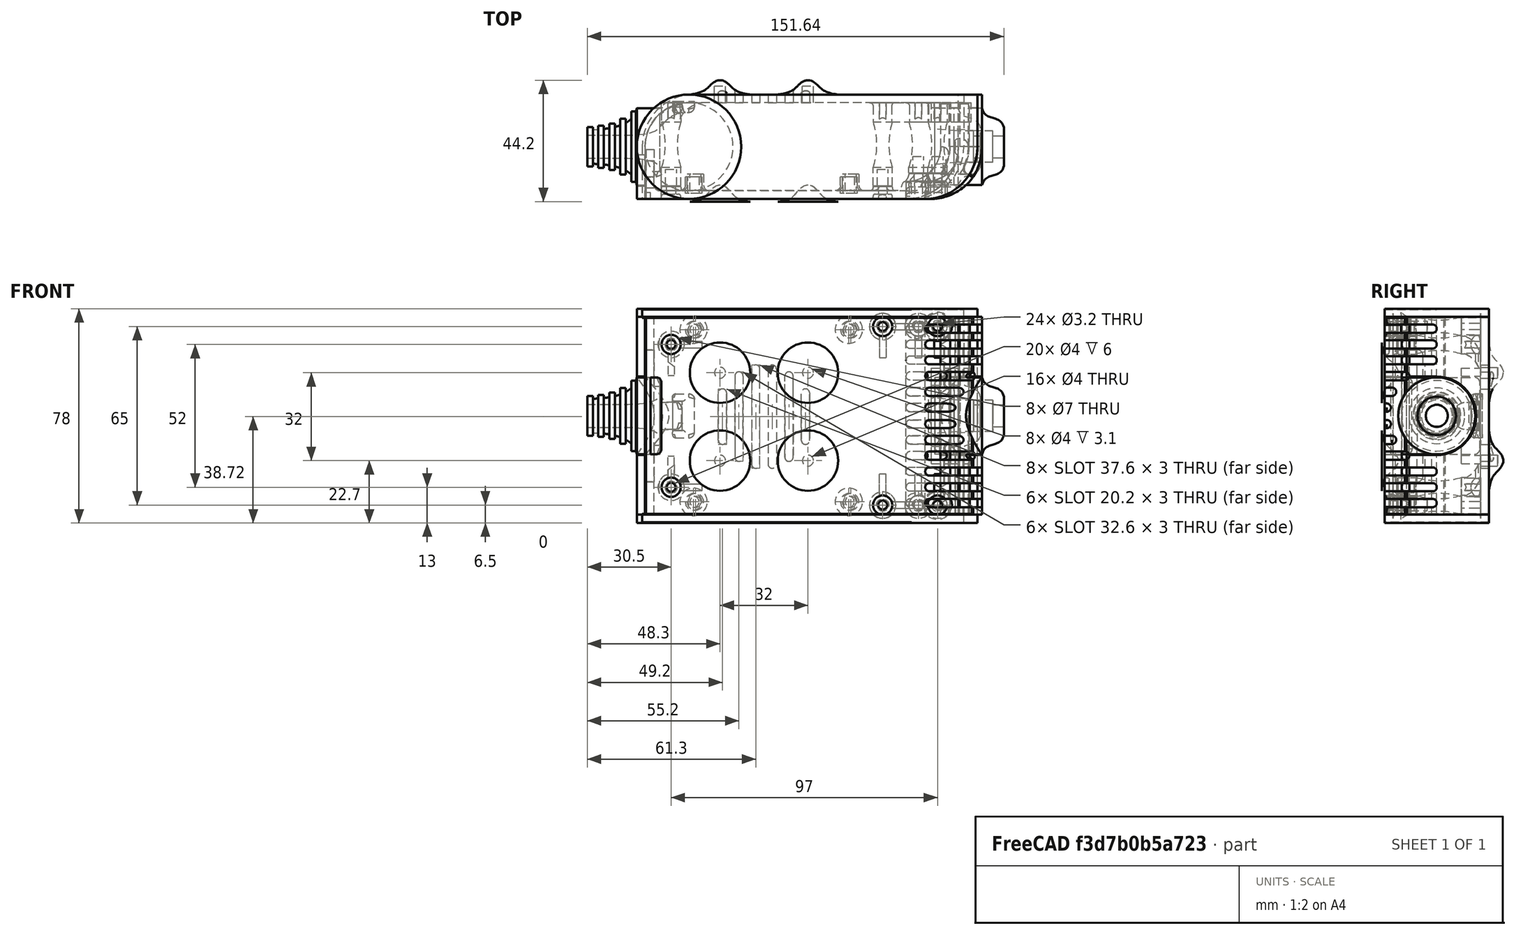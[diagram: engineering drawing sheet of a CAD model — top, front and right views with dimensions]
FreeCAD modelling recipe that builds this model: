
FCSTD DOCUMENT  (FreeCAD 0.19R0.19.2)
Label: enclosure_169FCStd
License: All rights reserved
LicenseURL: http://en.wikipedia.org/wiki/All_rights_reserved
objects: Part::Revolution×146, Part::Feature×140, Part::MultiFuse×134, Sketcher::SketchObject×74, Part::Cylinder×62, Part::Cut×61, Part::Extrusion×59, Part::Fillet×54, Part::Box×36, App::MeasureDistance×4
note: 766 computed .brp shape members not serialized (recipe doc carries the construction recipe); baked Part::Feature solids carry a one-line shape summary decoded from their .brp

FEATURE [Sketcher::SketchObject] Sketch  label="topSketch"
  FullyConstrained = true
  sketch-geometry (20):
    g0: LineSegment StartX=5.21097e-06 StartY=3 StartZ=0 EndX=5.21097e-06 EndY=19 EndZ=0
    g1: ArcOfCircle CenterX=19 CenterY=19 CenterZ=0 NormalX=0 NormalY=0 NormalZ=1 AngleXU=0 Radius=19 StartAngle=1.5708 EndAngle=3.14159
    g2: ArcOfCircle CenterX=19 CenterY=19 CenterZ=0 NormalX=0 NormalY=0 NormalZ=1 AngleXU=0 Radius=16 StartAngle=1.5708 EndAngle=3.14159
    g3: LineSegment StartX=114 StartY=35 StartZ=0 EndX=19 EndY=35 EndZ=0
    g4: LineSegment StartX=5.21097e-06 StartY=3 StartZ=0 EndX=5.21097e-06 EndY=0 EndZ=0
    g5: LineSegment StartX=3 StartY=0 StartZ=0 EndX=5.21097e-06 EndY=0 EndZ=0
    g6: LineSegment StartX=3 StartY=19 StartZ=0 EndX=3 EndY=0 EndZ=0
    g7: LineSegment StartX=19 StartY=38 StartZ=0 EndX=124 EndY=38 EndZ=0
    g8: Circle CenterX=119 CenterY=35 CenterZ=0 NormalX=0 NormalY=0 NormalZ=1 AngleXU=0 Radius=1
    g9: Circle CenterX=121 CenterY=35 CenterZ=0 NormalX=0 NormalY=0 NormalZ=1 AngleXU=0 Radius=1
    g10: Circle CenterX=121 CenterY=33 CenterZ=0 NormalX=0 NormalY=0 NormalZ=1 AngleXU=0 Radius=1
    g11: BSplineCurve PolesCount=3 KnotsCount=2 Degree=2 IsPeriodic=0
    g12: GeomPoint X=119 Y=35 Z=0
    g13: GeomPoint X=121 Y=33 Z=0
    g14: LineSegment StartX=119 StartY=35 StartZ=0 EndX=114 EndY=35 EndZ=0
    g15: ArcOfCircle CenterX=105 CenterY=19 CenterZ=0 NormalX=0 NormalY=0 NormalZ=1 AngleXU=0 Radius=19 StartAngle=5.7297 EndAngle=6.28319
    g16: ArcOfCircle CenterX=105 CenterY=19 CenterZ=0 NormalX=0 NormalY=0 NormalZ=1 AngleXU=0 Radius=16 StartAngle=5.60905 EndAngle=6.28319
    g17: LineSegment StartX=121 StartY=33 StartZ=0 EndX=121 EndY=19 EndZ=0
    g18: LineSegment StartX=124 StartY=38 StartZ=0 EndX=124 EndY=19 EndZ=0
    g19: LineSegment StartX=117.5 StartY=9.01251 StartZ=0 EndX=121.163 EndY=9.0125 EndZ=0
  constraints (46):
    c: Vertical(g0)
    c: Block(g0)
    c: Coincident(g1,g0)
    c: Block(g1)
    c: Coincident(g2,g1)
    c: Block(g2)
    c: Coincident(g3,g2)
    c: Horizontal(g3)
    c: Tangent(g3,g2)
    c: Coincident(g4,g0)
    c: Distance(g4) = 3
    c: Vertical(g4)
    c: Coincident(g5,g4)
    c: Horizontal(g5)
    c: Coincident(g6,g2)
    c: Coincident(g6,g5)
    c: Vertical(g6)
    c: Horizontal(g7)
    c: Distance(g7) = 105
    c: Coincident(g7,g1)
    c: Block(g3)
    c: Weight(g8) = 1
    c: Equal(g8,g9)
    c: Equal(g8,g10)
    c: InternalAlignment(g8,g11)
    c: InternalAlignment(g9,g11)
    c: InternalAlignment(g10,g11)
    c: InternalAlignment(g12,g11)
    c: InternalAlignment(g13,g11)
    c: Block(g11)
    c: Coincident(g14,g11)
    c: Coincident(g14,g3)
    c: Horizontal(g14)
    c: Block(g15)
    c: Coincident(g16,g15)
    c: Block(g16)
    c: Coincident(g17,g11)
    c: Coincident(g17,g16)
    c: Vertical(g17)
    c: Distance(g17) = 14
    c: Coincident(g18,g7)
    c: Coincident(g18,g15)
    c: Vertical(g18)
    c: Distance(g18) = 19
    c: Coincident(g19,g16)
    c: Coincident(g19,g15)
FEATURE [Sketcher::SketchObject] Sketch001  label="bottomSketch"
  FullyConstrained = true
  sketch-geometry (32):
    g0: LineSegment StartX=3.3 StartY=-6.03275e-07 StartZ=0 EndX=98 EndY=-6.03275e-07 EndZ=0
    g1: ArcOfCircle CenterX=98 CenterY=19 CenterZ=0 NormalX=0 NormalY=0 NormalZ=1 AngleXU=0 Radius=19 StartAngle=4.71239 EndAngle=5.71103
    g2: LineSegment StartX=6.3 StartY=8 StartZ=0 EndX=3.3 EndY=8 EndZ=0
    g3: LineSegment StartX=3.3 StartY=8 StartZ=0 EndX=3.3 EndY=-6.03275e-07 EndZ=0
    g4: ArcOfCircle CenterX=8.3 CenterY=5 CenterZ=0 NormalX=0 NormalY=0 NormalZ=1 AngleXU=0 Radius=2 StartAngle=3.14159 EndAngle=4.71239
    g5: LineSegment StartX=6.3 StartY=8 StartZ=0 EndX=6.3 EndY=5 EndZ=0
    g6: ArcOfCircle CenterX=98 CenterY=19 CenterZ=0 NormalX=0 NormalY=0 NormalZ=1 AngleXU=0 Radius=12.7 StartAngle=4.71239 EndAngle=6.28319
    g7: LineSegment StartX=94.7 StartY=3 StartZ=0 EndX=8.3 EndY=3 EndZ=0
    g8-g12: Circle x5 (B-spline internal-alignment scaffolding for g13; pole/knot coordinates omitted)
    g13: BSplineCurve PolesCount=5 KnotsCount=3 Degree=3 IsPeriodic=0
    g14: GeomPoint X=98 Y=6.3 Z=0
    g15: GeomPoint X=96.3938 Y=4.71946 Z=0
    g16: GeomPoint X=94.7 Y=3 Z=0
    g17-g23: Circle x7 (B-spline internal-alignment scaffolding for g24; pole/knot coordinates omitted)
    g24: BSplineCurve PolesCount=7 KnotsCount=5 Degree=3 IsPeriodic=0
    g25-g29: GeomPoint x5 (B-spline internal-alignment scaffolding for g24; pole/knot coordinates omitted)
    g30: ArcOfCircle CenterX=98 CenterY=19 CenterZ=0 NormalX=0 NormalY=0 NormalZ=1 AngleXU=0 Radius=15.7 StartAngle=5.81226 EndAngle=6.28319
    g31: LineSegment StartX=110.7 StartY=19 StartZ=0 EndX=113.7 EndY=19 EndZ=0
  constraints (41):
    c: Horizontal(g0)
    c: Coincident(g1,g0)
    c: Block(g1)
    c: Horizontal(g2)
    c: Distance(g2) = 3
    c: Coincident(g3,g2)
    c: Vertical(g3)
    c: Coincident(g3,g0)
    c: Block(g4)
    c: Block(g2)
    c: Coincident(g5,g2)
    c: Coincident(g5,g4)
    c: Vertical(g5)
    c: Coincident(g6,g1)
    c: Block(g6)
    c: Coincident(g7,g4)
    c: Horizontal(g7)
    c: Block(g0)
    c: Block(g7)
    c: Block(g3)
    c: Coincident(g13,g6)
    c: Weight(g8) = 1
    c: Equal(g8, g9-g12) x4
    c: Coincident(g13,g7)
    c: InternalAlignment(g8-g12 -> g13) x5
    c: InternalAlignment(g14,g13)
    c: InternalAlignment(g15,g13)
    c: InternalAlignment(g16,g13)
    c: Block(g13)
    c: Weight(g17) = 1
    c: Equal(g17, g18-g23) x6
    c: Coincident(g24,g1)
    c: InternalAlignment(g17-g23 -> g24) x7
    c: InternalAlignment(g25-g29 -> g24) x5
    c: Block(g24)
    c: Coincident(g30,g24)
    c: Coincident(g31,g6)
    c: Coincident(g31,g30)
    c: Horizontal(g31)
    c: Block(g31)
    c: Block(g30)
FEATURE [Part::Extrusion] Extrude  label="top"
  Base = -> Sketch
  Dir = (0,0,1)
  DirMode = 2
  FaceMakerClass = Part::FaceMakerBullseye
  LengthFwd = 72
  LengthRev = 0
  Solid = true
  Symmetric = false
FEATURE [Part::Extrusion] Extrude001  label="bottom"
  Base = -> Sketch001
  Dir = (0,0,1)
  DirMode = 2
  FaceMakerClass = Part::FaceMakerBullseye
  LengthFwd = 71.4
  LengthRev = 0
  Placement = pos=(0,0,0.3) rot=(0,0,1;0rad)
  Solid = true
  Symmetric = false
FEATURE [Sketcher::SketchObject] Sketch002  label="topSketch001"
  FullyConstrained = true
  sketch-geometry (6):
    g0: ArcOfCircle CenterX=19 CenterY=19 CenterZ=0 NormalX=0 NormalY=0 NormalZ=1 AngleXU=0 Radius=19 StartAngle=1.5708 EndAngle=3.14159
    g1: LineSegment StartX=5.22862e-06 StartY=19 StartZ=0 EndX=5.22862e-06 EndY=1.19904e-11 EndZ=0
    g2: LineSegment StartX=19 StartY=38 StartZ=0 EndX=124 EndY=38 EndZ=0
    g3: LineSegment StartX=5.22862e-06 StartY=1.19904e-11 StartZ=0 EndX=105 EndY=1.19904e-11 EndZ=0
    g4: ArcOfCircle CenterX=105 CenterY=19 CenterZ=0 NormalX=0 NormalY=0 NormalZ=1 AngleXU=0 Radius=19 StartAngle=4.71239 EndAngle=6.28319
    g5: LineSegment StartX=124 StartY=38 StartZ=0 EndX=124 EndY=19 EndZ=0
  constraints (16):
    c: Block(g0)
    c: Coincident(g1,g0)
    c: Vertical(g1)
    c: Horizontal(g2)
    c: Distance(g2) = 105
    c: Coincident(g2,g0)
    c: Distance(g1) = 19
    c: Coincident(g3,g1)
    c: Horizontal(g3)
    c: Distance(g3) = 105
    c: Block(g4)
    c: Coincident(g4,g3)
    c: Coincident(g5,g2)
    c: Coincident(g5,g4)
    c: Vertical(g5)
    c: Distance(g5) = 19
FEATURE [Part::Extrusion] Extrude002  label="sideA"
  Base = -> Sketch002
  Dir = (0,0,1)
  DirMode = 2
  FaceMakerClass = Part::FaceMakerBullseye
  LengthFwd = 3
  LengthRev = 0
  Placement = pos=(0,0,-3) rot=(0,0,1;0rad)
  Solid = true
  Symmetric = false
FEATURE [Sketcher::SketchObject] Sketch003  label="topSketch002"
  FullyConstrained = true
  sketch-geometry (6):
    g0: LineSegment StartX=19 StartY=38 StartZ=0 EndX=117 EndY=38 EndZ=0
    g1: ArcOfCircle CenterX=19 CenterY=19 CenterZ=0 NormalX=0 NormalY=0 NormalZ=1 AngleXU=0 Radius=19 StartAngle=1.5708 EndAngle=3.14159
    g2: LineSegment StartX=117 StartY=38 StartZ=0 EndX=117 EndY=19 EndZ=0
    g3: LineSegment StartX=98 StartY=1.0161e-12 StartZ=0 EndX=5.22862e-06 EndY=1.0161e-12 EndZ=0
    g4: LineSegment StartX=5.22862e-06 StartY=19 StartZ=0 EndX=5.22862e-06 EndY=1.0161e-12 EndZ=0
    g5: ArcOfCircle CenterX=98 CenterY=19 CenterZ=0 NormalX=0 NormalY=0 NormalZ=1 AngleXU=0 Radius=19 StartAngle=4.71239 EndAngle=6.28319
  constraints (16):
    c: Horizontal(g0)
    c: Distance(g0) = 98
    c: Coincident(g1,g0)
    c: Block(g1)
    c: Coincident(g2,g0)
    c: Vertical(g2)
    c: Distance(g2) = 19
    c: Horizontal(g3)
    c: Coincident(g4,g1)
    c: Vertical(g4)
    c: Coincident(g3,g4)
    c: Block(g3)
    c: Coincident(g5,g2)
    c: Coincident(g5,g3)
    c: Block(g0)
    c: Block(g5)
FEATURE [Sketcher::SketchObject] Sketch004
  FullyConstrained = true
  MapMode = 3
  Placement = pos=(0,0,0) rot=(1,0,0;1.5708rad)
  Support = -> [Extrude]
  sketch-geometry (8):
    g0: Circle CenterX=80.351 CenterY=-67.6202 CenterZ=0 NormalX=0 NormalY=0 NormalZ=1 AngleXU=0 Radius=2
    g1: Circle CenterX=80.351 CenterY=-67.6202 CenterZ=0 NormalX=0 NormalY=0 NormalZ=1 AngleXU=0 Radius=3
    g2: Circle CenterX=80.351 CenterY=-4.92017 CenterZ=0 NormalX=0 NormalY=0 NormalZ=1 AngleXU=0 Radius=2
    g3: Circle CenterX=80.351 CenterY=-4.92017 CenterZ=0 NormalX=0 NormalY=0 NormalZ=1 AngleXU=0 Radius=3
    g4: Circle CenterX=23.851 CenterY=-4.92017 CenterZ=0 NormalX=0 NormalY=0 NormalZ=1 AngleXU=0 Radius=2
    g5: Circle CenterX=23.851 CenterY=-4.92017 CenterZ=0 NormalX=0 NormalY=0 NormalZ=1 AngleXU=0 Radius=3
    g6: Circle CenterX=23.851 CenterY=-67.6202 CenterZ=0 NormalX=0 NormalY=0 NormalZ=1 AngleXU=0 Radius=2
    g7: Circle CenterX=23.851 CenterY=-67.6202 CenterZ=0 NormalX=0 NormalY=0 NormalZ=1 AngleXU=0 Radius=3
  constraints (8):
    c: Block(g3)
    c: Block(g2)
    c: Block(g1)
    c: Block(g0)
    c: Block(g6)
    c: Block(g7)
    c: Block(g4)
    c: Block(g5)
FEATURE [Part::Extrusion] Extrude004
  Base = -> Sketch004
  Dir = (0,-1,2e-16)
  DirMode = 2
  FaceMakerClass = Part::FaceMakerBullseye
  LengthFwd = 6
  LengthRev = 0
  Placement = pos=(0,9,0) rot=(0,0,1;0rad)
  Solid = true
  Symmetric = false
FEATURE [Sketcher::SketchObject] Sketch005
  FullyConstrained = true
  MapMode = 3
  Placement = pos=(0,0,0) rot=(1,0,0;1.5708rad)
  Support = -> [Extrude]
  sketch-geometry (8):
    g0: Circle CenterX=80.351 CenterY=-67.6202 CenterZ=0 NormalX=0 NormalY=0 NormalZ=1 AngleXU=0 Radius=3
    g1: Circle CenterX=80.351 CenterY=-4.92017 CenterZ=0 NormalX=0 NormalY=0 NormalZ=1 AngleXU=0 Radius=3
    g2: Circle CenterX=23.851 CenterY=-4.92017 CenterZ=0 NormalX=0 NormalY=0 NormalZ=1 AngleXU=0 Radius=3
    g3: Circle CenterX=23.851 CenterY=-67.6202 CenterZ=0 NormalX=0 NormalY=0 NormalZ=1 AngleXU=0 Radius=3
    g4: Circle CenterX=23.851 CenterY=-67.6202 CenterZ=0 NormalX=0 NormalY=0 NormalZ=1 AngleXU=0 Radius=5
    g5: Circle CenterX=80.351 CenterY=-67.6202 CenterZ=0 NormalX=0 NormalY=0 NormalZ=1 AngleXU=0 Radius=5
    g6: Circle CenterX=23.851 CenterY=-4.92017 CenterZ=0 NormalX=0 NormalY=0 NormalZ=1 AngleXU=0 Radius=5
    g7: Circle CenterX=80.351 CenterY=-4.92017 CenterZ=0 NormalX=0 NormalY=0 NormalZ=1 AngleXU=0 Radius=5
  constraints (8):
    c: Block(g1)
    c: Block(g0)
    c: Block(g3)
    c: Block(g2)
    c: Block(g5)
    c: Block(g4)
    c: Block(g6)
    c: Block(g7)
FEATURE [Part::Extrusion] Extrude005
  Base = -> Sketch005
  Dir = (0,-1,2e-16)
  DirMode = 2
  FaceMakerClass = Part::FaceMakerBullseye
  LengthFwd = 2
  LengthRev = 0
  Solid = true
  Symmetric = false
FEATURE [Sketcher::SketchObject] Sketch006
  FullyConstrained = true
  MapMode = 3
  Placement = pos=(0,0,0) rot=(1,0,0;1.5708rad)
  sketch-geometry (8):
    g0: Circle CenterX=80.351 CenterY=-67.6202 CenterZ=0 NormalX=0 NormalY=0 NormalZ=1 AngleXU=0 Radius=3
    g1: Circle CenterX=80.351 CenterY=-4.92017 CenterZ=0 NormalX=0 NormalY=0 NormalZ=1 AngleXU=0 Radius=3
    g2: Circle CenterX=23.851 CenterY=-4.92017 CenterZ=0 NormalX=0 NormalY=0 NormalZ=1 AngleXU=0 Radius=3
    g3: Circle CenterX=23.851 CenterY=-67.6202 CenterZ=0 NormalX=0 NormalY=0 NormalZ=1 AngleXU=0 Radius=3
    g4: Circle CenterX=23.851 CenterY=-67.6202 CenterZ=0 NormalX=0 NormalY=0 NormalZ=1 AngleXU=0 Radius=5
    g5: Circle CenterX=80.351 CenterY=-67.6202 CenterZ=0 NormalX=0 NormalY=0 NormalZ=1 AngleXU=0 Radius=5
    g6: Circle CenterX=23.851 CenterY=-4.92017 CenterZ=0 NormalX=0 NormalY=0 NormalZ=1 AngleXU=0 Radius=5
    g7: Circle CenterX=80.351 CenterY=-4.92017 CenterZ=0 NormalX=0 NormalY=0 NormalZ=1 AngleXU=0 Radius=5
  constraints (8):
    c: Block(g1)
    c: Block(g0)
    c: Block(g3)
    c: Block(g2)
    c: Block(g5)
    c: Block(g4)
    c: Block(g6)
    c: Block(g7)
FEATURE [Part::Extrusion] Extrude007
  Base = -> Sketch006
  Dir = (0,-1,2e-16)
  DirMode = 2
  FaceMakerClass = Part::FaceMakerBullseye
  LengthFwd = 2
  LengthRev = 0
  Solid = true
  Symmetric = false
FEATURE [Part::Fillet] Fillet
  Base = -> Extrude007
  Edges = 4 edges r=1.99: [Edge6,Edge12,Edge18,Edge24]
FEATURE [Part::Cut] Cut
  Base = -> Extrude005
  Placement = pos=(0,5,0) rot=(0,0,1;0rad)
  Tool = -> Fillet
FEATURE [Part::MultiFuse] Fusion  label="pCBScrews"
  Placement = pos=(-2.5,0,72.3) rot=(0,0,1;0rad)
  Shapes = -> [Extrude004,Cut]
FEATURE [App::MeasureDistance] Distance  label="Distance: 0.69 mm"
  Distance = 0.685967
  P1 = (24.0138,2.9647,0.3)
  P2 = (23.8901,3,-0.373787)
FEATURE [App::MeasureDistance] Distance001  label="Distance: 0.53 mm"
  Distance = 0.533607
  P1 = (80.2939,3,72.2334)
  P2 = (80.281,2.99661,71.7)
FEATURE [Part::Fillet] Fillet001
  Base = -> Extrude001
  Edges = 1 edges r=2.4: [Edge17]
FEATURE [Part::Fillet] Fillet002  label="bottom001"
  Base = -> Fillet001
  Edges = 1 edges r=2.4: [Edge36]
FEATURE [Part::Fillet] Fillet003  label="top001"
  Base = -> Extrude
  Edges = 1 edges r=2: [Edge1]
FEATURE [Sketcher::SketchObject] Sketch007
  FullyConstrained = true
  sketch-geometry (16):
    g0: LineSegment StartX=4 StartY=0 StartZ=0 EndX=4 EndY=2.4 EndZ=0
    g1: LineSegment StartX=4 StartY=2.4 StartZ=0 EndX=7 EndY=2.4 EndZ=0
    g2: LineSegment StartX=4 StartY=0 StartZ=0 EndX=5.7 EndY=0 EndZ=0
    g3: LineSegment StartX=5.7 StartY=0 StartZ=0 EndX=5.7 EndY=-5.6 EndZ=0
    g4-g8: Circle x5 (B-spline internal-alignment scaffolding for g9; pole/knot coordinates omitted)
    g9: BSplineCurve PolesCount=5 KnotsCount=3 Degree=3 IsPeriodic=0
    g10: GeomPoint X=7 Y=2.4 Z=0
    g11: GeomPoint X=10.4582 Y=-1.55472 Z=0
    g12: GeomPoint X=14 Y=-5.6 Z=0
    g13: LineSegment StartX=14 StartY=-5.6 StartZ=0 EndX=14 EndY=-14.1 EndZ=0
    g14: LineSegment StartX=14 StartY=-14.1 StartZ=0 EndX=6.5 EndY=-14.1 EndZ=0
    g15: LineSegment StartX=5.7 StartY=-5.6 StartZ=0 EndX=6.5 EndY=-14.1 EndZ=0
  constraints (28):
    c: Distance(g0) = 2.4
    c: Vertical(g0)
    c: Block(g0)
    c: Coincident(g1,g0)
    c: Horizontal(g1)
    c: Distance(g1) = 3
    c: Coincident(g2,g0)
    c: Horizontal(g2)
    c: Distance(g2) = 1.7
    c: Coincident(g3,g2)
    c: Vertical(g3)
    c: Distance(g3) = 5.6
    c: Coincident(g9,g1)
    c: Weight(g4) = 1
    c: Equal(g4, g5-g8) x4
    c: InternalAlignment(g4-g8 -> g9) x5
    c: InternalAlignment(g10,g9)
    c: InternalAlignment(g11,g9)
    c: InternalAlignment(g12,g9)
    c: Block(g9)
    c: Coincident(g13,g9)
    c: Vertical(g13)
    c: Distance(g13) = 8.5
    c: Coincident(g14,g13)
    c: Horizontal(g14)
    c: Distance(g14) = 7.5
    c: Coincident(g15,g3)
    c: Coincident(g15,g14)
FEATURE [Part::Feature] Face
  shape: bbox 10 x 16.5 x 2e-07 mm, 1 faces, 0 solids (baked)
FEATURE [Part::Revolution] Revolve  label="plugHousing"
  Angle = 360
  Axis = (0,1,0)
  Base = (0,0,0)
  FaceMakerClass = Part::FaceMakerBullseye
  Placement = pos=(0,0,36.15) rot=(0,0,1;0rad)
  Solid = false
  Source = -> Face
  Symmetric = false
FEATURE [Part::Feature] Face001
  shape: bbox 10 x 16.5 x 2e-07 mm, 1 faces, 0 solids (baked)
FEATURE [Part::Revolution] Revolve001  label="plugHousing001"
  Angle = 360
  Axis = (0,1,0)
  Base = (0,0,0)
  FaceMakerClass = Part::FaceMakerBullseye
  Placement = pos=(0,0,36.15) rot=(0,0,1;0rad)
  Solid = false
  Source = -> Face001
  Symmetric = false
FEATURE [Part::MultiFuse] Fusion001  label="plugHousing002"
  Placement = pos=(0,0,0) rot=(0,0,1;1.5708rad)
  Shapes = -> [Revolve001,Revolve]
FEATURE [Part::Feature] Face002
  shape: bbox 10 x 16.5 x 2e-07 mm, 1 faces, 0 solids (baked)
FEATURE [Part::Revolution] Revolve003  label="plugHousing005"
  Angle = 360
  Axis = (0,1,0)
  Base = (0,0,0)
  FaceMakerClass = Part::FaceMakerBullseye
  Placement = pos=(0,0,36.15) rot=(0,0,1;0rad)
  Solid = false
  Source = -> Face002
  Symmetric = false
FEATURE [Part::Feature] Face003
  shape: bbox 10 x 16.5 x 2e-07 mm, 1 faces, 0 solids (baked)
FEATURE [Part::Revolution] Revolve002  label="plugHousing003"
  Angle = 360
  Axis = (0,1,0)
  Base = (0,0,0)
  FaceMakerClass = Part::FaceMakerBullseye
  Placement = pos=(0,0,36.15) rot=(0,0,1;0rad)
  Solid = false
  Source = -> Face003
  Symmetric = false
FEATURE [Part::MultiFuse] Fusion002  label="plugHousing004"
  Placement = pos=(0,0,0) rot=(0,0,1;1.5708rad)
  Shapes = -> [Revolve002,Revolve003]
FEATURE [Part::MultiFuse] Fusion003  label="plugHousing006"
  Placement = pos=(0,19,0) rot=(0,0,1;3.14159rad)
  Shapes = -> [Fusion002,Fusion001]
FEATURE [Part::Feature] Face004
  shape: bbox 10 x 16.5 x 2e-07 mm, 1 faces, 0 solids (baked)
FEATURE [Part::Revolution] Revolve006  label="plugHousing010"
  Angle = 360
  Axis = (0,1,0)
  Base = (0,0,0)
  FaceMakerClass = Part::FaceMakerBullseye
  Placement = pos=(0,0,36.15) rot=(0,0,1;0rad)
  Solid = false
  Source = -> Face004
  Symmetric = false
FEATURE [Part::Feature] Face005
  shape: bbox 10 x 16.5 x 2e-07 mm, 1 faces, 0 solids (baked)
FEATURE [Part::Revolution] Revolve007  label="plugHousing011"
  Angle = 360
  Axis = (0,1,0)
  Base = (0,0,0)
  FaceMakerClass = Part::FaceMakerBullseye
  Placement = pos=(0,0,36.15) rot=(0,0,1;0rad)
  Solid = false
  Source = -> Face005
  Symmetric = false
FEATURE [Part::Feature] Face006
  shape: bbox 10 x 16.5 x 2e-07 mm, 1 faces, 0 solids (baked)
FEATURE [Part::Revolution] Revolve004  label="plugHousing007"
  Angle = 360
  Axis = (0,1,0)
  Base = (0,0,0)
  FaceMakerClass = Part::FaceMakerBullseye
  Placement = pos=(0,0,36.15) rot=(0,0,1;0rad)
  Solid = false
  Source = -> Face006
  Symmetric = false
FEATURE [Part::MultiFuse] Fusion004  label="plugHousing009"
  Placement = pos=(0,0,0) rot=(0,0,1;1.5708rad)
  Shapes = -> [Revolve004,Revolve007]
FEATURE [Part::Feature] Face007
  shape: bbox 10 x 16.5 x 2e-07 mm, 1 faces, 0 solids (baked)
FEATURE [Part::Revolution] Revolve005  label="plugHousing008"
  Angle = 360
  Axis = (0,1,0)
  Base = (0,0,0)
  FaceMakerClass = Part::FaceMakerBullseye
  Placement = pos=(0,0,36.15) rot=(0,0,1;0rad)
  Solid = false
  Source = -> Face007
  Symmetric = false
FEATURE [Part::MultiFuse] Fusion005  label="plugHousing012"
  Placement = pos=(0,0,0) rot=(0,0,1;1.5708rad)
  Shapes = -> [Revolve006,Revolve005]
FEATURE [Part::MultiFuse] Fusion006  label="plugHousing013"
  Placement = pos=(0,19,0) rot=(0,0,1;3.14159rad)
  Shapes = -> [Fusion005,Fusion004]
FEATURE [Part::MultiFuse] Fusion007  label="plugHousing014"
  Placement = pos=(122.621,0,-0.15) rot=(0,0,1;0rad)
  Shapes = -> [Fusion003,Fusion006]
FEATURE [Part::Cylinder] Cylinder002
  Angle = 360
  AttacherType = Attacher::AttachEngine3D
  Height = 20
  Placement = pos=(0,0,36.15) rot=(0,0,1;0rad)
  Radius = 4
FEATURE [Part::Cylinder] Cylinder003
  Angle = 360
  AttacherType = Attacher::AttachEngine3D
  Height = 10
  Placement = pos=(0,0,36.15) rot=(0,0,1;0rad)
  Radius = 4
FEATURE [Part::MultiFuse] Fusion009  label="removeToCreateHoleForPlugHousing"
  Placement = pos=(70,19,36.15) rot=(0,1,0;1.5708rad)
  Shapes = -> [Cylinder002,Cylinder003]
FEATURE [Part::Cylinder] Cylinder004
  Angle = 360
  AttacherType = Attacher::AttachEngine3D
  Height = 20
  Placement = pos=(0,0,36.15) rot=(0,0,1;0rad)
  Radius = 4
FEATURE [Part::Cylinder] Cylinder005
  Angle = 360
  AttacherType = Attacher::AttachEngine3D
  Height = 10
  Placement = pos=(0,0,36.15) rot=(0,0,1;0rad)
  Radius = 4
FEATURE [Part::MultiFuse] Fusion010  label="removeToCreateHoleForPlugHousing001"
  Placement = pos=(70,19,36.15) rot=(0,1,0;1.5708rad)
  Shapes = -> [Cylinder004,Cylinder005]
FEATURE [Part::Cut] Cut001
  Base = -> Fillet003
  Tool = -> Fusion010
FEATURE [Part::Cut] Cut002  label="Bottom"
  Base = -> Fillet002
  Tool = -> Fusion009
FEATURE [Part::Feature] Face008
  shape: bbox 10 x 16.5 x 2e-07 mm, 1 faces, 0 solids (baked)
FEATURE [Part::Revolution] Revolve011  label="plugHousing021"
  Angle = 360
  Axis = (0,1,0)
  Base = (0,0,0)
  FaceMakerClass = Part::FaceMakerBullseye
  Placement = pos=(0,0,36.15) rot=(0,0,1;0rad)
  Solid = false
  Source = -> Face008
  Symmetric = false
FEATURE [Part::Feature] Face009
  shape: bbox 10 x 16.5 x 2e-07 mm, 1 faces, 0 solids (baked)
FEATURE [Part::Revolution] Revolve012  label="plugHousing022"
  Angle = 360
  Axis = (0,1,0)
  Base = (0,0,0)
  FaceMakerClass = Part::FaceMakerBullseye
  Placement = pos=(0,0,36.15) rot=(0,0,1;0rad)
  Solid = false
  Source = -> Face009
  Symmetric = false
FEATURE [Part::Feature] Face010 .. Face013  x4 (patterned run collapsed; names and placements below)
  shape: bbox 10 x 16.5 x 2e-07 mm, 1 faces, 0 solids (baked)
FEATURE [Part::Revolution] Revolve015  label="plugHousing027"
  Angle = 360
  Axis = (0,1,0)
  Base = (0,0,0)
  FaceMakerClass = Part::FaceMakerBullseye
  Placement = pos=(0,0,36.15) rot=(0,0,1;0rad)
  Solid = false
  Source = -> Face013
  Symmetric = false
FEATURE [Part::Feature] Face014
  shape: bbox 10 x 16.5 x 2e-07 mm, 1 faces, 0 solids (baked)
FEATURE [Part::Feature] Face015
  shape: bbox 10 x 16.5 x 2e-07 mm, 1 faces, 0 solids (baked)
FEATURE [Part::Feature] Face016
  shape: bbox 10 x 16.5 x 2e-07 mm, 1 faces, 0 solids (baked)
FEATURE [Part::Revolution] Revolve019  label="plugHousing033"
  Angle = 360
  Axis = (0,1,0)
  Base = (0,0,0)
  FaceMakerClass = Part::FaceMakerBullseye
  Placement = pos=(0,0,36.15) rot=(0,0,1;0rad)
  Solid = false
  Source = -> Face016
  Symmetric = false
FEATURE [Part::Feature] Face017
  shape: bbox 10 x 16.5 x 2e-07 mm, 1 faces, 0 solids (baked)
FEATURE [Part::Revolution] Revolve020  label="plugHousing034"
  Angle = 360
  Axis = (0,1,0)
  Base = (0,0,0)
  FaceMakerClass = Part::FaceMakerBullseye
  Placement = pos=(0,0,36.15) rot=(0,0,1;0rad)
  Solid = false
  Source = -> Face017
  Symmetric = false
FEATURE [Part::Feature] Face018
  shape: bbox 10 x 16.5 x 2e-07 mm, 1 faces, 0 solids (baked)
FEATURE [Part::Revolution] Revolve016  label="plugHousing030"
  Angle = 360
  Axis = (0,1,0)
  Base = (0,0,0)
  FaceMakerClass = Part::FaceMakerBullseye
  Placement = pos=(0,0,36.15) rot=(0,0,1;0rad)
  Solid = false
  Source = -> Face018
  Symmetric = false
FEATURE [Part::MultiFuse] Fusion020  label="plugHousing038"
  Placement = pos=(0,0,0) rot=(0,0,1;1.5708rad)
  Shapes = -> [Revolve016,Revolve020]
FEATURE [Part::Feature] Face019
  shape: bbox 10 x 16.5 x 2e-07 mm, 1 faces, 0 solids (baked)
FEATURE [Part::Feature] Face020
  shape: bbox 10 x 16.5 x 2e-07 mm, 1 faces, 0 solids (baked)
FEATURE [Part::Revolution] Revolve017  label="plugHousing031"
  Angle = 360
  Axis = (0,1,0)
  Base = (0,0,0)
  FaceMakerClass = Part::FaceMakerBullseye
  Placement = pos=(0,0,36.15) rot=(0,0,1;0rad)
  Solid = false
  Source = -> Face020
  Symmetric = false
FEATURE [Part::MultiFuse] Fusion021  label="plugHousing039"
  Placement = pos=(0,0,0) rot=(0,0,1;1.5708rad)
  Shapes = -> [Revolve019,Revolve017]
FEATURE [Part::MultiFuse] Fusion023  label="plugHousing041"
  Placement = pos=(0,19,0) rot=(0,0,1;3.14159rad)
  Shapes = -> [Fusion021,Fusion020]
FEATURE [Part::Revolution] Revolve022  label="plugHousing043"
  Angle = 360
  Axis = (0,1,0)
  Base = (0,0,0)
  FaceMakerClass = Part::FaceMakerBullseye
  Placement = pos=(0,0,36.15) rot=(0,0,1;0rad)
  Solid = false
  Source = -> Face019
  Symmetric = false
FEATURE [Part::Feature] Face021
  shape: bbox 10 x 16.5 x 2e-07 mm, 1 faces, 0 solids (baked)
FEATURE [Part::Revolution] Revolve023  label="plugHousing044"
  Angle = 360
  Axis = (0,1,0)
  Base = (0,0,0)
  FaceMakerClass = Part::FaceMakerBullseye
  Placement = pos=(0,0,36.15) rot=(0,0,1;0rad)
  Solid = false
  Source = -> Face021
  Symmetric = false
FEATURE [Part::Feature] Face022
  shape: bbox 10 x 16.5 x 2e-07 mm, 1 faces, 0 solids (baked)
FEATURE [Part::Revolution] Revolve018  label="plugHousing032"
  Angle = 360
  Axis = (0,1,0)
  Base = (0,0,0)
  FaceMakerClass = Part::FaceMakerBullseye
  Placement = pos=(0,0,36.15) rot=(0,0,1;0rad)
  Solid = false
  Source = -> Face022
  Symmetric = false
FEATURE [Part::MultiFuse] Fusion022  label="plugHousing040"
  Placement = pos=(0,0,0) rot=(0,0,1;1.5708rad)
  Shapes = -> [Revolve018,Revolve023]
FEATURE [Part::Feature] Face023
  shape: bbox 10 x 16.5 x 2e-07 mm, 1 faces, 0 solids (baked)
FEATURE [Part::Revolution] Revolve021  label="plugHousing035"
  Angle = 360
  Axis = (0,1,0)
  Base = (0,0,0)
  FaceMakerClass = Part::FaceMakerBullseye
  Placement = pos=(0,0,36.15) rot=(0,0,1;0rad)
  Solid = false
  Source = -> Face023
  Symmetric = false
FEATURE [Part::MultiFuse] Fusion018  label="plugHousing036"
  Placement = pos=(0,0,0) rot=(0,0,1;1.5708rad)
  Shapes = -> [Revolve022,Revolve021]
FEATURE [Part::MultiFuse] Fusion019  label="plugHousing037"
  Placement = pos=(0,19,0) rot=(0,0,1;3.14159rad)
  Shapes = -> [Fusion018,Fusion022]
FEATURE [Part::MultiFuse] Fusion024  label="plugHousing042"
  Placement = pos=(122.621,0,-0.15) rot=(0,0,1;0rad)
  Shapes = -> [Fusion023,Fusion019]
FEATURE [Part::Cylinder] Cylinder006
  Angle = 360
  AttacherType = Attacher::AttachEngine3D
  Height = 20
  Placement = pos=(0,0,36.15) rot=(0,0,1;0rad)
  Radius = 14.3
FEATURE [Part::Cylinder] Cylinder007
  Angle = 360
  AttacherType = Attacher::AttachEngine3D
  Height = 10
  Placement = pos=(0,0,36.15) rot=(0,0,1;0rad)
  Radius = 4
FEATURE [Part::MultiFuse] Fusion026  label="removeToCreteHoleForPlugHousing"
  Placement = pos=(70,19,36) rot=(0,1,0;1.5708rad)
  Shapes = -> [Cylinder006,Cylinder007]
FEATURE [Part::Box] Box001  label="Cube001"
  AttacherType = Attacher::AttachEngine3D
  Height = 28
  Length = 3
  Placement = pos=(110.7,19,22) rot=(0,0,1;0rad)
  Width = 15.7
FEATURE [Part::Cut] Cut003  label="top002"
  Base = -> Cut001
  Tool = -> Fusion007
FEATURE [Part::Revolution] Revolve008  label="plugHousing015"
  Angle = 360
  Axis = (0,1,0)
  Base = (0,0,0)
  FaceMakerClass = Part::FaceMakerBullseye
  Placement = pos=(0,0,36.15) rot=(0,0,1;0rad)
  Solid = false
  Source = -> Face010
  Symmetric = false
FEATURE [Part::MultiFuse] Fusion013  label="plugHousing020"
  Placement = pos=(0,0,0) rot=(0,0,1;1.5708rad)
  Shapes = -> [Revolve008,Revolve012]
FEATURE [Part::Cut] Cut004  label="top003"
  Base = -> Cut003
  Placement = pos=(1,0,0) rot=(0,0,1;0rad)
  Tool = -> Fusion026
FEATURE [Part::Cylinder] Cylinder008
  Angle = 360
  AttacherType = Attacher::AttachEngine3D
  Height = 20
  Placement = pos=(0,0,36.15) rot=(0,0,1;0rad)
  Radius = 10.3
FEATURE [Part::Cylinder] Cylinder009
  Angle = 360
  AttacherType = Attacher::AttachEngine3D
  Height = 10
  Placement = pos=(0,0,36.15) rot=(0,0,1;0rad)
  Radius = 4
FEATURE [Part::MultiFuse] Fusion027  label="removeToCreteHoleForPlugHousing001"
  Placement = pos=(70,19,36) rot=(0,1,0;1.5708rad)
  Shapes = -> [Cylinder008,Cylinder009]
FEATURE [Part::Cut] Cut005  label="plugHousingTab"
  Base = -> Box001
  Tool = -> Fusion027
FEATURE [Part::MultiFuse] Fusion028  label="plugHousing045"
  Shapes = -> [Fusion024,Cut005]
FEATURE [Part::Box] Box002  label="Cube002"
  AttacherType = Attacher::AttachEngine3D
  Height = 28.8
  Length = 3
  Placement = pos=(107.3,28,21.6) rot=(0,0,1;0rad)
  Width = 7
FEATURE [Part::Box] Box003  label="Cube003"
  AttacherType = Attacher::AttachEngine3D
  Height = 3
  Length = 6.4
  Placement = pos=(107.3,28,18.6) rot=(0,0,1;0rad)
  Width = 7
FEATURE [Part::Box] Box004  label="Cube004"
  AttacherType = Attacher::AttachEngine3D
  Height = 3
  Length = 6.4
  Placement = pos=(107.3,28,50.4) rot=(0,0,1;0rad)
  Width = 7
FEATURE [Part::MultiFuse] Fusion029  label="plugHousingBracketHolder"
  Shapes = -> [Box004,Box002,Box003]
FEATURE [Part::Cylinder] Cylinder010
  Angle = 360
  AttacherType = Attacher::AttachEngine3D
  Height = 20
  Placement = pos=(0,0,36.15) rot=(0,0,1;0rad)
  Radius = 14.3
FEATURE [Part::Cylinder] Cylinder011
  Angle = 360
  AttacherType = Attacher::AttachEngine3D
  Height = 10
  Placement = pos=(0,0,36.15) rot=(0,0,1;0rad)
  Radius = 4
FEATURE [Part::MultiFuse] Fusion030  label="removeToCreteHoleForPlugHousing002"
  Placement = pos=(70,19,36) rot=(0,1,0;1.5708rad)
  Shapes = -> [Cylinder010,Cylinder011]
FEATURE [Part::Cut] Cut006  label="plugHousingBracketHolder001"
  Base = -> Fusion029
  Tool = -> Fusion030
FEATURE [Part::Cylinder] Cylinder012
  Angle = 360
  AttacherType = Attacher::AttachEngine3D
  Height = 20
  Placement = pos=(0,0,36.15) rot=(0,0,1;0rad)
  Radius = 7
FEATURE [Part::Cylinder] Cylinder013
  Angle = 360
  AttacherType = Attacher::AttachEngine3D
  Height = 10
  Placement = pos=(0,0,36.15) rot=(0,0,1;0rad)
  Radius = 4
FEATURE [Part::MultiFuse] Fusion032  label="removeToCreteHoleForPlugHousing003"
  Placement = pos=(70,19,36) rot=(0,1,0;1.5708rad)
  Shapes = -> [Cylinder012,Cylinder013]
FEATURE [Part::Cut] Cut007  label="bottom002"
  Base = -> Cut002
  Tool = -> Fusion032
FEATURE [Sketcher::SketchObject] Sketch008
  FullyConstrained = true
  sketch-geometry (54):
    g0: LineSegment StartX=-4.2 StartY=0 StartZ=0 EndX=-6.2 EndY=0 EndZ=0
    g1: LineSegment StartX=-14 StartY=-18 StartZ=0 EndX=-14 EndY=-26.5 EndZ=0
    g2: LineSegment StartX=-4.2 StartY=0 StartZ=0 EndX=-4.2 EndY=-13.4877 EndZ=0
    g3: Circle CenterX=-4.2 CenterY=-13.4877 CenterZ=0 NormalX=0 NormalY=0 NormalZ=1 AngleXU=0 Radius=1
    g4: Circle CenterX=-4.2 CenterY=-26.5 CenterZ=0 NormalX=0 NormalY=0 NormalZ=1 AngleXU=0 Radius=1
    g5: Circle CenterX=-8.2 CenterY=-26.5 CenterZ=0 NormalX=0 NormalY=0 NormalZ=1 AngleXU=0 Radius=1
    g6: BSplineCurve PolesCount=3 KnotsCount=2 Degree=2 IsPeriodic=0
    g7: GeomPoint X=-4.2 Y=-13.4877 Z=0
    g8: GeomPoint X=-8.2 Y=-26.5 Z=0
    g9: LineSegment StartX=-14 StartY=-26.5 StartZ=0 EndX=-8.2 EndY=-26.5 EndZ=0
    g10: LineSegment StartX=-10.15 StartY=-12 StartZ=0 EndX=-10.15 EndY=-14 EndZ=0
    g11: LineSegment StartX=-12.8401 StartY=-16 StartZ=0 EndX=-10.1571 EndY=-16 EndZ=0
    g12: LineSegment StartX=-10.15 StartY=-14 StartZ=0 EndX=-8.70761 EndY=-14 EndZ=0
    g13: LineSegment StartX=-12.8401 StartY=-16 StartZ=0 EndX=-12.8401 EndY=-17.6958 EndZ=0
    g14: LineSegment StartX=-10.15 StartY=-12 StartZ=0 EndX=-7.79258 EndY=-12 EndZ=0
    g15: Circle CenterX=-6.2215 CenterY=-2 CenterZ=0 NormalX=0 NormalY=0 NormalZ=1 AngleXU=0 Radius=1
    g16: Circle CenterX=-6.22762 CenterY=-2.58724 CenterZ=0 NormalX=0 NormalY=0 NormalZ=1 AngleXU=0 Radius=1
    g17: Circle CenterX=-6.32538 CenterY=-4 CenterZ=0 NormalX=0 NormalY=0 NormalZ=1 AngleXU=0 Radius=1
    g18: BSplineCurve PolesCount=3 KnotsCount=2 Degree=2 IsPeriodic=0
    g19: GeomPoint X=-6.2215 Y=-2 Z=0
    g20: GeomPoint X=-6.32538 Y=-4 Z=0
    g21: Circle CenterX=-6.48644 CenterY=-5.99526 CenterZ=0 NormalX=0 NormalY=0 NormalZ=1 AngleXU=0 Radius=1
    g22: Circle CenterX=-6.58486 CenterY=-6.99526 CenterZ=0 NormalX=0 NormalY=0 NormalZ=1 AngleXU=0 Radius=1
    g23: Circle CenterX=-6.77343 CenterY=-8 CenterZ=0 NormalX=0 NormalY=0 NormalZ=1 AngleXU=0 Radius=1
    g24: BSplineCurve PolesCount=3 KnotsCount=2 Degree=2 IsPeriodic=0
    g25: GeomPoint X=-6.48644 Y=-5.99526 Z=0
    g26: GeomPoint X=-6.77343 Y=-8 Z=0
    g27: Circle CenterX=-7.19003 CenterY=-10 CenterZ=0 NormalX=0 NormalY=0 NormalZ=1 AngleXU=0 Radius=1
    g28: Circle CenterX=-7.44407 CenterY=-11.0915 CenterZ=0 NormalX=0 NormalY=0 NormalZ=1 AngleXU=0 Radius=1
    g29: Circle CenterX=-7.79258 CenterY=-12 CenterZ=0 NormalX=0 NormalY=0 NormalZ=1 AngleXU=0 Radius=1
    g30: BSplineCurve PolesCount=3 KnotsCount=2 Degree=2 IsPeriodic=0
    g31: GeomPoint X=-7.19003 Y=-10 Z=0
    g32: GeomPoint X=-7.79258 Y=-12 Z=0
    g33: Circle CenterX=-8.70761 CenterY=-14 CenterZ=0 NormalX=0 NormalY=0 NormalZ=1 AngleXU=0 Radius=1
    g34: Circle CenterX=-9.33087 CenterY=-15.1837 CenterZ=0 NormalX=0 NormalY=0 NormalZ=1 AngleXU=0 Radius=1
    g35: Circle CenterX=-10.1571 CenterY=-16 CenterZ=0 NormalX=0 NormalY=0 NormalZ=1 AngleXU=0 Radius=1
    g36: BSplineCurve PolesCount=3 KnotsCount=2 Degree=2 IsPeriodic=0
    g37: GeomPoint X=-8.70761 Y=-14 Z=0
    g38: GeomPoint X=-10.1571 Y=-16 Z=0
    g39: Circle CenterX=-12.8401 CenterY=-17.6958 CenterZ=0 NormalX=0 NormalY=0 NormalZ=1 AngleXU=0 Radius=1
    g40: Circle CenterX=-13.3521 CenterY=-17.9027 CenterZ=0 NormalX=0 NormalY=0 NormalZ=1 AngleXU=0 Radius=1
    g41: Circle CenterX=-14 CenterY=-18 CenterZ=0 NormalX=0 NormalY=0 NormalZ=1 AngleXU=0 Radius=1
    g42: BSplineCurve PolesCount=3 KnotsCount=2 Degree=2 IsPeriodic=0
    g43: GeomPoint X=-12.8401 Y=-17.6958 Z=0
    g44: GeomPoint X=-14 Y=-18 Z=0
    g45: LineSegment StartX=-6.2 StartY=0 StartZ=0 EndX=-7.2 EndY=0 EndZ=0
    g46: LineSegment StartX=-7.2 StartY=0 StartZ=0 EndX=-7.2 EndY=-2 EndZ=0
    g47: LineSegment StartX=-7.2 StartY=-2 StartZ=0 EndX=-6.2215 EndY=-2 EndZ=0
    g48: LineSegment StartX=-6.32538 StartY=-4 StartZ=0 EndX=-7.65538 EndY=-4 EndZ=0
    g49: LineSegment StartX=-7.65538 StartY=-4 StartZ=0 EndX=-7.65538 EndY=-5.99526 EndZ=0
    g50: LineSegment StartX=-7.65538 StartY=-5.99526 StartZ=0 EndX=-6.48644 EndY=-5.99526 EndZ=0
    g51: LineSegment StartX=-6.77343 StartY=-8 StartZ=0 EndX=-8.43343 EndY=-8 EndZ=0
    g52: LineSegment StartX=-8.43343 StartY=-8 StartZ=0 EndX=-8.43343 EndY=-10 EndZ=0
    g53: LineSegment StartX=-8.43343 StartY=-10 StartZ=0 EndX=-7.19003 EndY=-10 EndZ=0
  constraints (112):
    c: Horizontal(g0)
    c: Distance(g0) = 2
    c: Block(g0)
    c: Vertical(g1)
    c: Coincident(g2,g0)
    c: Vertical(g2)
    c: Block(g2)
    c: Coincident(g6,g2)
    c: Weight(g3) = 1
    c: Equal(g3,g4)
    c: Equal(g3,g5)
    c: InternalAlignment(g3,g6)
    c: InternalAlignment(g4,g6)
    c: InternalAlignment(g5,g6)
    c: InternalAlignment(g7,g6)
    c: InternalAlignment(g8,g6)
    c: Block(g6)
    c: Coincident(g9,g1)
    c: Coincident(g9,g6)
    c: Horizontal(g9)
    c: Vertical(g10)
    c: Block(g10)
    c: Horizontal(g11)
    c: Block(g11)
    c: Coincident(g12,g10)
    c: Horizontal(g12)
    c: Block(g12)
    c: Coincident(g13,g11)
    c: Vertical(g13)
    c: Block(g13)
    c: Coincident(g14,g10)
    c: Horizontal(g14)
    c: Block(g14)
    c: Block(g9)
    c: Block(g1)
    c: Weight(g15) = 1
    c: Equal(g15,g16)
    c: Equal(g15,g17)
    c: InternalAlignment(g15,g18)
    c: InternalAlignment(g16,g18)
    c: InternalAlignment(g17,g18)
    c: InternalAlignment(g19,g18)
    c: InternalAlignment(g20,g18)
    c: Weight(g21) = 1
    c: Equal(g21,g22)
    c: Equal(g21,g23)
    c: InternalAlignment(g21,g24)
    c: InternalAlignment(g22,g24)
    c: InternalAlignment(g23,g24)
    c: InternalAlignment(g25,g24)
    c: InternalAlignment(g26,g24)
    c: Weight(g27) = 1
    c: Equal(g27,g28)
    c: Equal(g27,g29)
    c: Coincident(g30,g14)
    c: InternalAlignment(g27,g30)
    c: InternalAlignment(g28,g30)
    c: InternalAlignment(g29,g30)
    c: InternalAlignment(g31,g30)
    c: InternalAlignment(g32,g30)
    c: Coincident(g36,g12)
    c: Weight(g33) = 1
    c: Equal(g33,g34)
    c: Equal(g33,g35)
    c: Coincident(g36,g11)
    c: InternalAlignment(g33,g36)
    c: InternalAlignment(g34,g36)
    c: InternalAlignment(g35,g36)
    c: InternalAlignment(g37,g36)
    c: InternalAlignment(g38,g36)
    c: Coincident(g42,g13)
    c: Weight(g39) = 1
    c: Equal(g39,g40)
    c: Equal(g39,g41)
    c: Coincident(g42,g1)
    c: InternalAlignment(g39,g42)
    c: InternalAlignment(g40,g42)
    c: InternalAlignment(g41,g42)
    c: InternalAlignment(g43,g42)
    c: InternalAlignment(g44,g42)
    c: Block(g18)
    c: Block(g24)
    c: Block(g30)
    c: Block(g36)
    c: Block(g42)
    c: Horizontal(g45)
    c: Coincident(g45,g0)
    c: Vertical(g46)
    c: Coincident(g46,g45)
    c: Coincident(g47,g46)
    c: Coincident(g47,g18)
    c: Horizontal(g47)
    c: Block(g46)
    c: Coincident(g48,g18)
    c: Horizontal(g48)
    c: Distance(g48) = 1.33
    c: Vertical(g49)
    c: Coincident(g49,g48)
    c: Coincident(g50,g49)
    c: Coincident(g50,g24)
    c: Horizontal(g50)
    c: Tangent(g50,g22)
    c: Horizontal(g51)
    c: Coincident(g51,g24)
    c: Block(g51)
    c: Vertical(g52)
    c: Block(g52)
    c: Coincident(g52,g51)
    c: Coincident(g53,g52)
    c: Coincident(g53,g30)
    c: Horizontal(g53)
    c: Distance(g1) = 8.5
FEATURE [Part::Feature] Face024
  shape: bbox 9.8 x 26.5 x 2e-07 mm, 1 faces, 0 solids (baked)
FEATURE [Part::Revolution] Revolve024
  Angle = 360
  Axis = (0,1,0)
  Base = (0,0,0)
  FaceMakerClass = Part::FaceMakerBullseye
  Placement = pos=(0,0,0) rot=(0,0,1;1.5708rad)
  Solid = false
  Source = -> Face024
  Symmetric = false
FEATURE [Part::Feature] Face025
  shape: bbox 9.8 x 26.5 x 2e-07 mm, 1 faces, 0 solids (baked)
FEATURE [Part::Revolution] Revolve025
  Angle = 360
  Axis = (0,1,0)
  Base = (0,0,0)
  FaceMakerClass = Part::FaceMakerBullseye
  Placement = pos=(0,0,0) rot=(0,0,1;1.5708rad)
  Solid = false
  Source = -> Face025
  Symmetric = false
FEATURE [Part::MultiFuse] Fusion033
  Placement = pos=(-18,19,36) rot=(0,0,1;0rad)
  Shapes = -> [Revolve025,Revolve024]
FEATURE [Part::Cylinder] Cylinder014
  Angle = 360
  AttacherType = Attacher::AttachEngine3D
  Height = 20
  Placement = pos=(0,0,36.15) rot=(0,0,1;0rad)
  Radius = 14.3
FEATURE [Part::Cylinder] Cylinder015
  Angle = 360
  AttacherType = Attacher::AttachEngine3D
  Height = 10
  Placement = pos=(0,0,36.15) rot=(0,0,1;0rad)
  Radius = 4
FEATURE [Part::MultiFuse] Fusion034  label="removeToCreteHoleForPlugHousing004"
  Placement = pos=(-42,19,36) rot=(0,1,0;1.5708rad)
  Shapes = -> [Cylinder014,Cylinder015]
FEATURE [Part::Cut] Cut008  label="top004"
  Base = -> Cut004
  Placement = pos=(-1,0,0) rot=(0,0,1;0rad)
  Tool = -> Fusion034
FEATURE [Part::Box] Box005  label="Cube005"
  AttacherType = Attacher::AttachEngine3D
  Height = 28
  Length = 3
  Placement = pos=(110.7,19,22) rot=(0,0,1;0rad)
  Width = 15.7
FEATURE [Part::Cylinder] Cylinder016
  Angle = 360
  AttacherType = Attacher::AttachEngine3D
  Height = 10
  Placement = pos=(0,0,36.15) rot=(0,0,1;0rad)
  Radius = 4
FEATURE [Part::Cylinder] Cylinder017
  Angle = 360
  AttacherType = Attacher::AttachEngine3D
  Height = 20
  Placement = pos=(0,0,36.15) rot=(0,0,1;0rad)
  Radius = 10.3
FEATURE [Part::MultiFuse] Fusion035  label="removeToCreteHoleForPlugHousing005"
  Placement = pos=(70,19,36) rot=(0,1,0;1.5708rad)
  Shapes = -> [Cylinder017,Cylinder016]
FEATURE [Part::Cut] Cut009  label="plugHousingTab001"
  Base = -> Box005
  Placement = pos=(-107.4,-14,0) rot=(0,0,1;0rad)
  Tool = -> Fusion035
FEATURE [Part::Box] Box006  label="Cube006"
  AttacherType = Attacher::AttachEngine3D
  Height = 28
  Length = 3
  Placement = pos=(110.7,19,22) rot=(0,0,1;0rad)
  Width = 15.7
FEATURE [Part::Cylinder] Cylinder018
  Angle = 360
  AttacherType = Attacher::AttachEngine3D
  Height = 10
  Placement = pos=(0,0,36.15) rot=(0,0,1;0rad)
  Radius = 4
FEATURE [Part::Cylinder] Cylinder019
  Angle = 360
  AttacherType = Attacher::AttachEngine3D
  Height = 20
  Placement = pos=(0,0,36.15) rot=(0,0,1;0rad)
  Radius = 10.3
FEATURE [Part::MultiFuse] Fusion036  label="removeToCreteHoleForPlugHousing006"
  Placement = pos=(70,19,36) rot=(0,1,0;1.5708rad)
  Shapes = -> [Cylinder019,Cylinder018]
FEATURE [Part::Cut] Cut010  label="plugHousingTab002"
  Base = -> Box006
  Placement = pos=(-107.4,-14,0) rot=(0,0,1;0rad)
  Tool = -> Fusion036
FEATURE [Part::MultiFuse] Fusion037
  Placement = pos=(9.6,23,0) rot=(0,0,1;3.14159rad)
  Shapes = -> [Cut009,Cut010]
FEATURE [Part::Box] Box  label="Cube"
  AttacherType = Attacher::AttachEngine3D
  Height = 10
  Length = 3
  Placement = pos=(3.3,4,12) rot=(0,0,1;0rad)
  Width = 10
FEATURE [Part::Fillet] Fillet004
  Base = -> Fusion028
  Edges = 1 edges r=2: [Edge25]
FEATURE [Part::Fillet] Fillet005  label="plugHousing046"
  Base = -> Fillet004
  Edges = 1 edges r=2: [Edge8]
FEATURE [Part::Fillet] Fillet006
  Base = -> Box
  Edges = 1 edges r=2: [Edge11]
FEATURE [Part::Box] Box007  label="Cube007"
  AttacherType = Attacher::AttachEngine3D
  Height = 10
  Length = 3
  Placement = pos=(3.3,4,50) rot=(0,0,1;0rad)
  Width = 10
FEATURE [Part::Fillet] Fillet007
  Base = -> Box007
  Edges = 1 edges r=2: [Edge12]
FEATURE [Part::Box] Box008  label="Cube008"
  AttacherType = Attacher::AttachEngine3D
  Height = 28
  Length = 4
  Placement = pos=(5,0,22) rot=(0,0,1;0rad)
  Width = 10
FEATURE [Part::Fillet] Fillet008
  Base = -> Box008
  Edges = 1 edges r=1: [Edge7]
FEATURE [Part::Fillet] Fillet009
  Base = -> Fillet008
  Edges = 1 edges r=2: [Edge5]
FEATURE [Part::Fillet] Fillet010
  Base = -> Fillet009
  Edges = 1 edges r=2: [Edge2]
FEATURE [Sketcher::SketchObject] Sketch009  label="topSketch003"
  FullyConstrained = true
  sketch-geometry (4):
    g0: LineSegment StartX=16.8446 StartY=31.512 StartZ=0 EndX=16.3251 EndY=34.4666 EndZ=0
    g1: ArcOfCircle CenterX=19 CenterY=19.2524 CenterZ=0 NormalX=0 NormalY=0 NormalZ=1 AngleXU=0 Radius=15.4476 StartAngle=1.74483 EndAngle=2.72717
    g2: ArcOfCircle CenterX=19 CenterY=19.2524 CenterZ=0 NormalX=0 NormalY=0 NormalZ=1 AngleXU=0 Radius=12.4476 StartAngle=1.74483 EndAngle=2.73189
    g3: LineSegment StartX=4.86004 StartY=25.4725 StartZ=0 EndX=7.58253 EndY=24.2107 EndZ=0
  constraints (7):
    c: Block(g0)
    c: Coincident(g1,g0)
    c: Coincident(g2,g0)
    c: Coincident(g3,g1)
    c: Coincident(g3,g2)
    c: Block(g1)
    c: Block(g2)
FEATURE [Part::Extrusion] Extrude008
  Base = -> Sketch009
  Dir = (0,0,1)
  DirMode = 2
  FaceMakerClass = Part::FaceMakerBullseye
  LengthFwd = 10
  LengthRev = 0
  Placement = pos=(0,0,31) rot=(0,0,1;0rad)
  Solid = true
  Symmetric = false
FEATURE [Part::Cylinder] Cylinder020
  Angle = 360
  AttacherType = Attacher::AttachEngine3D
  Height = 20
  Placement = pos=(0,0,36.15) rot=(0,0,1;0rad)
  Radius = 8.2
FEATURE [Part::Cylinder] Cylinder021
  Angle = 360
  AttacherType = Attacher::AttachEngine3D
  Height = 10
  Placement = pos=(0,0,36.15) rot=(0,0,1;0rad)
  Radius = 4
FEATURE [Part::MultiFuse] Fusion038  label="removeToCreteHoleForPlugHousing007"
  Placement = pos=(-42,19,36) rot=(0,1,0;1.5708rad)
  Shapes = -> [Cylinder020,Cylinder021]
FEATURE [Part::Cut] Cut011
  Base = -> Extrude008
  Tool = -> Fusion038
FEATURE [Part::Fillet] Fillet011
  Base = -> Cut011
  Edges = 1 edges r=2: [Edge1]
FEATURE [Part::Fillet] Fillet012
  Base = -> Fillet011
  Edges = 1 edges r=2.5: [Edge1]
FEATURE [Part::Fillet] Fillet013
  Base = -> Fillet012
  Edges = 1 edges r=2.5: [Edge2]
FEATURE [Part::Box] Box010  label="Cube010"
  AttacherType = Attacher::AttachEngine3D
  Height = 16
  Length = 8
  Placement = pos=(12.7,31.52,28) rot=(0,0,1;0rad)
  Width = 4
FEATURE [Sketcher::SketchObject] Sketch010  label="topSketch004"
  FullyConstrained = true
  sketch-geometry (4):
    g0: LineSegment StartX=16.8446 StartY=31.512 StartZ=0 EndX=16.3251 EndY=34.4666 EndZ=0
    g1: ArcOfCircle CenterX=19 CenterY=19.2524 CenterZ=0 NormalX=0 NormalY=0 NormalZ=1 AngleXU=0 Radius=15.4476 StartAngle=1.74483 EndAngle=2.72717
    g2: ArcOfCircle CenterX=19 CenterY=19.2524 CenterZ=0 NormalX=0 NormalY=0 NormalZ=1 AngleXU=0 Radius=12.4476 StartAngle=1.74483 EndAngle=2.73189
    g3: LineSegment StartX=4.86004 StartY=25.4725 StartZ=0 EndX=7.58253 EndY=24.2107 EndZ=0
  constraints (7):
    c: Block(g0)
    c: Coincident(g1,g0)
    c: Coincident(g2,g0)
    c: Coincident(g3,g1)
    c: Coincident(g3,g2)
    c: Block(g1)
    c: Block(g2)
FEATURE [Part::Cylinder] Cylinder022
  Angle = 360
  AttacherType = Attacher::AttachEngine3D
  Height = 10
  Placement = pos=(0,0,36.15) rot=(0,0,1;0rad)
  Radius = 4
FEATURE [Sketcher::SketchObject] Sketch011  label="topSketch005"
  FullyConstrained = true
  sketch-geometry (4):
    g0: LineSegment StartX=16.8446 StartY=31.512 StartZ=0 EndX=16.3251 EndY=34.4666 EndZ=0
    g1: ArcOfCircle CenterX=19 CenterY=19.2524 CenterZ=0 NormalX=0 NormalY=0 NormalZ=1 AngleXU=0 Radius=15.4476 StartAngle=1.74483 EndAngle=2.72717
    g2: ArcOfCircle CenterX=19 CenterY=19.2524 CenterZ=0 NormalX=0 NormalY=0 NormalZ=1 AngleXU=0 Radius=12.4476 StartAngle=1.74483 EndAngle=2.73189
    g3: LineSegment StartX=4.86004 StartY=25.4725 StartZ=0 EndX=7.58253 EndY=24.2107 EndZ=0
  constraints (7):
    c: Block(g0)
    c: Coincident(g1,g0)
    c: Coincident(g2,g0)
    c: Coincident(g3,g1)
    c: Coincident(g3,g2)
    c: Block(g1)
    c: Block(g2)
FEATURE [Part::Extrusion] Extrude010
  Base = -> Sketch011
  Dir = (0,0,1)
  DirMode = 2
  FaceMakerClass = Part::FaceMakerBullseye
  LengthFwd = 10.6
  LengthRev = 0
  Placement = pos=(0,0,31) rot=(0,0,1;0rad)
  Solid = true
  Symmetric = false
FEATURE [Part::Cylinder] Cylinder023
  Angle = 360
  AttacherType = Attacher::AttachEngine3D
  Height = 20
  Placement = pos=(0,0,36.15) rot=(0,0,1;0rad)
  Radius = 8.2
FEATURE [Part::MultiFuse] Fusion039  label="removeToCreteHoleForPlugHousing008"
  Placement = pos=(-42,19,36) rot=(0,1,0;1.5708rad)
  Shapes = -> [Cylinder023,Cylinder022]
FEATURE [Part::Cut] Cut012
  Base = -> Extrude010
  Placement = pos=(0,0,-0.3) rot=(0,0,1;0rad)
  Tool = -> Fusion039
FEATURE [Part::Cut] Cut013
  Base = -> Box010
  Tool = -> Cut012
FEATURE [Part::Fillet] Fillet014
  Base = -> Cut013
  Edges = 1 edges r=0.7: [Edge13]
FEATURE [Part::Fillet] Fillet015
  Base = -> Fillet014
  Edges = 1 edges r=0.7: [Edge13]
FEATURE [Part::Fillet] Fillet016
  Base = -> Fillet015
  Edges = 1 edges r=0.7: [Edge16]
FEATURE [Part::Fillet] Fillet017
  Base = -> Fillet016
  Edges = 1 edges r=0.7: [Edge11]
FEATURE [Part::Fillet] Fillet018
  Base = -> Fillet017
  Edges = 1 edges r=0.7: [Edge10]
FEATURE [Part::Fillet] Fillet019
  Base = -> Fillet018
  Edges = 1 edges r=1.2: [Edge5]
FEATURE [Part::Fillet] Fillet020
  Base = -> Fillet019
  Edges = 1 edges r=1.2: [Edge12]
FEATURE [Part::Fillet] Fillet021
  Base = -> Fillet020
  Edges = 1 edges r=2: [Edge1]
  Placement = pos=(0.3,0,0) rot=(0,0,1;0rad)
FEATURE [Part::MultiFuse] Fusion040  label="top005"
  Shapes = -> [Cut008,Fillet021]
FEATURE [Part::MultiFuse] Fusion041  label="wireHolder"
  Shapes = -> [Fusion033,Fillet013]
FEATURE [Part::MultiFuse] Fusion042
  Shapes = -> [Fillet007,Fusion041]
FEATURE [Part::MultiFuse] Fusion043  label="wireHolder001"
  Shapes = -> [Fusion042,Fillet010]
FEATURE [Part::MultiFuse] Fusion044  label="wireHolder002"
  Shapes = -> [Fillet006,Fusion037,Fusion043]
FEATURE [Part::Feature] Face026
  shape: bbox 11 x 6 x 2e-07 mm, 1 faces, 0 solids (baked)
FEATURE [Part::Revolution] Revolve026
  Angle = 360
  Axis = (0,1,0)
  Base = (0,0,0)
  FaceMakerClass = Part::FaceMakerBullseye
  Placement = pos=(30.3,-1,19.7) rot=(0,0,1;0rad)
  Solid = false
  Source = -> Face026
  Symmetric = false
FEATURE [Sketcher::SketchObject] Sketch013  label="topSketch006"
  FullyConstrained = true
  sketch-geometry (13):
    g0: LineSegment StartX=117 StartY=19 StartZ=0 EndX=117 EndY=38 EndZ=0
    g1: ArcOfCircle CenterX=98 CenterY=19 CenterZ=0 NormalX=0 NormalY=0 NormalZ=1 AngleXU=0 Radius=19 StartAngle=5.7297 EndAngle=6.28319
    g2: LineSegment StartX=0 StartY=3 StartZ=0 EndX=0 EndY=19 EndZ=0
    g3: LineSegment StartX=19 StartY=38 StartZ=0 EndX=117 EndY=38 EndZ=0
    g4: ArcOfCircle CenterX=19 CenterY=19 CenterZ=0 NormalX=0 NormalY=0 NormalZ=1 AngleXU=0 Radius=19 StartAngle=1.5708 EndAngle=3.14159
    g5: ArcOfCircle CenterX=19 CenterY=19 CenterZ=0 NormalX=0 NormalY=0 NormalZ=1 AngleXU=0 Radius=16 StartAngle=1.5708 EndAngle=3.14159
    g6: ArcOfCircle CenterX=98 CenterY=19 CenterZ=0 NormalX=0 NormalY=0 NormalZ=1 AngleXU=0 Radius=16 StartAngle=5.60905 EndAngle=6.28319
    g7: LineSegment StartX=114 StartY=19 StartZ=0 EndX=114 EndY=35 EndZ=0
    g8: LineSegment StartX=110.5 StartY=9.01251 StartZ=0 EndX=114.163 EndY=9.01251 EndZ=0
    g9: LineSegment StartX=114 StartY=35 StartZ=0 EndX=19 EndY=35 EndZ=0
    g10: LineSegment StartX=0 StartY=3 StartZ=0 EndX=0 EndY=0 EndZ=0
    g11: LineSegment StartX=3 StartY=0 StartZ=0 EndX=0 EndY=0 EndZ=0
    g12: LineSegment StartX=3 StartY=19 StartZ=0 EndX=3 EndY=0 EndZ=0
  constraints (33):
    c: Vertical(g0)
    c: Distance(g0) = 19
    c: Block(g0)
    c: Coincident(g1,g0)
    c: Block(g1)
    c: Vertical(g2)
    c: Block(g2)
    c: Coincident(g3,g0)
    c: Horizontal(g3)
    c: Distance(g3) = 98
    c: Coincident(g4,g3)
    c: Coincident(g4,g2)
    c: Block(g4)
    c: Coincident(g5,g4)
    c: Coincident(g6,g1)
    c: Block(g6)
    c: Block(g5)
    c: Coincident(g7,g6)
    c: Vertical(g7)
    c: Coincident(g8,g6)
    c: Coincident(g8,g1)
    c: Coincident(g9,g7)
    c: Coincident(g9,g5)
    c: Horizontal(g9)
    c: Tangent(g9,g5)
    c: Coincident(g10,g2)
    c: Distance(g10) = 3
    c: Vertical(g10)
    c: Coincident(g11,g10)
    c: Horizontal(g11)
    c: Coincident(g12,g5)
    c: Coincident(g12,g11)
    c: Vertical(g12)
FEATURE [Part::Extrusion] Extrude011  label="top006"
  Base = -> Sketch013
  Dir = (0,0,1)
  DirMode = 2
  FaceMakerClass = Part::FaceMakerBullseye
  LengthFwd = 72
  LengthRev = 0
  Solid = true
  Symmetric = false
FEATURE [Sketcher::SketchObject] Sketch014
  FullyConstrained = true
  MapMode = 3
  Placement = pos=(0,0,0) rot=(1,0,0;1.5708rad)
  Support = -> [Extrude011]
  sketch-geometry (8):
    g0: Circle CenterX=80.351 CenterY=-67.6202 CenterZ=0 NormalX=0 NormalY=0 NormalZ=1 AngleXU=0 Radius=2
    g1: Circle CenterX=80.351 CenterY=-67.6202 CenterZ=0 NormalX=0 NormalY=0 NormalZ=1 AngleXU=0 Radius=3
    g2: Circle CenterX=80.351 CenterY=-4.92017 CenterZ=0 NormalX=0 NormalY=0 NormalZ=1 AngleXU=0 Radius=2
    g3: Circle CenterX=80.351 CenterY=-4.92017 CenterZ=0 NormalX=0 NormalY=0 NormalZ=1 AngleXU=0 Radius=3
    g4: Circle CenterX=23.851 CenterY=-4.92017 CenterZ=0 NormalX=0 NormalY=0 NormalZ=1 AngleXU=0 Radius=2
    g5: Circle CenterX=23.851 CenterY=-4.92017 CenterZ=0 NormalX=0 NormalY=0 NormalZ=1 AngleXU=0 Radius=3
    g6: Circle CenterX=23.851 CenterY=-67.6202 CenterZ=0 NormalX=0 NormalY=0 NormalZ=1 AngleXU=0 Radius=2
    g7: Circle CenterX=23.851 CenterY=-67.6202 CenterZ=0 NormalX=0 NormalY=0 NormalZ=1 AngleXU=0 Radius=3
  constraints (8):
    c: Block(g3)
    c: Block(g2)
    c: Block(g1)
    c: Block(g0)
    c: Block(g6)
    c: Block(g7)
    c: Block(g4)
    c: Block(g5)
FEATURE [Part::Feature] Face027
  shape: bbox 11 x 6 x 2e-07 mm, 1 faces, 0 solids (baked)
FEATURE [Part::Revolution] Revolve027
  Angle = 360
  Axis = (0,1,0)
  Base = (0,0,0)
  FaceMakerClass = Part::FaceMakerBullseye
  Placement = pos=(30.3,-1,51.7) rot=(0,0,1;0rad)
  Solid = false
  Source = -> Face027
  Symmetric = false
FEATURE [Part::Feature] Face028
  shape: bbox 11 x 6 x 2e-07 mm, 1 faces, 0 solids (baked)
FEATURE [Part::Revolution] Revolve028
  Angle = 360
  Axis = (0,1,0)
  Base = (0,0,0)
  FaceMakerClass = Part::FaceMakerBullseye
  Placement = pos=(62.3,-1,19.7) rot=(0,0,1;0rad)
  Solid = false
  Source = -> Face028
  Symmetric = false
FEATURE [Part::Feature] Face029
  shape: bbox 11 x 6 x 2e-07 mm, 1 faces, 0 solids (baked)
FEATURE [Part::Revolution] Revolve029
  Angle = 360
  Axis = (0,1,0)
  Base = (0,0,0)
  FaceMakerClass = Part::FaceMakerBullseye
  Placement = pos=(62.3,-1,51.7) rot=(0,0,1;0rad)
  Solid = false
  Source = -> Face029
  Symmetric = false
FEATURE [Part::Feature] Wire
  shape: bbox 11 x 5.2 x 2e-07 mm, 0 faces, 0 solids (baked)
FEATURE [Part::Revolution] Revolve030
  Angle = 360
  Axis = (0,1,0)
  Base = (0,0,0)
  FaceMakerClass = Part::FaceMakerBullseye
  Placement = pos=(30.3,38,19.7) rot=(0,0,1;0rad)
  Solid = true
  Source = -> Wire
  Symmetric = false
FEATURE [Part::Feature] Wire001
  shape: bbox 11 x 5.2 x 2e-07 mm, 0 faces, 0 solids (baked)
FEATURE [Part::Revolution] Revolve031
  Angle = 360
  Axis = (0,1,0)
  Base = (0,0,0)
  FaceMakerClass = Part::FaceMakerBullseye
  Placement = pos=(30.3,38,51.7) rot=(0,0,1;0rad)
  Solid = true
  Source = -> Wire001
  Symmetric = false
FEATURE [Part::Feature] Wire002
  shape: bbox 11 x 5.2 x 2e-07 mm, 0 faces, 0 solids (baked)
FEATURE [Part::Revolution] Revolve032
  Angle = 360
  Axis = (0,1,0)
  Base = (0,0,0)
  FaceMakerClass = Part::FaceMakerBullseye
  Placement = pos=(62.3,38,51.7) rot=(0,0,1;0rad)
  Solid = true
  Source = -> Wire002
  Symmetric = false
FEATURE [Part::Feature] Wire003
  shape: bbox 11 x 5.2 x 2e-07 mm, 0 faces, 0 solids (baked)
FEATURE [Part::Revolution] Revolve033
  Angle = 360
  Axis = (0,1,0)
  Base = (0,0,0)
  FaceMakerClass = Part::FaceMakerBullseye
  Placement = pos=(62.3,38,19.7) rot=(0,0,1;0rad)
  Solid = true
  Source = -> Wire003
  Symmetric = false
FEATURE [Part::MultiFuse] Fusion045  label="altRandScrewHousing"
  Shapes = -> [Revolve029,Revolve027,Revolve028,Revolve026]
FEATURE [Part::MultiFuse] Fusion046  label="fanScrewHousing"
  Shapes = -> [Revolve033,Revolve032,Revolve031,Revolve030]
FEATURE [Sketcher::SketchObject] Sketch015
  FullyConstrained = true
  sketch-geometry (17):
    g0: Circle CenterX=-3.5 CenterY=23.5 CenterZ=0 NormalX=0 NormalY=0 NormalZ=1 AngleXU=0 Radius=1
    g1: Circle CenterX=-1 CenterY=15.25 CenterZ=0 NormalX=0 NormalY=0 NormalZ=1 AngleXU=0 Radius=1
    g2: Circle CenterX=-3.5 CenterY=7 CenterZ=0 NormalX=0 NormalY=0 NormalZ=1 AngleXU=0 Radius=1
    g3: BSplineCurve PolesCount=3 KnotsCount=2 Degree=2 IsPeriodic=0
    g4: GeomPoint X=-3.5 Y=23.5 Z=0
    g5: GeomPoint X=-3.5 Y=7 Z=0
    g6: Circle CenterX=-4.8 CenterY=30.5 CenterZ=0 NormalX=0 NormalY=0 NormalZ=1 AngleXU=0 Radius=1
    g7: Circle CenterX=-3.5 CenterY=30.5 CenterZ=0 NormalX=0 NormalY=0 NormalZ=1 AngleXU=0 Radius=1
    g8: Circle CenterX=-3.5 CenterY=29.2 CenterZ=0 NormalX=0 NormalY=0 NormalZ=1 AngleXU=0 Radius=1
    g9: BSplineCurve PolesCount=3 KnotsCount=2 Degree=2 IsPeriodic=0
    g10: GeomPoint X=-4.8 Y=30.5 Z=0
    g11: GeomPoint X=-3.5 Y=29.2 Z=0
    g12: LineSegment StartX=-3.5 StartY=29.2 StartZ=0 EndX=-3.5 EndY=23.5 EndZ=0
    g13: LineSegment StartX=-4.8 StartY=30.5 StartZ=0 EndX=0 EndY=30.5 EndZ=0
    g14: LineSegment StartX=-3.5 StartY=0.3 StartZ=0 EndX=0 EndY=0.3 EndZ=0
    g15: LineSegment StartX=-3.5 StartY=0.3 StartZ=0 EndX=-3.5 EndY=7 EndZ=0
    g16: LineSegment StartX=0 StartY=0.3 StartZ=0 EndX=0 EndY=30.5 EndZ=0
  constraints (33):
    c: Weight(g0) = 1
    c: Equal(g0,g1)
    c: Equal(g0,g2)
    c: InternalAlignment(g0,g3)
    c: InternalAlignment(g1,g3)
    c: InternalAlignment(g2,g3)
    c: InternalAlignment(g4,g3)
    c: InternalAlignment(g5,g3)
    c: Block(g3)
    c: Weight(g6) = 1
    c: Equal(g6,g7)
    c: Equal(g6,g8)
    c: InternalAlignment(g6,g9)
    c: InternalAlignment(g7,g9)
    c: InternalAlignment(g8,g9)
    c: InternalAlignment(g10,g9)
    c: InternalAlignment(g11,g9)
    c: Block(g9)
    c: Coincident(g12,g9)
    c: Coincident(g12,g3)
    c: Vertical(g12)
    c: Coincident(g13,g9)
    c: Horizontal(g13)
    c: Distance(g13) = 4.8
    c: Horizontal(g14)
    c: Block(g14)
    c: Coincident(g15,g14)
    c: Coincident(g15,g3)
    c: Vertical(g15)
    c: Coincident(g16,g14)
    c: Coincident(g16,g13)
    c: Vertical(g16)
    c: Tangent(g16,g1)
FEATURE [Sketcher::SketchObject] Sketch016
  FullyConstrained = true
  sketch-geometry (16):
    g0: Circle CenterX=-3.5 CenterY=23.5 CenterZ=0 NormalX=0 NormalY=0 NormalZ=1 AngleXU=0 Radius=1
    g1: Circle CenterX=-1 CenterY=15.25 CenterZ=0 NormalX=0 NormalY=0 NormalZ=1 AngleXU=0 Radius=1
    g2: Circle CenterX=-3.5 CenterY=7 CenterZ=0 NormalX=0 NormalY=0 NormalZ=1 AngleXU=0 Radius=1
    g3: BSplineCurve PolesCount=3 KnotsCount=2 Degree=2 IsPeriodic=0
    g4: GeomPoint X=-3.5 Y=23.5 Z=0
    g5: GeomPoint X=-3.5 Y=7 Z=0
    g6: LineSegment StartX=-3.5 StartY=28.2 StartZ=0 EndX=-3.5 EndY=23.5 EndZ=0
    g7: LineSegment StartX=0 StartY=29.5 StartZ=0 EndX=0 EndY=30 EndZ=0
    g8: LineSegment StartX=-3.5 StartY=28.2 StartZ=0 EndX=-3.5 EndY=30 EndZ=0
    g9: LineSegment StartX=0 StartY=30 StartZ=0 EndX=0 EndY=30.5 EndZ=0
    g10: LineSegment StartX=0 StartY=30.5 StartZ=0 EndX=-3.5 EndY=30.5 EndZ=0
    g11: LineSegment StartX=-3.5 StartY=30.5 StartZ=0 EndX=-3.5 EndY=30 EndZ=0
    g12: LineSegment StartX=0 StartY=29.5 StartZ=0 EndX=0 EndY=5 EndZ=0
    g13: LineSegment StartX=-3.5 StartY=0.3 StartZ=0 EndX=-3.5 EndY=7 EndZ=0
    g14: LineSegment StartX=-3.5 StartY=0.3 StartZ=0 EndX=0 EndY=0.3 EndZ=0
    g15: LineSegment StartX=0 StartY=5 StartZ=0 EndX=0 EndY=0.3 EndZ=0
  constraints (39):
    c: Weight(g0) = 1
    c: Equal(g0,g1)
    c: Equal(g0,g2)
    c: InternalAlignment(g0,g3)
    c: InternalAlignment(g1,g3)
    c: InternalAlignment(g2,g3)
    c: InternalAlignment(g4,g3)
    c: InternalAlignment(g5,g3)
    c: Block(g3)
    c: Coincident(g6,g3)
    c: Vertical(g6)
    c: Vertical(g7)
    c: Distance(g7) = 0.5
    c: Coincident(g8,g6)
    c: Vertical(g8)
    c: Block(g6)
    c: Block(g7)
    c: Vertical(g9)
    c: Equal(g7,g9) = 0.5
    c: Block(g9)
    c: Coincident(g9,g7)
    c: Horizontal(g10)
    c: Coincident(g10,g9)
    c: Coincident(g11,g10)
    c: Coincident(g11,g8)
    c: Vertical(g11)
    c: Block(g11)
    c: Coincident(g12,g7)
    c: Vertical(g12)
    c: Coincident(g13,g3)
    c: Vertical(g13)
    c: Distance(g13) = 6.7
    c: Coincident(g14,g13)
    c: Horizontal(g14)
    c: Block(g14)
    c: Coincident(g15,g12)
    c: Coincident(g15,g14)
    c: Vertical(g15)
    c: Block(g15)
FEATURE [Sketcher::SketchObject] Sketch017
  FullyConstrained = true
  sketch-geometry (11):
    g0: LineSegment StartX=-3.5 StartY=1e-16 StartZ=0 EndX=-1.6 EndY=1e-16 EndZ=0
    g1: LineSegment StartX=-1.6 StartY=1e-16 StartZ=0 EndX=-1.6 EndY=1.5 EndZ=0
    g2: LineSegment StartX=-3.5 StartY=1.5 StartZ=0 EndX=-1.6 EndY=1.5 EndZ=0
    g3: LineSegment StartX=-3.5 StartY=1e-16 StartZ=0 EndX=-4.8 EndY=1e-16 EndZ=0
    g4: Circle CenterX=-3.5 CenterY=1.3 CenterZ=0 NormalX=0 NormalY=0 NormalZ=1 AngleXU=0 Radius=1
    g5: Circle CenterX=-3.5 CenterY=1e-16 CenterZ=0 NormalX=0 NormalY=0 NormalZ=1 AngleXU=0 Radius=1
    g6: Circle CenterX=-4.8 CenterY=1e-16 CenterZ=0 NormalX=0 NormalY=0 NormalZ=1 AngleXU=0 Radius=1
    g7: BSplineCurve PolesCount=3 KnotsCount=2 Degree=2 IsPeriodic=0
    g8: GeomPoint X=-3.5 Y=1.3 Z=0
    g9: GeomPoint X=-4.8 Y=1e-16 Z=0
    g10: LineSegment StartX=-3.5 StartY=1.3 StartZ=0 EndX=-3.5 EndY=1.5 EndZ=0
  constraints (24):
    c: Horizontal(g0)
    c: Distance(g0) = 1.9
    c: Block(g0)
    c: Coincident(g1,g0)
    c: Vertical(g1)
    c: Coincident(g2,g1)
    c: Horizontal(g2)
    c: Coincident(g3,g0)
    c: Horizontal(g3)
    c: Distance(g3) = 1.3
    c: Weight(g4) = 1
    c: Equal(g4,g5)
    c: Coincident(g5,g0)
    c: Equal(g4,g6)
    c: Coincident(g7,g3)
    c: InternalAlignment(g4,g7)
    c: InternalAlignment(g5,g7)
    c: InternalAlignment(g6,g7)
    c: InternalAlignment(g8,g7)
    c: InternalAlignment(g9,g7)
    c: Coincident(g10,g7)
    c: Coincident(g10,g2)
    c: Vertical(g10)
    c: Block(g10)
FEATURE [Part::Feature] Face035
  shape: bbox 3.2 x 1.5 x 2e-07 mm, 1 faces, 0 solids (baked)
FEATURE [Part::Revolution] Revolve039  label="backCaseScrewRetainer"
  Angle = 360
  Axis = (0,1,0)
  Base = (0,0,0)
  FaceMakerClass = Part::FaceMakerBullseye
  Placement = pos=(12.5,3,62) rot=(0,0,1;0rad)
  Solid = false
  Source = -> Face035
  Symmetric = false
FEATURE [Part::Feature] Face036
  shape: bbox 3.2 x 1.5 x 2e-07 mm, 1 faces, 0 solids (baked)
FEATURE [Part::Feature] Face039
  shape: bbox 4.8 x 30.2 x 2e-07 mm, 1 faces, 0 solids (baked)
FEATURE [Part::Revolution] Revolve043  label="frontCaseScrewPost002"
  Angle = 360
  Axis = (0,1,0)
  Base = (0,0,0)
  FaceMakerClass = Part::FaceMakerBullseye
  Placement = pos=(89.5,4.5,3.5) rot=(0,0,1;0rad)
  Solid = false
  Source = -> Face039
  Symmetric = false
FEATURE [Part::Feature] Face042
  shape: bbox 4.8 x 30.2 x 2e-07 mm, 1 faces, 0 solids (baked)
FEATURE [Part::Revolution] Revolve046  label="frontCaseScrewPost003"
  Angle = 360
  Axis = (0,1,0)
  Base = (0,0,0)
  FaceMakerClass = Part::FaceMakerBullseye
  Placement = pos=(89.5,4.5,68.5) rot=(0,0,1;0rad)
  Solid = false
  Source = -> Face042
  Symmetric = false
FEATURE [Part::Feature] Face043
  shape: bbox 3.2 x 1.5 x 2e-07 mm, 1 faces, 0 solids (baked)
FEATURE [Part::Revolution] Revolve047  label="frontCaseScrewRetainer002"
  Angle = 360
  Axis = (0,1,0)
  Base = (0,0,0)
  FaceMakerClass = Part::FaceMakerBullseye
  Placement = pos=(89.5,3,68.5) rot=(0,0,1;0rad)
  Solid = false
  Source = -> Face043
  Symmetric = false
FEATURE [Part::Feature] Face044
  shape: bbox 3.2 x 1.5 x 2e-07 mm, 1 faces, 0 solids (baked)
FEATURE [Part::Revolution] Revolve048  label="frontCaseScrewRetainer003"
  Angle = 360
  Axis = (0,1,0)
  Base = (0,0,0)
  FaceMakerClass = Part::FaceMakerBullseye
  Placement = pos=(89.5,3,3.5) rot=(0,0,1;0rad)
  Solid = false
  Source = -> Face044
  Symmetric = false
FEATURE [App::MeasureDistance] Distance002  label="Distance: 1.67 mm"
  Distance = 1.66921
  P1 = (99.2361,4.7524,71.7)
  P2 = (99.2347,6.42161,71.7)
FEATURE [Sketcher::SketchObject] Sketch018
  FullyConstrained = true
  sketch-geometry (7):
    g0: LineSegment StartX=0 StartY=0 StartZ=0 EndX=0 EndY=6 EndZ=0
    g1: Circle CenterX=0 CenterY=0 CenterZ=0 NormalX=0 NormalY=0 NormalZ=1 AngleXU=0 Radius=1
    g2: Circle CenterX=8 CenterY=6 CenterZ=0 NormalX=0 NormalY=0 NormalZ=1 AngleXU=0 Radius=1
    g3: BSplineCurve PolesCount=3 KnotsCount=2 Degree=2 IsPeriodic=0
    g4: GeomPoint X=0 Y=0 Z=0
    g5: GeomPoint X=8 Y=6 Z=0
    g6: LineSegment StartX=0 StartY=6 StartZ=0 EndX=8 EndY=6 EndZ=0
  constraints (14):
    c: Coincident(g0,g-1)
    c: Distance(g0) = 6
    c: Vertical(g0)
    c: Coincident(g3,g0)
    c: Weight(g1) = 1
    c: Equal(g1,g2)
    c: InternalAlignment(g1,g3)
    c: InternalAlignment(g2,g3)
    c: InternalAlignment(g4,g3)
    c: InternalAlignment(g5,g3)
    c: Block(g3)
    c: Coincident(g6,g0)
    c: Coincident(g6,g3)
    c: Horizontal(g6)
FEATURE [Part::Extrusion] Extrude012  label="caseScrewPillarBracket"
  Base = -> Sketch018
  Dir = (0,0,1)
  DirMode = 2
  FaceMakerClass = Part::FaceMakerBullseye
  LengthFwd = 2.4
  LengthRev = 0
  Placement = pos=(15.76,29,8.8) rot=(0,1,0;0rad)
  Solid = true
  Symmetric = false
FEATURE [Sketcher::SketchObject] Sketch019
  FullyConstrained = true
  sketch-geometry (7):
    g0: LineSegment StartX=0 StartY=0 StartZ=0 EndX=0 EndY=6 EndZ=0
    g1: Circle CenterX=0 CenterY=0 CenterZ=0 NormalX=0 NormalY=0 NormalZ=1 AngleXU=0 Radius=1
    g2: Circle CenterX=8 CenterY=6 CenterZ=0 NormalX=0 NormalY=0 NormalZ=1 AngleXU=0 Radius=1
    g3: BSplineCurve PolesCount=3 KnotsCount=2 Degree=2 IsPeriodic=0
    g4: GeomPoint X=0 Y=0 Z=0
    g5: GeomPoint X=8 Y=6 Z=0
    g6: LineSegment StartX=0 StartY=6 StartZ=0 EndX=8 EndY=6 EndZ=0
  constraints (14):
    c: Coincident(g0,g-1)
    c: Distance(g0) = 6
    c: Vertical(g0)
    c: Coincident(g3,g0)
    c: Weight(g1) = 1
    c: Equal(g1,g2)
    c: InternalAlignment(g1,g3)
    c: InternalAlignment(g2,g3)
    c: InternalAlignment(g4,g3)
    c: InternalAlignment(g5,g3)
    c: Block(g3)
    c: Coincident(g6,g0)
    c: Coincident(g6,g3)
    c: Horizontal(g6)
FEATURE [Part::Extrusion] Extrude013  label="caseScrewPillarBracket001"
  Base = -> Sketch019
  Dir = (0,0,1)
  DirMode = 2
  FaceMakerClass = Part::FaceMakerBullseye
  LengthFwd = 2.4
  LengthRev = 0
  Placement = pos=(15.76,29,60.8) rot=(0,0,1;0rad)
  Solid = true
  Symmetric = false
FEATURE [Sketcher::SketchObject] Sketch020
  FullyConstrained = true
  sketch-geometry (7):
    g0: LineSegment StartX=0 StartY=0 StartZ=0 EndX=0 EndY=6 EndZ=0
    g1: Circle CenterX=0 CenterY=0 CenterZ=0 NormalX=0 NormalY=0 NormalZ=1 AngleXU=0 Radius=1
    g2: Circle CenterX=8 CenterY=6 CenterZ=0 NormalX=0 NormalY=0 NormalZ=1 AngleXU=0 Radius=1
    g3: BSplineCurve PolesCount=3 KnotsCount=2 Degree=2 IsPeriodic=0
    g4: GeomPoint X=0 Y=0 Z=0
    g5: GeomPoint X=8 Y=6 Z=0
    g6: LineSegment StartX=0 StartY=6 StartZ=0 EndX=8 EndY=6 EndZ=0
  constraints (14):
    c: Coincident(g0,g-1)
    c: Distance(g0) = 6
    c: Vertical(g0)
    c: Coincident(g3,g0)
    c: Weight(g1) = 1
    c: Equal(g1,g2)
    c: InternalAlignment(g1,g3)
    c: InternalAlignment(g2,g3)
    c: InternalAlignment(g4,g3)
    c: InternalAlignment(g5,g3)
    c: Block(g3)
    c: Coincident(g6,g0)
    c: Coincident(g6,g3)
    c: Horizontal(g6)
FEATURE [Part::Extrusion] Extrude014  label="caseScrewPillarBracket002"
  Base = -> Sketch020
  Dir = (0,0,1)
  DirMode = 2
  FaceMakerClass = Part::FaceMakerBullseye
  LengthFwd = 2.4
  LengthRev = 0
  Placement = pos=(13.7,29,13.26) rot=(0,-1,0;1.5708rad)
  Solid = true
  Symmetric = false
FEATURE [Sketcher::SketchObject] Sketch021
  FullyConstrained = true
  sketch-geometry (7):
    g0: LineSegment StartX=0 StartY=0 StartZ=0 EndX=0 EndY=6 EndZ=0
    g1: Circle CenterX=0 CenterY=0 CenterZ=0 NormalX=0 NormalY=0 NormalZ=1 AngleXU=0 Radius=1
    g2: Circle CenterX=8 CenterY=6 CenterZ=0 NormalX=0 NormalY=0 NormalZ=1 AngleXU=0 Radius=1
    g3: BSplineCurve PolesCount=3 KnotsCount=2 Degree=2 IsPeriodic=0
    g4: GeomPoint X=0 Y=0 Z=0
    g5: GeomPoint X=8 Y=6 Z=0
    g6: LineSegment StartX=0 StartY=6 StartZ=0 EndX=8 EndY=6 EndZ=0
  constraints (14):
    c: Coincident(g0,g-1)
    c: Distance(g0) = 6
    c: Vertical(g0)
    c: Coincident(g3,g0)
    c: Weight(g1) = 1
    c: Equal(g1,g2)
    c: InternalAlignment(g1,g3)
    c: InternalAlignment(g2,g3)
    c: InternalAlignment(g4,g3)
    c: InternalAlignment(g5,g3)
    c: Block(g3)
    c: Coincident(g6,g0)
    c: Coincident(g6,g3)
    c: Horizontal(g6)
FEATURE [Part::Extrusion] Extrude015  label="caseScrewPillarBracket003"
  Base = -> Sketch021
  Dir = (0,0,1)
  DirMode = 2
  FaceMakerClass = Part::FaceMakerBullseye
  LengthFwd = 2.4
  LengthRev = 0
  Placement = pos=(11.3,29,58.74) rot=(0,1,0;1.5708rad)
  Solid = true
  Symmetric = false
FEATURE [Sketcher::SketchObject] Sketch022
  FullyConstrained = true
  sketch-geometry (7):
    g0: LineSegment StartX=0 StartY=0 StartZ=0 EndX=0 EndY=6 EndZ=0
    g1: Circle CenterX=0 CenterY=0 CenterZ=0 NormalX=0 NormalY=0 NormalZ=1 AngleXU=0 Radius=1
    g2: Circle CenterX=8 CenterY=6 CenterZ=0 NormalX=0 NormalY=0 NormalZ=1 AngleXU=0 Radius=1
    g3: BSplineCurve PolesCount=3 KnotsCount=2 Degree=2 IsPeriodic=0
    g4: GeomPoint X=0 Y=0 Z=0
    g5: GeomPoint X=8 Y=6 Z=0
    g6: LineSegment StartX=0 StartY=6 StartZ=0 EndX=8 EndY=6 EndZ=0
  constraints (14):
    c: Coincident(g0,g-1)
    c: Distance(g0) = 6
    c: Vertical(g0)
    c: Coincident(g3,g0)
    c: Weight(g1) = 1
    c: Equal(g1,g2)
    c: InternalAlignment(g1,g3)
    c: InternalAlignment(g2,g3)
    c: InternalAlignment(g4,g3)
    c: InternalAlignment(g5,g3)
    c: Block(g3)
    c: Coincident(g6,g0)
    c: Coincident(g6,g3)
    c: Horizontal(g6)
FEATURE [Part::Extrusion] Extrude016  label="caseScrewPillarBracket004"
  Base = -> Sketch022
  Dir = (0,0,1)
  DirMode = 2
  FaceMakerClass = Part::FaceMakerBullseye
  LengthFwd = 2.4
  LengthRev = 0
  Placement = pos=(88.3,29,65.23) rot=(0,1,0;1.5708rad)
  Solid = true
  Symmetric = false
FEATURE [Sketcher::SketchObject] Sketch023
  FullyConstrained = true
  sketch-geometry (7):
    g0: LineSegment StartX=0 StartY=0 StartZ=0 EndX=0 EndY=6 EndZ=0
    g1: Circle CenterX=0 CenterY=0 CenterZ=0 NormalX=0 NormalY=0 NormalZ=1 AngleXU=0 Radius=1
    g2: Circle CenterX=8 CenterY=6 CenterZ=0 NormalX=0 NormalY=0 NormalZ=1 AngleXU=0 Radius=1
    g3: BSplineCurve PolesCount=3 KnotsCount=2 Degree=2 IsPeriodic=0
    g4: GeomPoint X=0 Y=0 Z=0
    g5: GeomPoint X=8 Y=6 Z=0
    g6: LineSegment StartX=0 StartY=6 StartZ=0 EndX=8 EndY=6 EndZ=0
  constraints (14):
    c: Coincident(g0,g-1)
    c: Distance(g0) = 6
    c: Vertical(g0)
    c: Coincident(g3,g0)
    c: Weight(g1) = 1
    c: Equal(g1,g2)
    c: InternalAlignment(g1,g3)
    c: InternalAlignment(g2,g3)
    c: InternalAlignment(g4,g3)
    c: InternalAlignment(g5,g3)
    c: Block(g3)
    c: Coincident(g6,g0)
    c: Coincident(g6,g3)
    c: Horizontal(g6)
FEATURE [Part::Extrusion] Extrude017  label="caseScrewPillarBracket005"
  Base = -> Sketch023
  Dir = (0,0,1)
  DirMode = 2
  FaceMakerClass = Part::FaceMakerBullseye
  LengthFwd = 2.4
  LengthRev = 0
  Placement = pos=(90.7,29,6.77) rot=(0,-1,0;1.5708rad)
  Solid = true
  Symmetric = false
FEATURE [Sketcher::SketchObject] Sketch024
  FullyConstrained = true
  sketch-geometry (7):
    g0: LineSegment StartX=0 StartY=0 StartZ=0 EndX=0 EndY=6 EndZ=0
    g1: Circle CenterX=0 CenterY=0 CenterZ=0 NormalX=0 NormalY=0 NormalZ=1 AngleXU=0 Radius=1
    g2: Circle CenterX=8 CenterY=6 CenterZ=0 NormalX=0 NormalY=0 NormalZ=1 AngleXU=0 Radius=1
    g3: BSplineCurve PolesCount=3 KnotsCount=2 Degree=2 IsPeriodic=0
    g4: GeomPoint X=0 Y=0 Z=0
    g5: GeomPoint X=8 Y=6 Z=0
    g6: LineSegment StartX=0 StartY=6 StartZ=0 EndX=8 EndY=6 EndZ=0
  constraints (14):
    c: Coincident(g0,g-1)
    c: Distance(g0) = 6
    c: Vertical(g0)
    c: Coincident(g3,g0)
    c: Weight(g1) = 1
    c: Equal(g1,g2)
    c: InternalAlignment(g1,g3)
    c: InternalAlignment(g2,g3)
    c: InternalAlignment(g4,g3)
    c: InternalAlignment(g5,g3)
    c: Block(g3)
    c: Coincident(g6,g0)
    c: Coincident(g6,g3)
    c: Horizontal(g6)
FEATURE [Part::Extrusion] Extrude018  label="caseScrewPillarBracket006"
  Base = -> Sketch024
  Dir = (0,0,1)
  DirMode = 2
  FaceMakerClass = Part::FaceMakerBullseye
  LengthFwd = 2.4
  LengthRev = 0
  Placement = pos=(103.7,29,6.77) rot=(0,-1,0;1.5708rad)
  Solid = true
  Symmetric = false
FEATURE [Sketcher::SketchObject] Sketch025
  FullyConstrained = true
  sketch-geometry (7):
    g0: LineSegment StartX=0 StartY=0 StartZ=0 EndX=0 EndY=6 EndZ=0
    g1: Circle CenterX=0 CenterY=0 CenterZ=0 NormalX=0 NormalY=0 NormalZ=1 AngleXU=0 Radius=1
    g2: Circle CenterX=8 CenterY=6 CenterZ=0 NormalX=0 NormalY=0 NormalZ=1 AngleXU=0 Radius=1
    g3: BSplineCurve PolesCount=3 KnotsCount=2 Degree=2 IsPeriodic=0
    g4: GeomPoint X=0 Y=0 Z=0
    g5: GeomPoint X=8 Y=6 Z=0
    g6: LineSegment StartX=0 StartY=6 StartZ=0 EndX=8 EndY=6 EndZ=0
  constraints (14):
    c: Coincident(g0,g-1)
    c: Distance(g0) = 6
    c: Vertical(g0)
    c: Coincident(g3,g0)
    c: Weight(g1) = 1
    c: Equal(g1,g2)
    c: InternalAlignment(g1,g3)
    c: InternalAlignment(g2,g3)
    c: InternalAlignment(g4,g3)
    c: InternalAlignment(g5,g3)
    c: Block(g3)
    c: Coincident(g6,g0)
    c: Coincident(g6,g3)
    c: Horizontal(g6)
FEATURE [Part::Extrusion] Extrude019  label="caseScrewPillarBracket007"
  Base = -> Sketch025
  Dir = (0,0,1)
  DirMode = 2
  FaceMakerClass = Part::FaceMakerBullseye
  LengthFwd = 2.4
  LengthRev = 0
  Placement = pos=(101.3,29,65.23) rot=(0,1,0;1.5708rad)
  Solid = true
  Symmetric = false
FEATURE [Part::Box] Box011  label="frontCaseScrewPillarBracket"
  AttacherType = Attacher::AttachEngine3D
  Height = 2.4
  Length = 16
  Placement = pos=(87,28,2.3) rot=(0,0,1;0rad)
  Width = 7
FEATURE [Part::Box] Box012  label="frontCaseScrewPillarBracket001"
  AttacherType = Attacher::AttachEngine3D
  Height = 2.4
  Length = 16
  Placement = pos=(87,28,67.3) rot=(0,0,1;0rad)
  Width = 7
FEATURE [Sketcher::SketchObject] Sketch026
  FullyConstrained = true
  sketch-geometry (17):
    g0: Circle CenterX=-3.5 CenterY=23.5 CenterZ=0 NormalX=0 NormalY=0 NormalZ=1 AngleXU=0 Radius=1
    g1: Circle CenterX=-1 CenterY=15.25 CenterZ=0 NormalX=0 NormalY=0 NormalZ=1 AngleXU=0 Radius=1
    g2: Circle CenterX=-3.5 CenterY=7 CenterZ=0 NormalX=0 NormalY=0 NormalZ=1 AngleXU=0 Radius=1
    g3: BSplineCurve PolesCount=3 KnotsCount=2 Degree=2 IsPeriodic=0
    g4: GeomPoint X=-3.5 Y=23.5 Z=0
    g5: GeomPoint X=-3.5 Y=7 Z=0
    g6: Circle CenterX=-4.8 CenterY=30.5 CenterZ=0 NormalX=0 NormalY=0 NormalZ=1 AngleXU=0 Radius=1
    g7: Circle CenterX=-3.5 CenterY=30.5 CenterZ=0 NormalX=0 NormalY=0 NormalZ=1 AngleXU=0 Radius=1
    g8: Circle CenterX=-3.5 CenterY=29.2 CenterZ=0 NormalX=0 NormalY=0 NormalZ=1 AngleXU=0 Radius=1
    g9: BSplineCurve PolesCount=3 KnotsCount=2 Degree=2 IsPeriodic=0
    g10: GeomPoint X=-4.8 Y=30.5 Z=0
    g11: GeomPoint X=-3.5 Y=29.2 Z=0
    g12: LineSegment StartX=-3.5 StartY=29.2 StartZ=0 EndX=-3.5 EndY=23.5 EndZ=0
    g13: LineSegment StartX=-4.8 StartY=30.5 StartZ=0 EndX=0 EndY=30.5 EndZ=0
    g14: LineSegment StartX=-3.5 StartY=5 StartZ=0 EndX=-3.5 EndY=7 EndZ=0
    g15: LineSegment StartX=0 StartY=5 StartZ=0 EndX=0 EndY=30.5 EndZ=0
    g16: LineSegment StartX=-3.5 StartY=5 StartZ=0 EndX=0 EndY=5 EndZ=0
  constraints (33):
    c: Weight(g0) = 1
    c: Equal(g0,g1)
    c: Equal(g0,g2)
    c: InternalAlignment(g0,g3)
    c: InternalAlignment(g1,g3)
    c: InternalAlignment(g2,g3)
    c: InternalAlignment(g4,g3)
    c: InternalAlignment(g5,g3)
    c: Block(g3)
    c: Weight(g6) = 1
    c: Equal(g6,g7)
    c: Equal(g6,g8)
    c: InternalAlignment(g6,g9)
    c: InternalAlignment(g7,g9)
    c: InternalAlignment(g8,g9)
    c: InternalAlignment(g10,g9)
    c: InternalAlignment(g11,g9)
    c: Block(g9)
    c: Coincident(g12,g9)
    c: Coincident(g12,g3)
    c: Vertical(g12)
    c: Coincident(g13,g9)
    c: Horizontal(g13)
    c: Distance(g13) = 4.8
    c: Coincident(g14,g3)
    c: Vertical(g14)
    c: Coincident(g15,g13)
    c: Vertical(g15)
    c: Tangent(g15,g1)
    c: Distance(g14) = 2
    c: Coincident(g16,g14)
    c: Horizontal(g16)
    c: Coincident(g15,g16)
FEATURE [Part::Feature] Face050
  shape: bbox 4.8 x 25.5 x 2e-07 mm, 1 faces, 0 solids (baked)
FEATURE [Part::Revolution] Revolve054  label="moreFrontCaseScrewPost001"
  Angle = 360
  Axis = (0,1,0)
  Base = (0,0,0)
  FaceMakerClass = Part::FaceMakerBullseye
  Placement = pos=(102.5,4.5,3.5) rot=(0,0,1;0rad)
  Solid = false
  Source = -> Face050
  Symmetric = false
FEATURE [Part::Feature] Face051
  shape: bbox 4.8 x 25.5 x 2e-07 mm, 1 faces, 0 solids (baked)
FEATURE [Part::Revolution] Revolve055  label="moreFrontCaseScrewPost002"
  Angle = 360
  Axis = (0,1,0)
  Base = (0,0,0)
  FaceMakerClass = Part::FaceMakerBullseye
  Placement = pos=(102.5,4.5,68.5) rot=(0,0,1;0rad)
  Solid = false
  Source = -> Face051
  Symmetric = false
FEATURE [Sketcher::SketchObject] Sketch027
  FullyConstrained = true
  sketch-geometry (10):
    g0: LineSegment StartX=-1.6 StartY=4.7 StartZ=0 EndX=-1.6 EndY=1.7 EndZ=0
    g1: LineSegment StartX=-3.5 StartY=4.7 StartZ=0 EndX=-1.6 EndY=4.7 EndZ=0
    g2: LineSegment StartX=-1.6 StartY=1.7 StartZ=0 EndX=-1.6 EndY=1.5 EndZ=0
    g3: LineSegment StartX=-1.6 StartY=1.5 StartZ=0 EndX=-5.2 EndY=1.5 EndZ=0
    g4: Circle CenterX=-3.5 CenterY=4.7 CenterZ=0 NormalX=0 NormalY=0 NormalZ=1 AngleXU=0 Radius=1
    g5: Circle CenterX=-3.59627 CenterY=2.99743 CenterZ=0 NormalX=0 NormalY=0 NormalZ=1 AngleXU=0 Radius=1
    g6: Circle CenterX=-5.2 CenterY=1.5 CenterZ=0 NormalX=0 NormalY=0 NormalZ=1 AngleXU=0 Radius=1
    g7: BSplineCurve PolesCount=3 KnotsCount=2 Degree=2 IsPeriodic=0
    g8: GeomPoint X=-3.5 Y=4.7 Z=0
    g9: GeomPoint X=-5.2 Y=1.5 Z=0
  constraints (23):
    c: Vertical(g0)
    c: Distance(g0) = 3
    c: Coincident(g1,g0)
    c: Horizontal(g1)
    c: Block(g0)
    c: Block(g1)
    c: Coincident(g2,g0)
    c: Vertical(g2)
    c: Distance(g2) = 0.2
    c: Coincident(g3,g2)
    c: Horizontal(g3)
    c: Block(g3)
    c: Coincident(g7,g1)
    c: Weight(g4) = 1
    c: Equal(g4,g5)
    c: Equal(g4,g6)
    c: Coincident(g7,g3)
    c: InternalAlignment(g4,g7)
    c: InternalAlignment(g5,g7)
    c: InternalAlignment(g6,g7)
    c: InternalAlignment(g8,g7)
    c: InternalAlignment(g9,g7)
    c: Block(g7)
FEATURE [Sketcher::SketchObject] Sketch028
  FullyConstrained = true
  sketch-geometry (18):
    g0: LineSegment StartX=0 StartY=3e-16 StartZ=0 EndX=0 EndY=1.7 EndZ=0
    g1: LineSegment StartX=-3.5 StartY=0 StartZ=0 EndX=-3.5 EndY=0.9 EndZ=0
    g2: Circle CenterX=-2.7 CenterY=1.7 CenterZ=0 NormalX=0 NormalY=0 NormalZ=1 AngleXU=0 Radius=1
    g3: Circle CenterX=-3.5 CenterY=1.7 CenterZ=0 NormalX=0 NormalY=0 NormalZ=1 AngleXU=0 Radius=1
    g4: Circle CenterX=-3.5 CenterY=0.9 CenterZ=0 NormalX=0 NormalY=0 NormalZ=1 AngleXU=0 Radius=1
    g5: BSplineCurve PolesCount=3 KnotsCount=2 Degree=2 IsPeriodic=0
    g6: GeomPoint X=-2.7 Y=1.7 Z=0
    g7: GeomPoint X=-3.5 Y=0.9 Z=0
    g8: LineSegment StartX=-3.5 StartY=0 StartZ=0 EndX=-3.5 EndY=-7 EndZ=0
    g9: LineSegment StartX=0 StartY=3e-16 StartZ=0 EndX=0 EndY=-7 EndZ=0
    g10: LineSegment StartX=-3.5 StartY=-7 StartZ=0 EndX=0 EndY=-7 EndZ=0
    g11: LineSegment StartX=-2.7 StartY=1.7 StartZ=0 EndX=-1.6 EndY=1.7 EndZ=0
    g12: LineSegment StartX=0 StartY=1.7 StartZ=0 EndX=0 EndY=4.5 EndZ=0
    g13: LineSegment StartX=0 StartY=4.5 StartZ=0 EndX=0 EndY=10.8 EndZ=0
    g14: LineSegment StartX=0 StartY=10.8 StartZ=0 EndX=-2 EndY=10.8 EndZ=0
    g15: LineSegment StartX=-1.6 StartY=4.7 StartZ=0 EndX=-1.6 EndY=1.7 EndZ=0
    g16: LineSegment StartX=-1.6 StartY=4.7 StartZ=0 EndX=-2 EndY=4.7 EndZ=0
    g17: LineSegment StartX=-2 StartY=4.7 StartZ=0 EndX=-2 EndY=10.8 EndZ=0
  constraints (44):
    c: Vertical(g0)
    c: Vertical(g1)
    c: Distance(g1) = 0.9
    c: Block(g0)
    c: Distance(g0) = 1.7
    c: Weight(g2) = 1
    c: Equal(g2,g3)
    c: Equal(g2,g4)
    c: Coincident(g5,g1)
    c: InternalAlignment(g2,g5)
    c: InternalAlignment(g3,g5)
    c: InternalAlignment(g4,g5)
    c: InternalAlignment(g6,g5)
    c: InternalAlignment(g7,g5)
    c: Block(g5)
    c: Coincident(g8,g1)
    c: Vertical(g8)
    c: Distance(g8) = 7
    c: Vertical(g9)
    c: Equal(g8,g9) = 7
    c: Coincident(g9,g0)
    c: Coincident(g10,g8)
    c: Coincident(g10,g9)
    c: Horizontal(g10)
    c: Coincident(g11,g5)
    c: Horizontal(g11)
    c: Coincident(g12,g0)
    c: Vertical(g12)
    c: Distance(g12) = 2.8
    c: Coincident(g13,g12)
    c: Vertical(g13)
    c: Distance(g13) = 6.3
    c: Coincident(g14,g13)
    c: Horizontal(g14)
    c: Distance(g14) = 2
    c: Vertical(g15)
    c: Distance(g15) = 3
    c: Block(g11)
    c: Coincident(g15,g11)
    c: Coincident(g16,g15)
    c: Horizontal(g16)
    c: Coincident(g17,g16)
    c: Coincident(g17,g14)
    c: Vertical(g17)
FEATURE [Part::Revolution] Revolve040  label="backCaseScrewRetainer001"
  Angle = 360
  Axis = (0,1,0)
  Base = (0,0,0)
  FaceMakerClass = Part::FaceMakerBullseye
  Placement = pos=(12.5,3,10) rot=(0,0,1;0rad)
  Solid = false
  Source = -> Face036
  Symmetric = false
FEATURE [Part::Feature] Face055
  shape: bbox 3.5 x 30.2 x 2e-07 mm, 1 faces, 0 solids (baked)
FEATURE [Part::Revolution] Revolve059  label="backCaseScrewPost"
  Angle = 360
  Axis = (0,1,0)
  Base = (0,0,0)
  FaceMakerClass = Part::FaceMakerBullseye
  Placement = pos=(12.5,4.5,10) rot=(0,0,1;0rad)
  Solid = false
  Source = -> Face055
  Symmetric = false
FEATURE [Part::Feature] Face056
  shape: bbox 3.5 x 30.2 x 2e-07 mm, 1 faces, 0 solids (baked)
FEATURE [Part::Revolution] Revolve060  label="backCaseScrewPost001"
  Angle = 360
  Axis = (0,1,0)
  Base = (0,0,0)
  FaceMakerClass = Part::FaceMakerBullseye
  Placement = pos=(12.5,4.5,62) rot=(0,0,1;0rad)
  Solid = false
  Source = -> Face056
  Symmetric = false
FEATURE [Part::Feature] Face057
  shape: bbox 3.5 x 17.8 x 2e-07 mm, 1 faces, 0 solids (baked)
FEATURE [Part::Revolution] Revolve061  label="removeToCreateScrewAndThreadedInsertHole"
  Angle = 360
  Axis = (0,1,0)
  Base = (0,0,0)
  FaceMakerClass = Part::FaceMakerBullseye
  Placement = pos=(12.5,0,10) rot=(0,0,1;0rad)
  Solid = false
  Source = -> Face057
  Symmetric = false
FEATURE [Part::Feature] Face058
  shape: bbox 3.5 x 17.8 x 2e-07 mm, 1 faces, 0 solids (baked)
FEATURE [Part::Revolution] Revolve062  label="removeToCreateScrewAndThreadedInsertHole001"
  Angle = 360
  Axis = (0,1,0)
  Base = (0,0,0)
  FaceMakerClass = Part::FaceMakerBullseye
  Placement = pos=(12.5,0,62) rot=(0,0,1;0rad)
  Solid = false
  Source = -> Face058
  Symmetric = false
FEATURE [Part::Feature] Face059
  shape: bbox 3.5 x 17.8 x 2e-07 mm, 1 faces, 0 solids (baked)
FEATURE [Part::Revolution] Revolve063  label="removeToCreateScrewAndThreadedInsertHole002"
  Angle = 360
  Axis = (0,1,0)
  Base = (0,0,0)
  FaceMakerClass = Part::FaceMakerBullseye
  Placement = pos=(89.5,0,68.5) rot=(0,0,1;0rad)
  Solid = false
  Source = -> Face059
  Symmetric = false
FEATURE [Part::Feature] Face060
  shape: bbox 3.5 x 17.8 x 2e-07 mm, 1 faces, 0 solids (baked)
FEATURE [Part::Revolution] Revolve064  label="removeToCreateScrewAndThreadedInsertHole003"
  Angle = 360
  Axis = (0,1,0)
  Base = (0,0,0)
  FaceMakerClass = Part::FaceMakerBullseye
  Placement = pos=(89.5,0,3.5) rot=(0,0,1;0rad)
  Solid = false
  Source = -> Face060
  Symmetric = false
FEATURE [Part::Feature] Face061
  shape: bbox 3.5 x 17.8 x 2e-07 mm, 1 faces, 0 solids (baked)
FEATURE [Part::Revolution] Revolve065  label="removeToCreateScrewAndThreadedInsertHole004"
  Angle = 360
  Axis = (0,1,0)
  Base = (0,0,0)
  FaceMakerClass = Part::FaceMakerBullseye
  Placement = pos=(102.5,4.7,3.5) rot=(0,0,1;0rad)
  Solid = false
  Source = -> Face061
  Symmetric = false
FEATURE [Part::Feature] Face062
  shape: bbox 3.5 x 17.8 x 2e-07 mm, 1 faces, 0 solids (baked)
FEATURE [Part::Revolution] Revolve066  label="removeToCreateScrewAndThreadedInsertHole005"
  Angle = 360
  Axis = (0,1,0)
  Base = (0,0,0)
  FaceMakerClass = Part::FaceMakerBullseye
  Placement = pos=(102.5,4.7,68.5) rot=(0,0,1;0rad)
  Solid = false
  Source = -> Face062
  Symmetric = false
FEATURE [Part::MultiFuse] Fusion047  label="makeHoles"
  Shapes = -> [Revolve066,Revolve065,Revolve064,Revolve063,Revolve062,Revolve061]
FEATURE [Part::Feature] Face063
  shape: bbox 3.6 x 3.2 x 2e-07 mm, 1 faces, 0 solids (baked)
FEATURE [Part::Revolution] Revolve067  label="moreFrontCaseScrewRetainer002"
  Angle = 360
  Axis = (0,1,0)
  Base = (0,0,0)
  FaceMakerClass = Part::FaceMakerBullseye
  Placement = pos=(102.5,4.5,68.5) rot=(0,0,1;0rad)
  Solid = false
  Source = -> Face063
  Symmetric = false
FEATURE [Part::Feature] Face064
  shape: bbox 3.6 x 3.2 x 2e-07 mm, 1 faces, 0 solids (baked)
FEATURE [Part::Revolution] Revolve068  label="moreFrontCaseScrewRetainer003"
  Angle = 360
  Axis = (0,1,0)
  Base = (0,0,0)
  FaceMakerClass = Part::FaceMakerBullseye
  Placement = pos=(102.5,4.5,3.5) rot=(0,0,1;0rad)
  Solid = false
  Source = -> Face064
  Symmetric = false
FEATURE [Part::Feature] Face065
  shape: bbox 3.5 x 17.8 x 2e-07 mm, 1 faces, 0 solids (baked)
FEATURE [Part::Revolution] Revolve069  label="removeToCreateScrewAndThreadedInsertHole006"
  Angle = 360
  Axis = (0,1,0)
  Base = (0,0,0)
  FaceMakerClass = Part::FaceMakerBullseye
  Placement = pos=(12.5,0,10) rot=(0,0,1;0rad)
  Solid = false
  Source = -> Face065
  Symmetric = false
FEATURE [Part::Feature] Face066
  shape: bbox 3.5 x 17.8 x 2e-07 mm, 1 faces, 0 solids (baked)
FEATURE [Part::Revolution] Revolve070  label="removeToCreateScrewAndThreadedInsertHole007"
  Angle = 360
  Axis = (0,1,0)
  Base = (0,0,0)
  FaceMakerClass = Part::FaceMakerBullseye
  Placement = pos=(12.5,0,62) rot=(0,0,1;0rad)
  Solid = false
  Source = -> Face066
  Symmetric = false
FEATURE [Part::Feature] Face067
  shape: bbox 3.5 x 17.8 x 2e-07 mm, 1 faces, 0 solids (baked)
FEATURE [Part::Revolution] Revolve071  label="removeToCreateScrewAndThreadedInsertHole008"
  Angle = 360
  Axis = (0,1,0)
  Base = (0,0,0)
  FaceMakerClass = Part::FaceMakerBullseye
  Placement = pos=(89.5,0,68.5) rot=(0,0,1;0rad)
  Solid = false
  Source = -> Face067
  Symmetric = false
FEATURE [Part::Feature] Face068
  shape: bbox 3.5 x 17.8 x 2e-07 mm, 1 faces, 0 solids (baked)
FEATURE [Part::Revolution] Revolve072  label="removeToCreateScrewAndThreadedInsertHole009"
  Angle = 360
  Axis = (0,1,0)
  Base = (0,0,0)
  FaceMakerClass = Part::FaceMakerBullseye
  Placement = pos=(89.5,0,3.5) rot=(0,0,1;0rad)
  Solid = false
  Source = -> Face068
  Symmetric = false
FEATURE [Part::Feature] Face069
  shape: bbox 3.5 x 17.8 x 2e-07 mm, 1 faces, 0 solids (baked)
FEATURE [Part::Feature] Face070
  shape: bbox 3.5 x 17.8 x 2e-07 mm, 1 faces, 0 solids (baked)
FEATURE [Part::Revolution] Revolve073  label="removeToCreateScrewAndThreadedInsertHole010"
  Angle = 360
  Axis = (0,1,0)
  Base = (0,0,0)
  FaceMakerClass = Part::FaceMakerBullseye
  Placement = pos=(102.5,4.7,3.5) rot=(0,0,1;0rad)
  Solid = false
  Source = -> Face069
  Symmetric = false
FEATURE [Part::Revolution] Revolve074  label="removeToCreateScrewAndThreadedInsertHole011"
  Angle = 360
  Axis = (0,1,0)
  Base = (0,0,0)
  FaceMakerClass = Part::FaceMakerBullseye
  Placement = pos=(102.5,4.7,68.5) rot=(0,0,1;0rad)
  Solid = false
  Source = -> Face070
  Symmetric = false
FEATURE [Part::MultiFuse] Fusion048  label="makeHoles001"
  Shapes = -> [Revolve074,Revolve073,Revolve072,Revolve071,Revolve070,Revolve069]
FEATURE [Part::MultiFuse] Fusion049  label="caseScrewRetainers"
  Shapes = -> [Revolve067,Revolve068,Revolve048,Revolve047,Revolve039,Revolve040]
FEATURE [Part::Cut] Cut015  label="caseScrewRetainers001"
  Base = -> Fusion049
  Tool = -> Fusion048
FEATURE [Part::MultiFuse] Fusion050  label="casePillars"
  Shapes = -> [Revolve055,Revolve054,Revolve043,Revolve046,Revolve059,Revolve060]
FEATURE [Part::Feature] Face071 .. Face076  x6 (patterned run collapsed; names and placements below)
  shape: bbox 3.5 x 17.8 x 2e-07 mm, 1 faces, 0 solids (baked)
FEATURE [Part::Revolution] Revolve075  label="removeToCreateScrewAndThreadedInsertHole012"
  Angle = 360
  Axis = (0,1,0)
  Base = (0,0,0)
  FaceMakerClass = Part::FaceMakerBullseye
  Placement = pos=(12.5,0,10) rot=(0,0,1;0rad)
  Solid = false
  Source = -> Face071
  Symmetric = false
FEATURE [Part::Revolution] Revolve076  label="removeToCreateScrewAndThreadedInsertHole013"
  Angle = 360
  Axis = (0,1,0)
  Base = (0,0,0)
  FaceMakerClass = Part::FaceMakerBullseye
  Placement = pos=(12.5,0,62) rot=(0,0,1;0rad)
  Solid = false
  Source = -> Face072
  Symmetric = false
FEATURE [Part::Revolution] Revolve077  label="removeToCreateScrewAndThreadedInsertHole014"
  Angle = 360
  Axis = (0,1,0)
  Base = (0,0,0)
  FaceMakerClass = Part::FaceMakerBullseye
  Placement = pos=(89.5,0,68.5) rot=(0,0,1;0rad)
  Solid = false
  Source = -> Face073
  Symmetric = false
FEATURE [Part::Revolution] Revolve078  label="removeToCreateScrewAndThreadedInsertHole015"
  Angle = 360
  Axis = (0,1,0)
  Base = (0,0,0)
  FaceMakerClass = Part::FaceMakerBullseye
  Placement = pos=(89.5,0,3.5) rot=(0,0,1;0rad)
  Solid = false
  Source = -> Face074
  Symmetric = false
FEATURE [Part::Revolution] Revolve079  label="removeToCreateScrewAndThreadedInsertHole016"
  Angle = 360
  Axis = (0,1,0)
  Base = (0,0,0)
  FaceMakerClass = Part::FaceMakerBullseye
  Placement = pos=(102.5,4.7,3.5) rot=(0,0,1;0rad)
  Solid = false
  Source = -> Face075
  Symmetric = false
FEATURE [Part::Revolution] Revolve080  label="removeToCreateScrewAndThreadedInsertHole017"
  Angle = 360
  Axis = (0,1,0)
  Base = (0,0,0)
  FaceMakerClass = Part::FaceMakerBullseye
  Placement = pos=(102.5,4.7,68.5) rot=(0,0,1;0rad)
  Solid = false
  Source = -> Face076
  Symmetric = false
FEATURE [Part::MultiFuse] Fusion051  label="makeHoles002"
  Shapes = -> [Revolve080,Revolve079,Revolve078,Revolve077,Revolve076,Revolve075]
FEATURE [Part::Cut] Cut016  label="caesPillars"
  Base = -> Fusion050
  Tool = -> Fusion051
FEATURE [Part::Revolution] Revolve009  label="plugHousing016"
  Angle = 360
  Axis = (0,1,0)
  Base = (0,0,0)
  FaceMakerClass = Part::FaceMakerBullseye
  Placement = pos=(0,0,36.15) rot=(0,0,1;0rad)
  Solid = false
  Source = -> Face012
  Symmetric = false
FEATURE [Part::MultiFuse] Fusion014  label="plugHousing023"
  Placement = pos=(0,0,0) rot=(0,0,1;1.5708rad)
  Shapes = -> [Revolve011,Revolve009]
FEATURE [Part::Revolution] Revolve010  label="plugHousing017"
  Angle = 360
  Axis = (0,1,0)
  Base = (0,0,0)
  FaceMakerClass = Part::FaceMakerBullseye
  Placement = pos=(0,0,36.15) rot=(0,0,1;0rad)
  Solid = false
  Source = -> Face014
  Symmetric = false
FEATURE [Part::MultiFuse] Fusion015  label="plugHousing024"
  Placement = pos=(0,0,0) rot=(0,0,1;1.5708rad)
  Shapes = -> [Revolve010,Revolve015]
FEATURE [Part::Revolution] Revolve014  label="plugHousing026"
  Angle = 360
  Axis = (0,1,0)
  Base = (0,0,0)
  FaceMakerClass = Part::FaceMakerBullseye
  Placement = pos=(0,0,36.15) rot=(0,0,1;0rad)
  Solid = false
  Source = -> Face011
  Symmetric = false
FEATURE [Part::Revolution] Revolve013  label="plugHousing025"
  Angle = 360
  Axis = (0,1,0)
  Base = (0,0,0)
  FaceMakerClass = Part::FaceMakerBullseye
  Placement = pos=(0,0,36.15) rot=(0,0,1;0rad)
  Solid = false
  Source = -> Face015
  Symmetric = false
FEATURE [Part::MultiFuse] Fusion016  label="plugHousing028"
  Placement = pos=(0,19,0) rot=(0,0,1;3.14159rad)
  Shapes = -> [Fusion014,Fusion013]
FEATURE [Part::MultiFuse] Fusion011  label="plugHousing018"
  Placement = pos=(0,0,0) rot=(0,0,1;1.5708rad)
  Shapes = -> [Revolve014,Revolve013]
FEATURE [Part::MultiFuse] Fusion012  label="plugHousing019"
  Placement = pos=(0,19,0) rot=(0,0,1;3.14159rad)
  Shapes = -> [Fusion011,Fusion015]
FEATURE [Part::MultiFuse] Fusion017  label="plugHousing029"
  Placement = pos=(122.621,0,-0.15) rot=(0,0,1;0rad)
  Shapes = -> [Fusion016,Fusion012]
FEATURE [Part::MultiFuse] Fusion052  label="casePillarRetainers"
  Shapes = -> [Extrude012,Extrude013,Extrude014,Extrude015,Extrude016,Extrude017,Extrude018,Extrude019,Box011,Box012]
FEATURE [Part::Feature] Face077
  shape: bbox 3.5 x 17.8 x 2e-07 mm, 1 faces, 0 solids (baked)
FEATURE [Part::Revolution] Revolve081  label="removeToCreateScrewAndThreadedInsertHole018"
  Angle = 360
  Axis = (0,1,0)
  Base = (0,0,0)
  FaceMakerClass = Part::FaceMakerBullseye
  Placement = pos=(62.3,30.3,19.7) rot=(0,0,1;0rad)
  Solid = false
  Source = -> Face077
  Symmetric = false
FEATURE [Part::Feature] Face078
  shape: bbox 3.5 x 17.8 x 2e-07 mm, 1 faces, 0 solids (baked)
FEATURE [Part::Revolution] Revolve082  label="removeToCreateScrewAndThreadedInsertHole019"
  Angle = 360
  Axis = (0,1,0)
  Base = (0,0,0)
  FaceMakerClass = Part::FaceMakerBullseye
  Placement = pos=(62.3,30.3,51.7) rot=(0,0,1;0rad)
  Solid = false
  Source = -> Face078
  Symmetric = false
FEATURE [Part::Feature] Face079
  shape: bbox 3.5 x 17.8 x 2e-07 mm, 1 faces, 0 solids (baked)
FEATURE [Part::Revolution] Revolve083  label="removeToCreateScrewAndThreadedInsertHole020"
  Angle = 360
  Axis = (0,1,0)
  Base = (0,0,0)
  FaceMakerClass = Part::FaceMakerBullseye
  Placement = pos=(30.3,30.3,19.7) rot=(0,0,1;0rad)
  Solid = false
  Source = -> Face079
  Symmetric = false
FEATURE [Part::Feature] Face080
  shape: bbox 3.5 x 17.8 x 2e-07 mm, 1 faces, 0 solids (baked)
FEATURE [Part::Revolution] Revolve084  label="removeToCreateScrewAndThreadedInsertHole021"
  Angle = 360
  Axis = (0,1,0)
  Base = (0,0,0)
  FaceMakerClass = Part::FaceMakerBullseye
  Placement = pos=(30.3,30.3,51.7) rot=(0,0,1;0rad)
  Solid = false
  Source = -> Face080
  Symmetric = false
FEATURE [Part::MultiFuse] Fusion053  label="createThreadedInsertHolesForFan"
  Shapes = -> [Revolve081,Revolve082,Revolve083,Revolve084]
FEATURE [Part::Cut] Cut017  label="fanScrewHousing001"
  Base = -> Fusion046
  Tool = -> Fusion053
FEATURE [Part::Feature] Face081
  shape: bbox 3.5 x 17.8 x 2e-07 mm, 1 faces, 0 solids (baked)
FEATURE [Part::Revolution] Revolve085  label="removeToCreateScrewAndThreadedInsertHole022"
  Angle = 360
  Axis = (0,1,0)
  Base = (0,0,0)
  FaceMakerClass = Part::FaceMakerBullseye
  Placement = pos=(62.3,30.3,19.7) rot=(0,0,1;0rad)
  Solid = false
  Source = -> Face081
  Symmetric = false
FEATURE [Part::Feature] Face082
  shape: bbox 3.5 x 17.8 x 2e-07 mm, 1 faces, 0 solids (baked)
FEATURE [Part::Revolution] Revolve086  label="removeToCreateScrewAndThreadedInsertHole023"
  Angle = 360
  Axis = (0,1,0)
  Base = (0,0,0)
  FaceMakerClass = Part::FaceMakerBullseye
  Placement = pos=(62.3,30.3,51.7) rot=(0,0,1;0rad)
  Solid = false
  Source = -> Face082
  Symmetric = false
FEATURE [Part::Feature] Face083
  shape: bbox 3.5 x 17.8 x 2e-07 mm, 1 faces, 0 solids (baked)
FEATURE [Part::Revolution] Revolve087  label="removeToCreateScrewAndThreadedInsertHole024"
  Angle = 360
  Axis = (0,1,0)
  Base = (0,0,0)
  FaceMakerClass = Part::FaceMakerBullseye
  Placement = pos=(30.3,30.3,19.7) rot=(0,0,1;0rad)
  Solid = false
  Source = -> Face083
  Symmetric = false
FEATURE [Part::Feature] Face084
  shape: bbox 3.5 x 17.8 x 2e-07 mm, 1 faces, 0 solids (baked)
FEATURE [Part::Revolution] Revolve088  label="removeToCreateScrewAndThreadedInsertHole025"
  Angle = 360
  Axis = (0,1,0)
  Base = (0,0,0)
  FaceMakerClass = Part::FaceMakerBullseye
  Placement = pos=(30.3,30.3,51.7) rot=(0,0,1;0rad)
  Solid = false
  Source = -> Face084
  Symmetric = false
FEATURE [Part::MultiFuse] Fusion054  label="createThreadedInsertHolesForFan001"
  Shapes = -> [Revolve085,Revolve086,Revolve087,Revolve088]
FEATURE [Part::Cut] Cut018  label="top007"
  Base = -> Fusion040
  Tool = -> Fusion054
FEATURE [Sketcher::SketchObject] Sketch029
  FullyConstrained = false
  Placement = pos=(0,0,0) rot=(1,0,0;1.5708rad)
  sketch-geometry (24):
    g0: ArcOfCircle CenterX=-4 CenterY=-10.5 CenterZ=0 NormalX=0 NormalY=0 NormalZ=1 AngleXU=0 Radius=1.5 StartAngle=6e-16 EndAngle=3.14159
    g1: ArcOfCircle CenterX=-34.2 CenterY=-10.5 CenterZ=0 NormalX=0 NormalY=0 NormalZ=1 AngleXU=0 Radius=1.5 StartAngle=0 EndAngle=3.14159
    g2: ArcOfCircle CenterX=-34.2 CenterY=-27.7 CenterZ=0 NormalX=0 NormalY=0 NormalZ=1 AngleXU=0 Radius=1.5 StartAngle=3.14159 EndAngle=6.28319
    g3: ArcOfCircle CenterX=-4 CenterY=-27.7 CenterZ=0 NormalX=0 NormalY=0 NormalZ=1 AngleXU=0 Radius=1.5 StartAngle=3.1416 EndAngle=6.28319
    g4: ArcOfCircle CenterX=-10 CenterY=-4.3 CenterZ=0 NormalX=0 NormalY=0 NormalZ=1 AngleXU=0 Radius=1.5 StartAngle=2e-16 EndAngle=3.14159
    g5: ArcOfCircle CenterX=-16.1 CenterY=-1.8 CenterZ=0 NormalX=0 NormalY=0 NormalZ=1 AngleXU=0 Radius=1.5 StartAngle=5e-16 EndAngle=3.14159
    g6: ArcOfCircle CenterX=-22.1 CenterY=-1.8 CenterZ=0 NormalX=0 NormalY=0 NormalZ=1 AngleXU=0 Radius=1.5 StartAngle=5e-16 EndAngle=3.14159
    g7: ArcOfCircle CenterX=-28.2 CenterY=-4.3 CenterZ=0 NormalX=0 NormalY=0 NormalZ=1 AngleXU=0 Radius=1.5 StartAngle=2e-16 EndAngle=3.14159
    g8: ArcOfCircle CenterX=-10 CenterY=-33.9 CenterZ=0 NormalX=0 NormalY=0 NormalZ=1 AngleXU=0 Radius=1.5 StartAngle=3.14159 EndAngle=6.28319
    g9: ArcOfCircle CenterX=-16.1 CenterY=-36.4 CenterZ=0 NormalX=0 NormalY=0 NormalZ=1 AngleXU=0 Radius=1.5 StartAngle=3.14159 EndAngle=6.28319
    g10: ArcOfCircle CenterX=-22.1 CenterY=-36.4 CenterZ=0 NormalX=0 NormalY=0 NormalZ=1 AngleXU=0 Radius=1.5 StartAngle=3.14159 EndAngle=6.28319
    g11: ArcOfCircle CenterX=-28.2 CenterY=-33.9 CenterZ=0 NormalX=0 NormalY=0 NormalZ=1 AngleXU=0 Radius=1.5 StartAngle=3.14159 EndAngle=6.28319
    g12: LineSegment StartX=-35.7 StartY=-10.5 StartZ=0 EndX=-35.7 EndY=-27.7 EndZ=0
    g13: LineSegment StartX=-32.7 StartY=-10.5 StartZ=0 EndX=-32.7 EndY=-27.7 EndZ=0
    g14: LineSegment StartX=-29.7 StartY=-33.9 StartZ=0 EndX=-29.7 EndY=-4.3 EndZ=0
    g15: LineSegment StartX=-26.7 StartY=-33.9 StartZ=0 EndX=-26.7 EndY=-4.3 EndZ=0
    g16: LineSegment StartX=-2.5 StartY=-10.5 StartZ=0 EndX=-2.5 EndY=-27.7 EndZ=0
    g17: LineSegment StartX=-8.5 StartY=-4.3 StartZ=0 EndX=-8.5 EndY=-33.9 EndZ=0
    g18: LineSegment StartX=-5.5 StartY=-10.5 StartZ=0 EndX=-5.5 EndY=-27.7 EndZ=0
    g19: LineSegment StartX=-11.5 StartY=-4.3 StartZ=0 EndX=-11.5 EndY=-33.9 EndZ=0
    g20: LineSegment StartX=-14.6 StartY=-1.8 StartZ=0 EndX=-14.6 EndY=-36.4 EndZ=0
    g21: LineSegment StartX=-17.6 StartY=-1.8 StartZ=0 EndX=-17.6 EndY=-36.4 EndZ=0
    g22: LineSegment StartX=-20.6 StartY=-36.4 StartZ=0 EndX=-20.6 EndY=-1.8 EndZ=0
    g23: LineSegment StartX=-23.6 StartY=-1.8 StartZ=0 EndX=-23.6 EndY=-36.4 EndZ=0
  constraints (48):
    c: Block(g0)
    c: Block(g1)
    c: Block(g2)
    c: Block(g3)
    c: Block(g4)
    c: Block(g5)
    c: Block(g6)
    c: Block(g7)
    c: Block(g8)
    c: Block(g9)
    c: Block(g10)
    c: Block(g11)
    c: Coincident(g12,g1)
    c: Coincident(g12,g2)
    c: Vertical(g12)
    c: Coincident(g13,g1)
    c: Coincident(g13,g2)
    c: Vertical(g13)
    c: Coincident(g14,g11)
    c: Coincident(g14,g7)
    c: Vertical(g14)
    c: Coincident(g15,g11)
    c: Coincident(g15,g7)
    c: Vertical(g15)
    c: Coincident(g16,g0)
    c: Coincident(g16,g3)
    c: Vertical(g16)
    c: Coincident(g17,g4)
    c: Coincident(g17,g8)
    c: Vertical(g17)
    c: Coincident(g18,g0)
    c: Coincident(g18,g3)
    c: Vertical(g18)
    c: Coincident(g19,g4)
    c: Coincident(g19,g8)
    c: Vertical(g19)
    c: Coincident(g20,g5)
    c: Coincident(g20,g9)
    c: Vertical(g20)
    c: Coincident(g21,g5)
    c: Coincident(g21,g9)
    c: Vertical(g21)
    c: Coincident(g22,g10)
    c: Coincident(g22,g6)
    c: Vertical(g22)
    c: Coincident(g23,g6)
    c: Coincident(g23,g10)
    c: Vertical(g23)
FEATURE [Part::Extrusion] Extrude020  label="removeToCreateFanGrillHoles"
  Base = -> Sketch029
  Dir = (0,-1,6e-16)
  DirMode = 2
  FaceMakerClass = Part::FaceMakerBullseye
  LengthFwd = 10
  LengthRev = 0
  Placement = pos=(65.4,44,54.82) rot=(0,0,1;0rad)
  Solid = true
  Symmetric = false
FEATURE [Part::MultiFuse] Fusion055  label="top008"
  Shapes = -> [Cut017,Cut018]
FEATURE [Part::Cut] Cut019  label="top009"
  Base = -> Fusion055
  Tool = -> Extrude020
FEATURE [App::MeasureDistance] Distance003  label="Distance: 71.95 mm"
  Distance = 71.9513
  P1 = (117,38,72)
  P2 = (117,38,0.0487319)
FEATURE [Sketcher::SketchObject] Sketch030
  FullyConstrained = true
  Placement = pos=(117,19,0) rot=(0.57735,0.57735,0.57735;2.0944rad)
  sketch-geometry (48):
    g0: LineSegment StartX=-49.19 StartY=69.25 StartZ=0 EndX=-49.19 EndY=66.25 EndZ=0
    g1: LineSegment StartX=-49.19 StartY=63.5 StartZ=0 EndX=-49.19 EndY=60.5 EndZ=0
    g2: LineSegment StartX=-49.19 StartY=57.75 StartZ=0 EndX=-49.19 EndY=54.75 EndZ=0
    g3: LineSegment StartX=-49.19 StartY=52 StartZ=0 EndX=-49.19 EndY=49 EndZ=0
    g4: LineSegment StartX=-49.19 StartY=46.25 StartZ=0 EndX=-49.19 EndY=43.25 EndZ=0
    g5: LineSegment StartX=-49.19 StartY=40.5 StartZ=0 EndX=-49.19 EndY=37.5 EndZ=0
    g6: LineSegment StartX=-49.19 StartY=34.5 StartZ=0 EndX=-49.19 EndY=31.5 EndZ=0
    g7: LineSegment StartX=-49.19 StartY=28.75 StartZ=0 EndX=-49.19 EndY=25.75 EndZ=0
    g8: LineSegment StartX=-49.19 StartY=23 StartZ=0 EndX=-49.19 EndY=20 EndZ=0
    g9: LineSegment StartX=-49.19 StartY=17.25 StartZ=0 EndX=-49.19 EndY=14.25 EndZ=0
    g10: LineSegment StartX=-49.19 StartY=11.5 StartZ=0 EndX=-49.19 EndY=8.5 EndZ=0
    g11: LineSegment StartX=-49.19 StartY=5.75 StartZ=0 EndX=-49.19 EndY=2.75 EndZ=0
    g12: ArcOfCircle CenterX=-1.5 CenterY=67.75 CenterZ=0 NormalX=0 NormalY=0 NormalZ=1 AngleXU=0 Radius=1.5 StartAngle=4.71239 EndAngle=7.85398
    g13: ArcOfCircle CenterX=-1.5 CenterY=62 CenterZ=0 NormalX=0 NormalY=0 NormalZ=1 AngleXU=0 Radius=1.5 StartAngle=4.71239 EndAngle=7.85398
    g14: ArcOfCircle CenterX=-1.5 CenterY=56.25 CenterZ=0 NormalX=0 NormalY=0 NormalZ=1 AngleXU=0 Radius=1.5 StartAngle=4.71239 EndAngle=7.85398
    g15: ArcOfCircle CenterX=-11.49 CenterY=50.5 CenterZ=0 NormalX=0 NormalY=0 NormalZ=1 AngleXU=0 Radius=1.5 StartAngle=4.71239 EndAngle=7.85398
    g16: ArcOfCircle CenterX=-16.28 CenterY=44.75 CenterZ=0 NormalX=0 NormalY=0 NormalZ=1 AngleXU=0 Radius=1.5 StartAngle=4.71239 EndAngle=7.85398
    g17: ArcOfCircle CenterX=-18.2337 CenterY=39 CenterZ=0 NormalX=0 NormalY=0 NormalZ=1 AngleXU=0 Radius=1.5 StartAngle=4.71485 EndAngle=7.85398
    g18: ArcOfCircle CenterX=-16.2837 CenterY=27.25 CenterZ=0 NormalX=0 NormalY=0 NormalZ=1 AngleXU=0 Radius=1.5 StartAngle=4.71485 EndAngle=7.85398
    g19: ArcOfCircle CenterX=-18.2337 CenterY=33 CenterZ=0 NormalX=0 NormalY=0 NormalZ=1 AngleXU=0 Radius=1.5 StartAngle=4.71485 EndAngle=7.85398
    g20: ArcOfCircle CenterX=-11.49 CenterY=21.5 CenterZ=0 NormalX=0 NormalY=0 NormalZ=1 AngleXU=0 Radius=1.5 StartAngle=4.71239 EndAngle=7.85398
    g21: ArcOfCircle CenterX=-1.5 CenterY=4.25 CenterZ=0 NormalX=0 NormalY=0 NormalZ=1 AngleXU=0 Radius=1.5 StartAngle=4.71239 EndAngle=7.85398
    g22: ArcOfCircle CenterX=-1.5 CenterY=10 CenterZ=0 NormalX=0 NormalY=0 NormalZ=1 AngleXU=0 Radius=1.5 StartAngle=4.71239 EndAngle=7.85398
    g23: ArcOfCircle CenterX=-1.5 CenterY=15.75 CenterZ=0 NormalX=0 NormalY=0 NormalZ=1 AngleXU=0 Radius=1.5 StartAngle=4.71239 EndAngle=7.85398
    g24: LineSegment StartX=-49.19 StartY=69.25 StartZ=0 EndX=-1.5 EndY=69.25 EndZ=0
    g25: LineSegment StartX=-49.19 StartY=66.25 StartZ=0 EndX=-1.5 EndY=66.25 EndZ=0
    g26: LineSegment StartX=-49.19 StartY=63.5 StartZ=0 EndX=-1.5 EndY=63.5 EndZ=0
    g27: LineSegment StartX=-49.19 StartY=60.5 StartZ=0 EndX=-1.5 EndY=60.5 EndZ=0
    g28: LineSegment StartX=-49.19 StartY=57.75 StartZ=0 EndX=-1.5 EndY=57.75 EndZ=0
    g29: LineSegment StartX=-49.19 StartY=54.75 StartZ=0 EndX=-1.5 EndY=54.75 EndZ=0
    g30: LineSegment StartX=-49.19 StartY=52 StartZ=0 EndX=-11.49 EndY=52 EndZ=0
    g31: LineSegment StartX=-49.19 StartY=49 StartZ=0 EndX=-11.49 EndY=49 EndZ=0
    g32: LineSegment StartX=-49.19 StartY=46.25 StartZ=0 EndX=-16.28 EndY=46.25 EndZ=0
    g33: LineSegment StartX=-49.19 StartY=43.25 StartZ=0 EndX=-16.28 EndY=43.25 EndZ=0
    g34: LineSegment StartX=-49.19 StartY=40.5 StartZ=0 EndX=-18.2337 EndY=40.5 EndZ=0
    g35: LineSegment StartX=-49.19 StartY=37.5 StartZ=0 EndX=-18.23 EndY=37.5 EndZ=0
    g36: LineSegment StartX=-49.19 StartY=34.5 StartZ=0 EndX=-18.2337 EndY=34.5 EndZ=0
    g37: LineSegment StartX=-49.19 StartY=31.5 StartZ=0 EndX=-18.23 EndY=31.5 EndZ=0
    g38: LineSegment StartX=-49.19 StartY=28.75 StartZ=0 EndX=-16.2837 EndY=28.75 EndZ=0
    g39: LineSegment StartX=-49.19 StartY=25.75 StartZ=0 EndX=-16.28 EndY=25.75 EndZ=0
    g40: LineSegment StartX=-49.19 StartY=23 StartZ=0 EndX=-11.49 EndY=23 EndZ=0
    g41: LineSegment StartX=-49.19 StartY=20 StartZ=0 EndX=-11.49 EndY=20 EndZ=0
    g42: LineSegment StartX=-49.19 StartY=17.25 StartZ=0 EndX=-1.5 EndY=17.25 EndZ=0
    g43: LineSegment StartX=-49.19 StartY=14.25 StartZ=0 EndX=-1.5 EndY=14.25 EndZ=0
    g44: LineSegment StartX=-49.19 StartY=11.5 StartZ=0 EndX=-1.5 EndY=11.5 EndZ=0
    g45: LineSegment StartX=-49.19 StartY=8.5 StartZ=0 EndX=-1.5 EndY=8.5 EndZ=0
    g46: LineSegment StartX=-49.19 StartY=5.75 StartZ=0 EndX=-1.5 EndY=5.75 EndZ=0
    g47: LineSegment StartX=-49.19 StartY=2.75 StartZ=0 EndX=-1.5 EndY=2.75 EndZ=0
  constraints (120):
    c: Vertical(g0)
    c: Distance(g0) = 3
    c: Block(g0)
    c: Vertical(g1)
    c: Distance(g1) = 3
    c: Vertical(g2)
    c: Equal(g0,g2) = 3
    c: Block(g2)
    c: Vertical(g3)
    c: Equal(g1,g3) = 3
    c: Vertical(g4)
    c: Equal(g0,g4) = 3
    c: Block(g4)
    c: Vertical(g5)
    c: Equal(g1,g5) = 3
    c: Vertical(g6)
    c: Equal(g0,g6) = 3
    c: Block(g6)
    c: Vertical(g7)
    c: Equal(g1,g7) = 3
    c: Vertical(g8)
    c: Equal(g0,g8) = 3
    c: Block(g8)
    c: Vertical(g9)
    c: Equal(g1,g9) = 3
    c: Vertical(g10)
    c: Equal(g0,g10) = 3
    c: Block(g10)
    c: Vertical(g11)
    c: Equal(g1,g11) = 3
    c: Block(g12)
    c: Block(g13)
    c: Block(g14)
    c: Block(g15)
    c: Block(g16)
    c: Block(g17)
    c: Block(g18)
    c: Block(g19)
    c: Block(g20)
    c: Block(g21)
    c: Block(g22)
    c: Block(g23)
    c: Block(g11)
    c: Block(g9)
    c: Block(g7)
    c: Block(g5)
    c: Block(g3)
    c: Block(g1)
    c: Coincident(g24,g0)
    c: Coincident(g24,g12)
    c: Horizontal(g24)
    c: Coincident(g25,g0)
    c: Coincident(g25,g12)
    c: Horizontal(g25)
    c: Coincident(g26,g1)
    c: Coincident(g26,g13)
    c: Horizontal(g26)
    c: Coincident(g27,g1)
    c: Coincident(g27,g13)
    c: Horizontal(g27)
    c: Coincident(g28,g2)
    c: Coincident(g28,g14)
    c: Horizontal(g28)
    c: Coincident(g29,g2)
    c: Coincident(g29,g14)
    c: Horizontal(g29)
    c: Coincident(g30,g3)
    c: Coincident(g30,g15)
    c: Horizontal(g30)
    c: Coincident(g31,g3)
    c: Coincident(g31,g15)
    c: Horizontal(g31)
    c: Coincident(g32,g4)
    c: Coincident(g32,g16)
    c: Horizontal(g32)
    c: Coincident(g33,g4)
    c: Coincident(g33,g16)
    c: Horizontal(g33)
    c: Coincident(g34,g5)
    c: Coincident(g34,g17)
    c: Horizontal(g34)
    c: Coincident(g35,g5)
    c: Coincident(g35,g17)
    c: Horizontal(g35)
    c: Coincident(g36,g6)
    c: Coincident(g36,g19)
    c: Horizontal(g36)
    c: Coincident(g37,g6)
    c: Coincident(g37,g19)
    c: Horizontal(g37)
    c: Coincident(g38,g7)
    c: Coincident(g38,g18)
    c: Horizontal(g38)
    c: Coincident(g39,g7)
    c: Coincident(g39,g18)
    c: Horizontal(g39)
    c: Coincident(g40,g8)
    c: Coincident(g40,g20)
    c: Horizontal(g40)
    c: Coincident(g41,g8)
    c: Coincident(g41,g20)
    c: Horizontal(g41)
    c: Coincident(g42,g9)
    c: Coincident(g42,g23)
    c: Horizontal(g42)
    c: Coincident(g43,g9)
    c: Coincident(g43,g23)
    c: Horizontal(g43)
    c: Coincident(g44,g10)
    c: Coincident(g44,g22)
    c: Horizontal(g44)
    c: Coincident(g45,g10)
    c: Coincident(g45,g22)
    c: Horizontal(g45)
    c: Coincident(g46,g11)
    c: Coincident(g46,g21)
    c: Horizontal(g46)
    c: Coincident(g47,g11)
    c: Coincident(g47,g21)
    c: Horizontal(g47)
FEATURE [Sketcher::SketchObject] Sketch031
  FullyConstrained = true
  Placement = pos=(117,19,0) rot=(0.57735,0.57735,0.57735;2.0944rad)
  sketch-geometry (24):
    g0: ArcOfCircle CenterX=-49.19 CenterY=67.75 CenterZ=0 NormalX=0 NormalY=0 NormalZ=1 AngleXU=0 Radius=1.5 StartAngle=1.5708 EndAngle=4.71239
    g1: ArcOfCircle CenterX=-49.19 CenterY=62 CenterZ=0 NormalX=0 NormalY=0 NormalZ=1 AngleXU=0 Radius=1.5 StartAngle=1.5708 EndAngle=4.71239
    g2: ArcOfCircle CenterX=-49.19 CenterY=56.25 CenterZ=0 NormalX=0 NormalY=0 NormalZ=1 AngleXU=0 Radius=1.5 StartAngle=1.5708 EndAngle=4.71239
    g3: ArcOfCircle CenterX=-49.19 CenterY=50.5 CenterZ=0 NormalX=0 NormalY=0 NormalZ=1 AngleXU=0 Radius=1.5 StartAngle=1.5708 EndAngle=4.71239
    g4: ArcOfCircle CenterX=-49.19 CenterY=44.75 CenterZ=0 NormalX=0 NormalY=0 NormalZ=1 AngleXU=0 Radius=1.5 StartAngle=1.5708 EndAngle=4.71239
    g5: ArcOfCircle CenterX=-49.19 CenterY=39 CenterZ=0 NormalX=0 NormalY=0 NormalZ=1 AngleXU=0 Radius=1.5 StartAngle=1.5708 EndAngle=4.71239
    g6: ArcOfCircle CenterX=-49.19 CenterY=33 CenterZ=0 NormalX=0 NormalY=0 NormalZ=1 AngleXU=0 Radius=1.5 StartAngle=1.5708 EndAngle=4.71239
    g7: ArcOfCircle CenterX=-49.19 CenterY=27.25 CenterZ=0 NormalX=0 NormalY=0 NormalZ=1 AngleXU=0 Radius=1.5 StartAngle=1.5708 EndAngle=4.71239
    g8: ArcOfCircle CenterX=-49.19 CenterY=21.5 CenterZ=0 NormalX=0 NormalY=0 NormalZ=1 AngleXU=0 Radius=1.5 StartAngle=1.5708 EndAngle=4.71239
    g9: ArcOfCircle CenterX=-49.19 CenterY=15.75 CenterZ=0 NormalX=0 NormalY=0 NormalZ=1 AngleXU=0 Radius=1.5 StartAngle=1.5708 EndAngle=4.71239
    g10: ArcOfCircle CenterX=-49.19 CenterY=10 CenterZ=0 NormalX=0 NormalY=0 NormalZ=1 AngleXU=0 Radius=1.5 StartAngle=1.5708 EndAngle=4.71239
    g11: ArcOfCircle CenterX=-49.19 CenterY=4.25 CenterZ=0 NormalX=0 NormalY=0 NormalZ=1 AngleXU=0 Radius=1.5 StartAngle=1.5708 EndAngle=4.71239
    g12: LineSegment StartX=-49.19 StartY=69.25 StartZ=0 EndX=-49.19 EndY=66.25 EndZ=0
    g13: LineSegment StartX=-49.19 StartY=63.5 StartZ=0 EndX=-49.19 EndY=60.5 EndZ=0
    g14: LineSegment StartX=-49.19 StartY=57.75 StartZ=0 EndX=-49.19 EndY=54.75 EndZ=0
    g15: LineSegment StartX=-49.19 StartY=52 StartZ=0 EndX=-49.19 EndY=49 EndZ=0
    g16: LineSegment StartX=-49.19 StartY=46.25 StartZ=0 EndX=-49.19 EndY=43.25 EndZ=0
    g17: LineSegment StartX=-49.19 StartY=40.5 StartZ=0 EndX=-49.19 EndY=37.5 EndZ=0
    g18: LineSegment StartX=-49.19 StartY=34.5 StartZ=0 EndX=-49.19 EndY=31.5 EndZ=0
    g19: LineSegment StartX=-49.19 StartY=28.75 StartZ=0 EndX=-49.19 EndY=25.75 EndZ=0
    g20: LineSegment StartX=-49.19 StartY=23 StartZ=0 EndX=-49.19 EndY=20 EndZ=0
    g21: LineSegment StartX=-49.19 StartY=17.25 StartZ=0 EndX=-49.19 EndY=14.25 EndZ=0
    g22: LineSegment StartX=-49.19 StartY=11.5 StartZ=0 EndX=-49.19 EndY=8.5 EndZ=0
    g23: LineSegment StartX=-49.19 StartY=5.75 StartZ=0 EndX=-49.19 EndY=2.75 EndZ=0
  constraints (48):
    c: Block(g0)
    c: Block(g1)
    c: Block(g2)
    c: Block(g3)
    c: Block(g4)
    c: Block(g5)
    c: Block(g6)
    c: Block(g7)
    c: Block(g8)
    c: Block(g9)
    c: Block(g10)
    c: Block(g11)
    c: Coincident(g12,g0)
    c: Coincident(g12,g0)
    c: Vertical(g12)
    c: Vertical(g13)
    c: Coincident(g13,g1)
    c: Vertical(g14)
    c: Coincident(g14,g2)
    c: Vertical(g15)
    c: Coincident(g15,g3)
    c: Vertical(g16)
    c: Coincident(g16,g4)
    c: Vertical(g17)
    c: Coincident(g17,g5)
    c: Vertical(g18)
    c: Coincident(g18,g6)
    c: Vertical(g19)
    c: Coincident(g19,g7)
    c: Vertical(g20)
    c: Coincident(g20,g8)
    c: Vertical(g21)
    c: Coincident(g21,g9)
    c: Vertical(g22)
    c: Coincident(g22,g10)
    c: Vertical(g23)
    c: Coincident(g23,g11)
    c: Block(g23)
    c: Block(g22)
    c: Block(g21)
    c: Block(g20)
    c: Block(g13)
    c: Block(g14)
    c: Block(g15)
    c: Block(g16)
    c: Block(g17)
    c: Block(g18)
    c: Block(g19)
FEATURE [Part::Extrusion] Extrude022
  Base = -> Sketch030
  Dir = (1,-2e-16,2e-16)
  DirMode = 2
  FaceMakerClass = Part::FaceMakerBullseye
  LengthFwd = 19
  LengthRev = 0
  Placement = pos=(-19,0,0) rot=(0,0,1;0rad)
  Solid = true
  Symmetric = false
FEATURE [Part::Fillet] Fillet022
  Base = -> Extrude022
  Edges = 24 edges r=1.49: [Edge6,Edge11,Edge18,Edge23,Edge30,Edge35,Edge42,Edge47,Edge54,Edge59,Edge66,Edge71,Edge78,Edge83,Edge90,Edge95,Edge102,Edge107,Edge114,Edge119,Edge126,Edge131,Edge138,Edge143]
FEATURE [Part::Cut] Cut020  label="top010"
  Base = -> Cut019
  Tool = -> Fillet022
FEATURE [Sketcher::SketchObject] Sketch032
  FullyConstrained = true
  Placement = pos=(117,19,0) rot=(0.57735,0.57735,0.57735;2.0944rad)
  sketch-geometry (48):
    g0: LineSegment StartX=-49.19 StartY=69.25 StartZ=0 EndX=-49.19 EndY=66.25 EndZ=0
    g1: LineSegment StartX=-49.19 StartY=63.5 StartZ=0 EndX=-49.19 EndY=60.5 EndZ=0
    g2: LineSegment StartX=-49.19 StartY=57.75 StartZ=0 EndX=-49.19 EndY=54.75 EndZ=0
    g3: LineSegment StartX=-49.19 StartY=52 StartZ=0 EndX=-49.19 EndY=49 EndZ=0
    g4: LineSegment StartX=-49.19 StartY=46.25 StartZ=0 EndX=-49.19 EndY=43.25 EndZ=0
    g5: LineSegment StartX=-49.19 StartY=40.5 StartZ=0 EndX=-49.19 EndY=37.5 EndZ=0
    g6: LineSegment StartX=-49.19 StartY=34.5 StartZ=0 EndX=-49.19 EndY=31.5 EndZ=0
    g7: LineSegment StartX=-49.19 StartY=28.75 StartZ=0 EndX=-49.19 EndY=25.75 EndZ=0
    g8: LineSegment StartX=-49.19 StartY=23 StartZ=0 EndX=-49.19 EndY=20 EndZ=0
    g9: LineSegment StartX=-49.19 StartY=17.25 StartZ=0 EndX=-49.19 EndY=14.25 EndZ=0
    g10: LineSegment StartX=-49.19 StartY=11.5 StartZ=0 EndX=-49.19 EndY=8.5 EndZ=0
    g11: LineSegment StartX=-49.19 StartY=5.75 StartZ=0 EndX=-49.19 EndY=2.75 EndZ=0
    g12: ArcOfCircle CenterX=-1.5 CenterY=67.75 CenterZ=0 NormalX=0 NormalY=0 NormalZ=1 AngleXU=0 Radius=1.5 StartAngle=4.71239 EndAngle=7.85398
    g13: ArcOfCircle CenterX=-1.5 CenterY=62 CenterZ=0 NormalX=0 NormalY=0 NormalZ=1 AngleXU=0 Radius=1.5 StartAngle=4.71239 EndAngle=7.85398
    g14: ArcOfCircle CenterX=-1.5 CenterY=56.25 CenterZ=0 NormalX=0 NormalY=0 NormalZ=1 AngleXU=0 Radius=1.5 StartAngle=4.71239 EndAngle=7.85398
    g15: ArcOfCircle CenterX=-11.49 CenterY=50.5 CenterZ=0 NormalX=0 NormalY=0 NormalZ=1 AngleXU=0 Radius=1.5 StartAngle=4.71239 EndAngle=7.85398
    g16: ArcOfCircle CenterX=-16.28 CenterY=44.75 CenterZ=0 NormalX=0 NormalY=0 NormalZ=1 AngleXU=0 Radius=1.5 StartAngle=4.71239 EndAngle=7.85398
    g17: ArcOfCircle CenterX=-18.2337 CenterY=39 CenterZ=0 NormalX=0 NormalY=0 NormalZ=1 AngleXU=0 Radius=1.5 StartAngle=4.71485 EndAngle=7.85398
    g18: ArcOfCircle CenterX=-16.2837 CenterY=27.25 CenterZ=0 NormalX=0 NormalY=0 NormalZ=1 AngleXU=0 Radius=1.5 StartAngle=4.71485 EndAngle=7.85398
    g19: ArcOfCircle CenterX=-18.2337 CenterY=33 CenterZ=0 NormalX=0 NormalY=0 NormalZ=1 AngleXU=0 Radius=1.5 StartAngle=4.71485 EndAngle=7.85398
    g20: ArcOfCircle CenterX=-11.49 CenterY=21.5 CenterZ=0 NormalX=0 NormalY=0 NormalZ=1 AngleXU=0 Radius=1.5 StartAngle=4.71239 EndAngle=7.85398
    g21: ArcOfCircle CenterX=-1.5 CenterY=4.25 CenterZ=0 NormalX=0 NormalY=0 NormalZ=1 AngleXU=0 Radius=1.5 StartAngle=4.71239 EndAngle=7.85398
    g22: ArcOfCircle CenterX=-1.5 CenterY=10 CenterZ=0 NormalX=0 NormalY=0 NormalZ=1 AngleXU=0 Radius=1.5 StartAngle=4.71239 EndAngle=7.85398
    g23: ArcOfCircle CenterX=-1.5 CenterY=15.75 CenterZ=0 NormalX=0 NormalY=0 NormalZ=1 AngleXU=0 Radius=1.5 StartAngle=4.71239 EndAngle=7.85398
    g24: LineSegment StartX=-49.19 StartY=69.25 StartZ=0 EndX=-1.5 EndY=69.25 EndZ=0
    g25: LineSegment StartX=-49.19 StartY=66.25 StartZ=0 EndX=-1.5 EndY=66.25 EndZ=0
    g26: LineSegment StartX=-49.19 StartY=63.5 StartZ=0 EndX=-1.5 EndY=63.5 EndZ=0
    g27: LineSegment StartX=-49.19 StartY=60.5 StartZ=0 EndX=-1.5 EndY=60.5 EndZ=0
    g28: LineSegment StartX=-49.19 StartY=57.75 StartZ=0 EndX=-1.5 EndY=57.75 EndZ=0
    g29: LineSegment StartX=-49.19 StartY=54.75 StartZ=0 EndX=-1.5 EndY=54.75 EndZ=0
    g30: LineSegment StartX=-49.19 StartY=52 StartZ=0 EndX=-11.49 EndY=52 EndZ=0
    g31: LineSegment StartX=-49.19 StartY=49 StartZ=0 EndX=-11.49 EndY=49 EndZ=0
    g32: LineSegment StartX=-49.19 StartY=46.25 StartZ=0 EndX=-16.28 EndY=46.25 EndZ=0
    g33: LineSegment StartX=-49.19 StartY=43.25 StartZ=0 EndX=-16.28 EndY=43.25 EndZ=0
    g34: LineSegment StartX=-49.19 StartY=40.5 StartZ=0 EndX=-18.2337 EndY=40.5 EndZ=0
    g35: LineSegment StartX=-49.19 StartY=37.5 StartZ=0 EndX=-18.23 EndY=37.5 EndZ=0
    g36: LineSegment StartX=-49.19 StartY=34.5 StartZ=0 EndX=-18.2337 EndY=34.5 EndZ=0
    g37: LineSegment StartX=-49.19 StartY=31.5 StartZ=0 EndX=-18.23 EndY=31.5 EndZ=0
    g38: LineSegment StartX=-49.19 StartY=28.75 StartZ=0 EndX=-16.2837 EndY=28.75 EndZ=0
    g39: LineSegment StartX=-49.19 StartY=25.75 StartZ=0 EndX=-16.28 EndY=25.75 EndZ=0
    g40: LineSegment StartX=-49.19 StartY=23 StartZ=0 EndX=-11.49 EndY=23 EndZ=0
    g41: LineSegment StartX=-49.19 StartY=20 StartZ=0 EndX=-11.49 EndY=20 EndZ=0
    g42: LineSegment StartX=-49.19 StartY=17.25 StartZ=0 EndX=-1.5 EndY=17.25 EndZ=0
    g43: LineSegment StartX=-49.19 StartY=14.25 StartZ=0 EndX=-1.5 EndY=14.25 EndZ=0
    g44: LineSegment StartX=-49.19 StartY=11.5 StartZ=0 EndX=-1.5 EndY=11.5 EndZ=0
    g45: LineSegment StartX=-49.19 StartY=8.5 StartZ=0 EndX=-1.5 EndY=8.5 EndZ=0
    g46: LineSegment StartX=-49.19 StartY=5.75 StartZ=0 EndX=-1.5 EndY=5.75 EndZ=0
    g47: LineSegment StartX=-49.19 StartY=2.75 StartZ=0 EndX=-1.5 EndY=2.75 EndZ=0
  constraints (120):
    c: Vertical(g0)
    c: Distance(g0) = 3
    c: Block(g0)
    c: Vertical(g1)
    c: Distance(g1) = 3
    c: Vertical(g2)
    c: Equal(g0,g2) = 3
    c: Block(g2)
    c: Vertical(g3)
    c: Equal(g1,g3) = 3
    c: Vertical(g4)
    c: Equal(g0,g4) = 3
    c: Block(g4)
    c: Vertical(g5)
    c: Equal(g1,g5) = 3
    c: Vertical(g6)
    c: Equal(g0,g6) = 3
    c: Block(g6)
    c: Vertical(g7)
    c: Equal(g1,g7) = 3
    c: Vertical(g8)
    c: Equal(g0,g8) = 3
    c: Block(g8)
    c: Vertical(g9)
    c: Equal(g1,g9) = 3
    c: Vertical(g10)
    c: Equal(g0,g10) = 3
    c: Block(g10)
    c: Vertical(g11)
    c: Equal(g1,g11) = 3
    c: Block(g12)
    c: Block(g13)
    c: Block(g14)
    c: Block(g15)
    c: Block(g16)
    c: Block(g17)
    c: Block(g18)
    c: Block(g19)
    c: Block(g20)
    c: Block(g21)
    c: Block(g22)
    c: Block(g23)
    c: Block(g11)
    c: Block(g9)
    c: Block(g7)
    c: Block(g5)
    c: Block(g3)
    c: Block(g1)
    c: Coincident(g24,g0)
    c: Coincident(g24,g12)
    c: Horizontal(g24)
    c: Coincident(g25,g0)
    c: Coincident(g25,g12)
    c: Horizontal(g25)
    c: Coincident(g26,g1)
    c: Coincident(g26,g13)
    c: Horizontal(g26)
    c: Coincident(g27,g1)
    c: Coincident(g27,g13)
    c: Horizontal(g27)
    c: Coincident(g28,g2)
    c: Coincident(g28,g14)
    c: Horizontal(g28)
    c: Coincident(g29,g2)
    c: Coincident(g29,g14)
    c: Horizontal(g29)
    c: Coincident(g30,g3)
    c: Coincident(g30,g15)
    c: Horizontal(g30)
    c: Coincident(g31,g3)
    c: Coincident(g31,g15)
    c: Horizontal(g31)
    c: Coincident(g32,g4)
    c: Coincident(g32,g16)
    c: Horizontal(g32)
    c: Coincident(g33,g4)
    c: Coincident(g33,g16)
    c: Horizontal(g33)
    c: Coincident(g34,g5)
    c: Coincident(g34,g17)
    c: Horizontal(g34)
    c: Coincident(g35,g5)
    c: Coincident(g35,g17)
    c: Horizontal(g35)
    c: Coincident(g36,g6)
    c: Coincident(g36,g19)
    c: Horizontal(g36)
    c: Coincident(g37,g6)
    c: Coincident(g37,g19)
    c: Horizontal(g37)
    c: Coincident(g38,g7)
    c: Coincident(g38,g18)
    c: Horizontal(g38)
    c: Coincident(g39,g7)
    c: Coincident(g39,g18)
    c: Horizontal(g39)
    c: Coincident(g40,g8)
    c: Coincident(g40,g20)
    c: Horizontal(g40)
    c: Coincident(g41,g8)
    c: Coincident(g41,g20)
    c: Horizontal(g41)
    c: Coincident(g42,g9)
    c: Coincident(g42,g23)
    c: Horizontal(g42)
    c: Coincident(g43,g9)
    c: Coincident(g43,g23)
    c: Horizontal(g43)
    c: Coincident(g44,g10)
    c: Coincident(g44,g22)
    c: Horizontal(g44)
    c: Coincident(g45,g10)
    c: Coincident(g45,g22)
    c: Horizontal(g45)
    c: Coincident(g46,g11)
    c: Coincident(g46,g21)
    c: Horizontal(g46)
    c: Coincident(g47,g11)
    c: Coincident(g47,g21)
    c: Horizontal(g47)
FEATURE [Part::Extrusion] Extrude023
  Base = -> Sketch032
  Dir = (1,-2e-16,2e-16)
  DirMode = 2
  FaceMakerClass = Part::FaceMakerBullseye
  LengthFwd = 19
  LengthRev = 0
  Placement = pos=(-19,0,0) rot=(0,0,1;0rad)
  Solid = true
  Symmetric = false
FEATURE [Part::Fillet] Fillet023
  Base = -> Extrude023
  Edges = <same value as first occurrence — deduplicated (x6 in doc)>
  Placement = pos=(0,0.05,0) rot=(0,0,1;0rad)
FEATURE [Part::Cut] Cut014  label="bottom003"
  Base = -> Cut007
  Tool = -> Fusion047
FEATURE [Part::Cut] Cut021  label="bottom004"
  Base = -> Cut014
  Tool = -> Fillet023
FEATURE [Sketcher::SketchObject] Sketch033
  FullyConstrained = true
  Placement = pos=(117,19,0) rot=(0.57735,0.57735,0.57735;2.0944rad)
  sketch-geometry (8):
    g0: LineSegment StartX=-49.19 StartY=69.25 StartZ=0 EndX=-49.19 EndY=66.25 EndZ=0
    g1: LineSegment StartX=-49.19 StartY=5.75 StartZ=0 EndX=-49.19 EndY=2.75 EndZ=0
    g2: ArcOfCircle CenterX=-1.5 CenterY=67.75 CenterZ=0 NormalX=0 NormalY=0 NormalZ=1 AngleXU=0 Radius=1.5 StartAngle=4.71239 EndAngle=7.85398
    g3: ArcOfCircle CenterX=-1.5 CenterY=4.25 CenterZ=0 NormalX=0 NormalY=0 NormalZ=1 AngleXU=0 Radius=1.5 StartAngle=4.71239 EndAngle=7.85398
    g4: LineSegment StartX=-49.19 StartY=69.25 StartZ=0 EndX=-1.5 EndY=69.25 EndZ=0
    g5: LineSegment StartX=-49.19 StartY=66.25 StartZ=0 EndX=-1.5 EndY=66.25 EndZ=0
    g6: LineSegment StartX=-49.19 StartY=5.75 StartZ=0 EndX=-1.5 EndY=5.75 EndZ=0
    g7: LineSegment StartX=-49.19 StartY=2.75 StartZ=0 EndX=-1.5 EndY=2.75 EndZ=0
  constraints (19):
    c: Vertical(g0)
    c: Distance(g0) = 3
    c: Block(g0)
    c: Vertical(g1)
    c: Block(g2)
    c: Block(g3)
    c: Block(g1)
    c: Coincident(g4,g0)
    c: Coincident(g4,g2)
    c: Horizontal(g4)
    c: Coincident(g5,g0)
    c: Coincident(g5,g2)
    c: Horizontal(g5)
    c: Coincident(g6,g1)
    c: Coincident(g6,g3)
    c: Horizontal(g6)
    c: Coincident(g7,g1)
    c: Coincident(g7,g3)
    c: Horizontal(g7)
FEATURE [Sketcher::SketchObject] Sketch034
  FullyConstrained = true
  Placement = pos=(117,19,0) rot=(0.57735,0.57735,0.57735;2.0944rad)
  sketch-geometry (8):
    g0: LineSegment StartX=-49.19 StartY=63.5 StartZ=0 EndX=-49.19 EndY=60.5 EndZ=0
    g1: LineSegment StartX=-49.19 StartY=11.5 StartZ=0 EndX=-49.19 EndY=8.5 EndZ=0
    g2: ArcOfCircle CenterX=-1.5 CenterY=62 CenterZ=0 NormalX=0 NormalY=0 NormalZ=1 AngleXU=0 Radius=1.5 StartAngle=4.71239 EndAngle=7.85398
    g3: ArcOfCircle CenterX=-1.5 CenterY=10 CenterZ=0 NormalX=0 NormalY=0 NormalZ=1 AngleXU=0 Radius=1.5 StartAngle=4.71239 EndAngle=7.85398
    g4: LineSegment StartX=-49.19 StartY=63.5 StartZ=0 EndX=-1.5 EndY=63.5 EndZ=0
    g5: LineSegment StartX=-49.19 StartY=60.5 StartZ=0 EndX=-1.5 EndY=60.5 EndZ=0
    g6: LineSegment StartX=-49.19 StartY=11.5 StartZ=0 EndX=-1.5 EndY=11.5 EndZ=0
    g7: LineSegment StartX=-49.19 StartY=8.5 StartZ=0 EndX=-1.5 EndY=8.5 EndZ=0
  constraints (19):
    c: Vertical(g0)
    c: Distance(g0) = 3
    c: Vertical(g1)
    c: Block(g1)
    c: Block(g2)
    c: Block(g3)
    c: Block(g0)
    c: Coincident(g4,g0)
    c: Coincident(g4,g2)
    c: Horizontal(g4)
    c: Coincident(g5,g0)
    c: Coincident(g5,g2)
    c: Horizontal(g5)
    c: Coincident(g6,g1)
    c: Coincident(g6,g3)
    c: Horizontal(g6)
    c: Coincident(g7,g1)
    c: Coincident(g7,g3)
    c: Horizontal(g7)
FEATURE [Part::Extrusion] Extrude024
  Base = -> Sketch033
  Dir = (1,0,0)
  DirMode = 2
  FaceMakerClass = Part::FaceMakerBullseye
  LengthFwd = 10
  LengthRev = 0
  Solid = true
  Symmetric = false
FEATURE [Part::Extrusion] Extrude025
  Base = -> Sketch034
  Dir = (1,0,0)
  DirMode = 2
  FaceMakerClass = Part::FaceMakerBullseye
  LengthFwd = 10
  LengthRev = 0
  Solid = true
  Symmetric = false
FEATURE [Part::Fillet] Fillet024  label="removeFromtMoreFrontCaseScrewRetainers"
  Base = -> Extrude024
  Edges = 4 edges r=1.49: [Edge6,Edge11,Edge18,Edge23]
  Placement = pos=(-11,0,0) rot=(0,0,1;0rad)
FEATURE [Part::Fillet] Fillet025  label="removeFromtMoreFrontCaseScrewRetainers001"
  Base = -> Extrude025
  Edges = 4 edges r=1.49: [Edge6,Edge11,Edge18,Edge23]
  Placement = pos=(-19,0,0) rot=(0,0,1;0rad)
FEATURE [Part::Cut] Cut022
  Base = -> Cut015
  Tool = -> Fillet025
FEATURE [Part::Cut] Cut023  label="screwRetainers"
  Base = -> Cut022
  Tool = -> Fillet024
FEATURE [Part::MultiFuse] Fusion056  label="bottom005"
  Shapes = -> [Fusion044,Cut021]
FEATURE [Part::MultiFuse] Fusion057  label="casePillars001"
  Shapes = -> [Cut016,Fusion052]
FEATURE [Part::MultiFuse] Fusion058  label="bottom006"
  Shapes = -> [Fusion056,Cut023]
FEATURE [Part::MultiFuse] Fusion059  label="bottom007"
  Shapes = -> [Fusion058,Fillet005]
FEATURE [Part::MultiFuse] Fusion060  label="bottom008"
  Shapes = -> [Fusion059,Fusion]
FEATURE [Part::MultiFuse] Fusion061  label="top011"
  Shapes = -> [Cut006,Cut020]
FEATURE [Part::MultiFuse] Fusion062  label="top012"
  Shapes = -> [Fusion057,Fusion061]
FEATURE [Sketcher::SketchObject] Sketch035  label="topSketch007"
  FullyConstrained = true
  sketch-geometry (6):
    g0: LineSegment StartX=19 StartY=38 StartZ=0 EndX=117 EndY=38 EndZ=0
    g1: ArcOfCircle CenterX=19 CenterY=19 CenterZ=0 NormalX=0 NormalY=0 NormalZ=1 AngleXU=0 Radius=19 StartAngle=1.5708 EndAngle=3.14159
    g2: LineSegment StartX=117 StartY=38 StartZ=0 EndX=117 EndY=19 EndZ=0
    g3: LineSegment StartX=98 StartY=1.0161e-12 StartZ=0 EndX=5.22862e-06 EndY=1.0161e-12 EndZ=0
    g4: LineSegment StartX=5.22862e-06 StartY=19 StartZ=0 EndX=5.22862e-06 EndY=1.0161e-12 EndZ=0
    g5: ArcOfCircle CenterX=98 CenterY=19 CenterZ=0 NormalX=0 NormalY=0 NormalZ=1 AngleXU=0 Radius=19 StartAngle=4.71239 EndAngle=6.28319
  constraints (16):
    c: Horizontal(g0)
    c: Distance(g0) = 98
    c: Coincident(g1,g0)
    c: Block(g1)
    c: Coincident(g2,g0)
    c: Vertical(g2)
    c: Distance(g2) = 19
    c: Horizontal(g3)
    c: Coincident(g4,g1)
    c: Vertical(g4)
    c: Coincident(g3,g4)
    c: Block(g3)
    c: Coincident(g5,g2)
    c: Coincident(g5,g3)
    c: Block(g0)
    c: Block(g5)
FEATURE [Part::Extrusion] Extrude026  label="sideA001"
  Base = -> Sketch035
  Dir = (0,0,1)
  DirMode = 2
  FaceMakerClass = Part::FaceMakerBullseye
  LengthFwd = 3
  LengthRev = 0
  Placement = pos=(0,0,-2.7) rot=(0,0,1;0rad)
  Solid = true
  Symmetric = false
FEATURE [Sketcher::SketchObject] Sketch036  label="topSketch008"
  FullyConstrained = true
  sketch-geometry (6):
    g0: LineSegment StartX=19 StartY=38 StartZ=0 EndX=117 EndY=38 EndZ=0
    g1: ArcOfCircle CenterX=19 CenterY=19 CenterZ=0 NormalX=0 NormalY=0 NormalZ=1 AngleXU=0 Radius=19 StartAngle=1.5708 EndAngle=3.14159
    g2: LineSegment StartX=117 StartY=38 StartZ=0 EndX=117 EndY=19 EndZ=0
    g3: LineSegment StartX=98 StartY=1.0161e-12 StartZ=0 EndX=5.22862e-06 EndY=1.0161e-12 EndZ=0
    g4: LineSegment StartX=5.22862e-06 StartY=19 StartZ=0 EndX=5.22862e-06 EndY=1.0161e-12 EndZ=0
    g5: ArcOfCircle CenterX=98 CenterY=19 CenterZ=0 NormalX=0 NormalY=0 NormalZ=1 AngleXU=0 Radius=19 StartAngle=4.71239 EndAngle=6.28319
  constraints (16):
    c: Horizontal(g0)
    c: Distance(g0) = 98
    c: Coincident(g1,g0)
    c: Block(g1)
    c: Coincident(g2,g0)
    c: Vertical(g2)
    c: Distance(g2) = 19
    c: Horizontal(g3)
    c: Coincident(g4,g1)
    c: Vertical(g4)
    c: Coincident(g3,g4)
    c: Block(g3)
    c: Coincident(g5,g2)
    c: Coincident(g5,g3)
    c: Block(g0)
    c: Block(g5)
FEATURE [Part::Extrusion] Extrude027  label="sideB001"
  Base = -> Sketch036
  Dir = (0,0,1)
  DirMode = 2
  FaceMakerClass = Part::FaceMakerBullseye
  LengthFwd = 3
  LengthRev = 0
  Placement = pos=(0,0,71.7) rot=(0,0,1;0rad)
  Solid = true
  Symmetric = false
FEATURE [Part::MultiFuse] Fusion064  label="removeFromBottom"
  Shapes = -> [Extrude026,Extrude027]
FEATURE [Part::Cut] Cut024  label="bottom009"
  Base = -> Fusion060
  Tool = -> Fusion064
FEATURE [Sketcher::SketchObject] Sketch037  label="topSketch009"
  FullyConstrained = true
  sketch-geometry (6):
    g0: ArcOfCircle CenterX=19 CenterY=19 CenterZ=0 NormalX=0 NormalY=0 NormalZ=1 AngleXU=0 Radius=19 StartAngle=1.5708 EndAngle=3.14159
    g1: LineSegment StartX=5.22862e-06 StartY=19 StartZ=0 EndX=5.22862e-06 EndY=1.19904e-11 EndZ=0
    g2: LineSegment StartX=19 StartY=38 StartZ=0 EndX=124 EndY=38 EndZ=0
    g3: LineSegment StartX=5.22862e-06 StartY=1.19904e-11 StartZ=0 EndX=105 EndY=1.19904e-11 EndZ=0
    g4: ArcOfCircle CenterX=105 CenterY=19 CenterZ=0 NormalX=0 NormalY=0 NormalZ=1 AngleXU=0 Radius=19 StartAngle=4.71239 EndAngle=6.28319
    g5: LineSegment StartX=124 StartY=38 StartZ=0 EndX=124 EndY=19 EndZ=0
  constraints (16):
    c: Block(g0)
    c: Coincident(g1,g0)
    c: Vertical(g1)
    c: Horizontal(g2)
    c: Distance(g2) = 105
    c: Coincident(g2,g0)
    c: Distance(g1) = 19
    c: Coincident(g3,g1)
    c: Horizontal(g3)
    c: Distance(g3) = 105
    c: Block(g4)
    c: Coincident(g4,g3)
    c: Coincident(g5,g2)
    c: Coincident(g5,g4)
    c: Vertical(g5)
    c: Distance(g5) = 19
FEATURE [Part::Extrusion] Extrude028  label="sideB"
  Base = -> Sketch037
  Dir = (0,0,1)
  DirMode = 2
  FaceMakerClass = Part::FaceMakerBullseye
  LengthFwd = 3
  LengthRev = 0
  Placement = pos=(0,0,72) rot=(0,0,1;0rad)
  Solid = true
  Symmetric = false
FEATURE [Sketcher::SketchObject] Sketch038  label="topSketch010"
  FullyConstrained = true
  sketch-geometry (22):
    g0: LineSegment StartX=5.21097e-06 StartY=3 StartZ=0 EndX=5.21097e-06 EndY=19 EndZ=0
    g1: ArcOfCircle CenterX=19 CenterY=19 CenterZ=0 NormalX=0 NormalY=0 NormalZ=1 AngleXU=0 Radius=19 StartAngle=1.5708 EndAngle=3.14159
    g2: ArcOfCircle CenterX=19 CenterY=19 CenterZ=0 NormalX=0 NormalY=0 NormalZ=1 AngleXU=0 Radius=16 StartAngle=1.5708 EndAngle=3.14159
    g3: LineSegment StartX=114 StartY=35 StartZ=0 EndX=19 EndY=35 EndZ=0
    g4: LineSegment StartX=5.21097e-06 StartY=3 StartZ=0 EndX=5.21097e-06 EndY=0 EndZ=0
    g5: LineSegment StartX=3 StartY=0 StartZ=0 EndX=5.21097e-06 EndY=0 EndZ=0
    g6: LineSegment StartX=3 StartY=19 StartZ=0 EndX=3 EndY=0 EndZ=0
    g7: LineSegment StartX=19 StartY=38 StartZ=0 EndX=124 EndY=38 EndZ=0
    g8: Circle CenterX=119 CenterY=35 CenterZ=0 NormalX=0 NormalY=0 NormalZ=1 AngleXU=0 Radius=1
    g9: Circle CenterX=121 CenterY=35 CenterZ=0 NormalX=0 NormalY=0 NormalZ=1 AngleXU=0 Radius=1
    g10: Circle CenterX=121 CenterY=33 CenterZ=0 NormalX=0 NormalY=0 NormalZ=1 AngleXU=0 Radius=1
    g11: BSplineCurve PolesCount=3 KnotsCount=2 Degree=2 IsPeriodic=0
    g12: GeomPoint X=119 Y=35 Z=0
    g13: GeomPoint X=121 Y=33 Z=0
    g14: LineSegment StartX=119 StartY=35 StartZ=0 EndX=114 EndY=35 EndZ=0
    g15: ArcOfCircle CenterX=105 CenterY=19 CenterZ=0 NormalX=0 NormalY=0 NormalZ=1 AngleXU=0 Radius=16 StartAngle=5.60905 EndAngle=6.28319
    g16: LineSegment StartX=121 StartY=33 StartZ=0 EndX=121 EndY=19 EndZ=0
    g17: LineSegment StartX=117.5 StartY=9.01251 StartZ=0 EndX=121.163 EndY=9.0125 EndZ=0
    g18: ArcOfCircle CenterX=105 CenterY=19 CenterZ=0 NormalX=0 NormalY=0 NormalZ=1 AngleXU=0 Radius=20.6155 StartAngle=5.7297 EndAngle=6.28319
    g19: LineSegment StartX=121.163 StartY=9.0125 StartZ=0 EndX=122.538 EndY=8.16329 EndZ=0
    g20: LineSegment StartX=124 StartY=38 StartZ=0 EndX=125.616 EndY=38 EndZ=0
    g21: LineSegment StartX=125.616 StartY=19 StartZ=0 EndX=125.616 EndY=38 EndZ=0
  constraints (49):
    c: Vertical(g0)
    c: Block(g0)
    c: Coincident(g1,g0)
    c: Block(g1)
    c: Coincident(g2,g1)
    c: Block(g2)
    c: Coincident(g3,g2)
    c: Horizontal(g3)
    c: Tangent(g3,g2)
    c: Coincident(g4,g0)
    c: Distance(g4) = 3
    c: Vertical(g4)
    c: Coincident(g5,g4)
    c: Horizontal(g5)
    c: Coincident(g6,g2)
    c: Coincident(g6,g5)
    c: Vertical(g6)
    c: Horizontal(g7)
    c: Distance(g7) = 105
    c: Coincident(g7,g1)
    c: Block(g3)
    c: Weight(g8) = 1
    c: Equal(g8,g9)
    c: Equal(g8,g10)
    c: InternalAlignment(g8,g11)
    c: InternalAlignment(g9,g11)
    c: InternalAlignment(g10,g11)
    c: InternalAlignment(g12,g11)
    c: InternalAlignment(g13,g11)
    c: Block(g11)
    c: Coincident(g14,g11)
    c: Coincident(g14,g3)
    c: Horizontal(g14)
    c: Block(g15)
    c: Coincident(g16,g11)
    c: Coincident(g16,g15)
    c: Vertical(g16)
    c: Distance(g16) = 14
    c: Coincident(g17,g15)
    c: Block(g18)
    c: Coincident(g19,g18)
    c: Coincident(g20,g7)
    c: Horizontal(g20)
    c: Vertical(g21)
    c: Coincident(g20,g21)
    c: Block(g20)
    c: Block(g21)
    c: Block(g19)
    c: Block(g17)
FEATURE [Part::Extrusion] Extrude029
  Base = -> Sketch038
  Dir = (0,0,1)
  DirMode = 2
  FaceMakerClass = Part::FaceMakerBullseye
  LengthFwd = 72
  LengthRev = 0
  Solid = true
  Symmetric = false
FEATURE [Part::Feature] Face085
  shape: bbox 4.8 x 25.5 x 2e-07 mm, 1 faces, 0 solids (baked)
FEATURE [Part::Revolution] Revolve089  label="moreFrontCaseScrewPost003"
  Angle = 360
  Axis = (0,1,0)
  Base = (0,0,0)
  FaceMakerClass = Part::FaceMakerBullseye
  Placement = pos=(109.5,4.5,3.5) rot=(0,0,1;0rad)
  Solid = false
  Source = -> Face085
  Symmetric = false
FEATURE [Part::Feature] Face086
  shape: bbox 4.8 x 25.5 x 2e-07 mm, 1 faces, 0 solids (baked)
FEATURE [Part::Revolution] Revolve090  label="moreFrontCaseScrewPost004"
  Angle = 360
  Axis = (0,1,0)
  Base = (0,0,0)
  FaceMakerClass = Part::FaceMakerBullseye
  Placement = pos=(109.5,4.5,68.5) rot=(0,0,1;0rad)
  Solid = false
  Source = -> Face086
  Symmetric = false
FEATURE [Part::Fillet] Fillet026  label="top013"
  Base = -> Extrude029
  Edges = 1 edges r=2: [Edge35]
FEATURE [Sketcher::SketchObject] Sketch039
  FullyConstrained = true
  sketch-geometry (7):
    g0: LineSegment StartX=0 StartY=0 StartZ=0 EndX=0 EndY=6 EndZ=0
    g1: Circle CenterX=0 CenterY=0 CenterZ=0 NormalX=0 NormalY=0 NormalZ=1 AngleXU=0 Radius=1
    g2: Circle CenterX=8 CenterY=6 CenterZ=0 NormalX=0 NormalY=0 NormalZ=1 AngleXU=0 Radius=1
    g3: BSplineCurve PolesCount=3 KnotsCount=2 Degree=2 IsPeriodic=0
    g4: GeomPoint X=0 Y=0 Z=0
    g5: GeomPoint X=8 Y=6 Z=0
    g6: LineSegment StartX=0 StartY=6 StartZ=0 EndX=8 EndY=6 EndZ=0
  constraints (14):
    c: Coincident(g0,g-1)
    c: Distance(g0) = 6
    c: Vertical(g0)
    c: Coincident(g3,g0)
    c: Weight(g1) = 1
    c: Equal(g1,g2)
    c: InternalAlignment(g1,g3)
    c: InternalAlignment(g2,g3)
    c: InternalAlignment(g4,g3)
    c: InternalAlignment(g5,g3)
    c: Block(g3)
    c: Coincident(g6,g0)
    c: Coincident(g6,g3)
    c: Horizontal(g6)
FEATURE [Sketcher::SketchObject] Sketch040
  FullyConstrained = true
  sketch-geometry (7):
    g0: LineSegment StartX=0 StartY=0 StartZ=0 EndX=0 EndY=6 EndZ=0
    g1: Circle CenterX=0 CenterY=0 CenterZ=0 NormalX=0 NormalY=0 NormalZ=1 AngleXU=0 Radius=1
    g2: Circle CenterX=8 CenterY=6 CenterZ=0 NormalX=0 NormalY=0 NormalZ=1 AngleXU=0 Radius=1
    g3: BSplineCurve PolesCount=3 KnotsCount=2 Degree=2 IsPeriodic=0
    g4: GeomPoint X=0 Y=0 Z=0
    g5: GeomPoint X=8 Y=6 Z=0
    g6: LineSegment StartX=0 StartY=6 StartZ=0 EndX=8 EndY=6 EndZ=0
  constraints (14):
    c: Coincident(g0,g-1)
    c: Distance(g0) = 6
    c: Vertical(g0)
    c: Coincident(g3,g0)
    c: Weight(g1) = 1
    c: Equal(g1,g2)
    c: InternalAlignment(g1,g3)
    c: InternalAlignment(g2,g3)
    c: InternalAlignment(g4,g3)
    c: InternalAlignment(g5,g3)
    c: Block(g3)
    c: Coincident(g6,g0)
    c: Coincident(g6,g3)
    c: Horizontal(g6)
FEATURE [Sketcher::SketchObject] Sketch041
  FullyConstrained = true
  sketch-geometry (7):
    g0: LineSegment StartX=0 StartY=0 StartZ=0 EndX=0 EndY=6 EndZ=0
    g1: Circle CenterX=0 CenterY=0 CenterZ=0 NormalX=0 NormalY=0 NormalZ=1 AngleXU=0 Radius=1
    g2: Circle CenterX=8 CenterY=6 CenterZ=0 NormalX=0 NormalY=0 NormalZ=1 AngleXU=0 Radius=1
    g3: BSplineCurve PolesCount=3 KnotsCount=2 Degree=2 IsPeriodic=0
    g4: GeomPoint X=0 Y=0 Z=0
    g5: GeomPoint X=8 Y=6 Z=0
    g6: LineSegment StartX=0 StartY=6 StartZ=0 EndX=8 EndY=6 EndZ=0
  constraints (14):
    c: Coincident(g0,g-1)
    c: Distance(g0) = 6
    c: Vertical(g0)
    c: Coincident(g3,g0)
    c: Weight(g1) = 1
    c: Equal(g1,g2)
    c: InternalAlignment(g1,g3)
    c: InternalAlignment(g2,g3)
    c: InternalAlignment(g4,g3)
    c: InternalAlignment(g5,g3)
    c: Block(g3)
    c: Coincident(g6,g0)
    c: Coincident(g6,g3)
    c: Horizontal(g6)
FEATURE [Sketcher::SketchObject] Sketch042
  FullyConstrained = true
  sketch-geometry (7):
    g0: LineSegment StartX=0 StartY=0 StartZ=0 EndX=0 EndY=6 EndZ=0
    g1: Circle CenterX=0 CenterY=0 CenterZ=0 NormalX=0 NormalY=0 NormalZ=1 AngleXU=0 Radius=1
    g2: Circle CenterX=8 CenterY=6 CenterZ=0 NormalX=0 NormalY=0 NormalZ=1 AngleXU=0 Radius=1
    g3: BSplineCurve PolesCount=3 KnotsCount=2 Degree=2 IsPeriodic=0
    g4: GeomPoint X=0 Y=0 Z=0
    g5: GeomPoint X=8 Y=6 Z=0
    g6: LineSegment StartX=0 StartY=6 StartZ=0 EndX=8 EndY=6 EndZ=0
  constraints (14):
    c: Coincident(g0,g-1)
    c: Distance(g0) = 6
    c: Vertical(g0)
    c: Coincident(g3,g0)
    c: Weight(g1) = 1
    c: Equal(g1,g2)
    c: InternalAlignment(g1,g3)
    c: InternalAlignment(g2,g3)
    c: InternalAlignment(g4,g3)
    c: InternalAlignment(g5,g3)
    c: Block(g3)
    c: Coincident(g6,g0)
    c: Coincident(g6,g3)
    c: Horizontal(g6)
FEATURE [Part::Extrusion] Extrude030  label="caseScrewPillarBracket008"
  Base = -> Sketch039
  Dir = (0,0,1)
  DirMode = 2
  FaceMakerClass = Part::FaceMakerBullseye
  LengthFwd = 2.4
  LengthRev = 0
  Placement = pos=(15.76,29,8.8) rot=(0,1,0;0rad)
  Solid = true
  Symmetric = false
FEATURE [Part::Extrusion] Extrude031  label="caseScrewPillarBracket009"
  Base = -> Sketch040
  Dir = (0,0,1)
  DirMode = 2
  FaceMakerClass = Part::FaceMakerBullseye
  LengthFwd = 2.4
  LengthRev = 0
  Placement = pos=(15.76,29,60.8) rot=(0,0,1;0rad)
  Solid = true
  Symmetric = false
FEATURE [Part::Extrusion] Extrude032  label="caseScrewPillarBracket010"
  Base = -> Sketch041
  Dir = (0,0,1)
  DirMode = 2
  FaceMakerClass = Part::FaceMakerBullseye
  LengthFwd = 2.4
  LengthRev = 0
  Placement = pos=(13.7,29,13.26) rot=(0,-1,0;1.5708rad)
  Solid = true
  Symmetric = false
FEATURE [Part::Extrusion] Extrude033  label="caseScrewPillarBracket011"
  Base = -> Sketch042
  Dir = (0,0,1)
  DirMode = 2
  FaceMakerClass = Part::FaceMakerBullseye
  LengthFwd = 2.4
  LengthRev = 0
  Placement = pos=(11.3,29,58.74) rot=(0,1,0;1.5708rad)
  Solid = true
  Symmetric = false
FEATURE [Sketcher::SketchObject] Sketch043
  FullyConstrained = true
  sketch-geometry (7):
    g0: LineSegment StartX=0 StartY=0 StartZ=0 EndX=0 EndY=6 EndZ=0
    g1: Circle CenterX=0 CenterY=0 CenterZ=0 NormalX=0 NormalY=0 NormalZ=1 AngleXU=0 Radius=1
    g2: Circle CenterX=8 CenterY=6 CenterZ=0 NormalX=0 NormalY=0 NormalZ=1 AngleXU=0 Radius=1
    g3: BSplineCurve PolesCount=3 KnotsCount=2 Degree=2 IsPeriodic=0
    g4: GeomPoint X=0 Y=0 Z=0
    g5: GeomPoint X=8 Y=6 Z=0
    g6: LineSegment StartX=0 StartY=6 StartZ=0 EndX=8 EndY=6 EndZ=0
  constraints (14):
    c: Coincident(g0,g-1)
    c: Distance(g0) = 6
    c: Vertical(g0)
    c: Coincident(g3,g0)
    c: Weight(g1) = 1
    c: Equal(g1,g2)
    c: InternalAlignment(g1,g3)
    c: InternalAlignment(g2,g3)
    c: InternalAlignment(g4,g3)
    c: InternalAlignment(g5,g3)
    c: Block(g3)
    c: Coincident(g6,g0)
    c: Coincident(g6,g3)
    c: Horizontal(g6)
FEATURE [Part::Extrusion] Extrude034  label="caseScrewPillarBracket012"
  Base = -> Sketch043
  Dir = (0,0,1)
  DirMode = 2
  FaceMakerClass = Part::FaceMakerBullseye
  LengthFwd = 2.4
  LengthRev = 0
  Placement = pos=(88.3,29,65.23) rot=(0,1,0;1.5708rad)
  Solid = true
  Symmetric = false
FEATURE [Sketcher::SketchObject] Sketch044
  FullyConstrained = true
  sketch-geometry (7):
    g0: LineSegment StartX=0 StartY=0 StartZ=0 EndX=0 EndY=6 EndZ=0
    g1: Circle CenterX=0 CenterY=0 CenterZ=0 NormalX=0 NormalY=0 NormalZ=1 AngleXU=0 Radius=1
    g2: Circle CenterX=8 CenterY=6 CenterZ=0 NormalX=0 NormalY=0 NormalZ=1 AngleXU=0 Radius=1
    g3: BSplineCurve PolesCount=3 KnotsCount=2 Degree=2 IsPeriodic=0
    g4: GeomPoint X=0 Y=0 Z=0
    g5: GeomPoint X=8 Y=6 Z=0
    g6: LineSegment StartX=0 StartY=6 StartZ=0 EndX=8 EndY=6 EndZ=0
  constraints (14):
    c: Coincident(g0,g-1)
    c: Distance(g0) = 6
    c: Vertical(g0)
    c: Coincident(g3,g0)
    c: Weight(g1) = 1
    c: Equal(g1,g2)
    c: InternalAlignment(g1,g3)
    c: InternalAlignment(g2,g3)
    c: InternalAlignment(g4,g3)
    c: InternalAlignment(g5,g3)
    c: Block(g3)
    c: Coincident(g6,g0)
    c: Coincident(g6,g3)
    c: Horizontal(g6)
FEATURE [Part::Extrusion] Extrude035  label="caseScrewPillarBracket013"
  Base = -> Sketch044
  Dir = (0,0,1)
  DirMode = 2
  FaceMakerClass = Part::FaceMakerBullseye
  LengthFwd = 2.4
  LengthRev = 0
  Placement = pos=(90.7,29,6.77) rot=(0,-1,0;1.5708rad)
  Solid = true
  Symmetric = false
FEATURE [Sketcher::SketchObject] Sketch045
  FullyConstrained = true
  sketch-geometry (7):
    g0: LineSegment StartX=0 StartY=0 StartZ=0 EndX=0 EndY=6 EndZ=0
    g1: Circle CenterX=0 CenterY=0 CenterZ=0 NormalX=0 NormalY=0 NormalZ=1 AngleXU=0 Radius=1
    g2: Circle CenterX=8 CenterY=6 CenterZ=0 NormalX=0 NormalY=0 NormalZ=1 AngleXU=0 Radius=1
    g3: BSplineCurve PolesCount=3 KnotsCount=2 Degree=2 IsPeriodic=0
    g4: GeomPoint X=0 Y=0 Z=0
    g5: GeomPoint X=8 Y=6 Z=0
    g6: LineSegment StartX=0 StartY=6 StartZ=0 EndX=8 EndY=6 EndZ=0
  constraints (14):
    c: Coincident(g0,g-1)
    c: Distance(g0) = 6
    c: Vertical(g0)
    c: Coincident(g3,g0)
    c: Weight(g1) = 1
    c: Equal(g1,g2)
    c: InternalAlignment(g1,g3)
    c: InternalAlignment(g2,g3)
    c: InternalAlignment(g4,g3)
    c: InternalAlignment(g5,g3)
    c: Block(g3)
    c: Coincident(g6,g0)
    c: Coincident(g6,g3)
    c: Horizontal(g6)
FEATURE [Sketcher::SketchObject] Sketch046
  FullyConstrained = true
  sketch-geometry (7):
    g0: LineSegment StartX=0 StartY=0 StartZ=0 EndX=0 EndY=6 EndZ=0
    g1: Circle CenterX=0 CenterY=0 CenterZ=0 NormalX=0 NormalY=0 NormalZ=1 AngleXU=0 Radius=1
    g2: Circle CenterX=8 CenterY=6 CenterZ=0 NormalX=0 NormalY=0 NormalZ=1 AngleXU=0 Radius=1
    g3: BSplineCurve PolesCount=3 KnotsCount=2 Degree=2 IsPeriodic=0
    g4: GeomPoint X=0 Y=0 Z=0
    g5: GeomPoint X=8 Y=6 Z=0
    g6: LineSegment StartX=0 StartY=6 StartZ=0 EndX=8 EndY=6 EndZ=0
  constraints (14):
    c: Coincident(g0,g-1)
    c: Distance(g0) = 6
    c: Vertical(g0)
    c: Coincident(g3,g0)
    c: Weight(g1) = 1
    c: Equal(g1,g2)
    c: InternalAlignment(g1,g3)
    c: InternalAlignment(g2,g3)
    c: InternalAlignment(g4,g3)
    c: InternalAlignment(g5,g3)
    c: Block(g3)
    c: Coincident(g6,g0)
    c: Coincident(g6,g3)
    c: Horizontal(g6)
FEATURE [Part::Extrusion] Extrude036  label="caseScrewPillarBracket014"
  Base = -> Sketch045
  Dir = (0,0,1)
  DirMode = 2
  FaceMakerClass = Part::FaceMakerBullseye
  LengthFwd = 2.4
  LengthRev = 0
  Placement = pos=(110.7,29,6.77) rot=(0,-1,0;1.5708rad)
  Solid = true
  Symmetric = false
FEATURE [Part::Extrusion] Extrude037  label="caseScrewPillarBracket015"
  Base = -> Sketch046
  Dir = (0,0,1)
  DirMode = 2
  FaceMakerClass = Part::FaceMakerBullseye
  LengthFwd = 2.4
  LengthRev = 0
  Placement = pos=(108.3,29,65.23) rot=(0,1,0;1.5708rad)
  Solid = true
  Symmetric = false
FEATURE [Part::Box] Box013  label="frontCaseScrewPillarBracket002"
  AttacherType = Attacher::AttachEngine3D
  Height = 2.4
  Length = 22
  Placement = pos=(87,28,2.3) rot=(0,0,1;0rad)
  Width = 7
FEATURE [Part::Box] Box014  label="frontCaseScrewPillarBracket003"
  AttacherType = Attacher::AttachEngine3D
  Height = 2.4
  Length = 22
  Placement = pos=(87,28,67.3) rot=(0,0,1;0rad)
  Width = 7
FEATURE [Part::Feature] Face087
  shape: bbox 4.8 x 30.2 x 2e-07 mm, 1 faces, 0 solids (baked)
FEATURE [Part::Revolution] Revolve091  label="frontCaseScrewPost004"
  Angle = 360
  Axis = (0,1,0)
  Base = (0,0,0)
  FaceMakerClass = Part::FaceMakerBullseye
  Placement = pos=(89.5,4.5,3.5) rot=(0,0,1;0rad)
  Solid = false
  Source = -> Face087
  Symmetric = false
FEATURE [Part::Feature] Face088
  shape: bbox 4.8 x 30.2 x 2e-07 mm, 1 faces, 0 solids (baked)
FEATURE [Part::Revolution] Revolve092  label="frontCaseScrewPost005"
  Angle = 360
  Axis = (0,1,0)
  Base = (0,0,0)
  FaceMakerClass = Part::FaceMakerBullseye
  Placement = pos=(89.5,4.5,68.5) rot=(0,0,1;0rad)
  Solid = false
  Source = -> Face088
  Symmetric = false
FEATURE [Part::Feature] Face089
  shape: bbox 3.5 x 30.2 x 2e-07 mm, 1 faces, 0 solids (baked)
FEATURE [Part::Revolution] Revolve093  label="backCaseScrewPost002"
  Angle = 360
  Axis = (0,1,0)
  Base = (0,0,0)
  FaceMakerClass = Part::FaceMakerBullseye
  Placement = pos=(12.5,4.5,10) rot=(0,0,1;0rad)
  Solid = false
  Source = -> Face089
  Symmetric = false
FEATURE [Part::Feature] Face090
  shape: bbox 3.5 x 30.2 x 2e-07 mm, 1 faces, 0 solids (baked)
FEATURE [Part::Revolution] Revolve094  label="backCaseScrewPost003"
  Angle = 360
  Axis = (0,1,0)
  Base = (0,0,0)
  FaceMakerClass = Part::FaceMakerBullseye
  Placement = pos=(12.5,4.5,62) rot=(0,0,1;0rad)
  Solid = false
  Source = -> Face090
  Symmetric = false
FEATURE [Part::Box] Box015  label="Cube011"
  AttacherType = Attacher::AttachEngine3D
  Height = 28.8
  Length = 3
  Placement = pos=(107.3,28,21.6) rot=(0,0,1;0rad)
  Width = 7
FEATURE [Part::Box] Box016  label="Cube012"
  AttacherType = Attacher::AttachEngine3D
  Height = 3
  Length = 7.4
  Placement = pos=(107.3,28,18.6) rot=(0,0,1;0rad)
  Width = 7
FEATURE [Part::Box] Box017  label="Cube013"
  AttacherType = Attacher::AttachEngine3D
  Height = 3
  Length = 7.4
  Placement = pos=(107.3,28,50.4) rot=(0,0,1;0rad)
  Width = 7
FEATURE [Part::Cylinder] Cylinder024
  Angle = 360
  AttacherType = Attacher::AttachEngine3D
  Height = 20
  Placement = pos=(0,0,36.15) rot=(0,0,1;0rad)
  Radius = 14.3
FEATURE [Part::Cylinder] Cylinder025
  Angle = 360
  AttacherType = Attacher::AttachEngine3D
  Height = 10
  Placement = pos=(0,0,36.15) rot=(0,0,1;0rad)
  Radius = 4
FEATURE [Part::MultiFuse] Fusion066  label="removeToCreteHoleForPlugHousing009"
  Placement = pos=(70,19,36) rot=(0,1,0;1.5708rad)
  Shapes = -> [Cylinder024,Cylinder025]
FEATURE [Part::MultiFuse] Fusion065  label="plugHousingBracketHolder002"
  Shapes = -> [Box017,Box015,Box016]
FEATURE [Part::Cut] Cut025  label="plugHousingBracketHolder003"
  Base = -> Fusion065
  Placement = pos=(7,0,0) rot=(0,0,1;0rad)
  Tool = -> Fusion066
FEATURE [Sketcher::SketchObject] Sketch047
  FullyConstrained = false
  Placement = pos=(0,0,0) rot=(1,0,0;1.5708rad)
  sketch-geometry (24):
    g0: ArcOfCircle CenterX=-4 CenterY=-10.5 CenterZ=0 NormalX=0 NormalY=0 NormalZ=1 AngleXU=0 Radius=1.5 StartAngle=6e-16 EndAngle=3.14159
    g1: ArcOfCircle CenterX=-34.2 CenterY=-10.5 CenterZ=0 NormalX=0 NormalY=0 NormalZ=1 AngleXU=0 Radius=1.5 StartAngle=0 EndAngle=3.14159
    g2: ArcOfCircle CenterX=-34.2 CenterY=-27.7 CenterZ=0 NormalX=0 NormalY=0 NormalZ=1 AngleXU=0 Radius=1.5 StartAngle=3.14159 EndAngle=6.28319
    g3: ArcOfCircle CenterX=-4 CenterY=-27.7 CenterZ=0 NormalX=0 NormalY=0 NormalZ=1 AngleXU=0 Radius=1.5 StartAngle=3.1416 EndAngle=6.28319
    g4: ArcOfCircle CenterX=-10 CenterY=-4.3 CenterZ=0 NormalX=0 NormalY=0 NormalZ=1 AngleXU=0 Radius=1.5 StartAngle=2e-16 EndAngle=3.14159
    g5: ArcOfCircle CenterX=-16.1 CenterY=-1.8 CenterZ=0 NormalX=0 NormalY=0 NormalZ=1 AngleXU=0 Radius=1.5 StartAngle=5e-16 EndAngle=3.14159
    g6: ArcOfCircle CenterX=-22.1 CenterY=-1.8 CenterZ=0 NormalX=0 NormalY=0 NormalZ=1 AngleXU=0 Radius=1.5 StartAngle=5e-16 EndAngle=3.14159
    g7: ArcOfCircle CenterX=-28.2 CenterY=-4.3 CenterZ=0 NormalX=0 NormalY=0 NormalZ=1 AngleXU=0 Radius=1.5 StartAngle=2e-16 EndAngle=3.14159
    g8: ArcOfCircle CenterX=-10 CenterY=-33.9 CenterZ=0 NormalX=0 NormalY=0 NormalZ=1 AngleXU=0 Radius=1.5 StartAngle=3.14159 EndAngle=6.28319
    g9: ArcOfCircle CenterX=-16.1 CenterY=-36.4 CenterZ=0 NormalX=0 NormalY=0 NormalZ=1 AngleXU=0 Radius=1.5 StartAngle=3.14159 EndAngle=6.28319
    g10: ArcOfCircle CenterX=-22.1 CenterY=-36.4 CenterZ=0 NormalX=0 NormalY=0 NormalZ=1 AngleXU=0 Radius=1.5 StartAngle=3.14159 EndAngle=6.28319
    g11: ArcOfCircle CenterX=-28.2 CenterY=-33.9 CenterZ=0 NormalX=0 NormalY=0 NormalZ=1 AngleXU=0 Radius=1.5 StartAngle=3.14159 EndAngle=6.28319
    g12: LineSegment StartX=-35.7 StartY=-10.5 StartZ=0 EndX=-35.7 EndY=-27.7 EndZ=0
    g13: LineSegment StartX=-32.7 StartY=-10.5 StartZ=0 EndX=-32.7 EndY=-27.7 EndZ=0
    g14: LineSegment StartX=-29.7 StartY=-33.9 StartZ=0 EndX=-29.7 EndY=-4.3 EndZ=0
    g15: LineSegment StartX=-26.7 StartY=-33.9 StartZ=0 EndX=-26.7 EndY=-4.3 EndZ=0
    g16: LineSegment StartX=-2.5 StartY=-10.5 StartZ=0 EndX=-2.5 EndY=-27.7 EndZ=0
    g17: LineSegment StartX=-8.5 StartY=-4.3 StartZ=0 EndX=-8.5 EndY=-33.9 EndZ=0
    g18: LineSegment StartX=-5.5 StartY=-10.5 StartZ=0 EndX=-5.5 EndY=-27.7 EndZ=0
    g19: LineSegment StartX=-11.5 StartY=-4.3 StartZ=0 EndX=-11.5 EndY=-33.9 EndZ=0
    g20: LineSegment StartX=-14.6 StartY=-1.8 StartZ=0 EndX=-14.6 EndY=-36.4 EndZ=0
    g21: LineSegment StartX=-17.6 StartY=-1.8 StartZ=0 EndX=-17.6 EndY=-36.4 EndZ=0
    g22: LineSegment StartX=-20.6 StartY=-36.4 StartZ=0 EndX=-20.6 EndY=-1.8 EndZ=0
    g23: LineSegment StartX=-23.6 StartY=-1.8 StartZ=0 EndX=-23.6 EndY=-36.4 EndZ=0
  constraints (48):
    c: Block(g0)
    c: Block(g1)
    c: Block(g2)
    c: Block(g3)
    c: Block(g4)
    c: Block(g5)
    c: Block(g6)
    c: Block(g7)
    c: Block(g8)
    c: Block(g9)
    c: Block(g10)
    c: Block(g11)
    c: Coincident(g12,g1)
    c: Coincident(g12,g2)
    c: Vertical(g12)
    c: Coincident(g13,g1)
    c: Coincident(g13,g2)
    c: Vertical(g13)
    c: Coincident(g14,g11)
    c: Coincident(g14,g7)
    c: Vertical(g14)
    c: Coincident(g15,g11)
    c: Coincident(g15,g7)
    c: Vertical(g15)
    c: Coincident(g16,g0)
    c: Coincident(g16,g3)
    c: Vertical(g16)
    c: Coincident(g17,g4)
    c: Coincident(g17,g8)
    c: Vertical(g17)
    c: Coincident(g18,g0)
    c: Coincident(g18,g3)
    c: Vertical(g18)
    c: Coincident(g19,g4)
    c: Coincident(g19,g8)
    c: Vertical(g19)
    c: Coincident(g20,g5)
    c: Coincident(g20,g9)
    c: Vertical(g20)
    c: Coincident(g21,g5)
    c: Coincident(g21,g9)
    c: Vertical(g21)
    c: Coincident(g22,g10)
    c: Coincident(g22,g6)
    c: Vertical(g22)
    c: Coincident(g23,g6)
    c: Coincident(g23,g10)
    c: Vertical(g23)
FEATURE [Part::Extrusion] Extrude038  label="removeToCreateFanGrillHoles001"
  Base = -> Sketch047
  Dir = (0,-1,6e-16)
  DirMode = 2
  FaceMakerClass = Part::FaceMakerBullseye
  LengthFwd = 10
  LengthRev = 0
  Placement = pos=(65.4,44,54.82) rot=(0,0,1;0rad)
  Solid = true
  Symmetric = false
FEATURE [Part::Feature] Wire004
  shape: bbox 11 x 5.2 x 2e-07 mm, 0 faces, 0 solids (baked)
FEATURE [Part::Revolution] Revolve095
  Angle = 360
  Axis = (0,1,0)
  Base = (0,0,0)
  FaceMakerClass = Part::FaceMakerBullseye
  Placement = pos=(30.3,38,19.7) rot=(0,0,1;0rad)
  Solid = true
  Source = -> Wire004
  Symmetric = false
FEATURE [Part::Feature] Wire005
  shape: bbox 11 x 5.2 x 2e-07 mm, 0 faces, 0 solids (baked)
FEATURE [Part::Revolution] Revolve096
  Angle = 360
  Axis = (0,1,0)
  Base = (0,0,0)
  FaceMakerClass = Part::FaceMakerBullseye
  Placement = pos=(30.3,38,51.7) rot=(0,0,1;0rad)
  Solid = true
  Source = -> Wire005
  Symmetric = false
FEATURE [Part::Feature] Wire006
  shape: bbox 11 x 5.2 x 2e-07 mm, 0 faces, 0 solids (baked)
FEATURE [Part::Revolution] Revolve097
  Angle = 360
  Axis = (0,1,0)
  Base = (0,0,0)
  FaceMakerClass = Part::FaceMakerBullseye
  Placement = pos=(62.3,38,51.7) rot=(0,0,1;0rad)
  Solid = true
  Source = -> Wire006
  Symmetric = false
FEATURE [Part::Feature] Wire007
  shape: bbox 11 x 5.2 x 2e-07 mm, 0 faces, 0 solids (baked)
FEATURE [Part::Revolution] Revolve098
  Angle = 360
  Axis = (0,1,0)
  Base = (0,0,0)
  FaceMakerClass = Part::FaceMakerBullseye
  Placement = pos=(62.3,38,19.7) rot=(0,0,1;0rad)
  Solid = true
  Source = -> Wire007
  Symmetric = false
FEATURE [Part::MultiFuse] Fusion067  label="fanScrewHousing002"
  Shapes = -> [Revolve098,Revolve097,Revolve096,Revolve095]
FEATURE [Part::Feature] Face091 .. Face094  x4 (patterned run collapsed; names and placements below)
  shape: bbox 3.5 x 17.8 x 2e-07 mm, 1 faces, 0 solids (baked)
FEATURE [Part::Revolution] Revolve099  label="removeToCreateScrewAndThreadedInsertHole026"
  Angle = 360
  Axis = (0,1,0)
  Base = (0,0,0)
  FaceMakerClass = Part::FaceMakerBullseye
  Placement = pos=(62.3,30.3,19.7) rot=(0,0,1;0rad)
  Solid = false
  Source = -> Face091
  Symmetric = false
FEATURE [Part::Revolution] Revolve100  label="removeToCreateScrewAndThreadedInsertHole027"
  Angle = 360
  Axis = (0,1,0)
  Base = (0,0,0)
  FaceMakerClass = Part::FaceMakerBullseye
  Placement = pos=(62.3,30.3,51.7) rot=(0,0,1;0rad)
  Solid = false
  Source = -> Face092
  Symmetric = false
FEATURE [Part::Revolution] Revolve101  label="removeToCreateScrewAndThreadedInsertHole028"
  Angle = 360
  Axis = (0,1,0)
  Base = (0,0,0)
  FaceMakerClass = Part::FaceMakerBullseye
  Placement = pos=(30.3,30.3,19.7) rot=(0,0,1;0rad)
  Solid = false
  Source = -> Face093
  Symmetric = false
FEATURE [Part::Revolution] Revolve102  label="removeToCreateScrewAndThreadedInsertHole029"
  Angle = 360
  Axis = (0,1,0)
  Base = (0,0,0)
  FaceMakerClass = Part::FaceMakerBullseye
  Placement = pos=(30.3,30.3,51.7) rot=(0,0,1;0rad)
  Solid = false
  Source = -> Face094
  Symmetric = false
FEATURE [Part::MultiFuse] Fusion068  label="createThreadedInsertHolesForFan002"
  Shapes = -> [Revolve099,Revolve100,Revolve101,Revolve102]
FEATURE [Part::Cut] Cut026  label="fanScrewHousing003"
  Base = -> Fusion067
  Tool = -> Fusion068
FEATURE [Sketcher::SketchObject] Sketch048
  FullyConstrained = false
  Placement = pos=(0,0,0) rot=(1,0,0;1.5708rad)
  sketch-geometry (24):
    g0: ArcOfCircle CenterX=-4 CenterY=-10.5 CenterZ=0 NormalX=0 NormalY=0 NormalZ=1 AngleXU=0 Radius=1.5 StartAngle=6e-16 EndAngle=3.14159
    g1: ArcOfCircle CenterX=-34.2 CenterY=-10.5 CenterZ=0 NormalX=0 NormalY=0 NormalZ=1 AngleXU=0 Radius=1.5 StartAngle=0 EndAngle=3.14159
    g2: ArcOfCircle CenterX=-34.2 CenterY=-27.7 CenterZ=0 NormalX=0 NormalY=0 NormalZ=1 AngleXU=0 Radius=1.5 StartAngle=3.14159 EndAngle=6.28319
    g3: ArcOfCircle CenterX=-4 CenterY=-27.7 CenterZ=0 NormalX=0 NormalY=0 NormalZ=1 AngleXU=0 Radius=1.5 StartAngle=3.1416 EndAngle=6.28319
    g4: ArcOfCircle CenterX=-10 CenterY=-4.3 CenterZ=0 NormalX=0 NormalY=0 NormalZ=1 AngleXU=0 Radius=1.5 StartAngle=2e-16 EndAngle=3.14159
    g5: ArcOfCircle CenterX=-16.1 CenterY=-1.8 CenterZ=0 NormalX=0 NormalY=0 NormalZ=1 AngleXU=0 Radius=1.5 StartAngle=5e-16 EndAngle=3.14159
    g6: ArcOfCircle CenterX=-22.1 CenterY=-1.8 CenterZ=0 NormalX=0 NormalY=0 NormalZ=1 AngleXU=0 Radius=1.5 StartAngle=5e-16 EndAngle=3.14159
    g7: ArcOfCircle CenterX=-28.2 CenterY=-4.3 CenterZ=0 NormalX=0 NormalY=0 NormalZ=1 AngleXU=0 Radius=1.5 StartAngle=2e-16 EndAngle=3.14159
    g8: ArcOfCircle CenterX=-10 CenterY=-33.9 CenterZ=0 NormalX=0 NormalY=0 NormalZ=1 AngleXU=0 Radius=1.5 StartAngle=3.14159 EndAngle=6.28319
    g9: ArcOfCircle CenterX=-16.1 CenterY=-36.4 CenterZ=0 NormalX=0 NormalY=0 NormalZ=1 AngleXU=0 Radius=1.5 StartAngle=3.14159 EndAngle=6.28319
    g10: ArcOfCircle CenterX=-22.1 CenterY=-36.4 CenterZ=0 NormalX=0 NormalY=0 NormalZ=1 AngleXU=0 Radius=1.5 StartAngle=3.14159 EndAngle=6.28319
    g11: ArcOfCircle CenterX=-28.2 CenterY=-33.9 CenterZ=0 NormalX=0 NormalY=0 NormalZ=1 AngleXU=0 Radius=1.5 StartAngle=3.14159 EndAngle=6.28319
    g12: LineSegment StartX=-35.7 StartY=-10.5 StartZ=0 EndX=-35.7 EndY=-27.7 EndZ=0
    g13: LineSegment StartX=-32.7 StartY=-10.5 StartZ=0 EndX=-32.7 EndY=-27.7 EndZ=0
    g14: LineSegment StartX=-29.7 StartY=-33.9 StartZ=0 EndX=-29.7 EndY=-4.3 EndZ=0
    g15: LineSegment StartX=-26.7 StartY=-33.9 StartZ=0 EndX=-26.7 EndY=-4.3 EndZ=0
    g16: LineSegment StartX=-2.5 StartY=-10.5 StartZ=0 EndX=-2.5 EndY=-27.7 EndZ=0
    g17: LineSegment StartX=-8.5 StartY=-4.3 StartZ=0 EndX=-8.5 EndY=-33.9 EndZ=0
    g18: LineSegment StartX=-5.5 StartY=-10.5 StartZ=0 EndX=-5.5 EndY=-27.7 EndZ=0
    g19: LineSegment StartX=-11.5 StartY=-4.3 StartZ=0 EndX=-11.5 EndY=-33.9 EndZ=0
    g20: LineSegment StartX=-14.6 StartY=-1.8 StartZ=0 EndX=-14.6 EndY=-36.4 EndZ=0
    g21: LineSegment StartX=-17.6 StartY=-1.8 StartZ=0 EndX=-17.6 EndY=-36.4 EndZ=0
    g22: LineSegment StartX=-20.6 StartY=-36.4 StartZ=0 EndX=-20.6 EndY=-1.8 EndZ=0
    g23: LineSegment StartX=-23.6 StartY=-1.8 StartZ=0 EndX=-23.6 EndY=-36.4 EndZ=0
  constraints (48):
    c: Block(g0)
    c: Block(g1)
    c: Block(g2)
    c: Block(g3)
    c: Block(g4)
    c: Block(g5)
    c: Block(g6)
    c: Block(g7)
    c: Block(g8)
    c: Block(g9)
    c: Block(g10)
    c: Block(g11)
    c: Coincident(g12,g1)
    c: Coincident(g12,g2)
    c: Vertical(g12)
    c: Coincident(g13,g1)
    c: Coincident(g13,g2)
    c: Vertical(g13)
    c: Coincident(g14,g11)
    c: Coincident(g14,g7)
    c: Vertical(g14)
    c: Coincident(g15,g11)
    c: Coincident(g15,g7)
    c: Vertical(g15)
    c: Coincident(g16,g0)
    c: Coincident(g16,g3)
    c: Vertical(g16)
    c: Coincident(g17,g4)
    c: Coincident(g17,g8)
    c: Vertical(g17)
    c: Coincident(g18,g0)
    c: Coincident(g18,g3)
    c: Vertical(g18)
    c: Coincident(g19,g4)
    c: Coincident(g19,g8)
    c: Vertical(g19)
    c: Coincident(g20,g5)
    c: Coincident(g20,g9)
    c: Vertical(g20)
    c: Coincident(g21,g5)
    c: Coincident(g21,g9)
    c: Vertical(g21)
    c: Coincident(g22,g10)
    c: Coincident(g22,g6)
    c: Vertical(g22)
    c: Coincident(g23,g6)
    c: Coincident(g23,g10)
    c: Vertical(g23)
FEATURE [Part::Extrusion] Extrude039  label="removeToCreateFanGrillHoles002"
  Base = -> Sketch048
  Dir = (0,-1,6e-16)
  DirMode = 2
  FaceMakerClass = Part::FaceMakerBullseye
  LengthFwd = 10
  LengthRev = 0
  Placement = pos=(65.4,44,54.82) rot=(0,0,1;0rad)
  Solid = true
  Symmetric = false
FEATURE [Part::Cut] Cut027  label="fanScrewHousing004"
  Base = -> Cut026
  Tool = -> Extrude038
FEATURE [Part::Cut] Cut028  label="top014"
  Base = -> Fillet026
  Tool = -> Extrude039
FEATURE [Part::Feature] Face095 .. Face098  x4 (patterned run collapsed; names and placements below)
  shape: bbox 3.5 x 17.8 x 2e-07 mm, 1 faces, 0 solids (baked)
FEATURE [Part::Revolution] Revolve103  label="removeToCreateScrewAndThreadedInsertHole030"
  Angle = 360
  Axis = (0,1,0)
  Base = (0,0,0)
  FaceMakerClass = Part::FaceMakerBullseye
  Placement = pos=(62.3,30.3,19.7) rot=(0,0,1;0rad)
  Solid = false
  Source = -> Face095
  Symmetric = false
FEATURE [Part::Revolution] Revolve104  label="removeToCreateScrewAndThreadedInsertHole031"
  Angle = 360
  Axis = (0,1,0)
  Base = (0,0,0)
  FaceMakerClass = Part::FaceMakerBullseye
  Placement = pos=(62.3,30.3,51.7) rot=(0,0,1;0rad)
  Solid = false
  Source = -> Face096
  Symmetric = false
FEATURE [Part::Revolution] Revolve105  label="removeToCreateScrewAndThreadedInsertHole032"
  Angle = 360
  Axis = (0,1,0)
  Base = (0,0,0)
  FaceMakerClass = Part::FaceMakerBullseye
  Placement = pos=(30.3,30.3,19.7) rot=(0,0,1;0rad)
  Solid = false
  Source = -> Face097
  Symmetric = false
FEATURE [Part::Revolution] Revolve106  label="removeToCreateScrewAndThreadedInsertHole033"
  Angle = 360
  Axis = (0,1,0)
  Base = (0,0,0)
  FaceMakerClass = Part::FaceMakerBullseye
  Placement = pos=(30.3,30.3,51.7) rot=(0,0,1;0rad)
  Solid = false
  Source = -> Face098
  Symmetric = false
FEATURE [Part::MultiFuse] Fusion069  label="createThreadedInsertHolesForFan003"
  Shapes = -> [Revolve103,Revolve104,Revolve105,Revolve106]
FEATURE [Part::Cut] Cut029  label="top015"
  Base = -> Cut028
  Tool = -> Fusion054
FEATURE [Part::Cut] Cut030  label="fanScrewHousing005"
  Base = -> Cut027
  Tool = -> Fusion069
FEATURE [Part::Cylinder] Cylinder026  label="removeToCreteHoleForPlugHousing010"
  Angle = 360
  AttacherType = Attacher::AttachEngine3D
  Height = 20
  Placement = pos=(-2,19,36) rot=(0,1,0;1.5708rad)
  Radius = 14.3
FEATURE [Part::Box] Box018  label="removeToCreteHoleForPlugHousing011"
  AttacherType = Attacher::AttachEngine3D
  Height = 28.6
  Length = 10
  Placement = pos=(-2,0,21.7) rot=(0,0,1;0rad)
  Width = 19
FEATURE [Part::Box] Box019  label="wireHolderBottomCaseBit"
  AttacherType = Attacher::AttachEngine3D
  Height = 28
  Length = 3
  Placement = pos=(0,0,22) rot=(0,0,1;0rad)
  Width = 21
FEATURE [Part::Cylinder] Cylinder027  label="removeToCreteHoleForPlugHousing012"
  Angle = 360
  AttacherType = Attacher::AttachEngine3D
  Height = 20
  Placement = pos=(-2,19,36) rot=(0,1,0;1.5708rad)
  Radius = 14.3
FEATURE [Part::Cut] Cut031  label="wireHolderBottomCaseBit001"
  Base = -> Box019
  Tool = -> Cylinder027
FEATURE [Part::MultiFuse] Fusion070  label="removeToCreteHoleForPlugHousing013"
  Shapes = -> [Box018,Cylinder026]
FEATURE [Part::Cut] Cut032  label="top016"
  Base = -> Cut029
  Tool = -> Fusion070
FEATURE [Part::Cylinder] Cylinder028
  Angle = 360
  AttacherType = Attacher::AttachEngine3D
  Height = 20
  Placement = pos=(0,0,36.15) rot=(0,0,1;0rad)
  Radius = 14.3
FEATURE [Part::Cylinder] Cylinder029
  Angle = 360
  AttacherType = Attacher::AttachEngine3D
  Height = 10
  Placement = pos=(0,0,36.15) rot=(0,0,1;0rad)
  Radius = 4
FEATURE [Part::MultiFuse] Fusion071  label="removeToCreteHoleForPlugHousing014"
  Placement = pos=(70,19,36) rot=(0,1,0;1.5708rad)
  Shapes = -> [Cylinder028,Cylinder029]
FEATURE [Sketcher::SketchObject] Sketch049  label="topSketch011"
  FullyConstrained = true
  sketch-geometry (4):
    g0: ArcOfCircle CenterX=105 CenterY=19 CenterZ=0 NormalX=0 NormalY=0 NormalZ=1 AngleXU=0 Radius=20.6155 StartAngle=5.54125 EndAngle=6.28319
    g1: ArcOfCircle CenterX=105 CenterY=19 CenterZ=0 NormalX=0 NormalY=0 NormalZ=1 AngleXU=0 Radius=13 StartAngle=5.54125 EndAngle=6.28319
    g2: LineSegment StartX=118 StartY=19 StartZ=0 EndX=125.616 EndY=19 EndZ=0
    g3: LineSegment StartX=114.583 StartY=10.2157 StartZ=0 EndX=120.197 EndY=5.06982 EndZ=0
  constraints (7):
    c: Block(g0)
    c: Block(g1)
    c: Coincident(g2,g1)
    c: Coincident(g2,g0)
    c: Horizontal(g2)
    c: Coincident(g3,g1)
    c: Coincident(g3,g0)
FEATURE [Part::Box] Box020  label="removeToCreteHoleForPlugHousing015"
  AttacherType = Attacher::AttachEngine3D
  Height = 28.6
  Length = 20
  Placement = pos=(106.15,0,21.7) rot=(0,0,1;0rad)
  Width = 19
FEATURE [Part::MultiFuse] Fusion072  label="removeToCreteHoleForPlugHousing016"
  Shapes = -> [Box020,Fusion071]
FEATURE [Part::Cut] Cut033  label="removeToCreteHoleForPlugHousing017"
  Base = -> Cut032
  Tool = -> Fusion072
FEATURE [Part::Cylinder] Cylinder030
  Angle = 360
  AttacherType = Attacher::AttachEngine3D
  Height = 20
  Placement = pos=(0,0,36.15) rot=(0,0,1;0rad)
  Radius = 14.3
FEATURE [Part::Cylinder] Cylinder031
  Angle = 360
  AttacherType = Attacher::AttachEngine3D
  Height = 10
  Placement = pos=(0,0,36.15) rot=(0,0,1;0rad)
  Radius = 4
FEATURE [Part::Box] Box021  label="removeToCreteHoleForPlugHousing019"
  AttacherType = Attacher::AttachEngine3D
  Height = 28.6
  Length = 20
  Placement = pos=(106.15,0,21.7) rot=(0,0,1;0rad)
  Width = 19
FEATURE [Part::MultiFuse] Fusion074  label="removeToCreteHoleForPlugHousing020"
  Placement = pos=(70,19,36) rot=(0,1,0;1.5708rad)
  Shapes = -> [Cylinder030,Cylinder031]
FEATURE [Part::MultiFuse] Fusion073  label="removeToCreteHoleForPlugHousing018"
  Placement = pos=(0,0,28.3) rot=(0,0,1;0rad)
  Shapes = -> [Box021,Fusion074]
FEATURE [Part::Cylinder] Cylinder032
  Angle = 360
  AttacherType = Attacher::AttachEngine3D
  Height = 20
  Placement = pos=(0,0,36.15) rot=(0,0,1;0rad)
  Radius = 14.3
FEATURE [Part::Cylinder] Cylinder033
  Angle = 360
  AttacherType = Attacher::AttachEngine3D
  Height = 10
  Placement = pos=(0,0,36.15) rot=(0,0,1;0rad)
  Radius = 4
FEATURE [Part::Box] Box022  label="removeToCreteHoleForPlugHousing021"
  AttacherType = Attacher::AttachEngine3D
  Height = 28.6
  Length = 20
  Placement = pos=(106.15,0,21.7) rot=(0,0,1;0rad)
  Width = 19
FEATURE [Part::MultiFuse] Fusion076  label="removeToCreteHoleForPlugHousing023"
  Placement = pos=(70,19,36) rot=(0,1,0;1.5708rad)
  Shapes = -> [Cylinder032,Cylinder033]
FEATURE [Part::MultiFuse] Fusion075  label="removeToCreteHoleForPlugHousing022"
  Placement = pos=(0,0,-28.3) rot=(0,0,1;0rad)
  Shapes = -> [Box022,Fusion076]
FEATURE [Part::MultiFuse] Fusion077  label="removeToCreatePlugHousingBottomBit"
  Shapes = -> [Fusion075,Fusion073]
FEATURE [Part::Cylinder] Cylinder034
  Angle = 360
  AttacherType = Attacher::AttachEngine3D
  Height = 20
  Placement = pos=(0,0,36.15) rot=(0,0,1;0rad)
  Radius = 14
FEATURE [Part::Cylinder] Cylinder035
  Angle = 360
  AttacherType = Attacher::AttachEngine3D
  Height = 10
  Placement = pos=(0,0,36.15) rot=(0,0,1;0rad)
  Radius = 4
FEATURE [Part::MultiFuse] Fusion078  label="removeToCreteHoleForPlugHousing024"
  Placement = pos=(70,19,36) rot=(0,1,0;1.5708rad)
  Shapes = -> [Cylinder034,Cylinder035]
FEATURE [Part::MultiFuse] Fusion079  label="removeToCreatePlugHousingBottomBit001"
  Shapes = -> [Fusion078,Fusion077]
FEATURE [Part::Extrusion] Extrude040  label="bottomPlugHousingBit"
  Base = -> Sketch049
  Dir = (0,0,1)
  DirMode = 2
  FaceMakerClass = Part::FaceMakerBullseye
  LengthFwd = 72
  LengthRev = 0
  Solid = true
  Symmetric = false
FEATURE [Part::Cut] Cut034  label="bottomPlugHousingBit001"
  Base = -> Extrude040
  Placement = pos=(-0.09,0,0) rot=(0,0,1;0rad)
  Tool = -> Fusion079
FEATURE [Part::Box] Box023  label="Cube014"
  AttacherType = Attacher::AttachEngine3D
  Height = 16
  Length = 8
  Placement = pos=(12.7,31.52,28) rot=(0,0,1;0rad)
  Width = 4
FEATURE [Part::Cylinder] Cylinder036
  Angle = 360
  AttacherType = Attacher::AttachEngine3D
  Height = 10
  Placement = pos=(0,0,36.15) rot=(0,0,1;0rad)
  Radius = 4
FEATURE [Part::Cylinder] Cylinder037
  Angle = 360
  AttacherType = Attacher::AttachEngine3D
  Height = 20
  Placement = pos=(0,0,36.15) rot=(0,0,1;0rad)
  Radius = 8.2
FEATURE [Part::MultiFuse] Fusion080  label="removeToCreteHoleForPlugHousing025"
  Placement = pos=(-42,19,36) rot=(0,1,0;1.5708rad)
  Shapes = -> [Cylinder037,Cylinder036]
FEATURE [Sketcher::SketchObject] Sketch050  label="topSketch012"
  FullyConstrained = true
  sketch-geometry (4):
    g0: LineSegment StartX=16.8446 StartY=31.512 StartZ=0 EndX=16.3251 EndY=34.4666 EndZ=0
    g1: ArcOfCircle CenterX=19 CenterY=19.2524 CenterZ=0 NormalX=0 NormalY=0 NormalZ=1 AngleXU=0 Radius=15.4476 StartAngle=1.74483 EndAngle=2.72717
    g2: ArcOfCircle CenterX=19 CenterY=19.2524 CenterZ=0 NormalX=0 NormalY=0 NormalZ=1 AngleXU=0 Radius=12.4476 StartAngle=1.74483 EndAngle=2.73189
    g3: LineSegment StartX=4.86004 StartY=25.4725 StartZ=0 EndX=7.58253 EndY=24.2107 EndZ=0
  constraints (7):
    c: Block(g0)
    c: Coincident(g1,g0)
    c: Coincident(g2,g0)
    c: Coincident(g3,g1)
    c: Coincident(g3,g2)
    c: Block(g1)
    c: Block(g2)
FEATURE [Part::Extrusion] Extrude041
  Base = -> Sketch050
  Dir = (0,0,1)
  DirMode = 2
  FaceMakerClass = Part::FaceMakerBullseye
  LengthFwd = 10.6
  LengthRev = 0
  Placement = pos=(0,0,31) rot=(0,0,1;0rad)
  Solid = true
  Symmetric = false
FEATURE [Part::Cut] Cut035
  Base = -> Extrude041
  Placement = pos=(0,0,-0.3) rot=(0,0,1;0rad)
  Tool = -> Fusion080
FEATURE [Part::Cut] Cut036
  Base = -> Box023
  Tool = -> Cut035
FEATURE [Part::Fillet] Fillet027
  Base = -> Cut036
  Edges = 1 edges r=0.7: [Edge13]
FEATURE [Part::Fillet] Fillet028
  Base = -> Fillet027
  Edges = 1 edges r=0.7: [Edge13]
FEATURE [Part::Fillet] Fillet029
  Base = -> Fillet028
  Edges = 1 edges r=0.7: [Edge16]
FEATURE [Part::Fillet] Fillet030
  Base = -> Fillet029
  Edges = 1 edges r=0.7: [Edge11]
FEATURE [Part::Fillet] Fillet031
  Base = -> Fillet030
  Edges = 1 edges r=0.7: [Edge10]
FEATURE [Part::Fillet] Fillet032
  Base = -> Fillet031
  Edges = 1 edges r=1.2: [Edge5]
FEATURE [Part::Fillet] Fillet033
  Base = -> Fillet032
  Edges = 1 edges r=1.2: [Edge12]
FEATURE [Part::Fillet] Fillet034  label="wireHousingRetainer"
  Base = -> Fillet033
  Edges = 1 edges r=2: [Edge1]
  Placement = pos=(0.3,0,0) rot=(0,0,1;0rad)
FEATURE [Part::Feature] Face099
  shape: bbox 3.5 x 17.8 x 2e-07 mm, 1 faces, 0 solids (baked)
FEATURE [Part::Revolution] Revolve107  label="removeToCreateScrewAndThreadedInsertHole034"
  Angle = 360
  Axis = (0,1,0)
  Base = (0,0,0)
  FaceMakerClass = Part::FaceMakerBullseye
  Placement = pos=(12.5,0,10) rot=(0,0,1;0rad)
  Solid = false
  Source = -> Face099
  Symmetric = false
FEATURE [Part::Feature] Face100
  shape: bbox 3.5 x 17.8 x 2e-07 mm, 1 faces, 0 solids (baked)
FEATURE [Part::Revolution] Revolve108  label="removeToCreateScrewAndThreadedInsertHole035"
  Angle = 360
  Axis = (0,1,0)
  Base = (0,0,0)
  FaceMakerClass = Part::FaceMakerBullseye
  Placement = pos=(12.5,0,62) rot=(0,0,1;0rad)
  Solid = false
  Source = -> Face100
  Symmetric = false
FEATURE [Part::Feature] Face101
  shape: bbox 3.5 x 17.8 x 2e-07 mm, 1 faces, 0 solids (baked)
FEATURE [Part::Revolution] Revolve109  label="removeToCreateScrewAndThreadedInsertHole036"
  Angle = 360
  Axis = (0,1,0)
  Base = (0,0,0)
  FaceMakerClass = Part::FaceMakerBullseye
  Placement = pos=(89.5,0,68.5) rot=(0,0,1;0rad)
  Solid = false
  Source = -> Face101
  Symmetric = false
FEATURE [Part::Feature] Face102
  shape: bbox 3.5 x 17.8 x 2e-07 mm, 1 faces, 0 solids (baked)
FEATURE [Part::Revolution] Revolve110  label="removeToCreateScrewAndThreadedInsertHole037"
  Angle = 360
  Axis = (0,1,0)
  Base = (0,0,0)
  FaceMakerClass = Part::FaceMakerBullseye
  Placement = pos=(89.5,0,3.5) rot=(0,0,1;0rad)
  Solid = false
  Source = -> Face102
  Symmetric = false
FEATURE [Part::Feature] Face103
  shape: bbox 3.5 x 17.8 x 2e-07 mm, 1 faces, 0 solids (baked)
FEATURE [Part::Revolution] Revolve111  label="removeToCreateScrewAndThreadedInsertHole038"
  Angle = 360
  Axis = (0,1,0)
  Base = (0,0,0)
  FaceMakerClass = Part::FaceMakerBullseye
  Placement = pos=(109.5,4.7,3.5) rot=(0,0,1;0rad)
  Solid = false
  Source = -> Face103
  Symmetric = false
FEATURE [Part::Feature] Face104
  shape: bbox 3.5 x 17.8 x 2e-07 mm, 1 faces, 0 solids (baked)
FEATURE [Part::Revolution] Revolve112  label="removeToCreateScrewAndThreadedInsertHole039"
  Angle = 360
  Axis = (0,1,0)
  Base = (0,0,0)
  FaceMakerClass = Part::FaceMakerBullseye
  Placement = pos=(109.5,4.7,68.5) rot=(0,0,1;0rad)
  Solid = false
  Source = -> Face104
  Symmetric = false
FEATURE [Part::MultiFuse] Fusion081  label="removeToCreateScrewAndThreadedInsertHole040"
  Shapes = -> [Revolve107,Revolve108,Revolve109,Revolve110,Revolve111,Revolve112]
FEATURE [Part::MultiFuse] Fusion082  label="casePillars002"
  Shapes = -> [Revolve094,Revolve092,Revolve090,Revolve089,Revolve091,Revolve093]
FEATURE [Part::Cut] Cut037  label="casePillars003"
  Base = -> Fusion082
  Tool = -> Fusion081
FEATURE [Sketcher::SketchObject] Sketch051
  FullyConstrained = true
  Placement = pos=(117,19,0) rot=(0.57735,0.57735,0.57735;2.0944rad)
  sketch-geometry (48):
    g0: LineSegment StartX=-49.19 StartY=69.25 StartZ=0 EndX=-49.19 EndY=66.25 EndZ=0
    g1: LineSegment StartX=-49.19 StartY=63.5 StartZ=0 EndX=-49.19 EndY=60.5 EndZ=0
    g2: LineSegment StartX=-49.19 StartY=57.75 StartZ=0 EndX=-49.19 EndY=54.75 EndZ=0
    g3: LineSegment StartX=-49.19 StartY=52 StartZ=0 EndX=-49.19 EndY=49 EndZ=0
    g4: LineSegment StartX=-49.19 StartY=46.25 StartZ=0 EndX=-49.19 EndY=43.25 EndZ=0
    g5: LineSegment StartX=-49.19 StartY=40.5 StartZ=0 EndX=-49.19 EndY=37.5 EndZ=0
    g6: LineSegment StartX=-49.19 StartY=34.5 StartZ=0 EndX=-49.19 EndY=31.5 EndZ=0
    g7: LineSegment StartX=-49.19 StartY=28.75 StartZ=0 EndX=-49.19 EndY=25.75 EndZ=0
    g8: LineSegment StartX=-49.19 StartY=23 StartZ=0 EndX=-49.19 EndY=20 EndZ=0
    g9: LineSegment StartX=-49.19 StartY=17.25 StartZ=0 EndX=-49.19 EndY=14.25 EndZ=0
    g10: LineSegment StartX=-49.19 StartY=11.5 StartZ=0 EndX=-49.19 EndY=8.5 EndZ=0
    g11: LineSegment StartX=-49.19 StartY=5.75 StartZ=0 EndX=-49.19 EndY=2.75 EndZ=0
    g12: ArcOfCircle CenterX=-1.5 CenterY=67.75 CenterZ=0 NormalX=0 NormalY=0 NormalZ=1 AngleXU=0 Radius=1.5 StartAngle=4.71239 EndAngle=7.85398
    g13: ArcOfCircle CenterX=-1.5 CenterY=62 CenterZ=0 NormalX=0 NormalY=0 NormalZ=1 AngleXU=0 Radius=1.5 StartAngle=4.71239 EndAngle=7.85398
    g14: ArcOfCircle CenterX=-1.5 CenterY=56.25 CenterZ=0 NormalX=0 NormalY=0 NormalZ=1 AngleXU=0 Radius=1.5 StartAngle=4.71239 EndAngle=7.85398
    g15: ArcOfCircle CenterX=-11.49 CenterY=50.5 CenterZ=0 NormalX=0 NormalY=0 NormalZ=1 AngleXU=0 Radius=1.5 StartAngle=4.71239 EndAngle=7.85398
    g16: ArcOfCircle CenterX=-16.28 CenterY=44.75 CenterZ=0 NormalX=0 NormalY=0 NormalZ=1 AngleXU=0 Radius=1.5 StartAngle=4.71239 EndAngle=7.85398
    g17: ArcOfCircle CenterX=-18.2337 CenterY=39 CenterZ=0 NormalX=0 NormalY=0 NormalZ=1 AngleXU=0 Radius=1.5 StartAngle=4.71485 EndAngle=7.85398
    g18: ArcOfCircle CenterX=-16.2837 CenterY=27.25 CenterZ=0 NormalX=0 NormalY=0 NormalZ=1 AngleXU=0 Radius=1.5 StartAngle=4.71485 EndAngle=7.85398
    g19: ArcOfCircle CenterX=-18.2337 CenterY=33 CenterZ=0 NormalX=0 NormalY=0 NormalZ=1 AngleXU=0 Radius=1.5 StartAngle=4.71485 EndAngle=7.85398
    g20: ArcOfCircle CenterX=-11.49 CenterY=21.5 CenterZ=0 NormalX=0 NormalY=0 NormalZ=1 AngleXU=0 Radius=1.5 StartAngle=4.71239 EndAngle=7.85398
    g21: ArcOfCircle CenterX=-1.5 CenterY=4.25 CenterZ=0 NormalX=0 NormalY=0 NormalZ=1 AngleXU=0 Radius=1.5 StartAngle=4.71239 EndAngle=7.85398
    g22: ArcOfCircle CenterX=-1.5 CenterY=10 CenterZ=0 NormalX=0 NormalY=0 NormalZ=1 AngleXU=0 Radius=1.5 StartAngle=4.71239 EndAngle=7.85398
    g23: ArcOfCircle CenterX=-1.5 CenterY=15.75 CenterZ=0 NormalX=0 NormalY=0 NormalZ=1 AngleXU=0 Radius=1.5 StartAngle=4.71239 EndAngle=7.85398
    g24: LineSegment StartX=-49.19 StartY=69.25 StartZ=0 EndX=-1.5 EndY=69.25 EndZ=0
    g25: LineSegment StartX=-49.19 StartY=66.25 StartZ=0 EndX=-1.5 EndY=66.25 EndZ=0
    g26: LineSegment StartX=-49.19 StartY=63.5 StartZ=0 EndX=-1.5 EndY=63.5 EndZ=0
    g27: LineSegment StartX=-49.19 StartY=60.5 StartZ=0 EndX=-1.5 EndY=60.5 EndZ=0
    g28: LineSegment StartX=-49.19 StartY=57.75 StartZ=0 EndX=-1.5 EndY=57.75 EndZ=0
    g29: LineSegment StartX=-49.19 StartY=54.75 StartZ=0 EndX=-1.5 EndY=54.75 EndZ=0
    g30: LineSegment StartX=-49.19 StartY=52 StartZ=0 EndX=-11.49 EndY=52 EndZ=0
    g31: LineSegment StartX=-49.19 StartY=49 StartZ=0 EndX=-11.49 EndY=49 EndZ=0
    g32: LineSegment StartX=-49.19 StartY=46.25 StartZ=0 EndX=-16.28 EndY=46.25 EndZ=0
    g33: LineSegment StartX=-49.19 StartY=43.25 StartZ=0 EndX=-16.28 EndY=43.25 EndZ=0
    g34: LineSegment StartX=-49.19 StartY=40.5 StartZ=0 EndX=-18.2337 EndY=40.5 EndZ=0
    g35: LineSegment StartX=-49.19 StartY=37.5 StartZ=0 EndX=-18.23 EndY=37.5 EndZ=0
    g36: LineSegment StartX=-49.19 StartY=34.5 StartZ=0 EndX=-18.2337 EndY=34.5 EndZ=0
    g37: LineSegment StartX=-49.19 StartY=31.5 StartZ=0 EndX=-18.23 EndY=31.5 EndZ=0
    g38: LineSegment StartX=-49.19 StartY=28.75 StartZ=0 EndX=-16.2837 EndY=28.75 EndZ=0
    g39: LineSegment StartX=-49.19 StartY=25.75 StartZ=0 EndX=-16.28 EndY=25.75 EndZ=0
    g40: LineSegment StartX=-49.19 StartY=23 StartZ=0 EndX=-11.49 EndY=23 EndZ=0
    g41: LineSegment StartX=-49.19 StartY=20 StartZ=0 EndX=-11.49 EndY=20 EndZ=0
    g42: LineSegment StartX=-49.19 StartY=17.25 StartZ=0 EndX=-1.5 EndY=17.25 EndZ=0
    g43: LineSegment StartX=-49.19 StartY=14.25 StartZ=0 EndX=-1.5 EndY=14.25 EndZ=0
    g44: LineSegment StartX=-49.19 StartY=11.5 StartZ=0 EndX=-1.5 EndY=11.5 EndZ=0
    g45: LineSegment StartX=-49.19 StartY=8.5 StartZ=0 EndX=-1.5 EndY=8.5 EndZ=0
    g46: LineSegment StartX=-49.19 StartY=5.75 StartZ=0 EndX=-1.5 EndY=5.75 EndZ=0
    g47: LineSegment StartX=-49.19 StartY=2.75 StartZ=0 EndX=-1.5 EndY=2.75 EndZ=0
  constraints (120):
    c: Vertical(g0)
    c: Distance(g0) = 3
    c: Block(g0)
    c: Vertical(g1)
    c: Distance(g1) = 3
    c: Vertical(g2)
    c: Equal(g0,g2) = 3
    c: Block(g2)
    c: Vertical(g3)
    c: Equal(g1,g3) = 3
    c: Vertical(g4)
    c: Equal(g0,g4) = 3
    c: Block(g4)
    c: Vertical(g5)
    c: Equal(g1,g5) = 3
    c: Vertical(g6)
    c: Equal(g0,g6) = 3
    c: Block(g6)
    c: Vertical(g7)
    c: Equal(g1,g7) = 3
    c: Vertical(g8)
    c: Equal(g0,g8) = 3
    c: Block(g8)
    c: Vertical(g9)
    c: Equal(g1,g9) = 3
    c: Vertical(g10)
    c: Equal(g0,g10) = 3
    c: Block(g10)
    c: Vertical(g11)
    c: Equal(g1,g11) = 3
    c: Block(g12)
    c: Block(g13)
    c: Block(g14)
    c: Block(g15)
    c: Block(g16)
    c: Block(g17)
    c: Block(g18)
    c: Block(g19)
    c: Block(g20)
    c: Block(g21)
    c: Block(g22)
    c: Block(g23)
    c: Block(g11)
    c: Block(g9)
    c: Block(g7)
    c: Block(g5)
    c: Block(g3)
    c: Block(g1)
    c: Coincident(g24,g0)
    c: Coincident(g24,g12)
    c: Horizontal(g24)
    c: Coincident(g25,g0)
    c: Coincident(g25,g12)
    c: Horizontal(g25)
    c: Coincident(g26,g1)
    c: Coincident(g26,g13)
    c: Horizontal(g26)
    c: Coincident(g27,g1)
    c: Coincident(g27,g13)
    c: Horizontal(g27)
    c: Coincident(g28,g2)
    c: Coincident(g28,g14)
    c: Horizontal(g28)
    c: Coincident(g29,g2)
    c: Coincident(g29,g14)
    c: Horizontal(g29)
    c: Coincident(g30,g3)
    c: Coincident(g30,g15)
    c: Horizontal(g30)
    c: Coincident(g31,g3)
    c: Coincident(g31,g15)
    c: Horizontal(g31)
    c: Coincident(g32,g4)
    c: Coincident(g32,g16)
    c: Horizontal(g32)
    c: Coincident(g33,g4)
    c: Coincident(g33,g16)
    c: Horizontal(g33)
    c: Coincident(g34,g5)
    c: Coincident(g34,g17)
    c: Horizontal(g34)
    c: Coincident(g35,g5)
    c: Coincident(g35,g17)
    c: Horizontal(g35)
    c: Coincident(g36,g6)
    c: Coincident(g36,g19)
    c: Horizontal(g36)
    c: Coincident(g37,g6)
    c: Coincident(g37,g19)
    c: Horizontal(g37)
    c: Coincident(g38,g7)
    c: Coincident(g38,g18)
    c: Horizontal(g38)
    c: Coincident(g39,g7)
    c: Coincident(g39,g18)
    c: Horizontal(g39)
    c: Coincident(g40,g8)
    c: Coincident(g40,g20)
    c: Horizontal(g40)
    c: Coincident(g41,g8)
    c: Coincident(g41,g20)
    c: Horizontal(g41)
    c: Coincident(g42,g9)
    c: Coincident(g42,g23)
    c: Horizontal(g42)
    c: Coincident(g43,g9)
    c: Coincident(g43,g23)
    c: Horizontal(g43)
    c: Coincident(g44,g10)
    c: Coincident(g44,g22)
    c: Horizontal(g44)
    c: Coincident(g45,g10)
    c: Coincident(g45,g22)
    c: Horizontal(g45)
    c: Coincident(g46,g11)
    c: Coincident(g46,g21)
    c: Horizontal(g46)
    c: Coincident(g47,g11)
    c: Coincident(g47,g21)
    c: Horizontal(g47)
FEATURE [Part::Extrusion] Extrude042
  Base = -> Sketch051
  Dir = (1,-2e-16,2e-16)
  DirMode = 2
  FaceMakerClass = Part::FaceMakerBullseye
  LengthFwd = 19
  LengthRev = 0
  Placement = pos=(-19,0,0) rot=(0,0,1;0rad)
  Solid = true
  Symmetric = false
FEATURE [Part::Fillet] Fillet035  label="removeToCreateVentalationHoles"
  Base = -> Extrude042
  Edges = <same value as first occurrence — deduplicated (x6 in doc)>
  Placement = pos=(7,0,0) rot=(0,0,1;0rad)
FEATURE [Part::Cut] Cut038  label="top017"
  Base = -> Cut033
  Tool = -> Fillet035
FEATURE [Sketcher::SketchObject] Sketch052  label="bottomSketch001"
  FullyConstrained = true
  sketch-geometry (45):
    g0: LineSegment StartX=6.29999 StartY=8 StartZ=0 EndX=3.29999 EndY=8 EndZ=0
    g1: LineSegment StartX=3.29999 StartY=8 StartZ=0 EndX=3.29999 EndY=-6.03275e-07 EndZ=0
    g2: ArcOfCircle CenterX=8.29999 CenterY=5 CenterZ=0 NormalX=0 NormalY=0 NormalZ=1 AngleXU=0 Radius=2 StartAngle=3.14159 EndAngle=4.71239
    g3: LineSegment StartX=6.29999 StartY=8 StartZ=0 EndX=6.29999 EndY=5 EndZ=0
    g4: ArcOfCircle CenterX=105 CenterY=19 CenterZ=0 NormalX=0 NormalY=0 NormalZ=1 AngleXU=0 Radius=12.7 StartAngle=4.71239 EndAngle=5.94289
    g5-g11: Circle x7 (B-spline internal-alignment scaffolding for g12; pole/knot coordinates omitted)
    g12: BSplineCurve PolesCount=7 KnotsCount=5 Degree=3 IsPeriodic=0
    g13-g17: GeomPoint x5 (B-spline internal-alignment scaffolding for g12; pole/knot coordinates omitted)
    g18: ArcOfCircle CenterX=105 CenterY=19 CenterZ=0 NormalX=0 NormalY=0 NormalZ=1 AngleXU=0 Radius=15.7 StartAngle=5.81226 EndAngle=6.28319
    g19: BSplineCurve PolesCount=5 KnotsCount=3 Degree=3 IsPeriodic=0
    g20: LineSegment StartX=8.29999 StartY=3 StartZ=0 EndX=101.7 EndY=3 EndZ=0
    g21: LineSegment StartX=3.29999 StartY=-6.03275e-07 StartZ=0 EndX=105 EndY=-6.03275e-07 EndZ=0
    g22: LineSegment StartX=120.974 StartY=8.71251 StartZ=0 EndX=122.332 EndY=7.83778 EndZ=0
    g23: LineSegment StartX=105 StartY=-6.03274e-07 StartZ=0 EndX=113 EndY=-6.03274e-07 EndZ=0
    g24: ArcOfCircle CenterX=105 CenterY=19 CenterZ=0 NormalX=0 NormalY=0 NormalZ=1 AngleXU=0 Radius=20.6155 StartAngle=5.11091 EndAngle=5.71103
    g25: ArcOfCircle CenterX=117.7 CenterY=19 CenterZ=0 NormalX=0 NormalY=0 NormalZ=1 AngleXU=0 Radius=3 StartAngle=1.2e-15 EndAngle=2.10468
    g26: Circle CenterX=116.345 CenterY=16.3232 CenterZ=0 NormalX=0 NormalY=0 NormalZ=1 AngleXU=0 Radius=1
    g27: Circle CenterX=117.24 CenterY=15.7584 CenterZ=0 NormalX=0 NormalY=0 NormalZ=1 AngleXU=0 Radius=1
    g28: Circle CenterX=116.972 CenterY=14.7612 CenterZ=0 NormalX=0 NormalY=0 NormalZ=1 AngleXU=0 Radius=1
    g29: BSplineCurve PolesCount=3 KnotsCount=2 Degree=2 IsPeriodic=0
    g30: GeomPoint X=116.345 Y=16.3232 Z=0
    g31: GeomPoint X=116.972 Y=14.7612 Z=0
    g32: Circle CenterX=115.828 CenterY=17.157 CenterZ=0 NormalX=0 NormalY=0 NormalZ=1 AngleXU=0 Radius=1
    g33: Circle CenterX=115.841 CenterY=16.639 CenterZ=0 NormalX=0 NormalY=0 NormalZ=1 AngleXU=0 Radius=1
    g34: Circle CenterX=116.345 CenterY=16.3232 CenterZ=0 NormalX=0 NormalY=0 NormalZ=1 AngleXU=0 Radius=1
    g35: BSplineCurve PolesCount=3 KnotsCount=2 Degree=2 IsPeriodic=0
    g36: GeomPoint X=115.828 Y=17.157 Z=0
    g37: GeomPoint X=116.345 Y=16.3232 Z=0
    g38: LineSegment StartX=115.828 StartY=17.157 StartZ=0 EndX=115.828 EndY=20.8307 EndZ=0
    g39: Circle CenterX=115.828 CenterY=20.8307 CenterZ=0 NormalX=0 NormalY=0 NormalZ=1 AngleXU=0 Radius=1
    g40: Circle CenterX=115.831 CenterY=21.3396 CenterZ=0 NormalX=0 NormalY=0 NormalZ=1 AngleXU=0 Radius=1
    g41: Circle CenterX=116.173 CenterY=21.5825 CenterZ=0 NormalX=0 NormalY=0 NormalZ=1 AngleXU=0 Radius=1
    g42: BSplineCurve PolesCount=3 KnotsCount=2 Degree=2 IsPeriodic=0
    g43: GeomPoint X=115.828 Y=20.8307 Z=0
    g44: GeomPoint X=116.173 Y=21.5825 Z=0
  constraints (70):
    c: Horizontal(g0)
    c: Distance(g0) = 3
    c: Coincident(g1,g0)
    c: Vertical(g1)
    c: Block(g2)
    c: Block(g0)
    c: Coincident(g3,g0)
    c: Coincident(g3,g2)
    c: Vertical(g3)
    c: Block(g1)
    c: Block(g4)
    c: Coincident(g19,g4)
    c: Block(g19)
    c: Equal(g5, g6-g11) x6
    c: InternalAlignment(g5-g11 -> g12) x7
    c: InternalAlignment(g13-g17 -> g12) x5
    c: Block(g12)
    c: Coincident(g18,g12)
    c: Block(g18)
    c: Coincident(g20,g2)
    c: Coincident(g20,g19)
    c: Horizontal(g20)
    c: Distance(g20) = 93.4
    c: Coincident(g21,g1)
    c: Horizontal(g21)
    c: Distance(g21) = 101.7
    c: Horizontal(g23)
    c: Distance(g23) = 8
    c: Coincident(g24,g23)
    c: Block(g23)
    c: Coincident(g22,g24)
    c: Block(g24)
    c: Block(g22)
    c: Distance(g22) = 1.61553
    c: Coincident(g25,g18)
    c: Block(g25)
    c: Weight(g26) = 1
    c: Equal(g26,g27)
    c: Equal(g26,g28)
    c: Coincident(g29,g4)
    c: InternalAlignment(g26,g29)
    c: InternalAlignment(g27,g29)
    c: InternalAlignment(g28,g29)
    c: InternalAlignment(g30,g29)
    c: InternalAlignment(g31,g29)
    c: Block(g29)
    c: Weight(g32) = 1
    c: Equal(g32,g33)
    c: Equal(g32,g34)
    c: Coincident(g35,g29)
    c: InternalAlignment(g32,g35)
    c: InternalAlignment(g33,g35)
    c: InternalAlignment(g34,g35)
    c: InternalAlignment(g36,g35)
    c: InternalAlignment(g37,g35)
    c: Block(g35)
    c: Coincident(g38,g35)
    c: Vertical(g38)
    c: Block(g38)
    c: Coincident(g42,g38)
    c: Weight(g39) = 1
    c: Equal(g39,g40)
    c: Equal(g39,g41)
    c: Coincident(g42,g25)
    c: InternalAlignment(g39,g42)
    c: InternalAlignment(g40,g42)
    c: InternalAlignment(g41,g42)
    c: InternalAlignment(g43,g42)
    c: InternalAlignment(g44,g42)
    c: Block(g42)
FEATURE [Part::Extrusion] Extrude043  label="bottom010"
  Base = -> Sketch052
  Dir = (0,0,1)
  DirMode = 2
  FaceMakerClass = Part::FaceMakerBullseye
  LengthFwd = 71.4
  LengthRev = 0
  Placement = pos=(0,0,0.3) rot=(0,0,1;0rad)
  Solid = true
  Symmetric = false
FEATURE [Sketcher::SketchObject] Sketch053  label="topSketch013"
  FullyConstrained = true
  sketch-geometry (22):
    g0: LineSegment StartX=5.21097e-06 StartY=3 StartZ=0 EndX=5.21097e-06 EndY=19 EndZ=0
    g1: ArcOfCircle CenterX=19 CenterY=19 CenterZ=0 NormalX=0 NormalY=0 NormalZ=1 AngleXU=0 Radius=19 StartAngle=1.5708 EndAngle=3.14159
    g2: ArcOfCircle CenterX=19 CenterY=19 CenterZ=0 NormalX=0 NormalY=0 NormalZ=1 AngleXU=0 Radius=16 StartAngle=1.5708 EndAngle=3.14159
    g3: LineSegment StartX=114 StartY=35 StartZ=0 EndX=19 EndY=35 EndZ=0
    g4: LineSegment StartX=5.21097e-06 StartY=3 StartZ=0 EndX=5.21097e-06 EndY=0 EndZ=0
    g5: LineSegment StartX=3 StartY=0 StartZ=0 EndX=5.21097e-06 EndY=0 EndZ=0
    g6: LineSegment StartX=3 StartY=19 StartZ=0 EndX=3 EndY=0 EndZ=0
    g7: LineSegment StartX=19 StartY=38 StartZ=0 EndX=124 EndY=38 EndZ=0
    g8: Circle CenterX=119 CenterY=35 CenterZ=0 NormalX=0 NormalY=0 NormalZ=1 AngleXU=0 Radius=1
    g9: Circle CenterX=121 CenterY=35 CenterZ=0 NormalX=0 NormalY=0 NormalZ=1 AngleXU=0 Radius=1
    g10: Circle CenterX=121 CenterY=33 CenterZ=0 NormalX=0 NormalY=0 NormalZ=1 AngleXU=0 Radius=1
    g11: BSplineCurve PolesCount=3 KnotsCount=2 Degree=2 IsPeriodic=0
    g12: GeomPoint X=119 Y=35 Z=0
    g13: GeomPoint X=121 Y=33 Z=0
    g14: LineSegment StartX=119 StartY=35 StartZ=0 EndX=114 EndY=35 EndZ=0
    g15: ArcOfCircle CenterX=105 CenterY=19 CenterZ=0 NormalX=0 NormalY=0 NormalZ=1 AngleXU=0 Radius=16 StartAngle=5.60905 EndAngle=6.28319
    g16: LineSegment StartX=121 StartY=33 StartZ=0 EndX=121 EndY=19 EndZ=0
    g17: LineSegment StartX=117.5 StartY=9.01251 StartZ=0 EndX=121.163 EndY=9.0125 EndZ=0
    g18: ArcOfCircle CenterX=105 CenterY=19 CenterZ=0 NormalX=0 NormalY=0 NormalZ=1 AngleXU=0 Radius=20.6155 StartAngle=5.7297 EndAngle=6.28319
    g19: LineSegment StartX=121.163 StartY=9.0125 StartZ=0 EndX=122.538 EndY=8.16329 EndZ=0
    g20: LineSegment StartX=124 StartY=38 StartZ=0 EndX=125.616 EndY=38 EndZ=0
    g21: LineSegment StartX=125.616 StartY=19 StartZ=0 EndX=125.616 EndY=38 EndZ=0
  constraints (50):
    c: Vertical(g0)
    c: Block(g0)
    c: Coincident(g1,g0)
    c: Block(g1)
    c: Coincident(g2,g1)
    c: Block(g2)
    c: Coincident(g3,g2)
    c: Horizontal(g3)
    c: Tangent(g3,g2)
    c: Coincident(g4,g0)
    c: Distance(g4) = 3
    c: Vertical(g4)
    c: Coincident(g5,g4)
    c: Horizontal(g5)
    c: Coincident(g6,g2)
    c: Coincident(g6,g5)
    c: Vertical(g6)
    c: Horizontal(g7)
    c: Distance(g7) = 105
    c: Coincident(g7,g1)
    c: Block(g3)
    c: Weight(g8) = 1
    c: Equal(g8,g9)
    c: Equal(g8,g10)
    c: InternalAlignment(g8,g11)
    c: InternalAlignment(g9,g11)
    c: InternalAlignment(g10,g11)
    c: InternalAlignment(g12,g11)
    c: InternalAlignment(g13,g11)
    c: Block(g11)
    c: Coincident(g14,g11)
    c: Coincident(g14,g3)
    c: Horizontal(g14)
    c: Block(g15)
    c: Coincident(g16,g11)
    c: Coincident(g16,g15)
    c: Vertical(g16)
    c: Distance(g16) = 14
    c: Coincident(g17,g15)
    c: Block(g18)
    c: Coincident(g19,g18)
    c: Coincident(g20,g7)
    c: Horizontal(g20)
    c: Vertical(g21)
    c: Coincident(g20,g21)
    c: Block(g20)
    c: Block(g21)
    c: Block(g19)
    c: Block(g17)
    c: Distance(g20) = 1.61553
FEATURE [Part::Extrusion] Extrude044
  Base = -> Sketch053
  Dir = (0,0,1)
  DirMode = 2
  FaceMakerClass = Part::FaceMakerBullseye
  LengthFwd = 72
  LengthRev = 0
  Solid = true
  Symmetric = false
FEATURE [Part::Fillet] Fillet036  label="top018"
  Base = -> Extrude044
  Edges = 1 edges r=2: [Edge41]
FEATURE [Sketcher::SketchObject] Sketch054
  FullyConstrained = false
  Placement = pos=(0,0,0) rot=(1,0,0;1.5708rad)
  sketch-geometry (24):
    g0: ArcOfCircle CenterX=-4 CenterY=-10.5 CenterZ=0 NormalX=0 NormalY=0 NormalZ=1 AngleXU=0 Radius=1.5 StartAngle=6e-16 EndAngle=3.14159
    g1: ArcOfCircle CenterX=-34.2 CenterY=-10.5 CenterZ=0 NormalX=0 NormalY=0 NormalZ=1 AngleXU=0 Radius=1.5 StartAngle=0 EndAngle=3.14159
    g2: ArcOfCircle CenterX=-34.2 CenterY=-27.7 CenterZ=0 NormalX=0 NormalY=0 NormalZ=1 AngleXU=0 Radius=1.5 StartAngle=3.14159 EndAngle=6.28319
    g3: ArcOfCircle CenterX=-4 CenterY=-27.7 CenterZ=0 NormalX=0 NormalY=0 NormalZ=1 AngleXU=0 Radius=1.5 StartAngle=3.1416 EndAngle=6.28319
    g4: ArcOfCircle CenterX=-10 CenterY=-4.3 CenterZ=0 NormalX=0 NormalY=0 NormalZ=1 AngleXU=0 Radius=1.5 StartAngle=2e-16 EndAngle=3.14159
    g5: ArcOfCircle CenterX=-16.1 CenterY=-1.8 CenterZ=0 NormalX=0 NormalY=0 NormalZ=1 AngleXU=0 Radius=1.5 StartAngle=5e-16 EndAngle=3.14159
    g6: ArcOfCircle CenterX=-22.1 CenterY=-1.8 CenterZ=0 NormalX=0 NormalY=0 NormalZ=1 AngleXU=0 Radius=1.5 StartAngle=5e-16 EndAngle=3.14159
    g7: ArcOfCircle CenterX=-28.2 CenterY=-4.3 CenterZ=0 NormalX=0 NormalY=0 NormalZ=1 AngleXU=0 Radius=1.5 StartAngle=2e-16 EndAngle=3.14159
    g8: ArcOfCircle CenterX=-10 CenterY=-33.9 CenterZ=0 NormalX=0 NormalY=0 NormalZ=1 AngleXU=0 Radius=1.5 StartAngle=3.14159 EndAngle=6.28319
    g9: ArcOfCircle CenterX=-16.1 CenterY=-36.4 CenterZ=0 NormalX=0 NormalY=0 NormalZ=1 AngleXU=0 Radius=1.5 StartAngle=3.14159 EndAngle=6.28319
    g10: ArcOfCircle CenterX=-22.1 CenterY=-36.4 CenterZ=0 NormalX=0 NormalY=0 NormalZ=1 AngleXU=0 Radius=1.5 StartAngle=3.14159 EndAngle=6.28319
    g11: ArcOfCircle CenterX=-28.2 CenterY=-33.9 CenterZ=0 NormalX=0 NormalY=0 NormalZ=1 AngleXU=0 Radius=1.5 StartAngle=3.14159 EndAngle=6.28319
    g12: LineSegment StartX=-35.7 StartY=-10.5 StartZ=0 EndX=-35.7 EndY=-27.7 EndZ=0
    g13: LineSegment StartX=-32.7 StartY=-10.5 StartZ=0 EndX=-32.7 EndY=-27.7 EndZ=0
    g14: LineSegment StartX=-29.7 StartY=-33.9 StartZ=0 EndX=-29.7 EndY=-4.3 EndZ=0
    g15: LineSegment StartX=-26.7 StartY=-33.9 StartZ=0 EndX=-26.7 EndY=-4.3 EndZ=0
    g16: LineSegment StartX=-2.5 StartY=-10.5 StartZ=0 EndX=-2.5 EndY=-27.7 EndZ=0
    g17: LineSegment StartX=-8.5 StartY=-4.3 StartZ=0 EndX=-8.5 EndY=-33.9 EndZ=0
    g18: LineSegment StartX=-5.5 StartY=-10.5 StartZ=0 EndX=-5.5 EndY=-27.7 EndZ=0
    g19: LineSegment StartX=-11.5 StartY=-4.3 StartZ=0 EndX=-11.5 EndY=-33.9 EndZ=0
    g20: LineSegment StartX=-14.6 StartY=-1.8 StartZ=0 EndX=-14.6 EndY=-36.4 EndZ=0
    g21: LineSegment StartX=-17.6 StartY=-1.8 StartZ=0 EndX=-17.6 EndY=-36.4 EndZ=0
    g22: LineSegment StartX=-20.6 StartY=-36.4 StartZ=0 EndX=-20.6 EndY=-1.8 EndZ=0
    g23: LineSegment StartX=-23.6 StartY=-1.8 StartZ=0 EndX=-23.6 EndY=-36.4 EndZ=0
  constraints (48):
    c: Block(g0)
    c: Block(g1)
    c: Block(g2)
    c: Block(g3)
    c: Block(g4)
    c: Block(g5)
    c: Block(g6)
    c: Block(g7)
    c: Block(g8)
    c: Block(g9)
    c: Block(g10)
    c: Block(g11)
    c: Coincident(g12,g1)
    c: Coincident(g12,g2)
    c: Vertical(g12)
    c: Coincident(g13,g1)
    c: Coincident(g13,g2)
    c: Vertical(g13)
    c: Coincident(g14,g11)
    c: Coincident(g14,g7)
    c: Vertical(g14)
    c: Coincident(g15,g11)
    c: Coincident(g15,g7)
    c: Vertical(g15)
    c: Coincident(g16,g0)
    c: Coincident(g16,g3)
    c: Vertical(g16)
    c: Coincident(g17,g4)
    c: Coincident(g17,g8)
    c: Vertical(g17)
    c: Coincident(g18,g0)
    c: Coincident(g18,g3)
    c: Vertical(g18)
    c: Coincident(g19,g4)
    c: Coincident(g19,g8)
    c: Vertical(g19)
    c: Coincident(g20,g5)
    c: Coincident(g20,g9)
    c: Vertical(g20)
    c: Coincident(g21,g5)
    c: Coincident(g21,g9)
    c: Vertical(g21)
    c: Coincident(g22,g10)
    c: Coincident(g22,g6)
    c: Vertical(g22)
    c: Coincident(g23,g6)
    c: Coincident(g23,g10)
    c: Vertical(g23)
FEATURE [Part::Extrusion] Extrude045  label="removeToCreateFanGrillHoles003"
  Base = -> Sketch054
  Dir = (0,-1,6e-16)
  DirMode = 2
  FaceMakerClass = Part::FaceMakerBullseye
  LengthFwd = 10
  LengthRev = 0
  Placement = pos=(65.4,44,54.82) rot=(0,0,1;0rad)
  Solid = true
  Symmetric = false
FEATURE [Part::Feature] Face105 .. Face108  x4 (patterned run collapsed; names and placements below)
  shape: bbox 3.5 x 17.8 x 2e-07 mm, 1 faces, 0 solids (baked)
FEATURE [Part::Revolution] Revolve113  label="removeToCreateScrewAndThreadedInsertHole041"
  Angle = 360
  Axis = (0,1,0)
  Base = (0,0,0)
  FaceMakerClass = Part::FaceMakerBullseye
  Placement = pos=(62.3,30.3,19.7) rot=(0,0,1;0rad)
  Solid = false
  Source = -> Face105
  Symmetric = false
FEATURE [Part::Revolution] Revolve114  label="removeToCreateScrewAndThreadedInsertHole042"
  Angle = 360
  Axis = (0,1,0)
  Base = (0,0,0)
  FaceMakerClass = Part::FaceMakerBullseye
  Placement = pos=(62.3,30.3,51.7) rot=(0,0,1;0rad)
  Solid = false
  Source = -> Face106
  Symmetric = false
FEATURE [Part::Revolution] Revolve115  label="removeToCreateScrewAndThreadedInsertHole043"
  Angle = 360
  Axis = (0,1,0)
  Base = (0,0,0)
  FaceMakerClass = Part::FaceMakerBullseye
  Placement = pos=(30.3,30.3,19.7) rot=(0,0,1;0rad)
  Solid = false
  Source = -> Face107
  Symmetric = false
FEATURE [Part::Revolution] Revolve116  label="removeToCreateScrewAndThreadedInsertHole044"
  Angle = 360
  Axis = (0,1,0)
  Base = (0,0,0)
  FaceMakerClass = Part::FaceMakerBullseye
  Placement = pos=(30.3,30.3,51.7) rot=(0,0,1;0rad)
  Solid = false
  Source = -> Face108
  Symmetric = false
FEATURE [Part::MultiFuse] Fusion083  label="createThreadedInsertHolesForFan004"
  Shapes = -> [Revolve113,Revolve114,Revolve115,Revolve116]
FEATURE [Part::Box] Box024  label="removeToCreteHoleForPlugHousing026"
  AttacherType = Attacher::AttachEngine3D
  Height = 28.6
  Length = 10
  Placement = pos=(-2,0,21.7) rot=(0,0,1;0rad)
  Width = 19
FEATURE [Part::Cylinder] Cylinder038  label="removeToCreteHoleForPlugHousing027"
  Angle = 360
  AttacherType = Attacher::AttachEngine3D
  Height = 20
  Placement = pos=(-2,19,36) rot=(0,1,0;1.5708rad)
  Radius = 14.3
FEATURE [Part::MultiFuse] Fusion084  label="removeToCreteHoleForPlugHousing028"
  Shapes = -> [Box024,Cylinder038]
FEATURE [Part::Cylinder] Cylinder039
  Angle = 360
  AttacherType = Attacher::AttachEngine3D
  Height = 20
  Placement = pos=(0,0,36.15) rot=(0,0,1;0rad)
  Radius = 14.3
FEATURE [Part::Cylinder] Cylinder040
  Angle = 360
  AttacherType = Attacher::AttachEngine3D
  Height = 10
  Placement = pos=(0,0,36.15) rot=(0,0,1;0rad)
  Radius = 4
FEATURE [Part::Box] Box025  label="removeToCreteHoleForPlugHousing030"
  AttacherType = Attacher::AttachEngine3D
  Height = 28.6
  Length = 20
  Placement = pos=(106.15,0,21.7) rot=(0,0,1;0rad)
  Width = 19
FEATURE [Part::MultiFuse] Fusion086  label="removeToCreteHoleForPlugHousing031"
  Placement = pos=(70,19,36) rot=(0,1,0;1.5708rad)
  Shapes = -> [Cylinder039,Cylinder040]
FEATURE [Part::MultiFuse] Fusion085  label="removeToCreteHoleForPlugHousing029"
  Shapes = -> [Box025,Fusion086]
FEATURE [Sketcher::SketchObject] Sketch055
  FullyConstrained = true
  Placement = pos=(117,19,0) rot=(0.57735,0.57735,0.57735;2.0944rad)
  sketch-geometry (48):
    g0: LineSegment StartX=-49.19 StartY=69.25 StartZ=0 EndX=-49.19 EndY=66.25 EndZ=0
    g1: LineSegment StartX=-49.19 StartY=63.5 StartZ=0 EndX=-49.19 EndY=60.5 EndZ=0
    g2: LineSegment StartX=-49.19 StartY=57.75 StartZ=0 EndX=-49.19 EndY=54.75 EndZ=0
    g3: LineSegment StartX=-49.19 StartY=52 StartZ=0 EndX=-49.19 EndY=49 EndZ=0
    g4: LineSegment StartX=-49.19 StartY=46.25 StartZ=0 EndX=-49.19 EndY=43.25 EndZ=0
    g5: LineSegment StartX=-49.19 StartY=40.5 StartZ=0 EndX=-49.19 EndY=37.5 EndZ=0
    g6: LineSegment StartX=-49.19 StartY=34.5 StartZ=0 EndX=-49.19 EndY=31.5 EndZ=0
    g7: LineSegment StartX=-49.19 StartY=28.75 StartZ=0 EndX=-49.19 EndY=25.75 EndZ=0
    g8: LineSegment StartX=-49.19 StartY=23 StartZ=0 EndX=-49.19 EndY=20 EndZ=0
    g9: LineSegment StartX=-49.19 StartY=17.25 StartZ=0 EndX=-49.19 EndY=14.25 EndZ=0
    g10: LineSegment StartX=-49.19 StartY=11.5 StartZ=0 EndX=-49.19 EndY=8.5 EndZ=0
    g11: LineSegment StartX=-49.19 StartY=5.75 StartZ=0 EndX=-49.19 EndY=2.75 EndZ=0
    g12: ArcOfCircle CenterX=-1.5 CenterY=67.75 CenterZ=0 NormalX=0 NormalY=0 NormalZ=1 AngleXU=0 Radius=1.5 StartAngle=4.71239 EndAngle=7.85398
    g13: ArcOfCircle CenterX=-1.5 CenterY=62 CenterZ=0 NormalX=0 NormalY=0 NormalZ=1 AngleXU=0 Radius=1.5 StartAngle=4.71239 EndAngle=7.85398
    g14: ArcOfCircle CenterX=-1.5 CenterY=56.25 CenterZ=0 NormalX=0 NormalY=0 NormalZ=1 AngleXU=0 Radius=1.5 StartAngle=4.71239 EndAngle=7.85398
    g15: ArcOfCircle CenterX=-11.49 CenterY=50.5 CenterZ=0 NormalX=0 NormalY=0 NormalZ=1 AngleXU=0 Radius=1.5 StartAngle=4.71239 EndAngle=7.85398
    g16: ArcOfCircle CenterX=-16.28 CenterY=44.75 CenterZ=0 NormalX=0 NormalY=0 NormalZ=1 AngleXU=0 Radius=1.5 StartAngle=4.71239 EndAngle=7.85398
    g17: ArcOfCircle CenterX=-18.2337 CenterY=39 CenterZ=0 NormalX=0 NormalY=0 NormalZ=1 AngleXU=0 Radius=1.5 StartAngle=4.71485 EndAngle=7.85398
    g18: ArcOfCircle CenterX=-16.2837 CenterY=27.25 CenterZ=0 NormalX=0 NormalY=0 NormalZ=1 AngleXU=0 Radius=1.5 StartAngle=4.71485 EndAngle=7.85398
    g19: ArcOfCircle CenterX=-18.2337 CenterY=33 CenterZ=0 NormalX=0 NormalY=0 NormalZ=1 AngleXU=0 Radius=1.5 StartAngle=4.71485 EndAngle=7.85398
    g20: ArcOfCircle CenterX=-11.49 CenterY=21.5 CenterZ=0 NormalX=0 NormalY=0 NormalZ=1 AngleXU=0 Radius=1.5 StartAngle=4.71239 EndAngle=7.85398
    g21: ArcOfCircle CenterX=-1.5 CenterY=4.25 CenterZ=0 NormalX=0 NormalY=0 NormalZ=1 AngleXU=0 Radius=1.5 StartAngle=4.71239 EndAngle=7.85398
    g22: ArcOfCircle CenterX=-1.5 CenterY=10 CenterZ=0 NormalX=0 NormalY=0 NormalZ=1 AngleXU=0 Radius=1.5 StartAngle=4.71239 EndAngle=7.85398
    g23: ArcOfCircle CenterX=-1.5 CenterY=15.75 CenterZ=0 NormalX=0 NormalY=0 NormalZ=1 AngleXU=0 Radius=1.5 StartAngle=4.71239 EndAngle=7.85398
    g24: LineSegment StartX=-49.19 StartY=69.25 StartZ=0 EndX=-1.5 EndY=69.25 EndZ=0
    g25: LineSegment StartX=-49.19 StartY=66.25 StartZ=0 EndX=-1.5 EndY=66.25 EndZ=0
    g26: LineSegment StartX=-49.19 StartY=63.5 StartZ=0 EndX=-1.5 EndY=63.5 EndZ=0
    g27: LineSegment StartX=-49.19 StartY=60.5 StartZ=0 EndX=-1.5 EndY=60.5 EndZ=0
    g28: LineSegment StartX=-49.19 StartY=57.75 StartZ=0 EndX=-1.5 EndY=57.75 EndZ=0
    g29: LineSegment StartX=-49.19 StartY=54.75 StartZ=0 EndX=-1.5 EndY=54.75 EndZ=0
    g30: LineSegment StartX=-49.19 StartY=52 StartZ=0 EndX=-11.49 EndY=52 EndZ=0
    g31: LineSegment StartX=-49.19 StartY=49 StartZ=0 EndX=-11.49 EndY=49 EndZ=0
    g32: LineSegment StartX=-49.19 StartY=46.25 StartZ=0 EndX=-16.28 EndY=46.25 EndZ=0
    g33: LineSegment StartX=-49.19 StartY=43.25 StartZ=0 EndX=-16.28 EndY=43.25 EndZ=0
    g34: LineSegment StartX=-49.19 StartY=40.5 StartZ=0 EndX=-18.2337 EndY=40.5 EndZ=0
    g35: LineSegment StartX=-49.19 StartY=37.5 StartZ=0 EndX=-18.23 EndY=37.5 EndZ=0
    g36: LineSegment StartX=-49.19 StartY=34.5 StartZ=0 EndX=-18.2337 EndY=34.5 EndZ=0
    g37: LineSegment StartX=-49.19 StartY=31.5 StartZ=0 EndX=-18.23 EndY=31.5 EndZ=0
    g38: LineSegment StartX=-49.19 StartY=28.75 StartZ=0 EndX=-16.2837 EndY=28.75 EndZ=0
    g39: LineSegment StartX=-49.19 StartY=25.75 StartZ=0 EndX=-16.28 EndY=25.75 EndZ=0
    g40: LineSegment StartX=-49.19 StartY=23 StartZ=0 EndX=-11.49 EndY=23 EndZ=0
    g41: LineSegment StartX=-49.19 StartY=20 StartZ=0 EndX=-11.49 EndY=20 EndZ=0
    g42: LineSegment StartX=-49.19 StartY=17.25 StartZ=0 EndX=-1.5 EndY=17.25 EndZ=0
    g43: LineSegment StartX=-49.19 StartY=14.25 StartZ=0 EndX=-1.5 EndY=14.25 EndZ=0
    g44: LineSegment StartX=-49.19 StartY=11.5 StartZ=0 EndX=-1.5 EndY=11.5 EndZ=0
    g45: LineSegment StartX=-49.19 StartY=8.5 StartZ=0 EndX=-1.5 EndY=8.5 EndZ=0
    g46: LineSegment StartX=-49.19 StartY=5.75 StartZ=0 EndX=-1.5 EndY=5.75 EndZ=0
    g47: LineSegment StartX=-49.19 StartY=2.75 StartZ=0 EndX=-1.5 EndY=2.75 EndZ=0
  constraints (120):
    c: Vertical(g0)
    c: Distance(g0) = 3
    c: Block(g0)
    c: Vertical(g1)
    c: Distance(g1) = 3
    c: Vertical(g2)
    c: Equal(g0,g2) = 3
    c: Block(g2)
    c: Vertical(g3)
    c: Equal(g1,g3) = 3
    c: Vertical(g4)
    c: Equal(g0,g4) = 3
    c: Block(g4)
    c: Vertical(g5)
    c: Equal(g1,g5) = 3
    c: Vertical(g6)
    c: Equal(g0,g6) = 3
    c: Block(g6)
    c: Vertical(g7)
    c: Equal(g1,g7) = 3
    c: Vertical(g8)
    c: Equal(g0,g8) = 3
    c: Block(g8)
    c: Vertical(g9)
    c: Equal(g1,g9) = 3
    c: Vertical(g10)
    c: Equal(g0,g10) = 3
    c: Block(g10)
    c: Vertical(g11)
    c: Equal(g1,g11) = 3
    c: Block(g12)
    c: Block(g13)
    c: Block(g14)
    c: Block(g15)
    c: Block(g16)
    c: Block(g17)
    c: Block(g18)
    c: Block(g19)
    c: Block(g20)
    c: Block(g21)
    c: Block(g22)
    c: Block(g23)
    c: Block(g11)
    c: Block(g9)
    c: Block(g7)
    c: Block(g5)
    c: Block(g3)
    c: Block(g1)
    c: Coincident(g24,g0)
    c: Coincident(g24,g12)
    c: Horizontal(g24)
    c: Coincident(g25,g0)
    c: Coincident(g25,g12)
    c: Horizontal(g25)
    c: Coincident(g26,g1)
    c: Coincident(g26,g13)
    c: Horizontal(g26)
    c: Coincident(g27,g1)
    c: Coincident(g27,g13)
    c: Horizontal(g27)
    c: Coincident(g28,g2)
    c: Coincident(g28,g14)
    c: Horizontal(g28)
    c: Coincident(g29,g2)
    c: Coincident(g29,g14)
    c: Horizontal(g29)
    c: Coincident(g30,g3)
    c: Coincident(g30,g15)
    c: Horizontal(g30)
    c: Coincident(g31,g3)
    c: Coincident(g31,g15)
    c: Horizontal(g31)
    c: Coincident(g32,g4)
    c: Coincident(g32,g16)
    c: Horizontal(g32)
    c: Coincident(g33,g4)
    c: Coincident(g33,g16)
    c: Horizontal(g33)
    c: Coincident(g34,g5)
    c: Coincident(g34,g17)
    c: Horizontal(g34)
    c: Coincident(g35,g5)
    c: Coincident(g35,g17)
    c: Horizontal(g35)
    c: Coincident(g36,g6)
    c: Coincident(g36,g19)
    c: Horizontal(g36)
    c: Coincident(g37,g6)
    c: Coincident(g37,g19)
    c: Horizontal(g37)
    c: Coincident(g38,g7)
    c: Coincident(g38,g18)
    c: Horizontal(g38)
    c: Coincident(g39,g7)
    c: Coincident(g39,g18)
    c: Horizontal(g39)
    c: Coincident(g40,g8)
    c: Coincident(g40,g20)
    c: Horizontal(g40)
    c: Coincident(g41,g8)
    c: Coincident(g41,g20)
    c: Horizontal(g41)
    c: Coincident(g42,g9)
    c: Coincident(g42,g23)
    c: Horizontal(g42)
    c: Coincident(g43,g9)
    c: Coincident(g43,g23)
    c: Horizontal(g43)
    c: Coincident(g44,g10)
    c: Coincident(g44,g22)
    c: Horizontal(g44)
    c: Coincident(g45,g10)
    c: Coincident(g45,g22)
    c: Horizontal(g45)
    c: Coincident(g46,g11)
    c: Coincident(g46,g21)
    c: Horizontal(g46)
    c: Coincident(g47,g11)
    c: Coincident(g47,g21)
    c: Horizontal(g47)
FEATURE [Part::Extrusion] Extrude046
  Base = -> Sketch055
  Dir = (1,0,0)
  DirMode = 2
  FaceMakerClass = Part::FaceMakerBullseye
  LengthFwd = 23
  LengthRev = 0
  Placement = pos=(-19,0,0) rot=(0,0,1;0rad)
  Solid = true
  Symmetric = false
FEATURE [Part::Fillet] Fillet038  label="removeToCreateVentalationHoles001"
  Base = -> Extrude046
  Edges = <same value as first occurrence — deduplicated (x6 in doc)>
  Placement = pos=(7,0,0) rot=(0,0,1;0rad)
FEATURE [Sketcher::SketchObject] Sketch056  label="topSketch014"
  FullyConstrained = true
  sketch-geometry (22):
    g0: LineSegment StartX=5.21097e-06 StartY=3 StartZ=0 EndX=5.21097e-06 EndY=19 EndZ=0
    g1: ArcOfCircle CenterX=19 CenterY=19 CenterZ=0 NormalX=0 NormalY=0 NormalZ=1 AngleXU=0 Radius=19 StartAngle=1.5708 EndAngle=3.14159
    g2: ArcOfCircle CenterX=19 CenterY=19 CenterZ=0 NormalX=0 NormalY=0 NormalZ=1 AngleXU=0 Radius=16 StartAngle=1.5708 EndAngle=3.14159
    g3: LineSegment StartX=114 StartY=35 StartZ=0 EndX=19 EndY=35 EndZ=0
    g4: LineSegment StartX=5.21097e-06 StartY=3 StartZ=0 EndX=5.21097e-06 EndY=0 EndZ=0
    g5: LineSegment StartX=3 StartY=0 StartZ=0 EndX=5.21097e-06 EndY=0 EndZ=0
    g6: LineSegment StartX=3 StartY=19 StartZ=0 EndX=3 EndY=0 EndZ=0
    g7: LineSegment StartX=19 StartY=38 StartZ=0 EndX=124 EndY=38 EndZ=0
    g8: Circle CenterX=119 CenterY=35 CenterZ=0 NormalX=0 NormalY=0 NormalZ=1 AngleXU=0 Radius=1
    g9: Circle CenterX=121 CenterY=35 CenterZ=0 NormalX=0 NormalY=0 NormalZ=1 AngleXU=0 Radius=1
    g10: Circle CenterX=121 CenterY=33 CenterZ=0 NormalX=0 NormalY=0 NormalZ=1 AngleXU=0 Radius=1
    g11: BSplineCurve PolesCount=3 KnotsCount=2 Degree=2 IsPeriodic=0
    g12: GeomPoint X=119 Y=35 Z=0
    g13: GeomPoint X=121 Y=33 Z=0
    g14: LineSegment StartX=119 StartY=35 StartZ=0 EndX=114 EndY=35 EndZ=0
    g15: ArcOfCircle CenterX=105 CenterY=19 CenterZ=0 NormalX=0 NormalY=0 NormalZ=1 AngleXU=0 Radius=16 StartAngle=5.60905 EndAngle=6.28319
    g16: LineSegment StartX=121 StartY=33 StartZ=0 EndX=121 EndY=19 EndZ=0
    g17: LineSegment StartX=117.5 StartY=9.01251 StartZ=0 EndX=121.163 EndY=9.0125 EndZ=0
    g18: ArcOfCircle CenterX=105 CenterY=19 CenterZ=0 NormalX=0 NormalY=0 NormalZ=1 AngleXU=0 Radius=20.6155 StartAngle=5.7297 EndAngle=6.28319
    g19: LineSegment StartX=121.163 StartY=9.0125 StartZ=0 EndX=122.538 EndY=8.16329 EndZ=0
    g20: LineSegment StartX=124 StartY=38 StartZ=0 EndX=125.616 EndY=38 EndZ=0
    g21: LineSegment StartX=125.616 StartY=19 StartZ=0 EndX=125.616 EndY=38 EndZ=0
  constraints (49):
    c: Vertical(g0)
    c: Block(g0)
    c: Coincident(g1,g0)
    c: Block(g1)
    c: Coincident(g2,g1)
    c: Block(g2)
    c: Coincident(g3,g2)
    c: Horizontal(g3)
    c: Tangent(g3,g2)
    c: Coincident(g4,g0)
    c: Distance(g4) = 3
    c: Vertical(g4)
    c: Coincident(g5,g4)
    c: Horizontal(g5)
    c: Coincident(g6,g2)
    c: Coincident(g6,g5)
    c: Vertical(g6)
    c: Horizontal(g7)
    c: Distance(g7) = 105
    c: Coincident(g7,g1)
    c: Block(g3)
    c: Weight(g8) = 1
    c: Equal(g8,g9)
    c: Equal(g8,g10)
    c: InternalAlignment(g8,g11)
    c: InternalAlignment(g9,g11)
    c: InternalAlignment(g10,g11)
    c: InternalAlignment(g12,g11)
    c: InternalAlignment(g13,g11)
    c: Block(g11)
    c: Coincident(g14,g11)
    c: Coincident(g14,g3)
    c: Horizontal(g14)
    c: Block(g15)
    c: Coincident(g16,g11)
    c: Coincident(g16,g15)
    c: Vertical(g16)
    c: Distance(g16) = 14
    c: Coincident(g17,g15)
    c: Block(g18)
    c: Coincident(g19,g18)
    c: Coincident(g20,g7)
    c: Horizontal(g20)
    c: Vertical(g21)
    c: Coincident(g20,g21)
    c: Block(g20)
    c: Block(g21)
    c: Block(g19)
    c: Block(g17)
FEATURE [Part::Box] Box026  label="removeToCreteHoleForPlugHousing032"
  AttacherType = Attacher::AttachEngine3D
  Height = 28.6
  Length = 10
  Placement = pos=(-2,0,21.7) rot=(0,0,1;0rad)
  Width = 19
FEATURE [Part::Feature] Face109 .. Face112  x4 (patterned run collapsed; names and placements below)
  shape: bbox 3.5 x 17.8 x 2e-07 mm, 1 faces, 0 solids (baked)
FEATURE [Part::Revolution] Revolve117  label="removeToCreateScrewAndThreadedInsertHole045"
  Angle = 360
  Axis = (0,1,0)
  Base = (0,0,0)
  FaceMakerClass = Part::FaceMakerBullseye
  Placement = pos=(62.3,30.3,19.7) rot=(0,0,1;0rad)
  Solid = false
  Source = -> Face109
  Symmetric = false
FEATURE [Part::Revolution] Revolve118  label="removeToCreateScrewAndThreadedInsertHole046"
  Angle = 360
  Axis = (0,1,0)
  Base = (0,0,0)
  FaceMakerClass = Part::FaceMakerBullseye
  Placement = pos=(62.3,30.3,51.7) rot=(0,0,1;0rad)
  Solid = false
  Source = -> Face110
  Symmetric = false
FEATURE [Part::Revolution] Revolve119  label="removeToCreateScrewAndThreadedInsertHole047"
  Angle = 360
  Axis = (0,1,0)
  Base = (0,0,0)
  FaceMakerClass = Part::FaceMakerBullseye
  Placement = pos=(30.3,30.3,19.7) rot=(0,0,1;0rad)
  Solid = false
  Source = -> Face111
  Symmetric = false
FEATURE [Part::Revolution] Revolve120  label="removeToCreateScrewAndThreadedInsertHole048"
  Angle = 360
  Axis = (0,1,0)
  Base = (0,0,0)
  FaceMakerClass = Part::FaceMakerBullseye
  Placement = pos=(30.3,30.3,51.7) rot=(0,0,1;0rad)
  Solid = false
  Source = -> Face112
  Symmetric = false
FEATURE [Part::MultiFuse] Fusion087  label="createThreadedInsertHolesForFan005"
  Shapes = -> [Revolve117,Revolve118,Revolve119,Revolve120]
FEATURE [Part::Extrusion] Extrude047
  Base = -> Sketch056
  Dir = (0,0,1)
  DirMode = 2
  FaceMakerClass = Part::FaceMakerBullseye
  LengthFwd = 72
  LengthRev = 0
  Solid = true
  Symmetric = false
FEATURE [Part::Fillet] Fillet039  label="top019"
  Base = -> Extrude047
  Edges = 1 edges r=2: [Edge35]
FEATURE [Sketcher::SketchObject] Sketch057
  FullyConstrained = false
  Placement = pos=(0,0,0) rot=(1,0,0;1.5708rad)
  sketch-geometry (24):
    g0: ArcOfCircle CenterX=-4 CenterY=-10.5 CenterZ=0 NormalX=0 NormalY=0 NormalZ=1 AngleXU=0 Radius=1.5 StartAngle=6e-16 EndAngle=3.14159
    g1: ArcOfCircle CenterX=-34.2 CenterY=-10.5 CenterZ=0 NormalX=0 NormalY=0 NormalZ=1 AngleXU=0 Radius=1.5 StartAngle=0 EndAngle=3.14159
    g2: ArcOfCircle CenterX=-34.2 CenterY=-27.7 CenterZ=0 NormalX=0 NormalY=0 NormalZ=1 AngleXU=0 Radius=1.5 StartAngle=3.14159 EndAngle=6.28319
    g3: ArcOfCircle CenterX=-4 CenterY=-27.7 CenterZ=0 NormalX=0 NormalY=0 NormalZ=1 AngleXU=0 Radius=1.5 StartAngle=3.1416 EndAngle=6.28319
    g4: ArcOfCircle CenterX=-10 CenterY=-4.3 CenterZ=0 NormalX=0 NormalY=0 NormalZ=1 AngleXU=0 Radius=1.5 StartAngle=2e-16 EndAngle=3.14159
    g5: ArcOfCircle CenterX=-16.1 CenterY=-1.8 CenterZ=0 NormalX=0 NormalY=0 NormalZ=1 AngleXU=0 Radius=1.5 StartAngle=5e-16 EndAngle=3.14159
    g6: ArcOfCircle CenterX=-22.1 CenterY=-1.8 CenterZ=0 NormalX=0 NormalY=0 NormalZ=1 AngleXU=0 Radius=1.5 StartAngle=5e-16 EndAngle=3.14159
    g7: ArcOfCircle CenterX=-28.2 CenterY=-4.3 CenterZ=0 NormalX=0 NormalY=0 NormalZ=1 AngleXU=0 Radius=1.5 StartAngle=2e-16 EndAngle=3.14159
    g8: ArcOfCircle CenterX=-10 CenterY=-33.9 CenterZ=0 NormalX=0 NormalY=0 NormalZ=1 AngleXU=0 Radius=1.5 StartAngle=3.14159 EndAngle=6.28319
    g9: ArcOfCircle CenterX=-16.1 CenterY=-36.4 CenterZ=0 NormalX=0 NormalY=0 NormalZ=1 AngleXU=0 Radius=1.5 StartAngle=3.14159 EndAngle=6.28319
    g10: ArcOfCircle CenterX=-22.1 CenterY=-36.4 CenterZ=0 NormalX=0 NormalY=0 NormalZ=1 AngleXU=0 Radius=1.5 StartAngle=3.14159 EndAngle=6.28319
    g11: ArcOfCircle CenterX=-28.2 CenterY=-33.9 CenterZ=0 NormalX=0 NormalY=0 NormalZ=1 AngleXU=0 Radius=1.5 StartAngle=3.14159 EndAngle=6.28319
    g12: LineSegment StartX=-35.7 StartY=-10.5 StartZ=0 EndX=-35.7 EndY=-27.7 EndZ=0
    g13: LineSegment StartX=-32.7 StartY=-10.5 StartZ=0 EndX=-32.7 EndY=-27.7 EndZ=0
    g14: LineSegment StartX=-29.7 StartY=-33.9 StartZ=0 EndX=-29.7 EndY=-4.3 EndZ=0
    g15: LineSegment StartX=-26.7 StartY=-33.9 StartZ=0 EndX=-26.7 EndY=-4.3 EndZ=0
    g16: LineSegment StartX=-2.5 StartY=-10.5 StartZ=0 EndX=-2.5 EndY=-27.7 EndZ=0
    g17: LineSegment StartX=-8.5 StartY=-4.3 StartZ=0 EndX=-8.5 EndY=-33.9 EndZ=0
    g18: LineSegment StartX=-5.5 StartY=-10.5 StartZ=0 EndX=-5.5 EndY=-27.7 EndZ=0
    g19: LineSegment StartX=-11.5 StartY=-4.3 StartZ=0 EndX=-11.5 EndY=-33.9 EndZ=0
    g20: LineSegment StartX=-14.6 StartY=-1.8 StartZ=0 EndX=-14.6 EndY=-36.4 EndZ=0
    g21: LineSegment StartX=-17.6 StartY=-1.8 StartZ=0 EndX=-17.6 EndY=-36.4 EndZ=0
    g22: LineSegment StartX=-20.6 StartY=-36.4 StartZ=0 EndX=-20.6 EndY=-1.8 EndZ=0
    g23: LineSegment StartX=-23.6 StartY=-1.8 StartZ=0 EndX=-23.6 EndY=-36.4 EndZ=0
  constraints (48):
    c: Block(g0)
    c: Block(g1)
    c: Block(g2)
    c: Block(g3)
    c: Block(g4)
    c: Block(g5)
    c: Block(g6)
    c: Block(g7)
    c: Block(g8)
    c: Block(g9)
    c: Block(g10)
    c: Block(g11)
    c: Coincident(g12,g1)
    c: Coincident(g12,g2)
    c: Vertical(g12)
    c: Coincident(g13,g1)
    c: Coincident(g13,g2)
    c: Vertical(g13)
    c: Coincident(g14,g11)
    c: Coincident(g14,g7)
    c: Vertical(g14)
    c: Coincident(g15,g11)
    c: Coincident(g15,g7)
    c: Vertical(g15)
    c: Coincident(g16,g0)
    c: Coincident(g16,g3)
    c: Vertical(g16)
    c: Coincident(g17,g4)
    c: Coincident(g17,g8)
    c: Vertical(g17)
    c: Coincident(g18,g0)
    c: Coincident(g18,g3)
    c: Vertical(g18)
    c: Coincident(g19,g4)
    c: Coincident(g19,g8)
    c: Vertical(g19)
    c: Coincident(g20,g5)
    c: Coincident(g20,g9)
    c: Vertical(g20)
    c: Coincident(g21,g5)
    c: Coincident(g21,g9)
    c: Vertical(g21)
    c: Coincident(g22,g10)
    c: Coincident(g22,g6)
    c: Vertical(g22)
    c: Coincident(g23,g6)
    c: Coincident(g23,g10)
    c: Vertical(g23)
FEATURE [Part::Extrusion] Extrude048  label="removeToCreateFanGrillHoles004"
  Base = -> Sketch057
  Dir = (0,-1,6e-16)
  DirMode = 2
  FaceMakerClass = Part::FaceMakerBullseye
  LengthFwd = 10
  LengthRev = 0
  Placement = pos=(65.4,44,54.82) rot=(0,0,1;0rad)
  Solid = true
  Symmetric = false
FEATURE [Part::Cut] Cut040  label="top021"
  Base = -> Fillet039
  Tool = -> Extrude048
FEATURE [Part::Cylinder] Cylinder041  label="removeToCreteHoleForPlugHousing034"
  Angle = 360
  AttacherType = Attacher::AttachEngine3D
  Height = 20
  Placement = pos=(-2,19,36) rot=(0,1,0;1.5708rad)
  Radius = 14.3
FEATURE [Part::MultiFuse] Fusion089  label="removeToCreteHoleForPlugHousing035"
  Shapes = -> [Box026,Cylinder041]
FEATURE [Part::Cylinder] Cylinder042
  Angle = 360
  AttacherType = Attacher::AttachEngine3D
  Height = 20
  Placement = pos=(0,0,36.15) rot=(0,0,1;0rad)
  Radius = 14.3
FEATURE [Part::Cylinder] Cylinder043
  Angle = 360
  AttacherType = Attacher::AttachEngine3D
  Height = 10
  Placement = pos=(0,0,36.15) rot=(0,0,1;0rad)
  Radius = 4
FEATURE [Part::Box] Box027  label="removeToCreteHoleForPlugHousing036"
  AttacherType = Attacher::AttachEngine3D
  Height = 28.6
  Length = 20
  Placement = pos=(106.15,0,21.7) rot=(0,0,1;0rad)
  Width = 19
FEATURE [Part::Cut] Cut041  label="top022"
  Base = -> Cut040
  Tool = -> Fusion087
FEATURE [Part::Cut] Cut039  label="top020"
  Base = -> Cut041
  Tool = -> Fusion089
FEATURE [Part::MultiFuse] Fusion090  label="removeToCreteHoleForPlugHousing037"
  Placement = pos=(70,19,36) rot=(0,1,0;1.5708rad)
  Shapes = -> [Cylinder042,Cylinder043]
FEATURE [Part::MultiFuse] Fusion088  label="removeToCreteHoleForPlugHousing033"
  Shapes = -> [Box027,Fusion090]
FEATURE [Part::Cut] Cut042  label="removeToCreteHoleForPlugHousing038"
  Base = -> Cut039
  Tool = -> Fusion088
FEATURE [Part::MultiFuse] Fusion091  label="removeFromTop"
  Shapes = -> [Fillet038,Fusion085,Fusion084,Fusion083,Extrude045]
FEATURE [Part::Cut] Cut043  label="REAL TOP ====="
  Base = -> Fillet036
  Tool = -> Fusion091
FEATURE [Part::MultiFuse] Fusion092  label="caseScrewPillarBracket016"
  Shapes = -> [Extrude030,Extrude031,Extrude032,Extrude033,Extrude034,Extrude035,Extrude036,Extrude037,Box013,Box014]
FEATURE [Sketcher::SketchObject] Sketch058  label="topSketch015"
  FullyConstrained = true
  sketch-geometry (20):
    g0: LineSegment StartX=5.21097e-06 StartY=3 StartZ=0 EndX=5.21097e-06 EndY=19 EndZ=0
    g1: ArcOfCircle CenterX=19 CenterY=19 CenterZ=0 NormalX=0 NormalY=0 NormalZ=1 AngleXU=0 Radius=19 StartAngle=1.5708 EndAngle=3.14159
    g2: ArcOfCircle CenterX=19 CenterY=19 CenterZ=0 NormalX=0 NormalY=0 NormalZ=1 AngleXU=0 Radius=16 StartAngle=1.5708 EndAngle=3.14159
    g3: LineSegment StartX=114 StartY=35 StartZ=0 EndX=19 EndY=35 EndZ=0
    g4: LineSegment StartX=5.21097e-06 StartY=3 StartZ=0 EndX=5.21097e-06 EndY=0 EndZ=0
    g5: LineSegment StartX=3 StartY=0 StartZ=0 EndX=5.21097e-06 EndY=0 EndZ=0
    g6: LineSegment StartX=3 StartY=19 StartZ=0 EndX=3 EndY=0 EndZ=0
    g7: LineSegment StartX=19 StartY=38 StartZ=0 EndX=124 EndY=38 EndZ=0
    g8: Circle CenterX=119 CenterY=35 CenterZ=0 NormalX=0 NormalY=0 NormalZ=1 AngleXU=0 Radius=1
    g9: Circle CenterX=121 CenterY=35 CenterZ=0 NormalX=0 NormalY=0 NormalZ=1 AngleXU=0 Radius=1
    g10: Circle CenterX=121 CenterY=33 CenterZ=0 NormalX=0 NormalY=0 NormalZ=1 AngleXU=0 Radius=1
    g11: BSplineCurve PolesCount=3 KnotsCount=2 Degree=2 IsPeriodic=0
    g12: GeomPoint X=119 Y=35 Z=0
    g13: GeomPoint X=121 Y=33 Z=0
    g14: LineSegment StartX=119 StartY=35 StartZ=0 EndX=114 EndY=35 EndZ=0
    g15: ArcOfCircle CenterX=105 CenterY=19 CenterZ=0 NormalX=0 NormalY=0 NormalZ=1 AngleXU=0 Radius=19 StartAngle=5.7297 EndAngle=6.28319
    g16: ArcOfCircle CenterX=105 CenterY=19 CenterZ=0 NormalX=0 NormalY=0 NormalZ=1 AngleXU=0 Radius=16 StartAngle=5.60905 EndAngle=6.28319
    g17: LineSegment StartX=121 StartY=33 StartZ=0 EndX=121 EndY=19 EndZ=0
    g18: LineSegment StartX=124 StartY=38 StartZ=0 EndX=124 EndY=19 EndZ=0
    g19: LineSegment StartX=117.5 StartY=9.01251 StartZ=0 EndX=121.163 EndY=9.0125 EndZ=0
  constraints (46):
    c: Vertical(g0)
    c: Block(g0)
    c: Coincident(g1,g0)
    c: Block(g1)
    c: Coincident(g2,g1)
    c: Block(g2)
    c: Coincident(g3,g2)
    c: Horizontal(g3)
    c: Tangent(g3,g2)
    c: Coincident(g4,g0)
    c: Distance(g4) = 3
    c: Vertical(g4)
    c: Coincident(g5,g4)
    c: Horizontal(g5)
    c: Coincident(g6,g2)
    c: Coincident(g6,g5)
    c: Vertical(g6)
    c: Horizontal(g7)
    c: Distance(g7) = 105
    c: Coincident(g7,g1)
    c: Block(g3)
    c: Weight(g8) = 1
    c: Equal(g8,g9)
    c: Equal(g8,g10)
    c: InternalAlignment(g8,g11)
    c: InternalAlignment(g9,g11)
    c: InternalAlignment(g10,g11)
    c: InternalAlignment(g12,g11)
    c: InternalAlignment(g13,g11)
    c: Block(g11)
    c: Coincident(g14,g11)
    c: Coincident(g14,g3)
    c: Horizontal(g14)
    c: Block(g15)
    c: Coincident(g16,g15)
    c: Block(g16)
    c: Coincident(g17,g11)
    c: Coincident(g17,g16)
    c: Vertical(g17)
    c: Distance(g17) = 14
    c: Coincident(g18,g7)
    c: Coincident(g18,g15)
    c: Vertical(g18)
    c: Distance(g18) = 19
    c: Coincident(g19,g16)
    c: Coincident(g19,g15)
FEATURE [Part::Extrusion] Extrude049  label="top023"
  Base = -> Sketch058
  Dir = (0,0,1)
  DirMode = 2
  FaceMakerClass = Part::FaceMakerBullseye
  LengthFwd = 72
  LengthRev = 0
  Solid = true
  Symmetric = false
FEATURE [Sketcher::SketchObject] Sketch059
  FullyConstrained = true
  MapMode = 3
  Placement = pos=(0,0,0) rot=(1,0,0;1.5708rad)
  Support = -> [Extrude049]
  sketch-geometry (8):
    g0: Circle CenterX=80.351 CenterY=-67.6202 CenterZ=0 NormalX=0 NormalY=0 NormalZ=1 AngleXU=0 Radius=2
    g1: Circle CenterX=80.351 CenterY=-67.6202 CenterZ=0 NormalX=0 NormalY=0 NormalZ=1 AngleXU=0 Radius=3
    g2: Circle CenterX=80.351 CenterY=-4.92017 CenterZ=0 NormalX=0 NormalY=0 NormalZ=1 AngleXU=0 Radius=2
    g3: Circle CenterX=80.351 CenterY=-4.92017 CenterZ=0 NormalX=0 NormalY=0 NormalZ=1 AngleXU=0 Radius=3
    g4: Circle CenterX=23.851 CenterY=-4.92017 CenterZ=0 NormalX=0 NormalY=0 NormalZ=1 AngleXU=0 Radius=2
    g5: Circle CenterX=23.851 CenterY=-4.92017 CenterZ=0 NormalX=0 NormalY=0 NormalZ=1 AngleXU=0 Radius=3
    g6: Circle CenterX=23.851 CenterY=-67.6202 CenterZ=0 NormalX=0 NormalY=0 NormalZ=1 AngleXU=0 Radius=2
    g7: Circle CenterX=23.851 CenterY=-67.6202 CenterZ=0 NormalX=0 NormalY=0 NormalZ=1 AngleXU=0 Radius=3
  constraints (8):
    c: Block(g3)
    c: Block(g2)
    c: Block(g1)
    c: Block(g0)
    c: Block(g6)
    c: Block(g7)
    c: Block(g4)
    c: Block(g5)
FEATURE [Sketcher::SketchObject] Sketch060
  FullyConstrained = true
  MapMode = 3
  Placement = pos=(0,0,0) rot=(1,0,0;1.5708rad)
  Support = -> [Extrude049]
  sketch-geometry (8):
    g0: Circle CenterX=80.351 CenterY=-67.6202 CenterZ=0 NormalX=0 NormalY=0 NormalZ=1 AngleXU=0 Radius=3
    g1: Circle CenterX=80.351 CenterY=-4.92017 CenterZ=0 NormalX=0 NormalY=0 NormalZ=1 AngleXU=0 Radius=3
    g2: Circle CenterX=23.851 CenterY=-4.92017 CenterZ=0 NormalX=0 NormalY=0 NormalZ=1 AngleXU=0 Radius=3
    g3: Circle CenterX=23.851 CenterY=-67.6202 CenterZ=0 NormalX=0 NormalY=0 NormalZ=1 AngleXU=0 Radius=3
    g4: Circle CenterX=23.851 CenterY=-67.6202 CenterZ=0 NormalX=0 NormalY=0 NormalZ=1 AngleXU=0 Radius=5
    g5: Circle CenterX=80.351 CenterY=-67.6202 CenterZ=0 NormalX=0 NormalY=0 NormalZ=1 AngleXU=0 Radius=5
    g6: Circle CenterX=23.851 CenterY=-4.92017 CenterZ=0 NormalX=0 NormalY=0 NormalZ=1 AngleXU=0 Radius=5
    g7: Circle CenterX=80.351 CenterY=-4.92017 CenterZ=0 NormalX=0 NormalY=0 NormalZ=1 AngleXU=0 Radius=5
  constraints (8):
    c: Block(g1)
    c: Block(g0)
    c: Block(g3)
    c: Block(g2)
    c: Block(g5)
    c: Block(g4)
    c: Block(g6)
    c: Block(g7)
FEATURE [Sketcher::SketchObject] Sketch061
  FullyConstrained = true
  MapMode = 3
  Placement = pos=(0,0,0) rot=(1,0,0;1.5708rad)
  sketch-geometry (8):
    g0: Circle CenterX=80.351 CenterY=-67.6202 CenterZ=0 NormalX=0 NormalY=0 NormalZ=1 AngleXU=0 Radius=3
    g1: Circle CenterX=80.351 CenterY=-4.92017 CenterZ=0 NormalX=0 NormalY=0 NormalZ=1 AngleXU=0 Radius=3
    g2: Circle CenterX=23.851 CenterY=-4.92017 CenterZ=0 NormalX=0 NormalY=0 NormalZ=1 AngleXU=0 Radius=3
    g3: Circle CenterX=23.851 CenterY=-67.6202 CenterZ=0 NormalX=0 NormalY=0 NormalZ=1 AngleXU=0 Radius=3
    g4: Circle CenterX=23.851 CenterY=-67.6202 CenterZ=0 NormalX=0 NormalY=0 NormalZ=1 AngleXU=0 Radius=5
    g5: Circle CenterX=80.351 CenterY=-67.6202 CenterZ=0 NormalX=0 NormalY=0 NormalZ=1 AngleXU=0 Radius=5
    g6: Circle CenterX=23.851 CenterY=-4.92017 CenterZ=0 NormalX=0 NormalY=0 NormalZ=1 AngleXU=0 Radius=5
    g7: Circle CenterX=80.351 CenterY=-4.92017 CenterZ=0 NormalX=0 NormalY=0 NormalZ=1 AngleXU=0 Radius=5
  constraints (8):
    c: Block(g1)
    c: Block(g0)
    c: Block(g3)
    c: Block(g2)
    c: Block(g5)
    c: Block(g4)
    c: Block(g6)
    c: Block(g7)
FEATURE [Sketcher::SketchObject] Sketch062  label="topSketch016"
  FullyConstrained = true
  sketch-geometry (20):
    g0: LineSegment StartX=5.21097e-06 StartY=3 StartZ=0 EndX=5.21097e-06 EndY=19 EndZ=0
    g1: ArcOfCircle CenterX=19 CenterY=19 CenterZ=0 NormalX=0 NormalY=0 NormalZ=1 AngleXU=0 Radius=19 StartAngle=1.5708 EndAngle=3.14159
    g2: ArcOfCircle CenterX=19 CenterY=19 CenterZ=0 NormalX=0 NormalY=0 NormalZ=1 AngleXU=0 Radius=16 StartAngle=1.5708 EndAngle=3.14159
    g3: LineSegment StartX=114 StartY=35 StartZ=0 EndX=19 EndY=35 EndZ=0
    g4: LineSegment StartX=5.21097e-06 StartY=3 StartZ=0 EndX=5.21097e-06 EndY=0 EndZ=0
    g5: LineSegment StartX=3 StartY=0 StartZ=0 EndX=5.21097e-06 EndY=0 EndZ=0
    g6: LineSegment StartX=3 StartY=19 StartZ=0 EndX=3 EndY=0 EndZ=0
    g7: LineSegment StartX=19 StartY=38 StartZ=0 EndX=124 EndY=38 EndZ=0
    g8: Circle CenterX=119 CenterY=35 CenterZ=0 NormalX=0 NormalY=0 NormalZ=1 AngleXU=0 Radius=1
    g9: Circle CenterX=121 CenterY=35 CenterZ=0 NormalX=0 NormalY=0 NormalZ=1 AngleXU=0 Radius=1
    g10: Circle CenterX=121 CenterY=33 CenterZ=0 NormalX=0 NormalY=0 NormalZ=1 AngleXU=0 Radius=1
    g11: BSplineCurve PolesCount=3 KnotsCount=2 Degree=2 IsPeriodic=0
    g12: GeomPoint X=119 Y=35 Z=0
    g13: GeomPoint X=121 Y=33 Z=0
    g14: LineSegment StartX=119 StartY=35 StartZ=0 EndX=114 EndY=35 EndZ=0
    g15: ArcOfCircle CenterX=105 CenterY=19 CenterZ=0 NormalX=0 NormalY=0 NormalZ=1 AngleXU=0 Radius=19 StartAngle=5.7297 EndAngle=6.28319
    g16: ArcOfCircle CenterX=105 CenterY=19 CenterZ=0 NormalX=0 NormalY=0 NormalZ=1 AngleXU=0 Radius=16 StartAngle=5.60905 EndAngle=6.28319
    g17: LineSegment StartX=121 StartY=33 StartZ=0 EndX=121 EndY=19 EndZ=0
    g18: LineSegment StartX=124 StartY=38 StartZ=0 EndX=124 EndY=19 EndZ=0
    g19: LineSegment StartX=117.5 StartY=9.01251 StartZ=0 EndX=121.163 EndY=9.0125 EndZ=0
  constraints (46):
    c: Vertical(g0)
    c: Block(g0)
    c: Coincident(g1,g0)
    c: Block(g1)
    c: Coincident(g2,g1)
    c: Block(g2)
    c: Coincident(g3,g2)
    c: Horizontal(g3)
    c: Tangent(g3,g2)
    c: Coincident(g4,g0)
    c: Distance(g4) = 3
    c: Vertical(g4)
    c: Coincident(g5,g4)
    c: Horizontal(g5)
    c: Coincident(g6,g2)
    c: Coincident(g6,g5)
    c: Vertical(g6)
    c: Horizontal(g7)
    c: Distance(g7) = 105
    c: Coincident(g7,g1)
    c: Block(g3)
    c: Weight(g8) = 1
    c: Equal(g8,g9)
    c: Equal(g8,g10)
    c: InternalAlignment(g8,g11)
    c: InternalAlignment(g9,g11)
    c: InternalAlignment(g10,g11)
    c: InternalAlignment(g12,g11)
    c: InternalAlignment(g13,g11)
    c: Block(g11)
    c: Coincident(g14,g11)
    c: Coincident(g14,g3)
    c: Horizontal(g14)
    c: Block(g15)
    c: Coincident(g16,g15)
    c: Block(g16)
    c: Coincident(g17,g11)
    c: Coincident(g17,g16)
    c: Vertical(g17)
    c: Distance(g17) = 14
    c: Coincident(g18,g7)
    c: Coincident(g18,g15)
    c: Vertical(g18)
    c: Distance(g18) = 19
    c: Coincident(g19,g16)
    c: Coincident(g19,g15)
FEATURE [Part::Extrusion] Extrude053  label="top024"
  Base = -> Sketch062
  Dir = (0,0,1)
  DirMode = 2
  FaceMakerClass = Part::FaceMakerBullseye
  LengthFwd = 72
  LengthRev = 0
  Solid = true
  Symmetric = false
FEATURE [Sketcher::SketchObject] Sketch063
  FullyConstrained = true
  MapMode = 3
  Placement = pos=(0,0,0) rot=(1,0,0;1.5708rad)
  Support = -> [Extrude053]
  sketch-geometry (8):
    g0: Circle CenterX=80.351 CenterY=-67.6202 CenterZ=0 NormalX=0 NormalY=0 NormalZ=1 AngleXU=0 Radius=2
    g1: Circle CenterX=80.351 CenterY=-67.6202 CenterZ=0 NormalX=0 NormalY=0 NormalZ=1 AngleXU=0 Radius=3
    g2: Circle CenterX=80.351 CenterY=-4.92017 CenterZ=0 NormalX=0 NormalY=0 NormalZ=1 AngleXU=0 Radius=2
    g3: Circle CenterX=80.351 CenterY=-4.92017 CenterZ=0 NormalX=0 NormalY=0 NormalZ=1 AngleXU=0 Radius=3
    g4: Circle CenterX=23.851 CenterY=-4.92017 CenterZ=0 NormalX=0 NormalY=0 NormalZ=1 AngleXU=0 Radius=2
    g5: Circle CenterX=23.851 CenterY=-4.92017 CenterZ=0 NormalX=0 NormalY=0 NormalZ=1 AngleXU=0 Radius=3
    g6: Circle CenterX=23.851 CenterY=-67.6202 CenterZ=0 NormalX=0 NormalY=0 NormalZ=1 AngleXU=0 Radius=2
    g7: Circle CenterX=23.851 CenterY=-67.6202 CenterZ=0 NormalX=0 NormalY=0 NormalZ=1 AngleXU=0 Radius=3
  constraints (8):
    c: Block(g3)
    c: Block(g2)
    c: Block(g1)
    c: Block(g0)
    c: Block(g6)
    c: Block(g7)
    c: Block(g4)
    c: Block(g5)
FEATURE [Part::Extrusion] Extrude054
  Base = -> Sketch063
  Dir = (0,-1,2e-16)
  DirMode = 2
  FaceMakerClass = Part::FaceMakerBullseye
  LengthFwd = 6
  LengthRev = 0
  Placement = pos=(0,9,0) rot=(0,0,1;0rad)
  Solid = true
  Symmetric = false
FEATURE [Sketcher::SketchObject] Sketch064  label="topSketch017"
  FullyConstrained = true
  sketch-geometry (20):
    g0: LineSegment StartX=5.21097e-06 StartY=3 StartZ=0 EndX=5.21097e-06 EndY=19 EndZ=0
    g1: ArcOfCircle CenterX=19 CenterY=19 CenterZ=0 NormalX=0 NormalY=0 NormalZ=1 AngleXU=0 Radius=19 StartAngle=1.5708 EndAngle=3.14159
    g2: ArcOfCircle CenterX=19 CenterY=19 CenterZ=0 NormalX=0 NormalY=0 NormalZ=1 AngleXU=0 Radius=16 StartAngle=1.5708 EndAngle=3.14159
    g3: LineSegment StartX=114 StartY=35 StartZ=0 EndX=19 EndY=35 EndZ=0
    g4: LineSegment StartX=5.21097e-06 StartY=3 StartZ=0 EndX=5.21097e-06 EndY=0 EndZ=0
    g5: LineSegment StartX=3 StartY=0 StartZ=0 EndX=5.21097e-06 EndY=0 EndZ=0
    g6: LineSegment StartX=3 StartY=19 StartZ=0 EndX=3 EndY=0 EndZ=0
    g7: LineSegment StartX=19 StartY=38 StartZ=0 EndX=124 EndY=38 EndZ=0
    g8: Circle CenterX=119 CenterY=35 CenterZ=0 NormalX=0 NormalY=0 NormalZ=1 AngleXU=0 Radius=1
    g9: Circle CenterX=121 CenterY=35 CenterZ=0 NormalX=0 NormalY=0 NormalZ=1 AngleXU=0 Radius=1
    g10: Circle CenterX=121 CenterY=33 CenterZ=0 NormalX=0 NormalY=0 NormalZ=1 AngleXU=0 Radius=1
    g11: BSplineCurve PolesCount=3 KnotsCount=2 Degree=2 IsPeriodic=0
    g12: GeomPoint X=119 Y=35 Z=0
    g13: GeomPoint X=121 Y=33 Z=0
    g14: LineSegment StartX=119 StartY=35 StartZ=0 EndX=114 EndY=35 EndZ=0
    g15: ArcOfCircle CenterX=105 CenterY=19 CenterZ=0 NormalX=0 NormalY=0 NormalZ=1 AngleXU=0 Radius=19 StartAngle=5.7297 EndAngle=6.28319
    g16: ArcOfCircle CenterX=105 CenterY=19 CenterZ=0 NormalX=0 NormalY=0 NormalZ=1 AngleXU=0 Radius=16 StartAngle=5.60905 EndAngle=6.28319
    g17: LineSegment StartX=121 StartY=33 StartZ=0 EndX=121 EndY=19 EndZ=0
    g18: LineSegment StartX=124 StartY=38 StartZ=0 EndX=124 EndY=19 EndZ=0
    g19: LineSegment StartX=117.5 StartY=9.01251 StartZ=0 EndX=121.163 EndY=9.0125 EndZ=0
  constraints (46):
    c: Vertical(g0)
    c: Block(g0)
    c: Coincident(g1,g0)
    c: Block(g1)
    c: Coincident(g2,g1)
    c: Block(g2)
    c: Coincident(g3,g2)
    c: Horizontal(g3)
    c: Tangent(g3,g2)
    c: Coincident(g4,g0)
    c: Distance(g4) = 3
    c: Vertical(g4)
    c: Coincident(g5,g4)
    c: Horizontal(g5)
    c: Coincident(g6,g2)
    c: Coincident(g6,g5)
    c: Vertical(g6)
    c: Horizontal(g7)
    c: Distance(g7) = 105
    c: Coincident(g7,g1)
    c: Block(g3)
    c: Weight(g8) = 1
    c: Equal(g8,g9)
    c: Equal(g8,g10)
    c: InternalAlignment(g8,g11)
    c: InternalAlignment(g9,g11)
    c: InternalAlignment(g10,g11)
    c: InternalAlignment(g12,g11)
    c: InternalAlignment(g13,g11)
    c: Block(g11)
    c: Coincident(g14,g11)
    c: Coincident(g14,g3)
    c: Horizontal(g14)
    c: Block(g15)
    c: Coincident(g16,g15)
    c: Block(g16)
    c: Coincident(g17,g11)
    c: Coincident(g17,g16)
    c: Vertical(g17)
    c: Distance(g17) = 14
    c: Coincident(g18,g7)
    c: Coincident(g18,g15)
    c: Vertical(g18)
    c: Distance(g18) = 19
    c: Coincident(g19,g16)
    c: Coincident(g19,g15)
FEATURE [Sketcher::SketchObject] Sketch065
  FullyConstrained = true
  MapMode = 3
  Placement = pos=(0,0,0) rot=(1,0,0;1.5708rad)
  sketch-geometry (8):
    g0: Circle CenterX=80.351 CenterY=-67.6202 CenterZ=0 NormalX=0 NormalY=0 NormalZ=1 AngleXU=0 Radius=3
    g1: Circle CenterX=80.351 CenterY=-4.92017 CenterZ=0 NormalX=0 NormalY=0 NormalZ=1 AngleXU=0 Radius=3
    g2: Circle CenterX=23.851 CenterY=-4.92017 CenterZ=0 NormalX=0 NormalY=0 NormalZ=1 AngleXU=0 Radius=3
    g3: Circle CenterX=23.851 CenterY=-67.6202 CenterZ=0 NormalX=0 NormalY=0 NormalZ=1 AngleXU=0 Radius=3
    g4: Circle CenterX=23.851 CenterY=-67.6202 CenterZ=0 NormalX=0 NormalY=0 NormalZ=1 AngleXU=0 Radius=5
    g5: Circle CenterX=80.351 CenterY=-67.6202 CenterZ=0 NormalX=0 NormalY=0 NormalZ=1 AngleXU=0 Radius=5
    g6: Circle CenterX=23.851 CenterY=-4.92017 CenterZ=0 NormalX=0 NormalY=0 NormalZ=1 AngleXU=0 Radius=5
    g7: Circle CenterX=80.351 CenterY=-4.92017 CenterZ=0 NormalX=0 NormalY=0 NormalZ=1 AngleXU=0 Radius=5
  constraints (8):
    c: Block(g1)
    c: Block(g0)
    c: Block(g3)
    c: Block(g2)
    c: Block(g5)
    c: Block(g4)
    c: Block(g6)
    c: Block(g7)
FEATURE [Part::Extrusion] Extrude056
  Base = -> Sketch065
  Dir = (0,-1,2e-16)
  DirMode = 2
  FaceMakerClass = Part::FaceMakerBullseye
  LengthFwd = 2
  LengthRev = 0
  Solid = true
  Symmetric = false
FEATURE [Part::Extrusion] Extrude057  label="top025"
  Base = -> Sketch064
  Dir = (0,0,1)
  DirMode = 2
  FaceMakerClass = Part::FaceMakerBullseye
  LengthFwd = 72
  LengthRev = 0
  Solid = true
  Symmetric = false
FEATURE [Sketcher::SketchObject] Sketch066
  FullyConstrained = true
  MapMode = 3
  Placement = pos=(0,0,0) rot=(1,0,0;1.5708rad)
  Support = -> [Extrude057]
  sketch-geometry (8):
    g0: Circle CenterX=80.351 CenterY=-67.6202 CenterZ=0 NormalX=0 NormalY=0 NormalZ=1 AngleXU=0 Radius=3
    g1: Circle CenterX=80.351 CenterY=-4.92017 CenterZ=0 NormalX=0 NormalY=0 NormalZ=1 AngleXU=0 Radius=3
    g2: Circle CenterX=23.851 CenterY=-4.92017 CenterZ=0 NormalX=0 NormalY=0 NormalZ=1 AngleXU=0 Radius=3
    g3: Circle CenterX=23.851 CenterY=-67.6202 CenterZ=0 NormalX=0 NormalY=0 NormalZ=1 AngleXU=0 Radius=3
    g4: Circle CenterX=23.851 CenterY=-67.6202 CenterZ=0 NormalX=0 NormalY=0 NormalZ=1 AngleXU=0 Radius=5
    g5: Circle CenterX=80.351 CenterY=-67.6202 CenterZ=0 NormalX=0 NormalY=0 NormalZ=1 AngleXU=0 Radius=5
    g6: Circle CenterX=23.851 CenterY=-4.92017 CenterZ=0 NormalX=0 NormalY=0 NormalZ=1 AngleXU=0 Radius=5
    g7: Circle CenterX=80.351 CenterY=-4.92017 CenterZ=0 NormalX=0 NormalY=0 NormalZ=1 AngleXU=0 Radius=5
  constraints (8):
    c: Block(g1)
    c: Block(g0)
    c: Block(g3)
    c: Block(g2)
    c: Block(g5)
    c: Block(g4)
    c: Block(g6)
    c: Block(g7)
FEATURE [Part::Extrusion] Extrude055
  Base = -> Sketch066
  Dir = (0,-1,2e-16)
  DirMode = 2
  FaceMakerClass = Part::FaceMakerBullseye
  LengthFwd = 2
  LengthRev = 0
  Solid = true
  Symmetric = false
FEATURE [Part::Fillet] Fillet041
  Base = -> Extrude056
  Edges = 4 edges r=1.99: [Edge6,Edge12,Edge18,Edge24]
FEATURE [Part::Cut] Cut045
  Base = -> Extrude055
  Placement = pos=(0,6,0) rot=(0,0,1;0rad)
  Tool = -> Fillet041
FEATURE [Part::MultiFuse] Fusion095  label="pcbScrewPillars"
  Placement = pos=(-3.2,-1,72.3) rot=(0,0,1;0rad)
  Shapes = -> [Cut045,Extrude054]
FEATURE [Part::Feature] Face113
  shape: bbox 3.2 x 1.5 x 2e-07 mm, 1 faces, 0 solids (baked)
FEATURE [Part::Revolution] Revolve121  label="backCaseScrewRetainer002"
  Angle = 360
  Axis = (0,1,0)
  Base = (0,0,0)
  FaceMakerClass = Part::FaceMakerBullseye
  Placement = pos=(12.5,3,62) rot=(0,0,1;0rad)
  Solid = false
  Source = -> Face113
  Symmetric = false
FEATURE [Part::Feature] Face114
  shape: bbox 3.2 x 1.5 x 2e-07 mm, 1 faces, 0 solids (baked)
FEATURE [Part::Feature] Face115
  shape: bbox 3.2 x 1.5 x 2e-07 mm, 1 faces, 0 solids (baked)
FEATURE [Part::Feature] Face116
  shape: bbox 3.2 x 1.5 x 2e-07 mm, 1 faces, 0 solids (baked)
FEATURE [Part::Revolution] Revolve122  label="frontCaseScrewRetainer004"
  Angle = 360
  Axis = (0,1,0)
  Base = (0,0,0)
  FaceMakerClass = Part::FaceMakerBullseye
  Placement = pos=(89.5,3,68.5) rot=(0,0,1;0rad)
  Solid = false
  Source = -> Face115
  Symmetric = false
FEATURE [Part::Revolution] Revolve123  label="frontCaseScrewRetainer005"
  Angle = 360
  Axis = (0,1,0)
  Base = (0,0,0)
  FaceMakerClass = Part::FaceMakerBullseye
  Placement = pos=(89.5,3,3.5) rot=(0,0,1;0rad)
  Solid = false
  Source = -> Face116
  Symmetric = false
FEATURE [Part::Revolution] Revolve124  label="backCaseScrewRetainer003"
  Angle = 360
  Axis = (0,1,0)
  Base = (0,0,0)
  FaceMakerClass = Part::FaceMakerBullseye
  Placement = pos=(12.5,3,10) rot=(0,0,1;0rad)
  Solid = false
  Source = -> Face114
  Symmetric = false
FEATURE [Part::Feature] Face117
  shape: bbox 3.6 x 3.2 x 2e-07 mm, 1 faces, 0 solids (baked)
FEATURE [Part::Revolution] Revolve125  label="moreFrontCaseScrewRetainer004"
  Angle = 360
  Axis = (0,1,0)
  Base = (0,0,0)
  FaceMakerClass = Part::FaceMakerBullseye
  Placement = pos=(109.5,4.5,68.5) rot=(0,0,1;0rad)
  Solid = false
  Source = -> Face117
  Symmetric = false
FEATURE [Part::Feature] Face118
  shape: bbox 3.6 x 3.2 x 2e-07 mm, 1 faces, 0 solids (baked)
FEATURE [Part::Revolution] Revolve126  label="moreFrontCaseScrewRetainer005"
  Angle = 360
  Axis = (0,1,0)
  Base = (0,0,0)
  FaceMakerClass = Part::FaceMakerBullseye
  Placement = pos=(109.5,4.5,3.5) rot=(0,0,1;0rad)
  Solid = false
  Source = -> Face118
  Symmetric = false
FEATURE [Part::MultiFuse] Fusion096  label="screwRetainers001"
  Shapes = -> [Revolve126,Revolve125,Revolve124,Revolve123,Revolve122,Revolve121]
FEATURE [Part::Feature] Face119
  shape: bbox 10 x 16.5 x 2e-07 mm, 1 faces, 0 solids (baked)
FEATURE [Part::Revolution] Revolve130  label="plugHousing050"
  Angle = 360
  Axis = (0,1,0)
  Base = (0,0,0)
  FaceMakerClass = Part::FaceMakerBullseye
  Placement = pos=(0,0,36.15) rot=(0,0,1;0rad)
  Solid = false
  Source = -> Face119
  Symmetric = false
FEATURE [Part::Feature] Face120
  shape: bbox 10 x 16.5 x 2e-07 mm, 1 faces, 0 solids (baked)
FEATURE [Part::Feature] Face121
  shape: bbox 10 x 16.5 x 2e-07 mm, 1 faces, 0 solids (baked)
FEATURE [Part::Revolution] Revolve127  label="plugHousing047"
  Angle = 360
  Axis = (0,1,0)
  Base = (0,0,0)
  FaceMakerClass = Part::FaceMakerBullseye
  Placement = pos=(0,0,36.15) rot=(0,0,1;0rad)
  Solid = false
  Source = -> Face121
  Symmetric = false
FEATURE [Part::Feature] Face122
  shape: bbox 10 x 16.5 x 2e-07 mm, 1 faces, 0 solids (baked)
FEATURE [Part::Feature] Face123
  shape: bbox 10 x 16.5 x 2e-07 mm, 1 faces, 0 solids (baked)
FEATURE [Part::Revolution] Revolve128  label="plugHousing048"
  Angle = 360
  Axis = (0,1,0)
  Base = (0,0,0)
  FaceMakerClass = Part::FaceMakerBullseye
  Placement = pos=(0,0,36.15) rot=(0,0,1;0rad)
  Solid = false
  Source = -> Face123
  Symmetric = false
FEATURE [Part::MultiFuse] Fusion100  label="plugHousing054"
  Placement = pos=(0,0,0) rot=(0,0,1;1.5708rad)
  Shapes = -> [Revolve130,Revolve128]
FEATURE [Part::Feature] Face124
  shape: bbox 10 x 16.5 x 2e-07 mm, 1 faces, 0 solids (baked)
FEATURE [Part::Feature] Face125
  shape: bbox 10 x 16.5 x 2e-07 mm, 1 faces, 0 solids (baked)
FEATURE [Part::Revolution] Revolve129  label="plugHousing049"
  Angle = 360
  Axis = (0,1,0)
  Base = (0,0,0)
  FaceMakerClass = Part::FaceMakerBullseye
  Placement = pos=(0,0,36.15) rot=(0,0,1;0rad)
  Solid = false
  Source = -> Face125
  Symmetric = false
FEATURE [Part::Feature] Face126
  shape: bbox 10 x 16.5 x 2e-07 mm, 1 faces, 0 solids (baked)
FEATURE [Part::Revolution] Revolve131  label="plugHousing058"
  Angle = 360
  Axis = (0,1,0)
  Base = (0,0,0)
  FaceMakerClass = Part::FaceMakerBullseye
  Placement = pos=(0,0,36.15) rot=(0,0,1;0rad)
  Solid = false
  Source = -> Face120
  Symmetric = false
FEATURE [Part::MultiFuse] Fusion099  label="plugHousing053"
  Placement = pos=(0,0,0) rot=(0,0,1;1.5708rad)
  Shapes = -> [Revolve127,Revolve131]
FEATURE [Part::MultiFuse] Fusion102  label="plugHousing056"
  Placement = pos=(0,19,0) rot=(0,0,1;3.14159rad)
  Shapes = -> [Fusion100,Fusion099]
FEATURE [Part::Revolution] Revolve132  label="plugHousing059"
  Angle = 360
  Axis = (0,1,0)
  Base = (0,0,0)
  FaceMakerClass = Part::FaceMakerBullseye
  Placement = pos=(0,0,36.15) rot=(0,0,1;0rad)
  Solid = false
  Source = -> Face126
  Symmetric = false
FEATURE [Part::Revolution] Revolve133  label="plugHousing060"
  Angle = 360
  Axis = (0,1,0)
  Base = (0,0,0)
  FaceMakerClass = Part::FaceMakerBullseye
  Placement = pos=(0,0,36.15) rot=(0,0,1;0rad)
  Solid = false
  Source = -> Face122
  Symmetric = false
FEATURE [Part::MultiFuse] Fusion097  label="plugHousing051"
  Placement = pos=(0,0,0) rot=(0,0,1;1.5708rad)
  Shapes = -> [Revolve133,Revolve132]
FEATURE [Part::Revolution] Revolve134  label="plugHousing061"
  Angle = 360
  Axis = (0,1,0)
  Base = (0,0,0)
  FaceMakerClass = Part::FaceMakerBullseye
  Placement = pos=(0,0,36.15) rot=(0,0,1;0rad)
  Solid = false
  Source = -> Face124
  Symmetric = false
FEATURE [Part::MultiFuse] Fusion101  label="plugHousing055"
  Placement = pos=(0,0,0) rot=(0,0,1;1.5708rad)
  Shapes = -> [Revolve129,Revolve134]
FEATURE [Part::MultiFuse] Fusion098  label="plugHousing052"
  Placement = pos=(0,19,0) rot=(0,0,1;3.14159rad)
  Shapes = -> [Fusion097,Fusion101]
FEATURE [Part::MultiFuse] Fusion103  label="plugHousing057"
  Placement = pos=(122.621,0,-0.15) rot=(0,0,1;0rad)
  Shapes = -> [Fusion102,Fusion098]
FEATURE [Part::Box] Box028  label="Cube015"
  AttacherType = Attacher::AttachEngine3D
  Height = 28
  Length = 3
  Placement = pos=(110.7,19,22) rot=(0,0,1;0rad)
  Width = 15.7
FEATURE [Part::Cylinder] Cylinder044
  Angle = 360
  AttacherType = Attacher::AttachEngine3D
  Height = 20
  Placement = pos=(0,0,36.15) rot=(0,0,1;0rad)
  Radius = 10.3
FEATURE [Part::Cylinder] Cylinder045
  Angle = 360
  AttacherType = Attacher::AttachEngine3D
  Height = 10
  Placement = pos=(0,0,36.15) rot=(0,0,1;0rad)
  Radius = 4
FEATURE [Part::MultiFuse] Fusion104  label="removeToCreteHoleForPlugHousing040"
  Placement = pos=(70,19,36) rot=(0,1,0;1.5708rad)
  Shapes = -> [Cylinder044,Cylinder045]
FEATURE [Part::Cut] Cut046  label="plugHousingTab003"
  Base = -> Box028
  Tool = -> Fusion104
FEATURE [Part::MultiFuse] Fusion105  label="plugHousing062"
  Shapes = -> [Fusion103,Cut046]
FEATURE [Part::Fillet] Fillet042
  Base = -> Fusion105
  Edges = 1 edges r=2: [Edge25]
FEATURE [Part::Fillet] Fillet043  label="plugHousing063"
  Base = -> Fillet042
  Edges = 1 edges r=2: [Edge8]
  Placement = pos=(7,0,0) rot=(0,0,1;0rad)
FEATURE [Part::Feature] Face127
  shape: bbox 10 x 16.5 x 2e-07 mm, 1 faces, 0 solids (baked)
FEATURE [Part::Feature] Face128
  shape: bbox 10 x 16.5 x 2e-07 mm, 1 faces, 0 solids (baked)
FEATURE [Part::Revolution] Revolve137  label="plugHousing070"
  Angle = 360
  Axis = (0,1,0)
  Base = (0,0,0)
  FaceMakerClass = Part::FaceMakerBullseye
  Placement = pos=(0,0,36.15) rot=(0,0,1;0rad)
  Solid = false
  Source = -> Face127
  Symmetric = false
FEATURE [Part::Revolution] Revolve140  label="plugHousing073"
  Angle = 360
  Axis = (0,1,0)
  Base = (0,0,0)
  FaceMakerClass = Part::FaceMakerBullseye
  Placement = pos=(0,0,36.15) rot=(0,0,1;0rad)
  Solid = false
  Source = -> Face128
  Symmetric = false
FEATURE [Part::Feature] Face129
  shape: bbox 10 x 16.5 x 2e-07 mm, 1 faces, 0 solids (baked)
FEATURE [Part::Revolution] Revolve138  label="plugHousing071"
  Angle = 360
  Axis = (0,1,0)
  Base = (0,0,0)
  FaceMakerClass = Part::FaceMakerBullseye
  Placement = pos=(0,0,36.15) rot=(0,0,1;0rad)
  Solid = false
  Source = -> Face129
  Symmetric = false
FEATURE [Part::Feature] Face130
  shape: bbox 10 x 16.5 x 2e-07 mm, 1 faces, 0 solids (baked)
FEATURE [Part::Revolution] Revolve139  label="plugHousing072"
  Angle = 360
  Axis = (0,1,0)
  Base = (0,0,0)
  FaceMakerClass = Part::FaceMakerBullseye
  Placement = pos=(0,0,36.15) rot=(0,0,1;0rad)
  Solid = false
  Source = -> Face130
  Symmetric = false
FEATURE [Part::Feature] Face131
  shape: bbox 10 x 16.5 x 2e-07 mm, 1 faces, 0 solids (baked)
FEATURE [Part::Revolution] Revolve135  label="plugHousing068"
  Angle = 360
  Axis = (0,1,0)
  Base = (0,0,0)
  FaceMakerClass = Part::FaceMakerBullseye
  Placement = pos=(0,0,36.15) rot=(0,0,1;0rad)
  Solid = false
  Source = -> Face131
  Symmetric = false
FEATURE [Part::MultiFuse] Fusion112  label="plugHousing078"
  Placement = pos=(0,0,0) rot=(0,0,1;1.5708rad)
  Shapes = -> [Revolve135,Revolve139]
FEATURE [Part::Feature] Face132
  shape: bbox 10 x 16.5 x 2e-07 mm, 1 faces, 0 solids (baked)
FEATURE [Part::Revolution] Revolve141  label="plugHousing074"
  Angle = 360
  Axis = (0,1,0)
  Base = (0,0,0)
  FaceMakerClass = Part::FaceMakerBullseye
  Placement = pos=(0,0,36.15) rot=(0,0,1;0rad)
  Solid = false
  Source = -> Face132
  Symmetric = false
FEATURE [Part::MultiFuse] Fusion110  label="plugHousing076"
  Placement = pos=(0,0,0) rot=(0,0,1;1.5708rad)
  Shapes = -> [Revolve141,Revolve140]
FEATURE [Part::Feature] Face133
  shape: bbox 10 x 16.5 x 2e-07 mm, 1 faces, 0 solids (baked)
FEATURE [Part::Revolution] Revolve136  label="plugHousing069"
  Angle = 360
  Axis = (0,1,0)
  Base = (0,0,0)
  FaceMakerClass = Part::FaceMakerBullseye
  Placement = pos=(0,0,36.15) rot=(0,0,1;0rad)
  Solid = false
  Source = -> Face133
  Symmetric = false
FEATURE [Part::MultiFuse] Fusion106  label="plugHousing064"
  Placement = pos=(0,0,0) rot=(0,0,1;1.5708rad)
  Shapes = -> [Revolve138,Revolve136]
FEATURE [Part::MultiFuse] Fusion108  label="plugHousing066"
  Placement = pos=(0,19,0) rot=(0,0,1;3.14159rad)
  Shapes = -> [Fusion106,Fusion112]
FEATURE [Part::Feature] Face134
  shape: bbox 10 x 16.5 x 2e-07 mm, 1 faces, 0 solids (baked)
FEATURE [Part::Revolution] Revolve142  label="plugHousing075"
  Angle = 360
  Axis = (0,1,0)
  Base = (0,0,0)
  FaceMakerClass = Part::FaceMakerBullseye
  Placement = pos=(0,0,36.15) rot=(0,0,1;0rad)
  Solid = false
  Source = -> Face134
  Symmetric = false
FEATURE [Part::MultiFuse] Fusion107  label="plugHousing065"
  Placement = pos=(0,0,0) rot=(0,0,1;1.5708rad)
  Shapes = -> [Revolve137,Revolve142]
FEATURE [Part::MultiFuse] Fusion111  label="plugHousing077"
  Placement = pos=(0,19,0) rot=(0,0,1;3.14159rad)
  Shapes = -> [Fusion110,Fusion107]
FEATURE [Part::MultiFuse] Fusion109  label="plugHousing067"
  Placement = pos=(131.236,0,-0.15) rot=(0,0,1;0rad)
  Shapes = -> [Fusion108,Fusion111]
FEATURE [Part::MultiFuse] Fusion113  label="plugHousing079"
  Shapes = -> [Fillet043,Fusion109]
FEATURE [Part::Feature] Face135
  shape: bbox 3.5 x 17.8 x 2e-07 mm, 1 faces, 0 solids (baked)
FEATURE [Part::Revolution] Revolve143  label="removeToCreateScrewAndThreadedInsertHole049"
  Angle = 360
  Axis = (0,1,0)
  Base = (0,0,0)
  FaceMakerClass = Part::FaceMakerBullseye
  Placement = pos=(12.5,0,10) rot=(0,0,1;0rad)
  Solid = false
  Source = -> Face135
  Symmetric = false
FEATURE [Part::Feature] Face136
  shape: bbox 3.5 x 17.8 x 2e-07 mm, 1 faces, 0 solids (baked)
FEATURE [Part::Revolution] Revolve144  label="removeToCreateScrewAndThreadedInsertHole050"
  Angle = 360
  Axis = (0,1,0)
  Base = (0,0,0)
  FaceMakerClass = Part::FaceMakerBullseye
  Placement = pos=(12.5,0,62) rot=(0,0,1;0rad)
  Solid = false
  Source = -> Face136
  Symmetric = false
FEATURE [Part::Feature] Face137
  shape: bbox 3.5 x 17.8 x 2e-07 mm, 1 faces, 0 solids (baked)
FEATURE [Part::Revolution] Revolve145  label="removeToCreateScrewAndThreadedInsertHole051"
  Angle = 360
  Axis = (0,1,0)
  Base = (0,0,0)
  FaceMakerClass = Part::FaceMakerBullseye
  Placement = pos=(89.5,0,68.5) rot=(0,0,1;0rad)
  Solid = false
  Source = -> Face137
  Symmetric = false
FEATURE [Part::Feature] Face138
  shape: bbox 3.5 x 17.8 x 2e-07 mm, 1 faces, 0 solids (baked)
FEATURE [Part::Revolution] Revolve146  label="removeToCreateScrewAndThreadedInsertHole052"
  Angle = 360
  Axis = (0,1,0)
  Base = (0,0,0)
  FaceMakerClass = Part::FaceMakerBullseye
  Placement = pos=(89.5,0,3.5) rot=(0,0,1;0rad)
  Solid = false
  Source = -> Face138
  Symmetric = false
FEATURE [Part::Feature] Face139
  shape: bbox 3.5 x 17.8 x 2e-07 mm, 1 faces, 0 solids (baked)
FEATURE [Part::Revolution] Revolve147  label="removeToCreateScrewAndThreadedInsertHole053"
  Angle = 360
  Axis = (0,1,0)
  Base = (0,0,0)
  FaceMakerClass = Part::FaceMakerBullseye
  Placement = pos=(109.5,4.7,3.5) rot=(0,0,1;0rad)
  Solid = false
  Source = -> Face139
  Symmetric = false
FEATURE [Part::Feature] Face140
  shape: bbox 3.5 x 17.8 x 2e-07 mm, 1 faces, 0 solids (baked)
FEATURE [Part::Revolution] Revolve148  label="removeToCreateScrewAndThreadedInsertHole054"
  Angle = 360
  Axis = (0,1,0)
  Base = (0,0,0)
  FaceMakerClass = Part::FaceMakerBullseye
  Placement = pos=(109.5,4.7,68.5) rot=(0,0,1;0rad)
  Solid = false
  Source = -> Face140
  Symmetric = false
FEATURE [Part::MultiFuse] Fusion114  label="removeToCreateScrewAndThreadedInsertHole055"
  Shapes = -> [Revolve148,Revolve147,Revolve146,Revolve145,Revolve144,Revolve143]
FEATURE [Part::Cut] Cut047  label="casePillars004"
  Base = -> Cut037
  Tool = -> Fusion114
FEATURE [Part::Feature] Face141
  shape: bbox 3.5 x 17.8 x 2e-07 mm, 1 faces, 0 solids (baked)
FEATURE [Part::Feature] Face142
  shape: bbox 3.5 x 17.8 x 2e-07 mm, 1 faces, 0 solids (baked)
FEATURE [Part::Feature] Face143
  shape: bbox 3.5 x 17.8 x 2e-07 mm, 1 faces, 0 solids (baked)
FEATURE [Part::Revolution] Revolve149  label="removeToCreateScrewAndThreadedInsertHole057"
  Angle = 360
  Axis = (0,1,0)
  Base = (0,0,0)
  FaceMakerClass = Part::FaceMakerBullseye
  Placement = pos=(12.5,0,10) rot=(0,0,1;0rad)
  Solid = false
  Source = -> Face141
  Symmetric = false
FEATURE [Part::Feature] Face144
  shape: bbox 3.5 x 17.8 x 2e-07 mm, 1 faces, 0 solids (baked)
FEATURE [Part::Feature] Face145
  shape: bbox 3.5 x 17.8 x 2e-07 mm, 1 faces, 0 solids (baked)
FEATURE [Part::Feature] Face146
  shape: bbox 3.5 x 17.8 x 2e-07 mm, 1 faces, 0 solids (baked)
FEATURE [Part::Revolution] Revolve150  label="removeToCreateScrewAndThreadedInsertHole058"
  Angle = 360
  Axis = (0,1,0)
  Base = (0,0,0)
  FaceMakerClass = Part::FaceMakerBullseye
  Placement = pos=(12.5,0,62) rot=(0,0,1;0rad)
  Solid = false
  Source = -> Face146
  Symmetric = false
FEATURE [Part::Revolution] Revolve151  label="removeToCreateScrewAndThreadedInsertHole059"
  Angle = 360
  Axis = (0,1,0)
  Base = (0,0,0)
  FaceMakerClass = Part::FaceMakerBullseye
  Placement = pos=(89.5,0,68.5) rot=(0,0,1;0rad)
  Solid = false
  Source = -> Face143
  Symmetric = false
FEATURE [Part::Revolution] Revolve152  label="removeToCreateScrewAndThreadedInsertHole060"
  Angle = 360
  Axis = (0,1,0)
  Base = (0,0,0)
  FaceMakerClass = Part::FaceMakerBullseye
  Placement = pos=(89.5,0,3.5) rot=(0,0,1;0rad)
  Solid = false
  Source = -> Face142
  Symmetric = false
FEATURE [Part::Revolution] Revolve153  label="removeToCreateScrewAndThreadedInsertHole061"
  Angle = 360
  Axis = (0,1,0)
  Base = (0,0,0)
  FaceMakerClass = Part::FaceMakerBullseye
  Placement = pos=(109.5,4.7,3.5) rot=(0,0,1;0rad)
  Solid = false
  Source = -> Face145
  Symmetric = false
FEATURE [Part::Revolution] Revolve154  label="removeToCreateScrewAndThreadedInsertHole062"
  Angle = 360
  Axis = (0,1,0)
  Base = (0,0,0)
  FaceMakerClass = Part::FaceMakerBullseye
  Placement = pos=(109.5,4.7,68.5) rot=(0,0,1;0rad)
  Solid = false
  Source = -> Face144
  Symmetric = false
FEATURE [Part::MultiFuse] Fusion115  label="removeToCreateScrewAndThreadedInsertHole056"
  Shapes = -> [Revolve154,Revolve153,Revolve152,Revolve151,Revolve150,Revolve149]
FEATURE [Part::Feature] Face147
  shape: bbox 9.8 x 26.5 x 2e-07 mm, 1 faces, 0 solids (baked)
FEATURE [Part::Revolution] Revolve155
  Angle = 360
  Axis = (0,1,0)
  Base = (0,0,0)
  FaceMakerClass = Part::FaceMakerBullseye
  Placement = pos=(0,0,0) rot=(0,0,1;1.5708rad)
  Solid = false
  Source = -> Face147
  Symmetric = false
FEATURE [Part::Feature] Face148
  shape: bbox 9.8 x 26.5 x 2e-07 mm, 1 faces, 0 solids (baked)
FEATURE [Part::Revolution] Revolve156
  Angle = 360
  Axis = (0,1,0)
  Base = (0,0,0)
  FaceMakerClass = Part::FaceMakerBullseye
  Placement = pos=(0,0,0) rot=(0,0,1;1.5708rad)
  Solid = false
  Source = -> Face148
  Symmetric = false
FEATURE [Part::MultiFuse] Fusion116
  Placement = pos=(-18,19,36) rot=(0,0,1;0rad)
  Shapes = -> [Revolve156,Revolve155]
FEATURE [Part::Box] Box029  label="Cube016"
  AttacherType = Attacher::AttachEngine3D
  Height = 28
  Length = 3
  Placement = pos=(110.7,19,22) rot=(0,0,1;0rad)
  Width = 15.7
FEATURE [Part::Cylinder] Cylinder046
  Angle = 360
  AttacherType = Attacher::AttachEngine3D
  Height = 10
  Placement = pos=(0,0,36.15) rot=(0,0,1;0rad)
  Radius = 4
FEATURE [Part::Cylinder] Cylinder047
  Angle = 360
  AttacherType = Attacher::AttachEngine3D
  Height = 20
  Placement = pos=(0,0,36.15) rot=(0,0,1;0rad)
  Radius = 10.3
FEATURE [Part::MultiFuse] Fusion117  label="removeToCreteHoleForPlugHousing041"
  Placement = pos=(70,19,36) rot=(0,1,0;1.5708rad)
  Shapes = -> [Cylinder047,Cylinder046]
FEATURE [Part::Cut] Cut049  label="plugHousingTab004"
  Base = -> Box029
  Placement = pos=(-107.4,-14,0) rot=(0,0,1;0rad)
  Tool = -> Fusion117
FEATURE [Part::Box] Box030  label="Cube017"
  AttacherType = Attacher::AttachEngine3D
  Height = 28
  Length = 3
  Placement = pos=(110.7,19,22) rot=(0,0,1;0rad)
  Width = 15.7
FEATURE [Part::Cylinder] Cylinder048
  Angle = 360
  AttacherType = Attacher::AttachEngine3D
  Height = 10
  Placement = pos=(0,0,36.15) rot=(0,0,1;0rad)
  Radius = 4
FEATURE [Part::Cylinder] Cylinder049
  Angle = 360
  AttacherType = Attacher::AttachEngine3D
  Height = 20
  Placement = pos=(0,0,36.15) rot=(0,0,1;0rad)
  Radius = 10.3
FEATURE [Part::MultiFuse] Fusion118  label="removeToCreteHoleForPlugHousing042"
  Placement = pos=(70,19,36) rot=(0,1,0;1.5708rad)
  Shapes = -> [Cylinder049,Cylinder048]
FEATURE [Part::Cut] Cut050  label="plugHousingTab005"
  Base = -> Box030
  Placement = pos=(-107.4,-14,0) rot=(0,0,1;0rad)
  Tool = -> Fusion118
FEATURE [Part::MultiFuse] Fusion119
  Placement = pos=(9.6,23,0) rot=(0,0,1;3.14159rad)
  Shapes = -> [Cut049,Cut050]
FEATURE [Part::Box] Box031  label="Cube018"
  AttacherType = Attacher::AttachEngine3D
  Height = 10
  Length = 3
  Placement = pos=(3.3,4,12) rot=(0,0,1;0rad)
  Width = 10
FEATURE [Part::Fillet] Fillet044
  Base = -> Box031
  Edges = 1 edges r=2: [Edge11]
FEATURE [Part::Box] Box032  label="Cube019"
  AttacherType = Attacher::AttachEngine3D
  Height = 10
  Length = 3
  Placement = pos=(3.3,4,50) rot=(0,0,1;0rad)
  Width = 10
FEATURE [Part::Fillet] Fillet045
  Base = -> Box032
  Edges = 1 edges r=2: [Edge12]
FEATURE [Part::Box] Box033  label="Cube020"
  AttacherType = Attacher::AttachEngine3D
  Height = 28
  Length = 4
  Placement = pos=(5,0,22) rot=(0,0,1;0rad)
  Width = 10
FEATURE [Part::Fillet] Fillet046
  Base = -> Box033
  Edges = 1 edges r=1: [Edge7]
FEATURE [Part::Fillet] Fillet047
  Base = -> Fillet046
  Edges = 1 edges r=2: [Edge5]
FEATURE [Part::Fillet] Fillet048
  Base = -> Fillet047
  Edges = 1 edges r=2: [Edge2]
FEATURE [Part::Cylinder] Cylinder050
  Angle = 360
  AttacherType = Attacher::AttachEngine3D
  Height = 20
  Placement = pos=(0,0,36.15) rot=(0,0,1;0rad)
  Radius = 8.2
FEATURE [Part::Cylinder] Cylinder051
  Angle = 360
  AttacherType = Attacher::AttachEngine3D
  Height = 10
  Placement = pos=(0,0,36.15) rot=(0,0,1;0rad)
  Radius = 4
FEATURE [Part::MultiFuse] Fusion120  label="removeToCreteHoleForPlugHousing043"
  Placement = pos=(-42,19,36) rot=(0,1,0;1.5708rad)
  Shapes = -> [Cylinder050,Cylinder051]
FEATURE [Sketcher::SketchObject] Sketch067  label="topSketch018"
  FullyConstrained = true
  sketch-geometry (4):
    g0: LineSegment StartX=16.8446 StartY=31.512 StartZ=0 EndX=16.3251 EndY=34.4666 EndZ=0
    g1: ArcOfCircle CenterX=19 CenterY=19.2524 CenterZ=0 NormalX=0 NormalY=0 NormalZ=1 AngleXU=0 Radius=15.4476 StartAngle=1.74483 EndAngle=2.72717
    g2: ArcOfCircle CenterX=19 CenterY=19.2524 CenterZ=0 NormalX=0 NormalY=0 NormalZ=1 AngleXU=0 Radius=12.4476 StartAngle=1.74483 EndAngle=2.73189
    g3: LineSegment StartX=4.86004 StartY=25.4725 StartZ=0 EndX=7.58253 EndY=24.2107 EndZ=0
  constraints (7):
    c: Block(g0)
    c: Coincident(g1,g0)
    c: Coincident(g2,g0)
    c: Coincident(g3,g1)
    c: Coincident(g3,g2)
    c: Block(g1)
    c: Block(g2)
FEATURE [Part::Extrusion] Extrude058
  Base = -> Sketch067
  Dir = (0,0,1)
  DirMode = 2
  FaceMakerClass = Part::FaceMakerBullseye
  LengthFwd = 10
  LengthRev = 0
  Placement = pos=(0,0,31) rot=(0,0,1;0rad)
  Solid = true
  Symmetric = false
FEATURE [Part::Cut] Cut051
  Base = -> Extrude058
  Tool = -> Fusion120
FEATURE [Part::Fillet] Fillet049
  Base = -> Cut051
  Edges = 1 edges r=2: [Edge1]
FEATURE [Part::Fillet] Fillet050
  Base = -> Fillet049
  Edges = 1 edges r=2.5: [Edge1]
FEATURE [Part::Fillet] Fillet051
  Base = -> Fillet050
  Edges = 1 edges r=2.5: [Edge2]
FEATURE [Part::MultiFuse] Fusion121  label="wireHolder003"
  Shapes = -> [Fusion116,Fillet051]
FEATURE [Part::MultiFuse] Fusion122
  Shapes = -> [Fillet045,Fusion121]
FEATURE [Part::MultiFuse] Fusion123  label="wireHolder004"
  Shapes = -> [Fusion122,Fillet048]
FEATURE [Part::MultiFuse] Fusion124  label="wireHolder005"
  Shapes = -> [Fillet044,Fusion119,Fusion123]
FEATURE [Part::MultiFuse] Fusion126  label="casePillars005"
  Shapes = -> [Fusion092,Cut047]
FEATURE [Sketcher::SketchObject] Sketch068  label="topSketch019"
  FullyConstrained = true
  sketch-geometry (6):
    g0: LineSegment StartX=19 StartY=38 StartZ=0 EndX=117 EndY=38 EndZ=0
    g1: ArcOfCircle CenterX=19 CenterY=19 CenterZ=0 NormalX=0 NormalY=0 NormalZ=1 AngleXU=0 Radius=19 StartAngle=1.5708 EndAngle=3.14159
    g2: LineSegment StartX=117 StartY=38 StartZ=0 EndX=117 EndY=19 EndZ=0
    g3: LineSegment StartX=98 StartY=1.0161e-12 StartZ=0 EndX=5.22862e-06 EndY=1.0161e-12 EndZ=0
    g4: LineSegment StartX=5.22862e-06 StartY=19 StartZ=0 EndX=5.22862e-06 EndY=1.0161e-12 EndZ=0
    g5: ArcOfCircle CenterX=98 CenterY=19 CenterZ=0 NormalX=0 NormalY=0 NormalZ=1 AngleXU=0 Radius=19 StartAngle=4.71239 EndAngle=6.28319
  constraints (16):
    c: Horizontal(g0)
    c: Distance(g0) = 98
    c: Coincident(g1,g0)
    c: Block(g1)
    c: Coincident(g2,g0)
    c: Vertical(g2)
    c: Distance(g2) = 19
    c: Horizontal(g3)
    c: Coincident(g4,g1)
    c: Vertical(g4)
    c: Coincident(g3,g4)
    c: Block(g3)
    c: Coincident(g5,g2)
    c: Coincident(g5,g3)
    c: Block(g0)
    c: Block(g5)
FEATURE [Part::Extrusion] Extrude059  label="sideA002"
  Base = -> Sketch068
  Dir = (0,0,1)
  DirMode = 2
  FaceMakerClass = Part::FaceMakerBullseye
  LengthFwd = 3
  LengthRev = 0
  Placement = pos=(0,0,-2.7) rot=(0,0,1;0rad)
  Solid = true
  Symmetric = false
FEATURE [Sketcher::SketchObject] Sketch069  label="topSketch020"
  FullyConstrained = true
  sketch-geometry (6):
    g0: LineSegment StartX=19 StartY=38 StartZ=0 EndX=117 EndY=38 EndZ=0
    g1: ArcOfCircle CenterX=19 CenterY=19 CenterZ=0 NormalX=0 NormalY=0 NormalZ=1 AngleXU=0 Radius=19 StartAngle=1.5708 EndAngle=3.14159
    g2: LineSegment StartX=117 StartY=38 StartZ=0 EndX=117 EndY=19 EndZ=0
    g3: LineSegment StartX=98 StartY=1.0161e-12 StartZ=0 EndX=5.22862e-06 EndY=1.0161e-12 EndZ=0
    g4: LineSegment StartX=5.22862e-06 StartY=19 StartZ=0 EndX=5.22862e-06 EndY=1.0161e-12 EndZ=0
    g5: ArcOfCircle CenterX=98 CenterY=19 CenterZ=0 NormalX=0 NormalY=0 NormalZ=1 AngleXU=0 Radius=19 StartAngle=4.71239 EndAngle=6.28319
  constraints (16):
    c: Horizontal(g0)
    c: Distance(g0) = 98
    c: Coincident(g1,g0)
    c: Block(g1)
    c: Coincident(g2,g0)
    c: Vertical(g2)
    c: Distance(g2) = 19
    c: Horizontal(g3)
    c: Coincident(g4,g1)
    c: Vertical(g4)
    c: Coincident(g3,g4)
    c: Block(g3)
    c: Coincident(g5,g2)
    c: Coincident(g5,g3)
    c: Block(g0)
    c: Block(g5)
FEATURE [Part::Extrusion] Extrude060  label="sideB002"
  Base = -> Sketch069
  Dir = (0,0,1)
  DirMode = 2
  FaceMakerClass = Part::FaceMakerBullseye
  LengthFwd = 3
  LengthRev = 0
  Placement = pos=(0,0,71.7) rot=(0,0,1;0rad)
  Solid = true
  Symmetric = false
FEATURE [Part::MultiFuse] Fusion127  label="removeFromBottom001"
  Placement = pos=(2,0,0) rot=(0,0,1;0rad)
  Shapes = -> [Extrude059,Extrude060]
FEATURE [Part::Cylinder] Cylinder052
  Angle = 360
  AttacherType = Attacher::AttachEngine3D
  Height = 20
  Placement = pos=(0,0,36.15) rot=(0,0,1;0rad)
  Radius = 14
FEATURE [Part::Cylinder] Cylinder053
  Angle = 360
  AttacherType = Attacher::AttachEngine3D
  Height = 10
  Placement = pos=(0,0,36.15) rot=(0,0,1;0rad)
  Radius = 4
FEATURE [Part::MultiFuse] Fusion128  label="removeToCreteHoleForPlugHousing044"
  Placement = pos=(70,19,36) rot=(0,1,0;1.5708rad)
  Shapes = -> [Cylinder052,Cylinder053]
FEATURE [Part::Cut] Cut052  label="bottom011"
  Base = -> Extrude043
  Tool = -> Fusion128
FEATURE [Part::Cut] Cut054  label="bottom012"
  Base = -> Cut052
  Tool = -> Fusion115
FEATURE [Sketcher::SketchObject] Sketch070
  FullyConstrained = true
  Placement = pos=(117,19,0) rot=(0.57735,0.57735,0.57735;2.0944rad)
  sketch-geometry (48):
    g0: LineSegment StartX=-49.19 StartY=69.25 StartZ=0 EndX=-49.19 EndY=66.25 EndZ=0
    g1: LineSegment StartX=-49.19 StartY=63.5 StartZ=0 EndX=-49.19 EndY=60.5 EndZ=0
    g2: LineSegment StartX=-49.19 StartY=57.75 StartZ=0 EndX=-49.19 EndY=54.75 EndZ=0
    g3: LineSegment StartX=-49.19 StartY=52 StartZ=0 EndX=-49.19 EndY=49 EndZ=0
    g4: LineSegment StartX=-49.19 StartY=46.25 StartZ=0 EndX=-49.19 EndY=43.25 EndZ=0
    g5: LineSegment StartX=-49.19 StartY=40.5 StartZ=0 EndX=-49.19 EndY=37.5 EndZ=0
    g6: LineSegment StartX=-49.19 StartY=34.5 StartZ=0 EndX=-49.19 EndY=31.5 EndZ=0
    g7: LineSegment StartX=-49.19 StartY=28.75 StartZ=0 EndX=-49.19 EndY=25.75 EndZ=0
    g8: LineSegment StartX=-49.19 StartY=23 StartZ=0 EndX=-49.19 EndY=20 EndZ=0
    g9: LineSegment StartX=-49.19 StartY=17.25 StartZ=0 EndX=-49.19 EndY=14.25 EndZ=0
    g10: LineSegment StartX=-49.19 StartY=11.5 StartZ=0 EndX=-49.19 EndY=8.5 EndZ=0
    g11: LineSegment StartX=-49.19 StartY=5.75 StartZ=0 EndX=-49.19 EndY=2.75 EndZ=0
    g12: ArcOfCircle CenterX=-1.5 CenterY=67.75 CenterZ=0 NormalX=0 NormalY=0 NormalZ=1 AngleXU=0 Radius=1.5 StartAngle=4.71239 EndAngle=7.85398
    g13: ArcOfCircle CenterX=-1.5 CenterY=62 CenterZ=0 NormalX=0 NormalY=0 NormalZ=1 AngleXU=0 Radius=1.5 StartAngle=4.71239 EndAngle=7.85398
    g14: ArcOfCircle CenterX=-1.5 CenterY=56.25 CenterZ=0 NormalX=0 NormalY=0 NormalZ=1 AngleXU=0 Radius=1.5 StartAngle=4.71239 EndAngle=7.85398
    g15: ArcOfCircle CenterX=-11.49 CenterY=50.5 CenterZ=0 NormalX=0 NormalY=0 NormalZ=1 AngleXU=0 Radius=1.5 StartAngle=4.71239 EndAngle=7.85398
    g16: ArcOfCircle CenterX=-16.28 CenterY=44.75 CenterZ=0 NormalX=0 NormalY=0 NormalZ=1 AngleXU=0 Radius=1.5 StartAngle=4.71239 EndAngle=7.85398
    g17: ArcOfCircle CenterX=-18.2337 CenterY=39 CenterZ=0 NormalX=0 NormalY=0 NormalZ=1 AngleXU=0 Radius=1.5 StartAngle=4.71485 EndAngle=7.85398
    g18: ArcOfCircle CenterX=-16.2837 CenterY=27.25 CenterZ=0 NormalX=0 NormalY=0 NormalZ=1 AngleXU=0 Radius=1.5 StartAngle=4.71485 EndAngle=7.85398
    g19: ArcOfCircle CenterX=-18.2337 CenterY=33 CenterZ=0 NormalX=0 NormalY=0 NormalZ=1 AngleXU=0 Radius=1.5 StartAngle=4.71485 EndAngle=7.85398
    g20: ArcOfCircle CenterX=-11.49 CenterY=21.5 CenterZ=0 NormalX=0 NormalY=0 NormalZ=1 AngleXU=0 Radius=1.5 StartAngle=4.71239 EndAngle=7.85398
    g21: ArcOfCircle CenterX=-1.5 CenterY=4.25 CenterZ=0 NormalX=0 NormalY=0 NormalZ=1 AngleXU=0 Radius=1.5 StartAngle=4.71239 EndAngle=7.85398
    g22: ArcOfCircle CenterX=-1.5 CenterY=10 CenterZ=0 NormalX=0 NormalY=0 NormalZ=1 AngleXU=0 Radius=1.5 StartAngle=4.71239 EndAngle=7.85398
    g23: ArcOfCircle CenterX=-1.5 CenterY=15.75 CenterZ=0 NormalX=0 NormalY=0 NormalZ=1 AngleXU=0 Radius=1.5 StartAngle=4.71239 EndAngle=7.85398
    g24: LineSegment StartX=-49.19 StartY=69.25 StartZ=0 EndX=-1.5 EndY=69.25 EndZ=0
    g25: LineSegment StartX=-49.19 StartY=66.25 StartZ=0 EndX=-1.5 EndY=66.25 EndZ=0
    g26: LineSegment StartX=-49.19 StartY=63.5 StartZ=0 EndX=-1.5 EndY=63.5 EndZ=0
    g27: LineSegment StartX=-49.19 StartY=60.5 StartZ=0 EndX=-1.5 EndY=60.5 EndZ=0
    g28: LineSegment StartX=-49.19 StartY=57.75 StartZ=0 EndX=-1.5 EndY=57.75 EndZ=0
    g29: LineSegment StartX=-49.19 StartY=54.75 StartZ=0 EndX=-1.5 EndY=54.75 EndZ=0
    g30: LineSegment StartX=-49.19 StartY=52 StartZ=0 EndX=-11.49 EndY=52 EndZ=0
    g31: LineSegment StartX=-49.19 StartY=49 StartZ=0 EndX=-11.49 EndY=49 EndZ=0
    g32: LineSegment StartX=-49.19 StartY=46.25 StartZ=0 EndX=-16.28 EndY=46.25 EndZ=0
    g33: LineSegment StartX=-49.19 StartY=43.25 StartZ=0 EndX=-16.28 EndY=43.25 EndZ=0
    g34: LineSegment StartX=-49.19 StartY=40.5 StartZ=0 EndX=-18.2337 EndY=40.5 EndZ=0
    g35: LineSegment StartX=-49.19 StartY=37.5 StartZ=0 EndX=-18.23 EndY=37.5 EndZ=0
    g36: LineSegment StartX=-49.19 StartY=34.5 StartZ=0 EndX=-18.2337 EndY=34.5 EndZ=0
    g37: LineSegment StartX=-49.19 StartY=31.5 StartZ=0 EndX=-18.23 EndY=31.5 EndZ=0
    g38: LineSegment StartX=-49.19 StartY=28.75 StartZ=0 EndX=-16.2837 EndY=28.75 EndZ=0
    g39: LineSegment StartX=-49.19 StartY=25.75 StartZ=0 EndX=-16.28 EndY=25.75 EndZ=0
    g40: LineSegment StartX=-49.19 StartY=23 StartZ=0 EndX=-11.49 EndY=23 EndZ=0
    g41: LineSegment StartX=-49.19 StartY=20 StartZ=0 EndX=-11.49 EndY=20 EndZ=0
    g42: LineSegment StartX=-49.19 StartY=17.25 StartZ=0 EndX=-1.5 EndY=17.25 EndZ=0
    g43: LineSegment StartX=-49.19 StartY=14.25 StartZ=0 EndX=-1.5 EndY=14.25 EndZ=0
    g44: LineSegment StartX=-49.19 StartY=11.5 StartZ=0 EndX=-1.5 EndY=11.5 EndZ=0
    g45: LineSegment StartX=-49.19 StartY=8.5 StartZ=0 EndX=-1.5 EndY=8.5 EndZ=0
    g46: LineSegment StartX=-49.19 StartY=5.75 StartZ=0 EndX=-1.5 EndY=5.75 EndZ=0
    g47: LineSegment StartX=-49.19 StartY=2.75 StartZ=0 EndX=-1.5 EndY=2.75 EndZ=0
  constraints (120):
    c: Vertical(g0)
    c: Distance(g0) = 3
    c: Block(g0)
    c: Vertical(g1)
    c: Distance(g1) = 3
    c: Vertical(g2)
    c: Equal(g0,g2) = 3
    c: Block(g2)
    c: Vertical(g3)
    c: Equal(g1,g3) = 3
    c: Vertical(g4)
    c: Equal(g0,g4) = 3
    c: Block(g4)
    c: Vertical(g5)
    c: Equal(g1,g5) = 3
    c: Vertical(g6)
    c: Equal(g0,g6) = 3
    c: Block(g6)
    c: Vertical(g7)
    c: Equal(g1,g7) = 3
    c: Vertical(g8)
    c: Equal(g0,g8) = 3
    c: Block(g8)
    c: Vertical(g9)
    c: Equal(g1,g9) = 3
    c: Vertical(g10)
    c: Equal(g0,g10) = 3
    c: Block(g10)
    c: Vertical(g11)
    c: Equal(g1,g11) = 3
    c: Block(g12)
    c: Block(g13)
    c: Block(g14)
    c: Block(g15)
    c: Block(g16)
    c: Block(g17)
    c: Block(g18)
    c: Block(g19)
    c: Block(g20)
    c: Block(g21)
    c: Block(g22)
    c: Block(g23)
    c: Block(g11)
    c: Block(g9)
    c: Block(g7)
    c: Block(g5)
    c: Block(g3)
    c: Block(g1)
    c: Coincident(g24,g0)
    c: Coincident(g24,g12)
    c: Horizontal(g24)
    c: Coincident(g25,g0)
    c: Coincident(g25,g12)
    c: Horizontal(g25)
    c: Coincident(g26,g1)
    c: Coincident(g26,g13)
    c: Horizontal(g26)
    c: Coincident(g27,g1)
    c: Coincident(g27,g13)
    c: Horizontal(g27)
    c: Coincident(g28,g2)
    c: Coincident(g28,g14)
    c: Horizontal(g28)
    c: Coincident(g29,g2)
    c: Coincident(g29,g14)
    c: Horizontal(g29)
    c: Coincident(g30,g3)
    c: Coincident(g30,g15)
    c: Horizontal(g30)
    c: Coincident(g31,g3)
    c: Coincident(g31,g15)
    c: Horizontal(g31)
    c: Coincident(g32,g4)
    c: Coincident(g32,g16)
    c: Horizontal(g32)
    c: Coincident(g33,g4)
    c: Coincident(g33,g16)
    c: Horizontal(g33)
    c: Coincident(g34,g5)
    c: Coincident(g34,g17)
    c: Horizontal(g34)
    c: Coincident(g35,g5)
    c: Coincident(g35,g17)
    c: Horizontal(g35)
    c: Coincident(g36,g6)
    c: Coincident(g36,g19)
    c: Horizontal(g36)
    c: Coincident(g37,g6)
    c: Coincident(g37,g19)
    c: Horizontal(g37)
    c: Coincident(g38,g7)
    c: Coincident(g38,g18)
    c: Horizontal(g38)
    c: Coincident(g39,g7)
    c: Coincident(g39,g18)
    c: Horizontal(g39)
    c: Coincident(g40,g8)
    c: Coincident(g40,g20)
    c: Horizontal(g40)
    c: Coincident(g41,g8)
    c: Coincident(g41,g20)
    c: Horizontal(g41)
    c: Coincident(g42,g9)
    c: Coincident(g42,g23)
    c: Horizontal(g42)
    c: Coincident(g43,g9)
    c: Coincident(g43,g23)
    c: Horizontal(g43)
    c: Coincident(g44,g10)
    c: Coincident(g44,g22)
    c: Horizontal(g44)
    c: Coincident(g45,g10)
    c: Coincident(g45,g22)
    c: Horizontal(g45)
    c: Coincident(g46,g11)
    c: Coincident(g46,g21)
    c: Horizontal(g46)
    c: Coincident(g47,g11)
    c: Coincident(g47,g21)
    c: Horizontal(g47)
FEATURE [Part::Extrusion] Extrude061
  Base = -> Sketch070
  Dir = (1,0,0)
  DirMode = 2
  FaceMakerClass = Part::FaceMakerBullseye
  LengthFwd = 23
  LengthRev = 0
  Placement = pos=(-19,0,0) rot=(0,0,1;0rad)
  Solid = true
  Symmetric = false
FEATURE [Part::Fillet] Fillet052  label="removeToCreateVentalationHoles002"
  Base = -> Extrude061
  Edges = <same value as first occurrence — deduplicated (x6 in doc)>
  Placement = pos=(7,0.02,0) rot=(0,0,1;0rad)
FEATURE [Part::MultiFuse] Fusion130  label="bottom013"
  Shapes = -> [Cut054,Cut034]
FEATURE [Part::Cut] Cut055
  Base = -> Fusion130
  Tool = -> Fillet052
FEATURE [Part::Cylinder] Cylinder054
  Angle = 360
  AttacherType = Attacher::AttachEngine3D
  Height = 20
  Placement = pos=(0,0,36.15) rot=(0,0,1;0rad)
  Radius = 4
FEATURE [Sketcher::SketchObject] Sketch071  label="bottomSketch002"
  FullyConstrained = true
  sketch-geometry (32):
    g0: LineSegment StartX=3.3 StartY=-6.03275e-07 StartZ=0 EndX=98 EndY=-6.03275e-07 EndZ=0
    g1: ArcOfCircle CenterX=98 CenterY=19 CenterZ=0 NormalX=0 NormalY=0 NormalZ=1 AngleXU=0 Radius=19 StartAngle=4.71239 EndAngle=5.71103
    g2: LineSegment StartX=6.3 StartY=8 StartZ=0 EndX=3.3 EndY=8 EndZ=0
    g3: LineSegment StartX=3.3 StartY=8 StartZ=0 EndX=3.3 EndY=-6.03275e-07 EndZ=0
    g4: ArcOfCircle CenterX=8.3 CenterY=5 CenterZ=0 NormalX=0 NormalY=0 NormalZ=1 AngleXU=0 Radius=2 StartAngle=3.14159 EndAngle=4.71239
    g5: LineSegment StartX=6.3 StartY=8 StartZ=0 EndX=6.3 EndY=5 EndZ=0
    g6: ArcOfCircle CenterX=98 CenterY=19 CenterZ=0 NormalX=0 NormalY=0 NormalZ=1 AngleXU=0 Radius=12.7 StartAngle=4.71239 EndAngle=6.28319
    g7: LineSegment StartX=94.7 StartY=3 StartZ=0 EndX=8.3 EndY=3 EndZ=0
    g8-g12: Circle x5 (B-spline internal-alignment scaffolding for g13; pole/knot coordinates omitted)
    g13: BSplineCurve PolesCount=5 KnotsCount=3 Degree=3 IsPeriodic=0
    g14: GeomPoint X=98 Y=6.3 Z=0
    g15: GeomPoint X=96.3938 Y=4.71946 Z=0
    g16: GeomPoint X=94.7 Y=3 Z=0
    g17-g23: Circle x7 (B-spline internal-alignment scaffolding for g24; pole/knot coordinates omitted)
    g24: BSplineCurve PolesCount=7 KnotsCount=5 Degree=3 IsPeriodic=0
    g25-g29: GeomPoint x5 (B-spline internal-alignment scaffolding for g24; pole/knot coordinates omitted)
    g30: ArcOfCircle CenterX=98 CenterY=19 CenterZ=0 NormalX=0 NormalY=0 NormalZ=1 AngleXU=0 Radius=15.7 StartAngle=5.81226 EndAngle=6.28319
    g31: LineSegment StartX=110.7 StartY=19 StartZ=0 EndX=113.7 EndY=19 EndZ=0
  constraints (41):
    c: Horizontal(g0)
    c: Coincident(g1,g0)
    c: Block(g1)
    c: Horizontal(g2)
    c: Distance(g2) = 3
    c: Coincident(g3,g2)
    c: Vertical(g3)
    c: Coincident(g3,g0)
    c: Block(g4)
    c: Block(g2)
    c: Coincident(g5,g2)
    c: Coincident(g5,g4)
    c: Vertical(g5)
    c: Coincident(g6,g1)
    c: Block(g6)
    c: Coincident(g7,g4)
    c: Horizontal(g7)
    c: Block(g0)
    c: Block(g7)
    c: Block(g3)
    c: Coincident(g13,g6)
    c: Weight(g8) = 1
    c: Equal(g8, g9-g12) x4
    c: Coincident(g13,g7)
    c: InternalAlignment(g8-g12 -> g13) x5
    c: InternalAlignment(g14,g13)
    c: InternalAlignment(g15,g13)
    c: InternalAlignment(g16,g13)
    c: Block(g13)
    c: Weight(g17) = 1
    c: Equal(g17, g18-g23) x6
    c: Coincident(g24,g1)
    c: InternalAlignment(g17-g23 -> g24) x7
    c: InternalAlignment(g25-g29 -> g24) x5
    c: Block(g24)
    c: Coincident(g30,g24)
    c: Coincident(g31,g6)
    c: Coincident(g31,g30)
    c: Horizontal(g31)
    c: Block(g31)
    c: Block(g30)
FEATURE [Part::Extrusion] Extrude062  label="bottom014"
  Base = -> Sketch071
  Dir = (0,0,1)
  DirMode = 2
  FaceMakerClass = Part::FaceMakerBullseye
  LengthFwd = 71.4
  LengthRev = 0
  Placement = pos=(0,0,0.3) rot=(0,0,1;0rad)
  Solid = true
  Symmetric = false
FEATURE [Part::Fillet] Fillet054
  Base = -> Extrude062
  Edges = 1 edges r=2.4: [Edge17]
FEATURE [Part::Fillet] Fillet055  label="bottom015"
  Base = -> Fillet054
  Edges = 1 edges r=2.4: [Edge36]
FEATURE [Part::Cylinder] Cylinder055
  Angle = 360
  AttacherType = Attacher::AttachEngine3D
  Height = 10
  Placement = pos=(0,0,36.15) rot=(0,0,1;0rad)
  Radius = 4
FEATURE [Part::MultiFuse] Fusion131  label="removeToCreateHoleForPlugHousing002"
  Placement = pos=(70,19,36.15) rot=(0,1,0;1.5708rad)
  Shapes = -> [Cylinder054,Cylinder055]
FEATURE [Part::Cut] Cut056  label="Bottom001"
  Base = -> Fillet055
  Placement = pos=(9,0,0) rot=(0,0,1;0rad)
  Tool = -> Fusion131
FEATURE [Part::Cut] Cut057
  Base = -> Cut055
  Tool = -> Cut056
FEATURE [Sketcher::SketchObject] Sketch072  label="topSketch021"
  FullyConstrained = true
  sketch-geometry (4):
    g0: ArcOfCircle CenterX=105 CenterY=19 CenterZ=0 NormalX=0 NormalY=0 NormalZ=1 AngleXU=0 Radius=20.6155 StartAngle=5.54125 EndAngle=6.28319
    g1: ArcOfCircle CenterX=105 CenterY=19 CenterZ=0 NormalX=0 NormalY=0 NormalZ=1 AngleXU=0 Radius=13 StartAngle=5.54125 EndAngle=6.28319
    g2: LineSegment StartX=118 StartY=19 StartZ=0 EndX=125.616 EndY=19 EndZ=0
    g3: LineSegment StartX=114.583 StartY=10.2157 StartZ=0 EndX=120.197 EndY=5.06982 EndZ=0
  constraints (7):
    c: Block(g0)
    c: Block(g1)
    c: Coincident(g2,g1)
    c: Coincident(g2,g0)
    c: Horizontal(g2)
    c: Coincident(g3,g1)
    c: Coincident(g3,g0)
FEATURE [Part::Extrusion] Extrude063  label="bottomPlugHousingBit003"
  Base = -> Sketch072
  Dir = (0,0,1)
  DirMode = 2
  FaceMakerClass = Part::FaceMakerBullseye
  LengthFwd = 72
  LengthRev = 0
  Solid = true
  Symmetric = false
FEATURE [Part::Cylinder] Cylinder056
  Angle = 360
  AttacherType = Attacher::AttachEngine3D
  Height = 20
  Placement = pos=(0,0,36.15) rot=(0,0,1;0rad)
  Radius = 14.3
FEATURE [Part::Cylinder] Cylinder057
  Angle = 360
  AttacherType = Attacher::AttachEngine3D
  Height = 10
  Placement = pos=(0,0,36.15) rot=(0,0,1;0rad)
  Radius = 4
FEATURE [Part::Box] Box034  label="removeToCreteHoleForPlugHousing047"
  AttacherType = Attacher::AttachEngine3D
  Height = 28.6
  Length = 20
  Placement = pos=(106.15,0,21.7) rot=(0,0,1;0rad)
  Width = 19
FEATURE [Part::Cylinder] Cylinder058
  Angle = 360
  AttacherType = Attacher::AttachEngine3D
  Height = 20
  Placement = pos=(0,0,36.15) rot=(0,0,1;0rad)
  Radius = 14.3
FEATURE [Part::Cylinder] Cylinder059
  Angle = 360
  AttacherType = Attacher::AttachEngine3D
  Height = 10
  Placement = pos=(0,0,36.15) rot=(0,0,1;0rad)
  Radius = 4
FEATURE [Part::MultiFuse] Fusion134  label="removeToCreteHoleForPlugHousing046"
  Placement = pos=(70,19,36) rot=(0,1,0;1.5708rad)
  Shapes = -> [Cylinder058,Cylinder059]
FEATURE [Part::Cylinder] Cylinder060
  Angle = 360
  AttacherType = Attacher::AttachEngine3D
  Height = 20
  Placement = pos=(0,0,36.15) rot=(0,0,1;0rad)
  Radius = 14
FEATURE [Part::Cylinder] Cylinder061
  Angle = 360
  AttacherType = Attacher::AttachEngine3D
  Height = 10
  Placement = pos=(0,0,36.15) rot=(0,0,1;0rad)
  Radius = 4
FEATURE [Part::MultiFuse] Fusion135  label="removeToCreteHoleForPlugHousing048"
  Placement = pos=(70,19,36) rot=(0,1,0;1.5708rad)
  Shapes = -> [Cylinder060,Cylinder061]
FEATURE [Part::Box] Box035  label="removeToCreteHoleForPlugHousing049"
  AttacherType = Attacher::AttachEngine3D
  Height = 28.6
  Length = 20
  Placement = pos=(106.15,0,21.7) rot=(0,0,1;0rad)
  Width = 19
FEATURE [Part::MultiFuse] Fusion133  label="removeToCreteHoleForPlugHousing045"
  Placement = pos=(0,0,-28.3) rot=(0,0,1;0rad)
  Shapes = -> [Box035,Fusion134]
FEATURE [Part::MultiFuse] Fusion138  label="removeToCreteHoleForPlugHousing051"
  Placement = pos=(70,19,36) rot=(0,1,0;1.5708rad)
  Shapes = -> [Cylinder056,Cylinder057]
FEATURE [Part::MultiFuse] Fusion137  label="removeToCreteHoleForPlugHousing050"
  Placement = pos=(0,0,28.3) rot=(0,0,1;0rad)
  Shapes = -> [Box034,Fusion138]
FEATURE [Part::MultiFuse] Fusion132  label="removeToCreatePlugHousingBottomBit002"
  Shapes = -> [Fusion133,Fusion137]
FEATURE [Part::MultiFuse] Fusion136  label="removeToCreatePlugHousingBottomBit003"
  Shapes = -> [Fusion135,Fusion132]
FEATURE [Part::Cut] Cut058  label="bottomPlugHousingBit002"
  Base = -> Extrude063
  Placement = pos=(-0.09,0,0) rot=(0,0,1;0rad)
  Tool = -> Fusion136
FEATURE [Sketcher::SketchObject] Sketch073  label="bottomSketch003"
  FullyConstrained = true
  sketch-geometry (45):
    g0: LineSegment StartX=6.29999 StartY=8 StartZ=0 EndX=3.29999 EndY=8 EndZ=0
    g1: LineSegment StartX=3.29999 StartY=8 StartZ=0 EndX=3.29999 EndY=-6.03275e-07 EndZ=0
    g2: ArcOfCircle CenterX=8.29999 CenterY=5 CenterZ=0 NormalX=0 NormalY=0 NormalZ=1 AngleXU=0 Radius=2 StartAngle=3.14159 EndAngle=4.71239
    g3: LineSegment StartX=6.29999 StartY=8 StartZ=0 EndX=6.29999 EndY=5 EndZ=0
    g4: ArcOfCircle CenterX=105 CenterY=19 CenterZ=0 NormalX=0 NormalY=0 NormalZ=1 AngleXU=0 Radius=12.7 StartAngle=4.71239 EndAngle=5.94289
    g5-g11: Circle x7 (B-spline internal-alignment scaffolding for g12; pole/knot coordinates omitted)
    g12: BSplineCurve PolesCount=7 KnotsCount=5 Degree=3 IsPeriodic=0
    g13-g17: GeomPoint x5 (B-spline internal-alignment scaffolding for g12; pole/knot coordinates omitted)
    g18: ArcOfCircle CenterX=105 CenterY=19 CenterZ=0 NormalX=0 NormalY=0 NormalZ=1 AngleXU=0 Radius=15.7 StartAngle=5.81226 EndAngle=6.28319
    g19: BSplineCurve PolesCount=5 KnotsCount=3 Degree=3 IsPeriodic=0
    g20: LineSegment StartX=8.29999 StartY=3 StartZ=0 EndX=101.7 EndY=3 EndZ=0
    g21: LineSegment StartX=3.29999 StartY=-6.03275e-07 StartZ=0 EndX=105 EndY=-6.03275e-07 EndZ=0
    g22: LineSegment StartX=120.974 StartY=8.71251 StartZ=0 EndX=122.332 EndY=7.83778 EndZ=0
    g23: LineSegment StartX=105 StartY=-6.03274e-07 StartZ=0 EndX=113 EndY=-6.03274e-07 EndZ=0
    g24: ArcOfCircle CenterX=105 CenterY=19 CenterZ=0 NormalX=0 NormalY=0 NormalZ=1 AngleXU=0 Radius=20.6155 StartAngle=5.11091 EndAngle=5.71103
    g25: ArcOfCircle CenterX=117.7 CenterY=19 CenterZ=0 NormalX=0 NormalY=0 NormalZ=1 AngleXU=0 Radius=3 StartAngle=1.2e-15 EndAngle=2.10468
    g26: Circle CenterX=116.345 CenterY=16.3232 CenterZ=0 NormalX=0 NormalY=0 NormalZ=1 AngleXU=0 Radius=1
    g27: Circle CenterX=117.24 CenterY=15.7584 CenterZ=0 NormalX=0 NormalY=0 NormalZ=1 AngleXU=0 Radius=1
    g28: Circle CenterX=116.972 CenterY=14.7612 CenterZ=0 NormalX=0 NormalY=0 NormalZ=1 AngleXU=0 Radius=1
    g29: BSplineCurve PolesCount=3 KnotsCount=2 Degree=2 IsPeriodic=0
    g30: GeomPoint X=116.345 Y=16.3232 Z=0
    g31: GeomPoint X=116.972 Y=14.7612 Z=0
    g32: Circle CenterX=115.828 CenterY=17.157 CenterZ=0 NormalX=0 NormalY=0 NormalZ=1 AngleXU=0 Radius=1
    g33: Circle CenterX=115.841 CenterY=16.639 CenterZ=0 NormalX=0 NormalY=0 NormalZ=1 AngleXU=0 Radius=1
    g34: Circle CenterX=116.345 CenterY=16.3232 CenterZ=0 NormalX=0 NormalY=0 NormalZ=1 AngleXU=0 Radius=1
    g35: BSplineCurve PolesCount=3 KnotsCount=2 Degree=2 IsPeriodic=0
    g36: GeomPoint X=115.828 Y=17.157 Z=0
    g37: GeomPoint X=116.345 Y=16.3232 Z=0
    g38: LineSegment StartX=115.828 StartY=17.157 StartZ=0 EndX=115.828 EndY=20.8307 EndZ=0
    g39: Circle CenterX=115.828 CenterY=20.8307 CenterZ=0 NormalX=0 NormalY=0 NormalZ=1 AngleXU=0 Radius=1
    g40: Circle CenterX=115.831 CenterY=21.3396 CenterZ=0 NormalX=0 NormalY=0 NormalZ=1 AngleXU=0 Radius=1
    g41: Circle CenterX=116.173 CenterY=21.5825 CenterZ=0 NormalX=0 NormalY=0 NormalZ=1 AngleXU=0 Radius=1
    g42: BSplineCurve PolesCount=3 KnotsCount=2 Degree=2 IsPeriodic=0
    g43: GeomPoint X=115.828 Y=20.8307 Z=0
    g44: GeomPoint X=116.173 Y=21.5825 Z=0
  constraints (70):
    c: Horizontal(g0)
    c: Distance(g0) = 3
    c: Coincident(g1,g0)
    c: Vertical(g1)
    c: Block(g2)
    c: Block(g0)
    c: Coincident(g3,g0)
    c: Coincident(g3,g2)
    c: Vertical(g3)
    c: Block(g1)
    c: Block(g4)
    c: Coincident(g19,g4)
    c: Block(g19)
    c: Equal(g5, g6-g11) x6
    c: InternalAlignment(g5-g11 -> g12) x7
    c: InternalAlignment(g13-g17 -> g12) x5
    c: Block(g12)
    c: Coincident(g18,g12)
    c: Block(g18)
    c: Coincident(g20,g2)
    c: Coincident(g20,g19)
    c: Horizontal(g20)
    c: Distance(g20) = 93.4
    c: Coincident(g21,g1)
    c: Horizontal(g21)
    c: Distance(g21) = 101.7
    c: Horizontal(g23)
    c: Distance(g23) = 8
    c: Coincident(g24,g23)
    c: Block(g23)
    c: Coincident(g22,g24)
    c: Block(g24)
    c: Block(g22)
    c: Distance(g22) = 1.61553
    c: Coincident(g25,g18)
    c: Block(g25)
    c: Weight(g26) = 1
    c: Equal(g26,g27)
    c: Equal(g26,g28)
    c: Coincident(g29,g4)
    c: InternalAlignment(g26,g29)
    c: InternalAlignment(g27,g29)
    c: InternalAlignment(g28,g29)
    c: InternalAlignment(g30,g29)
    c: InternalAlignment(g31,g29)
    c: Block(g29)
    c: Weight(g32) = 1
    c: Equal(g32,g33)
    c: Equal(g32,g34)
    c: Coincident(g35,g29)
    c: InternalAlignment(g32,g35)
    c: InternalAlignment(g33,g35)
    c: InternalAlignment(g34,g35)
    c: InternalAlignment(g36,g35)
    c: InternalAlignment(g37,g35)
    c: Block(g35)
    c: Coincident(g38,g35)
    c: Vertical(g38)
    c: Block(g38)
    c: Coincident(g42,g38)
    c: Weight(g39) = 1
    c: Equal(g39,g40)
    c: Equal(g39,g41)
    c: Coincident(g42,g25)
    c: InternalAlignment(g39,g42)
    c: InternalAlignment(g40,g42)
    c: InternalAlignment(g41,g42)
    c: InternalAlignment(g43,g42)
    c: InternalAlignment(g44,g42)
    c: Block(g42)
FEATURE [Part::Extrusion] Extrude064  label="bottom016"
  Base = -> Sketch073
  Dir = (0,0,1)
  DirMode = 2
  FaceMakerClass = Part::FaceMakerBullseye
  LengthFwd = 71.4
  LengthRev = 0
  Placement = pos=(0,0,0.3) rot=(0,0,1;0rad)
  Solid = true
  Symmetric = false
FEATURE [Part::Revolution] Revolve157  label="removeToCreateScrewAndThreadedInsertHole063"
  Angle = 360
  Axis = (0,1,0)
  Base = (0,0,0)
  FaceMakerClass = Part::FaceMakerBullseye
  Placement = pos=(12.5,0,10) rot=(0,0,1;0rad)
  Solid = false
  Source = -> Face141
  Symmetric = false
FEATURE [Sketcher::SketchObject] Sketch074
  FullyConstrained = true
  Placement = pos=(117,19,0) rot=(0.57735,0.57735,0.57735;2.0944rad)
  sketch-geometry (48):
    g0: LineSegment StartX=-49.19 StartY=69.25 StartZ=0 EndX=-49.19 EndY=66.25 EndZ=0
    g1: LineSegment StartX=-49.19 StartY=63.5 StartZ=0 EndX=-49.19 EndY=60.5 EndZ=0
    g2: LineSegment StartX=-49.19 StartY=57.75 StartZ=0 EndX=-49.19 EndY=54.75 EndZ=0
    g3: LineSegment StartX=-49.19 StartY=52 StartZ=0 EndX=-49.19 EndY=49 EndZ=0
    g4: LineSegment StartX=-49.19 StartY=46.25 StartZ=0 EndX=-49.19 EndY=43.25 EndZ=0
    g5: LineSegment StartX=-49.19 StartY=40.5 StartZ=0 EndX=-49.19 EndY=37.5 EndZ=0
    g6: LineSegment StartX=-49.19 StartY=34.5 StartZ=0 EndX=-49.19 EndY=31.5 EndZ=0
    g7: LineSegment StartX=-49.19 StartY=28.75 StartZ=0 EndX=-49.19 EndY=25.75 EndZ=0
    g8: LineSegment StartX=-49.19 StartY=23 StartZ=0 EndX=-49.19 EndY=20 EndZ=0
    g9: LineSegment StartX=-49.19 StartY=17.25 StartZ=0 EndX=-49.19 EndY=14.25 EndZ=0
    g10: LineSegment StartX=-49.19 StartY=11.5 StartZ=0 EndX=-49.19 EndY=8.5 EndZ=0
    g11: LineSegment StartX=-49.19 StartY=5.75 StartZ=0 EndX=-49.19 EndY=2.75 EndZ=0
    g12: ArcOfCircle CenterX=-1.5 CenterY=67.75 CenterZ=0 NormalX=0 NormalY=0 NormalZ=1 AngleXU=0 Radius=1.5 StartAngle=4.71239 EndAngle=7.85398
    g13: ArcOfCircle CenterX=-1.5 CenterY=62 CenterZ=0 NormalX=0 NormalY=0 NormalZ=1 AngleXU=0 Radius=1.5 StartAngle=4.71239 EndAngle=7.85398
    g14: ArcOfCircle CenterX=-1.5 CenterY=56.25 CenterZ=0 NormalX=0 NormalY=0 NormalZ=1 AngleXU=0 Radius=1.5 StartAngle=4.71239 EndAngle=7.85398
    g15: ArcOfCircle CenterX=-11.49 CenterY=50.5 CenterZ=0 NormalX=0 NormalY=0 NormalZ=1 AngleXU=0 Radius=1.5 StartAngle=4.71239 EndAngle=7.85398
    g16: ArcOfCircle CenterX=-16.28 CenterY=44.75 CenterZ=0 NormalX=0 NormalY=0 NormalZ=1 AngleXU=0 Radius=1.5 StartAngle=4.71239 EndAngle=7.85398
    g17: ArcOfCircle CenterX=-18.2337 CenterY=39 CenterZ=0 NormalX=0 NormalY=0 NormalZ=1 AngleXU=0 Radius=1.5 StartAngle=4.71485 EndAngle=7.85398
    g18: ArcOfCircle CenterX=-16.2837 CenterY=27.25 CenterZ=0 NormalX=0 NormalY=0 NormalZ=1 AngleXU=0 Radius=1.5 StartAngle=4.71485 EndAngle=7.85398
    g19: ArcOfCircle CenterX=-18.2337 CenterY=33 CenterZ=0 NormalX=0 NormalY=0 NormalZ=1 AngleXU=0 Radius=1.5 StartAngle=4.71485 EndAngle=7.85398
    g20: ArcOfCircle CenterX=-11.49 CenterY=21.5 CenterZ=0 NormalX=0 NormalY=0 NormalZ=1 AngleXU=0 Radius=1.5 StartAngle=4.71239 EndAngle=7.85398
    g21: ArcOfCircle CenterX=-1.5 CenterY=4.25 CenterZ=0 NormalX=0 NormalY=0 NormalZ=1 AngleXU=0 Radius=1.5 StartAngle=4.71239 EndAngle=7.85398
    g22: ArcOfCircle CenterX=-1.5 CenterY=10 CenterZ=0 NormalX=0 NormalY=0 NormalZ=1 AngleXU=0 Radius=1.5 StartAngle=4.71239 EndAngle=7.85398
    g23: ArcOfCircle CenterX=-1.5 CenterY=15.75 CenterZ=0 NormalX=0 NormalY=0 NormalZ=1 AngleXU=0 Radius=1.5 StartAngle=4.71239 EndAngle=7.85398
    g24: LineSegment StartX=-49.19 StartY=69.25 StartZ=0 EndX=-1.5 EndY=69.25 EndZ=0
    g25: LineSegment StartX=-49.19 StartY=66.25 StartZ=0 EndX=-1.5 EndY=66.25 EndZ=0
    g26: LineSegment StartX=-49.19 StartY=63.5 StartZ=0 EndX=-1.5 EndY=63.5 EndZ=0
    g27: LineSegment StartX=-49.19 StartY=60.5 StartZ=0 EndX=-1.5 EndY=60.5 EndZ=0
    g28: LineSegment StartX=-49.19 StartY=57.75 StartZ=0 EndX=-1.5 EndY=57.75 EndZ=0
    g29: LineSegment StartX=-49.19 StartY=54.75 StartZ=0 EndX=-1.5 EndY=54.75 EndZ=0
    g30: LineSegment StartX=-49.19 StartY=52 StartZ=0 EndX=-11.49 EndY=52 EndZ=0
    g31: LineSegment StartX=-49.19 StartY=49 StartZ=0 EndX=-11.49 EndY=49 EndZ=0
    g32: LineSegment StartX=-49.19 StartY=46.25 StartZ=0 EndX=-16.28 EndY=46.25 EndZ=0
    g33: LineSegment StartX=-49.19 StartY=43.25 StartZ=0 EndX=-16.28 EndY=43.25 EndZ=0
    g34: LineSegment StartX=-49.19 StartY=40.5 StartZ=0 EndX=-18.2337 EndY=40.5 EndZ=0
    g35: LineSegment StartX=-49.19 StartY=37.5 StartZ=0 EndX=-18.23 EndY=37.5 EndZ=0
    g36: LineSegment StartX=-49.19 StartY=34.5 StartZ=0 EndX=-18.2337 EndY=34.5 EndZ=0
    g37: LineSegment StartX=-49.19 StartY=31.5 StartZ=0 EndX=-18.23 EndY=31.5 EndZ=0
    g38: LineSegment StartX=-49.19 StartY=28.75 StartZ=0 EndX=-16.2837 EndY=28.75 EndZ=0
    g39: LineSegment StartX=-49.19 StartY=25.75 StartZ=0 EndX=-16.28 EndY=25.75 EndZ=0
    g40: LineSegment StartX=-49.19 StartY=23 StartZ=0 EndX=-11.49 EndY=23 EndZ=0
    g41: LineSegment StartX=-49.19 StartY=20 StartZ=0 EndX=-11.49 EndY=20 EndZ=0
    g42: LineSegment StartX=-49.19 StartY=17.25 StartZ=0 EndX=-1.5 EndY=17.25 EndZ=0
    g43: LineSegment StartX=-49.19 StartY=14.25 StartZ=0 EndX=-1.5 EndY=14.25 EndZ=0
    g44: LineSegment StartX=-49.19 StartY=11.5 StartZ=0 EndX=-1.5 EndY=11.5 EndZ=0
    g45: LineSegment StartX=-49.19 StartY=8.5 StartZ=0 EndX=-1.5 EndY=8.5 EndZ=0
    g46: LineSegment StartX=-49.19 StartY=5.75 StartZ=0 EndX=-1.5 EndY=5.75 EndZ=0
    g47: LineSegment StartX=-49.19 StartY=2.75 StartZ=0 EndX=-1.5 EndY=2.75 EndZ=0
  constraints (120):
    c: Vertical(g0)
    c: Distance(g0) = 3
    c: Block(g0)
    c: Vertical(g1)
    c: Distance(g1) = 3
    c: Vertical(g2)
    c: Equal(g0,g2) = 3
    c: Block(g2)
    c: Vertical(g3)
    c: Equal(g1,g3) = 3
    c: Vertical(g4)
    c: Equal(g0,g4) = 3
    c: Block(g4)
    c: Vertical(g5)
    c: Equal(g1,g5) = 3
    c: Vertical(g6)
    c: Equal(g0,g6) = 3
    c: Block(g6)
    c: Vertical(g7)
    c: Equal(g1,g7) = 3
    c: Vertical(g8)
    c: Equal(g0,g8) = 3
    c: Block(g8)
    c: Vertical(g9)
    c: Equal(g1,g9) = 3
    c: Vertical(g10)
    c: Equal(g0,g10) = 3
    c: Block(g10)
    c: Vertical(g11)
    c: Equal(g1,g11) = 3
    c: Block(g12)
    c: Block(g13)
    c: Block(g14)
    c: Block(g15)
    c: Block(g16)
    c: Block(g17)
    c: Block(g18)
    c: Block(g19)
    c: Block(g20)
    c: Block(g21)
    c: Block(g22)
    c: Block(g23)
    c: Block(g11)
    c: Block(g9)
    c: Block(g7)
    c: Block(g5)
    c: Block(g3)
    c: Block(g1)
    c: Coincident(g24,g0)
    c: Coincident(g24,g12)
    c: Horizontal(g24)
    c: Coincident(g25,g0)
    c: Coincident(g25,g12)
    c: Horizontal(g25)
    c: Coincident(g26,g1)
    c: Coincident(g26,g13)
    c: Horizontal(g26)
    c: Coincident(g27,g1)
    c: Coincident(g27,g13)
    c: Horizontal(g27)
    c: Coincident(g28,g2)
    c: Coincident(g28,g14)
    c: Horizontal(g28)
    c: Coincident(g29,g2)
    c: Coincident(g29,g14)
    c: Horizontal(g29)
    c: Coincident(g30,g3)
    c: Coincident(g30,g15)
    c: Horizontal(g30)
    c: Coincident(g31,g3)
    c: Coincident(g31,g15)
    c: Horizontal(g31)
    c: Coincident(g32,g4)
    c: Coincident(g32,g16)
    c: Horizontal(g32)
    c: Coincident(g33,g4)
    c: Coincident(g33,g16)
    c: Horizontal(g33)
    c: Coincident(g34,g5)
    c: Coincident(g34,g17)
    c: Horizontal(g34)
    c: Coincident(g35,g5)
    c: Coincident(g35,g17)
    c: Horizontal(g35)
    c: Coincident(g36,g6)
    c: Coincident(g36,g19)
    c: Horizontal(g36)
    c: Coincident(g37,g6)
    c: Coincident(g37,g19)
    c: Horizontal(g37)
    c: Coincident(g38,g7)
    c: Coincident(g38,g18)
    c: Horizontal(g38)
    c: Coincident(g39,g7)
    c: Coincident(g39,g18)
    c: Horizontal(g39)
    c: Coincident(g40,g8)
    c: Coincident(g40,g20)
    c: Horizontal(g40)
    c: Coincident(g41,g8)
    c: Coincident(g41,g20)
    c: Horizontal(g41)
    c: Coincident(g42,g9)
    c: Coincident(g42,g23)
    c: Horizontal(g42)
    c: Coincident(g43,g9)
    c: Coincident(g43,g23)
    c: Horizontal(g43)
    c: Coincident(g44,g10)
    c: Coincident(g44,g22)
    c: Horizontal(g44)
    c: Coincident(g45,g10)
    c: Coincident(g45,g22)
    c: Horizontal(g45)
    c: Coincident(g46,g11)
    c: Coincident(g46,g21)
    c: Horizontal(g46)
    c: Coincident(g47,g11)
    c: Coincident(g47,g21)
    c: Horizontal(g47)
FEATURE [Part::Extrusion] Extrude065
  Base = -> Sketch074
  Dir = (1,0,0)
  DirMode = 2
  FaceMakerClass = Part::FaceMakerBullseye
  LengthFwd = 23
  LengthRev = 0
  Placement = pos=(-19,0,0) rot=(0,0,1;0rad)
  Solid = true
  Symmetric = false
FEATURE [Part::Fillet] Fillet056  label="removeToCreateVentalationHoles003"
  Base = -> Extrude065
  Edges = <same value as first occurrence — deduplicated (x6 in doc)>
  Placement = pos=(7,0.02,0) rot=(0,0,1;0rad)
FEATURE [Part::Revolution] Revolve158  label="removeToCreateScrewAndThreadedInsertHole065"
  Angle = 360
  Axis = (0,1,0)
  Base = (0,0,0)
  FaceMakerClass = Part::FaceMakerBullseye
  Placement = pos=(12.5,0,62) rot=(0,0,1;0rad)
  Solid = false
  Source = -> Face146
  Symmetric = false
FEATURE [Part::Revolution] Revolve159  label="removeToCreateScrewAndThreadedInsertHole066"
  Angle = 360
  Axis = (0,1,0)
  Base = (0,0,0)
  FaceMakerClass = Part::FaceMakerBullseye
  Placement = pos=(89.5,0,68.5) rot=(0,0,1;0rad)
  Solid = false
  Source = -> Face143
  Symmetric = false
FEATURE [Part::Revolution] Revolve160  label="removeToCreateScrewAndThreadedInsertHole067"
  Angle = 360
  Axis = (0,1,0)
  Base = (0,0,0)
  FaceMakerClass = Part::FaceMakerBullseye
  Placement = pos=(89.5,0,3.5) rot=(0,0,1;0rad)
  Solid = false
  Source = -> Face142
  Symmetric = false
FEATURE [Part::Revolution] Revolve161  label="removeToCreateScrewAndThreadedInsertHole068"
  Angle = 360
  Axis = (0,1,0)
  Base = (0,0,0)
  FaceMakerClass = Part::FaceMakerBullseye
  Placement = pos=(109.5,4.7,3.5) rot=(0,0,1;0rad)
  Solid = false
  Source = -> Face145
  Symmetric = false
FEATURE [Part::Revolution] Revolve162  label="removeToCreateScrewAndThreadedInsertHole069"
  Angle = 360
  Axis = (0,1,0)
  Base = (0,0,0)
  FaceMakerClass = Part::FaceMakerBullseye
  Placement = pos=(109.5,4.7,68.5) rot=(0,0,1;0rad)
  Solid = false
  Source = -> Face144
  Symmetric = false
FEATURE [Part::MultiFuse] Fusion141  label="removeToCreateScrewAndThreadedInsertHole064"
  Shapes = -> [Revolve162,Revolve161,Revolve160,Revolve159,Revolve158,Revolve157]
FEATURE [Part::Cylinder] Cylinder062
  Angle = 360
  AttacherType = Attacher::AttachEngine3D
  Height = 20
  Placement = pos=(0,0,36.15) rot=(0,0,1;0rad)
  Radius = 14
FEATURE [Part::Cylinder] Cylinder063
  Angle = 360
  AttacherType = Attacher::AttachEngine3D
  Height = 10
  Placement = pos=(0,0,36.15) rot=(0,0,1;0rad)
  Radius = 4
FEATURE [Part::MultiFuse] Fusion139  label="removeToCreteHoleForPlugHousing052"
  Placement = pos=(70,19,36) rot=(0,1,0;1.5708rad)
  Shapes = -> [Cylinder062,Cylinder063]
FEATURE [Part::Cut] Cut060  label="bottom017"
  Base = -> Extrude064
  Tool = -> Fusion139
FEATURE [Part::Cut] Cut061  label="bottom019"
  Base = -> Cut060
  Tool = -> Fusion141
FEATURE [Part::MultiFuse] Fusion140  label="bottom018"
  Shapes = -> [Cut061,Cut058]
FEATURE [Part::Cut] Cut059  label="bottom020"
  Base = -> Fusion140
  Tool = -> Fillet056
FEATURE [Part::Box] Box036  label="Cube021"
  AttacherType = Attacher::AttachEngine3D
  Height = 80
  Length = 26
  Placement = pos=(0,-1,-5) rot=(0,0,1;0rad)
  Width = 11
FEATURE [Part::Cut] Cut062  label="removeFromBottom002"
  Base = -> Cut057
  Tool = -> Box036
FEATURE [Part::Cut] Cut063
  Base = -> Cut059
  Tool = -> Cut062
